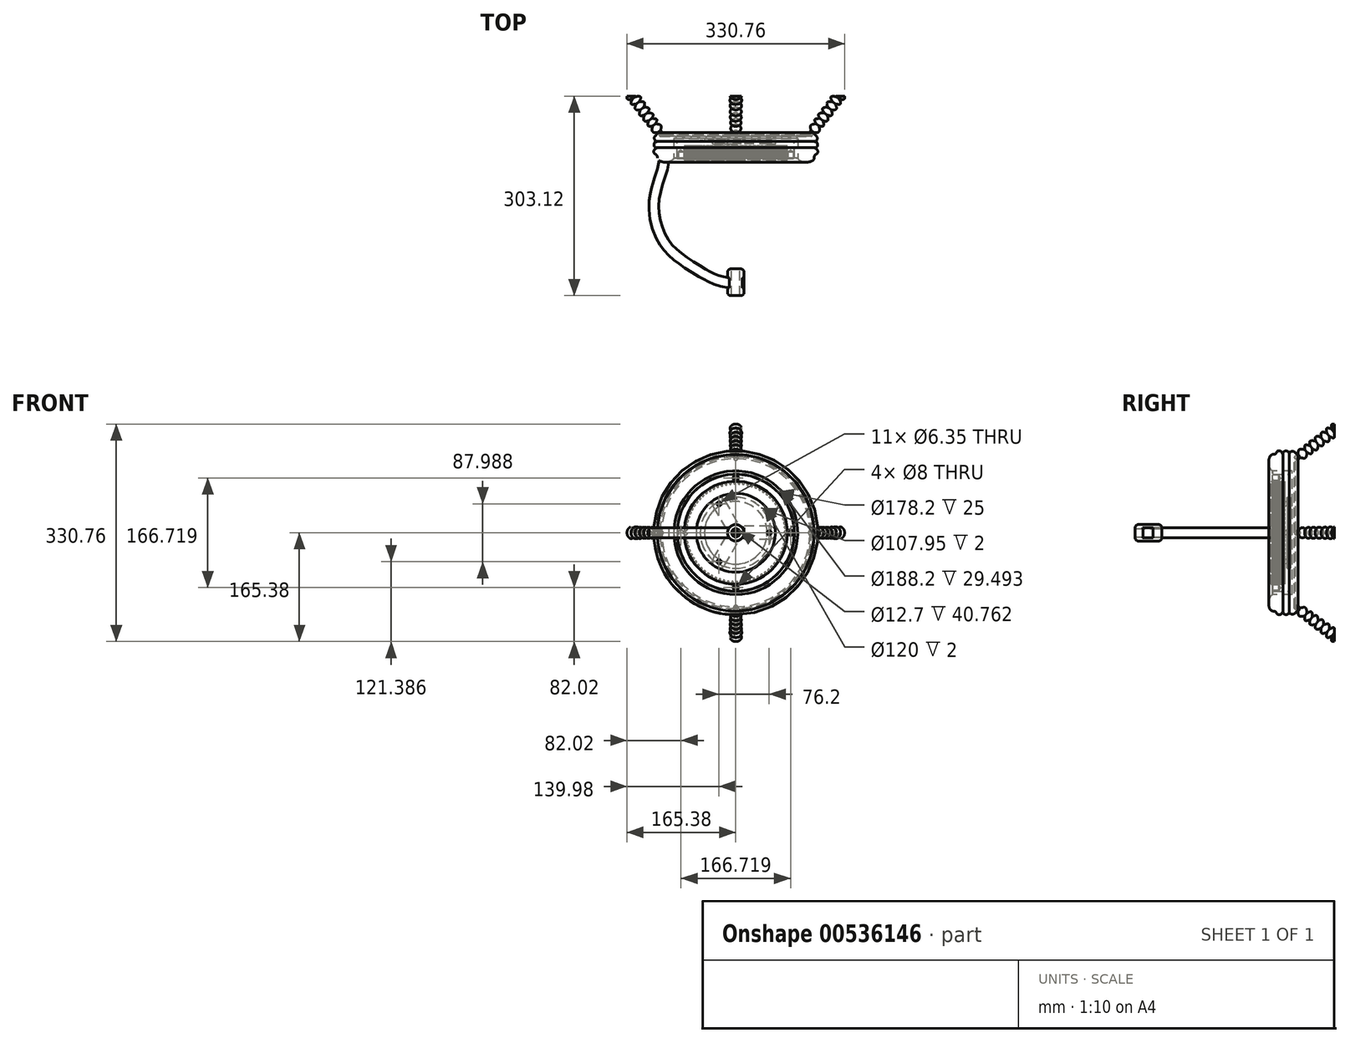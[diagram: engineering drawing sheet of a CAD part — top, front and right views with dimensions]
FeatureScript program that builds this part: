
annotation { "Feature Type Name" : "Feature", "Feature Type Description" : "" }
export const myFeature = defineFeature(function(context is Context, id is Id, definition is map)
    precondition{}
    {
        {
            var Q0;
            Q0=qCreatedBy(makeId("Front.planeOp"),FACE);
            var sketch = newSketch(context, id + "F0", { "sketchPlane" : qUnion([Q0])});
            skArc(sketch, "E0", {"start": v(-4.1, 78.2) * mm, "mid": v(-5.07, 78.15) * mm, "end": v(-6.03, 78.08) * mm});
            skArc(sketch, "E1.MirrorCS", {"start": v(-0.05, 76.06) * mm, "mid": v(-0.38, 75.29) * mm, "end": v(-0.74, 74.53) * mm});
            skLineSegment(sketch, "E2.MirrorCS", {"start": v(0, 76.35) * mm, "end": v(0, 77.53) * mm});
            skLineSegment(sketch, "E3.MirrorCS", {"start": v(-1.45, 74.1) * mm, "end": v(-1.7, 74.1) * mm});
            skLineSegment(sketch, "E4.MirrorCS", {"start": v(-1.97, 74.1) * mm, "end": v(-1.7, 74.1) * mm});
            skArc(sketch, "E5.MirrorCS", {"start": v(-3.28, 76.13) * mm, "mid": v(-2.99, 75.34) * mm, "end": v(-2.66, 74.57) * mm});
            skLineSegment(sketch, "E6.MirrorCS", {"start": v(-3.32, 76.42) * mm, "end": v(-3.28, 77.39) * mm});
            skPoint(sketch, "E7.end.orphan", {"position": v(-1.7, 78.3) * mm});
            skPoint(sketch, "E7.start.orphan", {"position": v(-0.96, 78.31) * mm});
            skPoint(sketch, "E8.MirrorCS.start.orphan", {"position": v(-2.45, 78.28) * mm});
            skPoint(sketch, "E9.orphan", {"position": v(-3.32, 76.13) * mm});
            skPoint(sketch, "E10.MirrorCS.end.orphan", {"position": v(-3.2, 73.49) * mm});
            skPoint(sketch, "E11.end.orphan", {"position": v(0, 73.56) * mm});
            skPoint(sketch, "E12.orphan", {"position": v(-3.2, 78.91) * mm});
            skPoint(sketch, "E13.orphan", {"position": v(0, 78.84) * mm});
            skPoint(sketch, "E14.start.orphan", {"position": v(0, 76.2) * mm});
            skPoint(sketch, "E15.visualSharp", {"position": v(-2.45, 74.12) * mm});
            skArc(sketch, "E15.filletArc", {"start": v(-2.48, 74.18) * mm, "mid": v(-2.44, 74.14) * mm, "end": v(-2.4, 74.12) * mm});
            skArc(sketch, "E16.filletArc", {"start": v(-0.05, 76.06) * mm, "mid": v(-0.01, 76.2) * mm, "end": v(0, 76.35) * mm});
            skPoint(sketch, "E17.visualSharp", {"position": v(-3.32, 76.27) * mm});
            skArc(sketch, "E17.filletArc", {"start": v(-3.32, 76.42) * mm, "mid": v(-3.3, 76.27) * mm, "end": v(-3.28, 76.13) * mm});
            skPoint(sketch, "E18.visualSharp", {"position": v(-0.96, 74.09) * mm});
            skArc(sketch, "E18.filletArc", {"start": v(-1.45, 74.1) * mm, "mid": v(-1.03, 74.21) * mm, "end": v(-0.74, 74.53) * mm});
            skArc(sketch, "E19.filletArc", {"start": v(-2.66, 74.57) * mm, "mid": v(-2.38, 74.24) * mm, "end": v(-1.97, 74.1) * mm});
            skPoint(sketch, "E20.visualSharp", {"position": v(-3.24, 78.25) * mm});
            skArc(sketch, "E20.filletArc", {"start": v(-3.28, 77.39) * mm, "mid": v(-3.5, 77.98) * mm, "end": v(-4.1, 78.2) * mm});
            skPoint(sketch, "E21.visualSharp", {"position": v(0, 78.32) * mm});
            skArc(sketch, "E21.filletArc", {"start": v(0.8, 78.31) * mm, "mid": v(0.23, 78.08) * mm, "end": v(0, 77.53) * mm});
            skCircle(sketch, "E22", {"center": v(0, 0) * mm, "radius": 88.9 * mm});
            skArc(sketch, "E23.1.0", {"start": v(-10, 76.8) * mm, "mid": v(-10.3, 77.38) * mm, "end": v(-10.9, 77.55) * mm});
            skLineSegment(sketch, "E23.1.1", {"start": v(-9.97, 75.84) * mm, "end": v(-10, 76.8) * mm});
            skArc(sketch, "E23.1.2", {"start": v(-9.97, 75.84) * mm, "mid": v(-9.94, 75.7) * mm, "end": v(-9.9, 75.55) * mm});
            skArc(sketch, "E23.1.3", {"start": v(-9.9, 75.55) * mm, "mid": v(-9.54, 74.8) * mm, "end": v(-9.15, 74.06) * mm});
            skArc(sketch, "E23.1.4", {"start": v(-9.15, 74.06) * mm, "mid": v(-8.84, 73.75) * mm, "end": v(-8.42, 73.65) * mm});
            skLineSegment(sketch, "E23.1.5", {"start": v(-8.42, 73.65) * mm, "end": v(-8.16, 73.67) * mm});
            skLineSegment(sketch, "E23.1.6", {"start": v(-7.9, 73.69) * mm, "end": v(-8.16, 73.67) * mm});
            skArc(sketch, "E23.1.7", {"start": v(-7.9, 73.69) * mm, "mid": v(-7.5, 73.84) * mm, "end": v(-7.23, 74.18) * mm});
            skArc(sketch, "E23.1.8", {"start": v(-6.68, 75.77) * mm, "mid": v(-6.94, 74.97) * mm, "end": v(-7.23, 74.18) * mm});
            skArc(sketch, "E23.1.9", {"start": v(-6.68, 75.77) * mm, "mid": v(-6.66, 75.9) * mm, "end": v(-6.65, 76.06) * mm});
            skLineSegment(sketch, "E23.1.10", {"start": v(-6.65, 76.06) * mm, "end": v(-6.76, 77.23) * mm});
            skArc(sketch, "E23.1.11", {"start": v(-6.03, 78.08) * mm, "mid": v(-6.57, 77.8) * mm, "end": v(-6.76, 77.23) * mm});
            skArc(sketch, "E23.2.0", {"start": v(-16.66, 75.64) * mm, "mid": v(-17, 76.19) * mm, "end": v(-17.62, 76.3) * mm});
            skLineSegment(sketch, "E23.2.1", {"start": v(-16.54, 74.68) * mm, "end": v(-16.66, 75.64) * mm});
            skArc(sketch, "E23.2.2", {"start": v(-16.54, 74.68) * mm, "mid": v(-16.5, 74.54) * mm, "end": v(-16.45, 74.4) * mm});
            skArc(sketch, "E23.2.3", {"start": v(-16.45, 74.4) * mm, "mid": v(-16.02, 73.68) * mm, "end": v(-15.57, 72.98) * mm});
            skArc(sketch, "E23.2.4", {"start": v(-15.57, 72.98) * mm, "mid": v(-15.24, 72.7) * mm, "end": v(-14.8, 72.64) * mm});
            skLineSegment(sketch, "E23.2.5", {"start": v(-14.8, 72.64) * mm, "end": v(-14.55, 72.68) * mm});
            skLineSegment(sketch, "E23.2.6", {"start": v(-14.3, 72.72) * mm, "end": v(-14.55, 72.68) * mm});
            skArc(sketch, "E23.2.7", {"start": v(-14.3, 72.72) * mm, "mid": v(-13.9, 72.9) * mm, "end": v(-13.67, 73.27) * mm});
            skArc(sketch, "E23.2.8", {"start": v(-13.26, 74.9) * mm, "mid": v(-13.45, 74.08) * mm, "end": v(-13.67, 73.27) * mm});
            skArc(sketch, "E23.2.9", {"start": v(-13.26, 74.9) * mm, "mid": v(-13.25, 75.04) * mm, "end": v(-13.26, 75.19) * mm});
            skLineSegment(sketch, "E23.2.10", {"start": v(-13.26, 75.19) * mm, "end": v(-13.46, 76.35) * mm});
            skArc(sketch, "E23.2.11", {"start": v(-12.82, 77.26) * mm, "mid": v(-13.33, 76.94) * mm, "end": v(-13.46, 76.35) * mm});
            skArc(sketch, "E23.3.0", {"start": v(-23.2, 73.9) * mm, "mid": v(-23.57, 74.42) * mm, "end": v(-24.2, 74.48) * mm});
            skLineSegment(sketch, "E23.3.1", {"start": v(-22.98, 72.96) * mm, "end": v(-23.2, 73.9) * mm});
            skArc(sketch, "E23.3.2", {"start": v(-22.98, 72.96) * mm, "mid": v(-22.94, 72.82) * mm, "end": v(-22.87, 72.69) * mm});
            skArc(sketch, "E23.3.3", {"start": v(-22.87, 72.69) * mm, "mid": v(-22.38, 72) * mm, "end": v(-21.87, 71.34) * mm});
            skArc(sketch, "E23.3.4", {"start": v(-21.87, 71.34) * mm, "mid": v(-21.52, 71.1) * mm, "end": v(-21.08, 71.07) * mm});
            skLineSegment(sketch, "E23.3.5", {"start": v(-21.08, 71.07) * mm, "end": v(-20.83, 71.13) * mm});
            skLineSegment(sketch, "E23.3.6", {"start": v(-20.58, 71.2) * mm, "end": v(-20.83, 71.13) * mm});
            skArc(sketch, "E23.3.7", {"start": v(-20.58, 71.2) * mm, "mid": v(-20.2, 71.42) * mm, "end": v(-20, 71.8) * mm});
            skArc(sketch, "E23.3.8", {"start": v(-19.74, 73.45) * mm, "mid": v(-19.85, 72.62) * mm, "end": v(-20, 71.8) * mm});
            skArc(sketch, "E23.3.9", {"start": v(-19.74, 73.45) * mm, "mid": v(-19.74, 73.6) * mm, "end": v(-19.76, 73.75) * mm});
            skLineSegment(sketch, "E23.3.10", {"start": v(-19.76, 73.75) * mm, "end": v(-20.07, 74.88) * mm});
            skArc(sketch, "E23.3.11", {"start": v(-19.5, 75.85) * mm, "mid": v(-19.98, 75.48) * mm, "end": v(-20.07, 74.88) * mm});
            skArc(sketch, "E23.4.0", {"start": v(-29.55, 71.6) * mm, "mid": v(-29.97, 72.08) * mm, "end": v(-30.6, 72.09) * mm});
            skLineSegment(sketch, "E23.4.1", {"start": v(-29.25, 70.68) * mm, "end": v(-29.55, 71.6) * mm});
            skArc(sketch, "E23.4.2", {"start": v(-29.25, 70.68) * mm, "mid": v(-29.2, 70.54) * mm, "end": v(-29.12, 70.42) * mm});
            skArc(sketch, "E23.4.3", {"start": v(-29.12, 70.42) * mm, "mid": v(-28.57, 69.78) * mm, "end": v(-28, 69.17) * mm});
            skArc(sketch, "E23.4.4", {"start": v(-28, 69.17) * mm, "mid": v(-27.63, 68.95) * mm, "end": v(-27.2, 68.96) * mm});
            skLineSegment(sketch, "E23.4.5", {"start": v(-27.2, 68.96) * mm, "end": v(-26.95, 69.05) * mm});
            skLineSegment(sketch, "E23.4.6", {"start": v(-26.7, 69.13) * mm, "end": v(-26.95, 69.05) * mm});
            skArc(sketch, "E23.4.7", {"start": v(-26.7, 69.13) * mm, "mid": v(-26.35, 69.38) * mm, "end": v(-26.18, 69.78) * mm});
            skArc(sketch, "E23.4.8", {"start": v(-26.07, 71.45) * mm, "mid": v(-26.1, 70.62) * mm, "end": v(-26.18, 69.78) * mm});
            skArc(sketch, "E23.4.9", {"start": v(-26.07, 71.45) * mm, "mid": v(-26.08, 71.6) * mm, "end": v(-26.11, 71.74) * mm});
            skLineSegment(sketch, "E23.4.10", {"start": v(-26.11, 71.74) * mm, "end": v(-26.52, 72.85) * mm});
            skArc(sketch, "E23.4.11", {"start": v(-26.04, 73.86) * mm, "mid": v(-26.49, 73.46) * mm, "end": v(-26.52, 72.85) * mm});
            skArc(sketch, "E23.5.0", {"start": v(-35.67, 68.75) * mm, "mid": v(-36.14, 69.2) * mm, "end": v(-36.77, 69.15) * mm});
            skLineSegment(sketch, "E23.5.1", {"start": v(-35.3, 67.86) * mm, "end": v(-35.67, 68.75) * mm});
            skArc(sketch, "E23.5.2", {"start": v(-35.3, 67.86) * mm, "mid": v(-35.23, 67.73) * mm, "end": v(-35.14, 67.61) * mm});
            skArc(sketch, "E23.5.3", {"start": v(-35.14, 67.61) * mm, "mid": v(-34.55, 67.02) * mm, "end": v(-33.93, 66.46) * mm});
            skArc(sketch, "E23.5.4", {"start": v(-33.93, 66.46) * mm, "mid": v(-33.53, 66.28) * mm, "end": v(-33.1, 66.33) * mm});
            skLineSegment(sketch, "E23.5.5", {"start": v(-33.1, 66.33) * mm, "end": v(-32.86, 66.43) * mm});
            skLineSegment(sketch, "E23.5.6", {"start": v(-32.63, 66.54) * mm, "end": v(-32.86, 66.43) * mm});
            skArc(sketch, "E23.5.7", {"start": v(-32.63, 66.54) * mm, "mid": v(-32.3, 66.82) * mm, "end": v(-32.16, 67.24) * mm});
            skArc(sketch, "E23.5.8", {"start": v(-32.2, 68.91) * mm, "mid": v(-32.16, 68.07) * mm, "end": v(-32.16, 67.24) * mm});
            skArc(sketch, "E23.5.9", {"start": v(-32.2, 68.91) * mm, "mid": v(-32.22, 69.06) * mm, "end": v(-32.27, 69.2) * mm});
            skLineSegment(sketch, "E23.5.10", {"start": v(-32.27, 69.2) * mm, "end": v(-32.76, 70.26) * mm});
            skArc(sketch, "E23.5.11", {"start": v(-32.38, 71.31) * mm, "mid": v(-32.79, 70.87) * mm, "end": v(-32.76, 70.26) * mm});
            skArc(sketch, "E23.6.0", {"start": v(-41.53, 65.38) * mm, "mid": v(-42.03, 65.78) * mm, "end": v(-42.66, 65.68) * mm});
            skLineSegment(sketch, "E23.6.1", {"start": v(-41.08, 64.52) * mm, "end": v(-41.53, 65.38) * mm});
            skArc(sketch, "E23.6.2", {"start": v(-41.08, 64.52) * mm, "mid": v(-41, 64.4) * mm, "end": v(-40.9, 64.3) * mm});
            skArc(sketch, "E23.6.3", {"start": v(-40.9, 64.3) * mm, "mid": v(-40.26, 63.76) * mm, "end": v(-39.6, 63.25) * mm});
            skArc(sketch, "E23.6.4", {"start": v(-39.6, 63.25) * mm, "mid": v(-39.18, 63.1) * mm, "end": v(-38.76, 63.2) * mm});
            skLineSegment(sketch, "E23.6.5", {"start": v(-38.76, 63.2) * mm, "end": v(-38.53, 63.32) * mm});
            skLineSegment(sketch, "E23.6.6", {"start": v(-38.3, 63.44) * mm, "end": v(-38.53, 63.32) * mm});
            skArc(sketch, "E23.6.7", {"start": v(-38.3, 63.44) * mm, "mid": v(-38, 63.75) * mm, "end": v(-37.9, 64.18) * mm});
            skArc(sketch, "E23.6.8", {"start": v(-38.08, 65.84) * mm, "mid": v(-37.97, 65.01) * mm, "end": v(-37.9, 64.18) * mm});
            skArc(sketch, "E23.6.9", {"start": v(-38.08, 65.84) * mm, "mid": v(-38.11, 65.99) * mm, "end": v(-38.17, 66.12) * mm});
            skLineSegment(sketch, "E23.6.10", {"start": v(-38.17, 66.12) * mm, "end": v(-38.76, 67.14) * mm});
            skArc(sketch, "E23.6.11", {"start": v(-38.47, 68.22) * mm, "mid": v(-38.84, 67.74) * mm, "end": v(-38.76, 67.14) * mm});
            skArc(sketch, "E23.7.0", {"start": v(-47.07, 61.51) * mm, "mid": v(-47.6, 61.87) * mm, "end": v(-48.22, 61.71) * mm});
            skLineSegment(sketch, "E23.7.1", {"start": v(-46.55, 60.7) * mm, "end": v(-47.07, 61.51) * mm});
            skArc(sketch, "E23.7.2", {"start": v(-46.55, 60.7) * mm, "mid": v(-46.46, 60.58) * mm, "end": v(-46.35, 60.48) * mm});
            skArc(sketch, "E23.7.3", {"start": v(-46.35, 60.48) * mm, "mid": v(-45.66, 60) * mm, "end": v(-44.95, 59.56) * mm});
            skArc(sketch, "E23.7.4", {"start": v(-44.95, 59.56) * mm, "mid": v(-44.53, 59.45) * mm, "end": v(-44.12, 59.58) * mm});
            skLineSegment(sketch, "E23.7.5", {"start": v(-44.12, 59.58) * mm, "end": v(-43.9, 59.72) * mm});
            skLineSegment(sketch, "E23.7.6", {"start": v(-43.69, 59.86) * mm, "end": v(-43.9, 59.72) * mm});
            skArc(sketch, "E23.7.7", {"start": v(-43.69, 59.86) * mm, "mid": v(-43.4, 60.2) * mm, "end": v(-43.35, 60.63) * mm});
            skArc(sketch, "E23.7.8", {"start": v(-43.67, 62.27) * mm, "mid": v(-43.5, 61.46) * mm, "end": v(-43.35, 60.63) * mm});
            skArc(sketch, "E23.7.9", {"start": v(-43.67, 62.27) * mm, "mid": v(-43.72, 62.41) * mm, "end": v(-43.8, 62.54) * mm});
            skLineSegment(sketch, "E23.7.10", {"start": v(-43.8, 62.54) * mm, "end": v(-44.47, 63.5) * mm});
            skArc(sketch, "E23.7.11", {"start": v(-44.27, 64.6) * mm, "mid": v(-44.6, 64.1) * mm, "end": v(-44.47, 63.5) * mm});
            skArc(sketch, "E23.8.0", {"start": v(-52.25, 57.18) * mm, "mid": v(-52.81, 57.48) * mm, "end": v(-53.41, 57.27) * mm});
            skLineSegment(sketch, "E23.8.1", {"start": v(-51.66, 56.4) * mm, "end": v(-52.25, 57.18) * mm});
            skArc(sketch, "E23.8.2", {"start": v(-51.66, 56.4) * mm, "mid": v(-51.56, 56.3) * mm, "end": v(-51.44, 56.21) * mm});
            skArc(sketch, "E23.8.3", {"start": v(-51.44, 56.21) * mm, "mid": v(-50.72, 55.8) * mm, "end": v(-49.97, 55.42) * mm});
            skArc(sketch, "E23.8.4", {"start": v(-49.97, 55.42) * mm, "mid": v(-49.54, 55.34) * mm, "end": v(-49.14, 55.5) * mm});
            skLineSegment(sketch, "E23.8.5", {"start": v(-49.14, 55.5) * mm, "end": v(-48.94, 55.66) * mm});
            skLineSegment(sketch, "E23.8.6", {"start": v(-48.74, 55.83) * mm, "end": v(-48.94, 55.66) * mm});
            skArc(sketch, "E23.8.7", {"start": v(-48.74, 55.83) * mm, "mid": v(-48.5, 56.19) * mm, "end": v(-48.47, 56.62) * mm});
            skArc(sketch, "E23.8.8", {"start": v(-48.93, 58.23) * mm, "mid": v(-48.68, 57.43) * mm, "end": v(-48.47, 56.62) * mm});
            skArc(sketch, "E23.8.9", {"start": v(-48.93, 58.23) * mm, "mid": v(-49, 58.36) * mm, "end": v(-49.08, 58.49) * mm});
            skLineSegment(sketch, "E23.8.10", {"start": v(-49.08, 58.49) * mm, "end": v(-49.83, 59.39) * mm});
            skArc(sketch, "E23.8.11", {"start": v(-49.73, 60.5) * mm, "mid": v(-50.01, 59.97) * mm, "end": v(-49.83, 59.39) * mm});
            skArc(sketch, "E23.9.0", {"start": v(-57.04, 52.4) * mm, "mid": v(-57.62, 52.66) * mm, "end": v(-58.2, 52.4) * mm});
            skLineSegment(sketch, "E23.9.1", {"start": v(-56.38, 51.7) * mm, "end": v(-57.04, 52.4) * mm});
            skArc(sketch, "E23.9.2", {"start": v(-56.38, 51.7) * mm, "mid": v(-56.27, 51.6) * mm, "end": v(-56.15, 51.52) * mm});
            skArc(sketch, "E23.9.3", {"start": v(-56.15, 51.52) * mm, "mid": v(-55.39, 51.17) * mm, "end": v(-54.61, 50.85) * mm});
            skArc(sketch, "E23.9.4", {"start": v(-54.61, 50.85) * mm, "mid": v(-54.18, 50.81) * mm, "end": v(-53.8, 51.01) * mm});
            skLineSegment(sketch, "E23.9.5", {"start": v(-53.8, 51.01) * mm, "end": v(-53.6, 51.19) * mm});
            skLineSegment(sketch, "E23.9.6", {"start": v(-53.42, 51.37) * mm, "end": v(-53.6, 51.19) * mm});
            skArc(sketch, "E23.9.7", {"start": v(-53.42, 51.37) * mm, "mid": v(-53.2, 51.75) * mm, "end": v(-53.22, 52.18) * mm});
            skArc(sketch, "E23.9.8", {"start": v(-53.82, 53.74) * mm, "mid": v(-53.5, 52.97) * mm, "end": v(-53.22, 52.18) * mm});
            skArc(sketch, "E23.9.9", {"start": v(-53.82, 53.74) * mm, "mid": v(-53.9, 53.87) * mm, "end": v(-53.99, 53.99) * mm});
            skLineSegment(sketch, "E23.9.10", {"start": v(-53.99, 53.99) * mm, "end": v(-54.82, 54.82) * mm});
            skArc(sketch, "E23.9.11", {"start": v(-54.81, 55.94) * mm, "mid": v(-55.05, 55.38) * mm, "end": v(-54.82, 54.82) * mm});
            skArc(sketch, "E23.10.0", {"start": v(-61.39, 47.24) * mm, "mid": v(-62, 47.44) * mm, "end": v(-62.55, 47.13) * mm});
            skLineSegment(sketch, "E23.10.1", {"start": v(-60.67, 46.58) * mm, "end": v(-61.39, 47.24) * mm});
            skArc(sketch, "E23.10.2", {"start": v(-60.67, 46.58) * mm, "mid": v(-60.56, 46.5) * mm, "end": v(-60.42, 46.43) * mm});
            skArc(sketch, "E23.10.3", {"start": v(-60.42, 46.43) * mm, "mid": v(-59.64, 46.14) * mm, "end": v(-58.84, 45.9) * mm});
            skArc(sketch, "E23.10.4", {"start": v(-58.84, 45.9) * mm, "mid": v(-58.4, 45.9) * mm, "end": v(-58.03, 46.13) * mm});
            skLineSegment(sketch, "E23.10.5", {"start": v(-58.03, 46.13) * mm, "end": v(-57.86, 46.32) * mm});
            skLineSegment(sketch, "E23.10.6", {"start": v(-57.7, 46.52) * mm, "end": v(-57.86, 46.32) * mm});
            skArc(sketch, "E23.10.7", {"start": v(-57.7, 46.52) * mm, "mid": v(-57.51, 46.91) * mm, "end": v(-57.57, 47.34) * mm});
            skArc(sketch, "E23.10.8", {"start": v(-58.3, 48.85) * mm, "mid": v(-57.92, 48.1) * mm, "end": v(-57.57, 47.34) * mm});
            skArc(sketch, "E23.10.9", {"start": v(-58.3, 48.85) * mm, "mid": v(-58.38, 48.97) * mm, "end": v(-58.49, 49.08) * mm});
            skLineSegment(sketch, "E23.10.10", {"start": v(-58.49, 49.08) * mm, "end": v(-59.39, 49.83) * mm});
            skArc(sketch, "E23.10.11", {"start": v(-59.48, 50.95) * mm, "mid": v(-59.67, 50.37) * mm, "end": v(-59.39, 49.83) * mm});
            skArc(sketch, "E23.11.0", {"start": v(-65.27, 41.7) * mm, "mid": v(-65.9, 41.86) * mm, "end": v(-66.42, 41.5) * mm});
            skLineSegment(sketch, "E23.11.1", {"start": v(-64.5, 41.12) * mm, "end": v(-65.27, 41.7) * mm});
            skArc(sketch, "E23.11.2", {"start": v(-64.5, 41.12) * mm, "mid": v(-64.38, 41.04) * mm, "end": v(-64.24, 40.98) * mm});
            skArc(sketch, "E23.11.3", {"start": v(-64.24, 40.98) * mm, "mid": v(-63.43, 40.77) * mm, "end": v(-62.61, 40.6) * mm});
            skArc(sketch, "E23.11.4", {"start": v(-62.61, 40.6) * mm, "mid": v(-62.18, 40.63) * mm, "end": v(-61.83, 40.9) * mm});
            skLineSegment(sketch, "E23.11.5", {"start": v(-61.83, 40.9) * mm, "end": v(-61.68, 41.1) * mm});
            skLineSegment(sketch, "E23.11.6", {"start": v(-61.53, 41.31) * mm, "end": v(-61.68, 41.1) * mm});
            skArc(sketch, "E23.11.7", {"start": v(-61.53, 41.31) * mm, "mid": v(-61.38, 41.72) * mm, "end": v(-61.47, 42.15) * mm});
            skArc(sketch, "E23.11.8", {"start": v(-62.34, 43.58) * mm, "mid": v(-61.89, 42.87) * mm, "end": v(-61.47, 42.15) * mm});
            skArc(sketch, "E23.11.9", {"start": v(-62.34, 43.58) * mm, "mid": v(-62.43, 43.7) * mm, "end": v(-62.54, 43.8) * mm});
            skLineSegment(sketch, "E23.11.10", {"start": v(-62.54, 43.8) * mm, "end": v(-63.5, 44.47) * mm});
            skArc(sketch, "E23.11.11", {"start": v(-63.7, 45.57) * mm, "mid": v(-63.83, 44.98) * mm, "end": v(-63.5, 44.47) * mm});
            skArc(sketch, "E23.12.0", {"start": v(-68.66, 35.86) * mm, "mid": v(-69.29, 35.95) * mm, "end": v(-69.78, 35.55) * mm});
            skLineSegment(sketch, "E23.12.1", {"start": v(-67.84, 35.34) * mm, "end": v(-68.66, 35.86) * mm});
            skArc(sketch, "E23.12.2", {"start": v(-67.84, 35.34) * mm, "mid": v(-67.7, 35.27) * mm, "end": v(-67.57, 35.23) * mm});
            skArc(sketch, "E23.12.3", {"start": v(-67.57, 35.23) * mm, "mid": v(-66.74, 35.09) * mm, "end": v(-65.91, 34.98) * mm});
            skArc(sketch, "E23.12.4", {"start": v(-65.91, 34.98) * mm, "mid": v(-65.48, 35.06) * mm, "end": v(-65.16, 35.35) * mm});
            skLineSegment(sketch, "E23.12.5", {"start": v(-65.16, 35.35) * mm, "end": v(-65.03, 35.57) * mm});
            skLineSegment(sketch, "E23.12.6", {"start": v(-64.9, 35.8) * mm, "end": v(-65.03, 35.57) * mm});
            skArc(sketch, "E23.12.7", {"start": v(-64.9, 35.8) * mm, "mid": v(-64.78, 36.21) * mm, "end": v(-64.91, 36.63) * mm});
            skArc(sketch, "E23.12.8", {"start": v(-65.9, 37.98) * mm, "mid": v(-65.4, 37.32) * mm, "end": v(-64.91, 36.63) * mm});
            skArc(sketch, "E23.12.9", {"start": v(-65.9, 37.98) * mm, "mid": v(-66, 38.09) * mm, "end": v(-66.12, 38.17) * mm});
            skLineSegment(sketch, "E23.12.10", {"start": v(-66.12, 38.17) * mm, "end": v(-67.14, 38.76) * mm});
            skArc(sketch, "E23.12.11", {"start": v(-67.42, 39.85) * mm, "mid": v(-67.5, 39.24) * mm, "end": v(-67.14, 38.76) * mm});
            skArc(sketch, "E23.13.0", {"start": v(-71.52, 29.74) * mm, "mid": v(-72.16, 29.78) * mm, "end": v(-72.62, 29.33) * mm});
            skLineSegment(sketch, "E23.13.1", {"start": v(-70.66, 29.3) * mm, "end": v(-71.52, 29.74) * mm});
            skArc(sketch, "E23.13.2", {"start": v(-70.66, 29.3) * mm, "mid": v(-70.53, 29.23) * mm, "end": v(-70.38, 29.2) * mm});
            skArc(sketch, "E23.13.3", {"start": v(-70.38, 29.2) * mm, "mid": v(-69.55, 29.14) * mm, "end": v(-68.71, 29.1) * mm});
            skArc(sketch, "E23.13.4", {"start": v(-68.71, 29.1) * mm, "mid": v(-68.3, 29.22) * mm, "end": v(-68, 29.54) * mm});
            skLineSegment(sketch, "E23.13.5", {"start": v(-68, 29.54) * mm, "end": v(-67.88, 29.77) * mm});
            skLineSegment(sketch, "E23.13.6", {"start": v(-67.77, 30) * mm, "end": v(-67.88, 29.77) * mm});
            skArc(sketch, "E23.13.7", {"start": v(-67.77, 30) * mm, "mid": v(-67.7, 30.43) * mm, "end": v(-67.86, 30.83) * mm});
            skArc(sketch, "E23.13.8", {"start": v(-68.96, 32.1) * mm, "mid": v(-68.4, 31.48) * mm, "end": v(-67.86, 30.83) * mm});
            skArc(sketch, "E23.13.9", {"start": v(-68.96, 32.1) * mm, "mid": v(-69.07, 32.2) * mm, "end": v(-69.2, 32.27) * mm});
            skLineSegment(sketch, "E23.13.10", {"start": v(-69.2, 32.27) * mm, "end": v(-70.26, 32.76) * mm});
            skArc(sketch, "E23.13.11", {"start": v(-70.64, 33.82) * mm, "mid": v(-70.67, 33.21) * mm, "end": v(-70.26, 32.76) * mm});
            skArc(sketch, "E23.14.0", {"start": v(-73.84, 23.4) * mm, "mid": v(-74.48, 23.38) * mm, "end": v(-74.9, 22.9) * mm});
            skLineSegment(sketch, "E23.14.1", {"start": v(-72.95, 23.02) * mm, "end": v(-73.84, 23.4) * mm});
            skArc(sketch, "E23.14.2", {"start": v(-72.95, 23.02) * mm, "mid": v(-72.8, 22.98) * mm, "end": v(-72.66, 22.96) * mm});
            skArc(sketch, "E23.14.3", {"start": v(-72.66, 22.96) * mm, "mid": v(-71.82, 22.96) * mm, "end": v(-70.99, 23) * mm});
            skArc(sketch, "E23.14.4", {"start": v(-70.99, 23) * mm, "mid": v(-70.58, 23.15) * mm, "end": v(-70.31, 23.5) * mm});
            skLineSegment(sketch, "E23.14.5", {"start": v(-70.31, 23.5) * mm, "end": v(-70.21, 23.74) * mm});
            skLineSegment(sketch, "E23.14.6", {"start": v(-70.12, 23.98) * mm, "end": v(-70.21, 23.74) * mm});
            skArc(sketch, "E23.14.7", {"start": v(-70.12, 23.98) * mm, "mid": v(-70.09, 24.41) * mm, "end": v(-70.29, 24.8) * mm});
            skArc(sketch, "E23.14.8", {"start": v(-71.5, 25.96) * mm, "mid": v(-70.88, 25.4) * mm, "end": v(-70.29, 24.8) * mm});
            skArc(sketch, "E23.14.9", {"start": v(-71.5, 25.96) * mm, "mid": v(-71.61, 26.05) * mm, "end": v(-71.74, 26.11) * mm});
            skLineSegment(sketch, "E23.14.10", {"start": v(-71.74, 26.11) * mm, "end": v(-72.85, 26.52) * mm});
            skArc(sketch, "E23.14.11", {"start": v(-73.32, 27.53) * mm, "mid": v(-73.3, 26.93) * mm, "end": v(-72.85, 26.52) * mm});
            skArc(sketch, "E23.15.0", {"start": v(-75.6, 16.87) * mm, "mid": v(-76.23, 16.8) * mm, "end": v(-76.6, 16.28) * mm});
            skLineSegment(sketch, "E23.15.1", {"start": v(-74.67, 16.57) * mm, "end": v(-75.6, 16.87) * mm});
            skArc(sketch, "E23.15.2", {"start": v(-74.67, 16.57) * mm, "mid": v(-74.53, 16.54) * mm, "end": v(-74.38, 16.54) * mm});
            skArc(sketch, "E23.15.3", {"start": v(-74.38, 16.54) * mm, "mid": v(-73.55, 16.62) * mm, "end": v(-72.72, 16.73) * mm});
            skArc(sketch, "E23.15.4", {"start": v(-72.72, 16.73) * mm, "mid": v(-72.33, 16.91) * mm, "end": v(-72.1, 17.28) * mm});
            skLineSegment(sketch, "E23.15.5", {"start": v(-72.1, 17.28) * mm, "end": v(-72.02, 17.53) * mm});
            skLineSegment(sketch, "E23.15.6", {"start": v(-71.95, 17.78) * mm, "end": v(-72.02, 17.53) * mm});
            skArc(sketch, "E23.15.7", {"start": v(-71.95, 17.78) * mm, "mid": v(-71.95, 18.21) * mm, "end": v(-72.18, 18.58) * mm});
            skArc(sketch, "E23.15.8", {"start": v(-73.48, 19.63) * mm, "mid": v(-72.82, 19.12) * mm, "end": v(-72.18, 18.58) * mm});
            skArc(sketch, "E23.15.9", {"start": v(-73.48, 19.63) * mm, "mid": v(-73.6, 19.7) * mm, "end": v(-73.75, 19.76) * mm});
            skLineSegment(sketch, "E23.15.10", {"start": v(-73.75, 19.76) * mm, "end": v(-74.88, 20.07) * mm});
            skArc(sketch, "E23.15.11", {"start": v(-75.44, 21.04) * mm, "mid": v(-75.36, 20.44) * mm, "end": v(-74.88, 20.07) * mm});
            skArc(sketch, "E23.16.0", {"start": v(-76.78, 10.21) * mm, "mid": v(-77.4, 10.09) * mm, "end": v(-77.73, 9.54) * mm});
            skLineSegment(sketch, "E23.16.1", {"start": v(-75.84, 10) * mm, "end": v(-76.78, 10.21) * mm});
            skArc(sketch, "E23.16.2", {"start": v(-75.84, 10) * mm, "mid": v(-75.69, 9.98) * mm, "end": v(-75.54, 10) * mm});
            skArc(sketch, "E23.16.3", {"start": v(-75.54, 10) * mm, "mid": v(-74.72, 10.14) * mm, "end": v(-73.9, 10.33) * mm});
            skArc(sketch, "E23.16.4", {"start": v(-73.9, 10.33) * mm, "mid": v(-73.53, 10.55) * mm, "end": v(-73.32, 10.93) * mm});
            skLineSegment(sketch, "E23.16.5", {"start": v(-73.32, 10.93) * mm, "end": v(-73.27, 11.18) * mm});
            skLineSegment(sketch, "E23.16.6", {"start": v(-73.22, 11.44) * mm, "end": v(-73.27, 11.18) * mm});
            skArc(sketch, "E23.16.7", {"start": v(-73.22, 11.44) * mm, "mid": v(-73.26, 11.87) * mm, "end": v(-73.53, 12.22) * mm});
            skArc(sketch, "E23.16.8", {"start": v(-74.91, 13.15) * mm, "mid": v(-74.2, 12.7) * mm, "end": v(-73.53, 12.22) * mm});
            skArc(sketch, "E23.16.9", {"start": v(-74.91, 13.15) * mm, "mid": v(-75.05, 13.22) * mm, "end": v(-75.19, 13.26) * mm});
            skLineSegment(sketch, "E23.16.10", {"start": v(-75.19, 13.26) * mm, "end": v(-76.35, 13.46) * mm});
            skArc(sketch, "E23.16.11", {"start": v(-76.98, 14.38) * mm, "mid": v(-76.86, 13.79) * mm, "end": v(-76.35, 13.46) * mm});
            skArc(sketch, "E23.17.0", {"start": v(-77.38, 3.48) * mm, "mid": v(-78, 3.3) * mm, "end": v(-78.27, 2.73) * mm});
            skLineSegment(sketch, "E23.17.1", {"start": v(-76.42, 3.36) * mm, "end": v(-77.38, 3.48) * mm});
            skArc(sketch, "E23.17.2", {"start": v(-76.42, 3.36) * mm, "mid": v(-76.27, 3.35) * mm, "end": v(-76.13, 3.37) * mm});
            skArc(sketch, "E23.17.3", {"start": v(-76.13, 3.37) * mm, "mid": v(-75.32, 3.6) * mm, "end": v(-74.52, 3.85) * mm});
            skArc(sketch, "E23.17.4", {"start": v(-74.52, 3.85) * mm, "mid": v(-74.16, 4.1) * mm, "end": v(-74, 4.5) * mm});
            skLineSegment(sketch, "E23.17.5", {"start": v(-74, 4.5) * mm, "end": v(-73.97, 4.76) * mm});
            skLineSegment(sketch, "E23.17.6", {"start": v(-73.94, 5.01) * mm, "end": v(-73.97, 4.76) * mm});
            skArc(sketch, "E23.17.7", {"start": v(-73.94, 5.01) * mm, "mid": v(-74.02, 5.44) * mm, "end": v(-74.31, 5.76) * mm});
            skArc(sketch, "E23.17.8", {"start": v(-75.77, 6.57) * mm, "mid": v(-75.03, 6.18) * mm, "end": v(-74.31, 5.76) * mm});
            skArc(sketch, "E23.17.9", {"start": v(-75.77, 6.57) * mm, "mid": v(-75.91, 6.63) * mm, "end": v(-76.06, 6.65) * mm});
            skLineSegment(sketch, "E23.17.10", {"start": v(-76.06, 6.65) * mm, "end": v(-77.23, 6.76) * mm});
            skArc(sketch, "E23.17.11", {"start": v(-77.95, 7.62) * mm, "mid": v(-77.77, 7.04) * mm, "end": v(-77.23, 6.76) * mm});
            skArc(sketch, "E23.18.0", {"start": v(-77.39, -3.28) * mm, "mid": v(-77.98, -3.5) * mm, "end": v(-78.2, -4.1) * mm});
            skLineSegment(sketch, "E23.18.1", {"start": v(-76.42, -3.32) * mm, "end": v(-77.39, -3.28) * mm});
            skArc(sketch, "E23.18.2", {"start": v(-76.42, -3.32) * mm, "mid": v(-76.27, -3.3) * mm, "end": v(-76.13, -3.28) * mm});
            skArc(sketch, "E23.18.3", {"start": v(-76.13, -3.28) * mm, "mid": v(-75.34, -2.99) * mm, "end": v(-74.57, -2.66) * mm});
            skArc(sketch, "E23.18.4", {"start": v(-74.57, -2.66) * mm, "mid": v(-74.24, -2.38) * mm, "end": v(-74.1, -1.97) * mm});
            skLineSegment(sketch, "E23.18.5", {"start": v(-74.1, -1.97) * mm, "end": v(-74.1, -1.7) * mm});
            skLineSegment(sketch, "E23.18.6", {"start": v(-74.1, -1.45) * mm, "end": v(-74.1, -1.7) * mm});
            skArc(sketch, "E23.18.7", {"start": v(-74.1, -1.45) * mm, "mid": v(-74.21, -1.03) * mm, "end": v(-74.53, -0.74) * mm});
            skArc(sketch, "E23.18.8", {"start": v(-76.06, -0.05) * mm, "mid": v(-75.29, -0.38) * mm, "end": v(-74.53, -0.74) * mm});
            skArc(sketch, "E23.18.9", {"start": v(-76.06, -0.05) * mm, "mid": v(-76.2, -0.01) * mm, "end": v(-76.35, 0) * mm});
            skLineSegment(sketch, "E23.18.10", {"start": v(-76.35, 0) * mm, "end": v(-77.53, 0) * mm});
            skArc(sketch, "E23.18.11", {"start": v(-78.31, 0.8) * mm, "mid": v(-78.08, 0.23) * mm, "end": v(-77.53, 0) * mm});
            skArc(sketch, "E23.19.0", {"start": v(-76.8, -10) * mm, "mid": v(-77.38, -10.3) * mm, "end": v(-77.55, -10.9) * mm});
            skLineSegment(sketch, "E23.19.1", {"start": v(-75.84, -9.97) * mm, "end": v(-76.8, -10) * mm});
            skArc(sketch, "E23.19.2", {"start": v(-75.84, -9.97) * mm, "mid": v(-75.7, -9.94) * mm, "end": v(-75.55, -9.9) * mm});
            skArc(sketch, "E23.19.3", {"start": v(-75.55, -9.9) * mm, "mid": v(-74.8, -9.54) * mm, "end": v(-74.06, -9.15) * mm});
            skArc(sketch, "E23.19.4", {"start": v(-74.06, -9.15) * mm, "mid": v(-73.75, -8.84) * mm, "end": v(-73.65, -8.42) * mm});
            skLineSegment(sketch, "E23.19.5", {"start": v(-73.65, -8.42) * mm, "end": v(-73.67, -8.16) * mm});
            skLineSegment(sketch, "E23.19.6", {"start": v(-73.69, -7.9) * mm, "end": v(-73.67, -8.16) * mm});
            skArc(sketch, "E23.19.7", {"start": v(-73.69, -7.9) * mm, "mid": v(-73.84, -7.5) * mm, "end": v(-74.18, -7.23) * mm});
            skArc(sketch, "E23.19.8", {"start": v(-75.77, -6.68) * mm, "mid": v(-74.97, -6.94) * mm, "end": v(-74.18, -7.23) * mm});
            skArc(sketch, "E23.19.9", {"start": v(-75.77, -6.68) * mm, "mid": v(-75.9, -6.66) * mm, "end": v(-76.06, -6.65) * mm});
            skLineSegment(sketch, "E23.19.10", {"start": v(-76.06, -6.65) * mm, "end": v(-77.23, -6.76) * mm});
            skArc(sketch, "E23.19.11", {"start": v(-78.08, -6.03) * mm, "mid": v(-77.8, -6.57) * mm, "end": v(-77.23, -6.76) * mm});
            skArc(sketch, "E23.20.0", {"start": v(-75.64, -16.66) * mm, "mid": v(-76.19, -17) * mm, "end": v(-76.3, -17.62) * mm});
            skLineSegment(sketch, "E23.20.1", {"start": v(-74.68, -16.54) * mm, "end": v(-75.64, -16.66) * mm});
            skArc(sketch, "E23.20.2", {"start": v(-74.68, -16.54) * mm, "mid": v(-74.54, -16.5) * mm, "end": v(-74.4, -16.45) * mm});
            skArc(sketch, "E23.20.3", {"start": v(-74.4, -16.45) * mm, "mid": v(-73.68, -16.02) * mm, "end": v(-72.98, -15.57) * mm});
            skArc(sketch, "E23.20.4", {"start": v(-72.98, -15.57) * mm, "mid": v(-72.7, -15.24) * mm, "end": v(-72.64, -14.8) * mm});
            skLineSegment(sketch, "E23.20.5", {"start": v(-72.64, -14.8) * mm, "end": v(-72.68, -14.55) * mm});
            skLineSegment(sketch, "E23.20.6", {"start": v(-72.72, -14.3) * mm, "end": v(-72.68, -14.55) * mm});
            skArc(sketch, "E23.20.7", {"start": v(-72.72, -14.3) * mm, "mid": v(-72.9, -13.9) * mm, "end": v(-73.27, -13.67) * mm});
            skArc(sketch, "E23.20.8", {"start": v(-74.9, -13.26) * mm, "mid": v(-74.08, -13.45) * mm, "end": v(-73.27, -13.67) * mm});
            skArc(sketch, "E23.20.9", {"start": v(-74.9, -13.26) * mm, "mid": v(-75.04, -13.25) * mm, "end": v(-75.19, -13.26) * mm});
            skLineSegment(sketch, "E23.20.10", {"start": v(-75.19, -13.26) * mm, "end": v(-76.35, -13.46) * mm});
            skArc(sketch, "E23.20.11", {"start": v(-77.26, -12.82) * mm, "mid": v(-76.94, -13.33) * mm, "end": v(-76.35, -13.46) * mm});
            skArc(sketch, "E23.21.0", {"start": v(-73.9, -23.2) * mm, "mid": v(-74.42, -23.57) * mm, "end": v(-74.48, -24.2) * mm});
            skLineSegment(sketch, "E23.21.1", {"start": v(-72.96, -22.98) * mm, "end": v(-73.9, -23.2) * mm});
            skArc(sketch, "E23.21.2", {"start": v(-72.96, -22.98) * mm, "mid": v(-72.82, -22.94) * mm, "end": v(-72.69, -22.87) * mm});
            skArc(sketch, "E23.21.3", {"start": v(-72.69, -22.87) * mm, "mid": v(-72, -22.38) * mm, "end": v(-71.34, -21.87) * mm});
            skArc(sketch, "E23.21.4", {"start": v(-71.34, -21.87) * mm, "mid": v(-71.1, -21.52) * mm, "end": v(-71.07, -21.08) * mm});
            skLineSegment(sketch, "E23.21.5", {"start": v(-71.07, -21.08) * mm, "end": v(-71.13, -20.83) * mm});
            skLineSegment(sketch, "E23.21.6", {"start": v(-71.2, -20.58) * mm, "end": v(-71.13, -20.83) * mm});
            skArc(sketch, "E23.21.7", {"start": v(-71.2, -20.58) * mm, "mid": v(-71.42, -20.2) * mm, "end": v(-71.8, -20) * mm});
            skArc(sketch, "E23.21.8", {"start": v(-73.45, -19.74) * mm, "mid": v(-72.62, -19.85) * mm, "end": v(-71.8, -20) * mm});
            skArc(sketch, "E23.21.9", {"start": v(-73.45, -19.74) * mm, "mid": v(-73.6, -19.74) * mm, "end": v(-73.75, -19.76) * mm});
            skLineSegment(sketch, "E23.21.10", {"start": v(-73.75, -19.76) * mm, "end": v(-74.88, -20.07) * mm});
            skArc(sketch, "E23.21.11", {"start": v(-75.85, -19.5) * mm, "mid": v(-75.48, -19.98) * mm, "end": v(-74.88, -20.07) * mm});
            skArc(sketch, "E23.22.0", {"start": v(-71.6, -29.55) * mm, "mid": v(-72.08, -29.97) * mm, "end": v(-72.09, -30.6) * mm});
            skLineSegment(sketch, "E23.22.1", {"start": v(-70.68, -29.25) * mm, "end": v(-71.6, -29.55) * mm});
            skArc(sketch, "E23.22.2", {"start": v(-70.68, -29.25) * mm, "mid": v(-70.54, -29.2) * mm, "end": v(-70.42, -29.12) * mm});
            skArc(sketch, "E23.22.3", {"start": v(-70.42, -29.12) * mm, "mid": v(-69.78, -28.57) * mm, "end": v(-69.17, -28) * mm});
            skArc(sketch, "E23.22.4", {"start": v(-69.17, -28) * mm, "mid": v(-68.95, -27.63) * mm, "end": v(-68.96, -27.2) * mm});
            skLineSegment(sketch, "E23.22.5", {"start": v(-68.96, -27.2) * mm, "end": v(-69.05, -26.95) * mm});
            skLineSegment(sketch, "E23.22.6", {"start": v(-69.13, -26.7) * mm, "end": v(-69.05, -26.95) * mm});
            skArc(sketch, "E23.22.7", {"start": v(-69.13, -26.7) * mm, "mid": v(-69.38, -26.35) * mm, "end": v(-69.78, -26.18) * mm});
            skArc(sketch, "E23.22.8", {"start": v(-71.45, -26.07) * mm, "mid": v(-70.62, -26.1) * mm, "end": v(-69.78, -26.18) * mm});
            skArc(sketch, "E23.22.9", {"start": v(-71.45, -26.07) * mm, "mid": v(-71.6, -26.08) * mm, "end": v(-71.74, -26.11) * mm});
            skLineSegment(sketch, "E23.22.10", {"start": v(-71.74, -26.11) * mm, "end": v(-72.85, -26.52) * mm});
            skArc(sketch, "E23.22.11", {"start": v(-73.86, -26.04) * mm, "mid": v(-73.46, -26.49) * mm, "end": v(-72.85, -26.52) * mm});
            skArc(sketch, "E23.23.0", {"start": v(-68.75, -35.67) * mm, "mid": v(-69.2, -36.14) * mm, "end": v(-69.15, -36.77) * mm});
            skLineSegment(sketch, "E23.23.1", {"start": v(-67.86, -35.3) * mm, "end": v(-68.75, -35.67) * mm});
            skArc(sketch, "E23.23.2", {"start": v(-67.86, -35.3) * mm, "mid": v(-67.73, -35.23) * mm, "end": v(-67.61, -35.14) * mm});
            skArc(sketch, "E23.23.3", {"start": v(-67.61, -35.14) * mm, "mid": v(-67.02, -34.55) * mm, "end": v(-66.46, -33.93) * mm});
            skArc(sketch, "E23.23.4", {"start": v(-66.46, -33.93) * mm, "mid": v(-66.28, -33.53) * mm, "end": v(-66.33, -33.1) * mm});
            skLineSegment(sketch, "E23.23.5", {"start": v(-66.33, -33.1) * mm, "end": v(-66.43, -32.86) * mm});
            skLineSegment(sketch, "E23.23.6", {"start": v(-66.54, -32.63) * mm, "end": v(-66.43, -32.86) * mm});
            skArc(sketch, "E23.23.7", {"start": v(-66.54, -32.63) * mm, "mid": v(-66.82, -32.3) * mm, "end": v(-67.24, -32.16) * mm});
            skArc(sketch, "E23.23.8", {"start": v(-68.91, -32.2) * mm, "mid": v(-68.07, -32.16) * mm, "end": v(-67.24, -32.16) * mm});
            skArc(sketch, "E23.23.9", {"start": v(-68.91, -32.2) * mm, "mid": v(-69.06, -32.22) * mm, "end": v(-69.2, -32.27) * mm});
            skLineSegment(sketch, "E23.23.10", {"start": v(-69.2, -32.27) * mm, "end": v(-70.26, -32.76) * mm});
            skArc(sketch, "E23.23.11", {"start": v(-71.31, -32.38) * mm, "mid": v(-70.87, -32.79) * mm, "end": v(-70.26, -32.76) * mm});
            skArc(sketch, "E23.24.0", {"start": v(-65.38, -41.53) * mm, "mid": v(-65.78, -42.03) * mm, "end": v(-65.68, -42.66) * mm});
            skLineSegment(sketch, "E23.24.1", {"start": v(-64.52, -41.08) * mm, "end": v(-65.38, -41.53) * mm});
            skArc(sketch, "E23.24.2", {"start": v(-64.52, -41.08) * mm, "mid": v(-64.4, -41) * mm, "end": v(-64.3, -40.9) * mm});
            skArc(sketch, "E23.24.3", {"start": v(-64.3, -40.9) * mm, "mid": v(-63.76, -40.26) * mm, "end": v(-63.25, -39.6) * mm});
            skArc(sketch, "E23.24.4", {"start": v(-63.25, -39.6) * mm, "mid": v(-63.1, -39.18) * mm, "end": v(-63.2, -38.76) * mm});
            skLineSegment(sketch, "E23.24.5", {"start": v(-63.2, -38.76) * mm, "end": v(-63.32, -38.53) * mm});
            skLineSegment(sketch, "E23.24.6", {"start": v(-63.44, -38.3) * mm, "end": v(-63.32, -38.53) * mm});
            skArc(sketch, "E23.24.7", {"start": v(-63.44, -38.3) * mm, "mid": v(-63.75, -38) * mm, "end": v(-64.18, -37.9) * mm});
            skArc(sketch, "E23.24.8", {"start": v(-65.84, -38.08) * mm, "mid": v(-65.01, -37.97) * mm, "end": v(-64.18, -37.9) * mm});
            skArc(sketch, "E23.24.9", {"start": v(-65.84, -38.08) * mm, "mid": v(-65.99, -38.11) * mm, "end": v(-66.12, -38.17) * mm});
            skLineSegment(sketch, "E23.24.10", {"start": v(-66.12, -38.17) * mm, "end": v(-67.14, -38.76) * mm});
            skArc(sketch, "E23.24.11", {"start": v(-68.22, -38.47) * mm, "mid": v(-67.74, -38.84) * mm, "end": v(-67.14, -38.76) * mm});
            skArc(sketch, "E23.25.0", {"start": v(-61.51, -47.07) * mm, "mid": v(-61.87, -47.6) * mm, "end": v(-61.71, -48.22) * mm});
            skLineSegment(sketch, "E23.25.1", {"start": v(-60.7, -46.55) * mm, "end": v(-61.51, -47.07) * mm});
            skArc(sketch, "E23.25.2", {"start": v(-60.7, -46.55) * mm, "mid": v(-60.58, -46.46) * mm, "end": v(-60.48, -46.35) * mm});
            skArc(sketch, "E23.25.3", {"start": v(-60.48, -46.35) * mm, "mid": v(-60, -45.66) * mm, "end": v(-59.56, -44.95) * mm});
            skArc(sketch, "E23.25.4", {"start": v(-59.56, -44.95) * mm, "mid": v(-59.45, -44.53) * mm, "end": v(-59.58, -44.12) * mm});
            skLineSegment(sketch, "E23.25.5", {"start": v(-59.58, -44.12) * mm, "end": v(-59.72, -43.9) * mm});
            skLineSegment(sketch, "E23.25.6", {"start": v(-59.86, -43.69) * mm, "end": v(-59.72, -43.9) * mm});
            skArc(sketch, "E23.25.7", {"start": v(-59.86, -43.69) * mm, "mid": v(-60.2, -43.4) * mm, "end": v(-60.63, -43.35) * mm});
            skArc(sketch, "E23.25.8", {"start": v(-62.27, -43.67) * mm, "mid": v(-61.46, -43.5) * mm, "end": v(-60.63, -43.35) * mm});
            skArc(sketch, "E23.25.9", {"start": v(-62.27, -43.67) * mm, "mid": v(-62.41, -43.72) * mm, "end": v(-62.54, -43.8) * mm});
            skLineSegment(sketch, "E23.25.10", {"start": v(-62.54, -43.8) * mm, "end": v(-63.5, -44.47) * mm});
            skArc(sketch, "E23.25.11", {"start": v(-64.6, -44.27) * mm, "mid": v(-64.1, -44.6) * mm, "end": v(-63.5, -44.47) * mm});
            skArc(sketch, "E23.26.0", {"start": v(-57.18, -52.25) * mm, "mid": v(-57.48, -52.81) * mm, "end": v(-57.27, -53.41) * mm});
            skLineSegment(sketch, "E23.26.1", {"start": v(-56.4, -51.66) * mm, "end": v(-57.18, -52.25) * mm});
            skArc(sketch, "E23.26.2", {"start": v(-56.4, -51.66) * mm, "mid": v(-56.3, -51.56) * mm, "end": v(-56.21, -51.44) * mm});
            skArc(sketch, "E23.26.3", {"start": v(-56.21, -51.44) * mm, "mid": v(-55.8, -50.72) * mm, "end": v(-55.42, -49.97) * mm});
            skArc(sketch, "E23.26.4", {"start": v(-55.42, -49.97) * mm, "mid": v(-55.34, -49.54) * mm, "end": v(-55.5, -49.14) * mm});
            skLineSegment(sketch, "E23.26.5", {"start": v(-55.5, -49.14) * mm, "end": v(-55.66, -48.94) * mm});
            skLineSegment(sketch, "E23.26.6", {"start": v(-55.83, -48.74) * mm, "end": v(-55.66, -48.94) * mm});
            skArc(sketch, "E23.26.7", {"start": v(-55.83, -48.74) * mm, "mid": v(-56.19, -48.5) * mm, "end": v(-56.62, -48.47) * mm});
            skArc(sketch, "E23.26.8", {"start": v(-58.23, -48.93) * mm, "mid": v(-57.43, -48.68) * mm, "end": v(-56.62, -48.47) * mm});
            skArc(sketch, "E23.26.9", {"start": v(-58.23, -48.93) * mm, "mid": v(-58.36, -49) * mm, "end": v(-58.49, -49.08) * mm});
            skLineSegment(sketch, "E23.26.10", {"start": v(-58.49, -49.08) * mm, "end": v(-59.39, -49.83) * mm});
            skArc(sketch, "E23.26.11", {"start": v(-60.5, -49.73) * mm, "mid": v(-59.97, -50.01) * mm, "end": v(-59.39, -49.83) * mm});
            skArc(sketch, "E23.27.0", {"start": v(-52.4, -57.04) * mm, "mid": v(-52.66, -57.62) * mm, "end": v(-52.4, -58.2) * mm});
            skLineSegment(sketch, "E23.27.1", {"start": v(-51.7, -56.38) * mm, "end": v(-52.4, -57.04) * mm});
            skArc(sketch, "E23.27.2", {"start": v(-51.7, -56.38) * mm, "mid": v(-51.6, -56.27) * mm, "end": v(-51.52, -56.15) * mm});
            skArc(sketch, "E23.27.3", {"start": v(-51.52, -56.15) * mm, "mid": v(-51.17, -55.39) * mm, "end": v(-50.85, -54.61) * mm});
            skArc(sketch, "E23.27.4", {"start": v(-50.85, -54.61) * mm, "mid": v(-50.81, -54.18) * mm, "end": v(-51.01, -53.8) * mm});
            skLineSegment(sketch, "E23.27.5", {"start": v(-51.01, -53.8) * mm, "end": v(-51.19, -53.6) * mm});
            skLineSegment(sketch, "E23.27.6", {"start": v(-51.37, -53.42) * mm, "end": v(-51.19, -53.6) * mm});
            skArc(sketch, "E23.27.7", {"start": v(-51.37, -53.42) * mm, "mid": v(-51.75, -53.2) * mm, "end": v(-52.18, -53.22) * mm});
            skArc(sketch, "E23.27.8", {"start": v(-53.74, -53.82) * mm, "mid": v(-52.97, -53.5) * mm, "end": v(-52.18, -53.22) * mm});
            skArc(sketch, "E23.27.9", {"start": v(-53.74, -53.82) * mm, "mid": v(-53.87, -53.9) * mm, "end": v(-53.99, -53.99) * mm});
            skLineSegment(sketch, "E23.27.10", {"start": v(-53.99, -53.99) * mm, "end": v(-54.82, -54.82) * mm});
            skArc(sketch, "E23.27.11", {"start": v(-55.94, -54.81) * mm, "mid": v(-55.38, -55.05) * mm, "end": v(-54.82, -54.82) * mm});
            skArc(sketch, "E23.28.0", {"start": v(-47.24, -61.39) * mm, "mid": v(-47.44, -62) * mm, "end": v(-47.13, -62.55) * mm});
            skLineSegment(sketch, "E23.28.1", {"start": v(-46.58, -60.67) * mm, "end": v(-47.24, -61.39) * mm});
            skArc(sketch, "E23.28.2", {"start": v(-46.58, -60.67) * mm, "mid": v(-46.5, -60.56) * mm, "end": v(-46.43, -60.42) * mm});
            skArc(sketch, "E23.28.3", {"start": v(-46.43, -60.42) * mm, "mid": v(-46.14, -59.64) * mm, "end": v(-45.9, -58.84) * mm});
            skArc(sketch, "E23.28.4", {"start": v(-45.9, -58.84) * mm, "mid": v(-45.9, -58.4) * mm, "end": v(-46.13, -58.03) * mm});
            skLineSegment(sketch, "E23.28.5", {"start": v(-46.13, -58.03) * mm, "end": v(-46.32, -57.86) * mm});
            skLineSegment(sketch, "E23.28.6", {"start": v(-46.52, -57.7) * mm, "end": v(-46.32, -57.86) * mm});
            skArc(sketch, "E23.28.7", {"start": v(-46.52, -57.7) * mm, "mid": v(-46.91, -57.51) * mm, "end": v(-47.34, -57.57) * mm});
            skArc(sketch, "E23.28.8", {"start": v(-48.85, -58.3) * mm, "mid": v(-48.1, -57.92) * mm, "end": v(-47.34, -57.57) * mm});
            skArc(sketch, "E23.28.9", {"start": v(-48.85, -58.3) * mm, "mid": v(-48.97, -58.38) * mm, "end": v(-49.08, -58.49) * mm});
            skLineSegment(sketch, "E23.28.10", {"start": v(-49.08, -58.49) * mm, "end": v(-49.83, -59.39) * mm});
            skArc(sketch, "E23.28.11", {"start": v(-50.95, -59.48) * mm, "mid": v(-50.37, -59.67) * mm, "end": v(-49.83, -59.39) * mm});
            skArc(sketch, "E23.29.0", {"start": v(-41.7, -65.27) * mm, "mid": v(-41.86, -65.9) * mm, "end": v(-41.5, -66.42) * mm});
            skLineSegment(sketch, "E23.29.1", {"start": v(-41.12, -64.5) * mm, "end": v(-41.7, -65.27) * mm});
            skArc(sketch, "E23.29.2", {"start": v(-41.12, -64.5) * mm, "mid": v(-41.04, -64.38) * mm, "end": v(-40.98, -64.24) * mm});
            skArc(sketch, "E23.29.3", {"start": v(-40.98, -64.24) * mm, "mid": v(-40.77, -63.43) * mm, "end": v(-40.6, -62.61) * mm});
            skArc(sketch, "E23.29.4", {"start": v(-40.6, -62.61) * mm, "mid": v(-40.63, -62.18) * mm, "end": v(-40.9, -61.83) * mm});
            skLineSegment(sketch, "E23.29.5", {"start": v(-40.9, -61.83) * mm, "end": v(-41.1, -61.68) * mm});
            skLineSegment(sketch, "E23.29.6", {"start": v(-41.31, -61.53) * mm, "end": v(-41.1, -61.68) * mm});
            skArc(sketch, "E23.29.7", {"start": v(-41.31, -61.53) * mm, "mid": v(-41.72, -61.38) * mm, "end": v(-42.15, -61.47) * mm});
            skArc(sketch, "E23.29.8", {"start": v(-43.58, -62.34) * mm, "mid": v(-42.87, -61.89) * mm, "end": v(-42.15, -61.47) * mm});
            skArc(sketch, "E23.29.9", {"start": v(-43.58, -62.34) * mm, "mid": v(-43.7, -62.43) * mm, "end": v(-43.8, -62.54) * mm});
            skLineSegment(sketch, "E23.29.10", {"start": v(-43.8, -62.54) * mm, "end": v(-44.47, -63.5) * mm});
            skArc(sketch, "E23.29.11", {"start": v(-45.57, -63.7) * mm, "mid": v(-44.98, -63.83) * mm, "end": v(-44.47, -63.5) * mm});
            skArc(sketch, "E23.30.0", {"start": v(-35.86, -68.66) * mm, "mid": v(-35.95, -69.29) * mm, "end": v(-35.55, -69.78) * mm});
            skLineSegment(sketch, "E23.30.1", {"start": v(-35.34, -67.84) * mm, "end": v(-35.86, -68.66) * mm});
            skArc(sketch, "E23.30.2", {"start": v(-35.34, -67.84) * mm, "mid": v(-35.27, -67.7) * mm, "end": v(-35.23, -67.57) * mm});
            skArc(sketch, "E23.30.3", {"start": v(-35.23, -67.57) * mm, "mid": v(-35.09, -66.74) * mm, "end": v(-34.98, -65.91) * mm});
            skArc(sketch, "E23.30.4", {"start": v(-34.98, -65.91) * mm, "mid": v(-35.06, -65.48) * mm, "end": v(-35.35, -65.16) * mm});
            skLineSegment(sketch, "E23.30.5", {"start": v(-35.35, -65.16) * mm, "end": v(-35.57, -65.03) * mm});
            skLineSegment(sketch, "E23.30.6", {"start": v(-35.8, -64.9) * mm, "end": v(-35.57, -65.03) * mm});
            skArc(sketch, "E23.30.7", {"start": v(-35.8, -64.9) * mm, "mid": v(-36.21, -64.78) * mm, "end": v(-36.63, -64.91) * mm});
            skArc(sketch, "E23.30.8", {"start": v(-37.98, -65.9) * mm, "mid": v(-37.32, -65.4) * mm, "end": v(-36.63, -64.91) * mm});
            skArc(sketch, "E23.30.9", {"start": v(-37.98, -65.9) * mm, "mid": v(-38.09, -66) * mm, "end": v(-38.17, -66.12) * mm});
            skLineSegment(sketch, "E23.30.10", {"start": v(-38.17, -66.12) * mm, "end": v(-38.76, -67.14) * mm});
            skArc(sketch, "E23.30.11", {"start": v(-39.85, -67.42) * mm, "mid": v(-39.24, -67.5) * mm, "end": v(-38.76, -67.14) * mm});
            skArc(sketch, "E23.31.0", {"start": v(-29.74, -71.52) * mm, "mid": v(-29.78, -72.16) * mm, "end": v(-29.33, -72.62) * mm});
            skLineSegment(sketch, "E23.31.1", {"start": v(-29.3, -70.66) * mm, "end": v(-29.74, -71.52) * mm});
            skArc(sketch, "E23.31.2", {"start": v(-29.3, -70.66) * mm, "mid": v(-29.23, -70.53) * mm, "end": v(-29.2, -70.38) * mm});
            skArc(sketch, "E23.31.3", {"start": v(-29.2, -70.38) * mm, "mid": v(-29.14, -69.55) * mm, "end": v(-29.1, -68.71) * mm});
            skArc(sketch, "E23.31.4", {"start": v(-29.1, -68.71) * mm, "mid": v(-29.22, -68.3) * mm, "end": v(-29.54, -68) * mm});
            skLineSegment(sketch, "E23.31.5", {"start": v(-29.54, -68) * mm, "end": v(-29.77, -67.88) * mm});
            skLineSegment(sketch, "E23.31.6", {"start": v(-30, -67.77) * mm, "end": v(-29.77, -67.88) * mm});
            skArc(sketch, "E23.31.7", {"start": v(-30, -67.77) * mm, "mid": v(-30.43, -67.7) * mm, "end": v(-30.83, -67.86) * mm});
            skArc(sketch, "E23.31.8", {"start": v(-32.1, -68.96) * mm, "mid": v(-31.48, -68.4) * mm, "end": v(-30.83, -67.86) * mm});
            skArc(sketch, "E23.31.9", {"start": v(-32.1, -68.96) * mm, "mid": v(-32.2, -69.07) * mm, "end": v(-32.27, -69.2) * mm});
            skLineSegment(sketch, "E23.31.10", {"start": v(-32.27, -69.2) * mm, "end": v(-32.76, -70.26) * mm});
            skArc(sketch, "E23.31.11", {"start": v(-33.82, -70.64) * mm, "mid": v(-33.21, -70.67) * mm, "end": v(-32.76, -70.26) * mm});
            skArc(sketch, "E23.32.0", {"start": v(-23.4, -73.84) * mm, "mid": v(-23.38, -74.48) * mm, "end": v(-22.9, -74.9) * mm});
            skLineSegment(sketch, "E23.32.1", {"start": v(-23.02, -72.95) * mm, "end": v(-23.4, -73.84) * mm});
            skArc(sketch, "E23.32.2", {"start": v(-23.02, -72.95) * mm, "mid": v(-22.98, -72.8) * mm, "end": v(-22.96, -72.66) * mm});
            skArc(sketch, "E23.32.3", {"start": v(-22.96, -72.66) * mm, "mid": v(-22.96, -71.82) * mm, "end": v(-23, -70.99) * mm});
            skArc(sketch, "E23.32.4", {"start": v(-23, -70.99) * mm, "mid": v(-23.15, -70.58) * mm, "end": v(-23.5, -70.31) * mm});
            skLineSegment(sketch, "E23.32.5", {"start": v(-23.5, -70.31) * mm, "end": v(-23.74, -70.21) * mm});
            skLineSegment(sketch, "E23.32.6", {"start": v(-23.98, -70.12) * mm, "end": v(-23.74, -70.21) * mm});
            skArc(sketch, "E23.32.7", {"start": v(-23.98, -70.12) * mm, "mid": v(-24.41, -70.09) * mm, "end": v(-24.8, -70.29) * mm});
            skArc(sketch, "E23.32.8", {"start": v(-25.96, -71.5) * mm, "mid": v(-25.4, -70.88) * mm, "end": v(-24.8, -70.29) * mm});
            skArc(sketch, "E23.32.9", {"start": v(-25.96, -71.5) * mm, "mid": v(-26.05, -71.61) * mm, "end": v(-26.11, -71.74) * mm});
            skLineSegment(sketch, "E23.32.10", {"start": v(-26.11, -71.74) * mm, "end": v(-26.52, -72.85) * mm});
            skArc(sketch, "E23.32.11", {"start": v(-27.53, -73.32) * mm, "mid": v(-26.93, -73.3) * mm, "end": v(-26.52, -72.85) * mm});
            skArc(sketch, "E23.33.0", {"start": v(-16.87, -75.6) * mm, "mid": v(-16.8, -76.23) * mm, "end": v(-16.28, -76.6) * mm});
            skLineSegment(sketch, "E23.33.1", {"start": v(-16.57, -74.67) * mm, "end": v(-16.87, -75.6) * mm});
            skArc(sketch, "E23.33.2", {"start": v(-16.57, -74.67) * mm, "mid": v(-16.54, -74.53) * mm, "end": v(-16.54, -74.38) * mm});
            skArc(sketch, "E23.33.3", {"start": v(-16.54, -74.38) * mm, "mid": v(-16.62, -73.55) * mm, "end": v(-16.73, -72.72) * mm});
            skArc(sketch, "E23.33.4", {"start": v(-16.73, -72.72) * mm, "mid": v(-16.91, -72.33) * mm, "end": v(-17.28, -72.1) * mm});
            skLineSegment(sketch, "E23.33.5", {"start": v(-17.28, -72.1) * mm, "end": v(-17.53, -72.02) * mm});
            skLineSegment(sketch, "E23.33.6", {"start": v(-17.78, -71.95) * mm, "end": v(-17.53, -72.02) * mm});
            skArc(sketch, "E23.33.7", {"start": v(-17.78, -71.95) * mm, "mid": v(-18.21, -71.95) * mm, "end": v(-18.58, -72.18) * mm});
            skArc(sketch, "E23.33.8", {"start": v(-19.63, -73.48) * mm, "mid": v(-19.12, -72.82) * mm, "end": v(-18.58, -72.18) * mm});
            skArc(sketch, "E23.33.9", {"start": v(-19.63, -73.48) * mm, "mid": v(-19.7, -73.6) * mm, "end": v(-19.76, -73.75) * mm});
            skLineSegment(sketch, "E23.33.10", {"start": v(-19.76, -73.75) * mm, "end": v(-20.07, -74.88) * mm});
            skArc(sketch, "E23.33.11", {"start": v(-21.04, -75.44) * mm, "mid": v(-20.44, -75.36) * mm, "end": v(-20.07, -74.88) * mm});
            skArc(sketch, "E23.34.0", {"start": v(-10.21, -76.78) * mm, "mid": v(-10.09, -77.4) * mm, "end": v(-9.54, -77.73) * mm});
            skLineSegment(sketch, "E23.34.1", {"start": v(-10, -75.84) * mm, "end": v(-10.21, -76.78) * mm});
            skArc(sketch, "E23.34.2", {"start": v(-10, -75.84) * mm, "mid": v(-9.98, -75.69) * mm, "end": v(-10, -75.54) * mm});
            skArc(sketch, "E23.34.3", {"start": v(-10, -75.54) * mm, "mid": v(-10.14, -74.72) * mm, "end": v(-10.33, -73.9) * mm});
            skArc(sketch, "E23.34.4", {"start": v(-10.33, -73.9) * mm, "mid": v(-10.55, -73.53) * mm, "end": v(-10.93, -73.32) * mm});
            skLineSegment(sketch, "E23.34.5", {"start": v(-10.93, -73.32) * mm, "end": v(-11.18, -73.27) * mm});
            skLineSegment(sketch, "E23.34.6", {"start": v(-11.44, -73.22) * mm, "end": v(-11.18, -73.27) * mm});
            skArc(sketch, "E23.34.7", {"start": v(-11.44, -73.22) * mm, "mid": v(-11.87, -73.26) * mm, "end": v(-12.22, -73.53) * mm});
            skArc(sketch, "E23.34.8", {"start": v(-13.15, -74.91) * mm, "mid": v(-12.7, -74.2) * mm, "end": v(-12.22, -73.53) * mm});
            skArc(sketch, "E23.34.9", {"start": v(-13.15, -74.91) * mm, "mid": v(-13.22, -75.05) * mm, "end": v(-13.26, -75.19) * mm});
            skLineSegment(sketch, "E23.34.10", {"start": v(-13.26, -75.19) * mm, "end": v(-13.46, -76.35) * mm});
            skArc(sketch, "E23.34.11", {"start": v(-14.38, -76.98) * mm, "mid": v(-13.79, -76.86) * mm, "end": v(-13.46, -76.35) * mm});
            skArc(sketch, "E23.35.0", {"start": v(-3.48, -77.38) * mm, "mid": v(-3.3, -78) * mm, "end": v(-2.73, -78.27) * mm});
            skLineSegment(sketch, "E23.35.1", {"start": v(-3.36, -76.42) * mm, "end": v(-3.48, -77.38) * mm});
            skArc(sketch, "E23.35.2", {"start": v(-3.36, -76.42) * mm, "mid": v(-3.35, -76.27) * mm, "end": v(-3.37, -76.13) * mm});
            skArc(sketch, "E23.35.3", {"start": v(-3.37, -76.13) * mm, "mid": v(-3.6, -75.32) * mm, "end": v(-3.85, -74.52) * mm});
            skArc(sketch, "E23.35.4", {"start": v(-3.85, -74.52) * mm, "mid": v(-4.1, -74.16) * mm, "end": v(-4.5, -74) * mm});
            skLineSegment(sketch, "E23.35.5", {"start": v(-4.5, -74) * mm, "end": v(-4.76, -73.97) * mm});
            skLineSegment(sketch, "E23.35.6", {"start": v(-5.01, -73.94) * mm, "end": v(-4.76, -73.97) * mm});
            skArc(sketch, "E23.35.7", {"start": v(-5.01, -73.94) * mm, "mid": v(-5.44, -74.02) * mm, "end": v(-5.76, -74.31) * mm});
            skArc(sketch, "E23.35.8", {"start": v(-6.57, -75.77) * mm, "mid": v(-6.18, -75.03) * mm, "end": v(-5.76, -74.31) * mm});
            skArc(sketch, "E23.35.9", {"start": v(-6.57, -75.77) * mm, "mid": v(-6.63, -75.91) * mm, "end": v(-6.65, -76.06) * mm});
            skLineSegment(sketch, "E23.35.10", {"start": v(-6.65, -76.06) * mm, "end": v(-6.76, -77.23) * mm});
            skArc(sketch, "E23.35.11", {"start": v(-7.62, -77.95) * mm, "mid": v(-7.04, -77.77) * mm, "end": v(-6.76, -77.23) * mm});
            skArc(sketch, "E23.36.0", {"start": v(3.28, -77.39) * mm, "mid": v(3.5, -77.98) * mm, "end": v(4.1, -78.2) * mm});
            skLineSegment(sketch, "E23.36.1", {"start": v(3.32, -76.42) * mm, "end": v(3.28, -77.39) * mm});
            skArc(sketch, "E23.36.2", {"start": v(3.32, -76.42) * mm, "mid": v(3.3, -76.27) * mm, "end": v(3.28, -76.13) * mm});
            skArc(sketch, "E23.36.3", {"start": v(3.28, -76.13) * mm, "mid": v(2.99, -75.34) * mm, "end": v(2.66, -74.57) * mm});
            skArc(sketch, "E23.36.4", {"start": v(2.66, -74.57) * mm, "mid": v(2.38, -74.24) * mm, "end": v(1.97, -74.1) * mm});
            skLineSegment(sketch, "E23.36.5", {"start": v(1.97, -74.1) * mm, "end": v(1.7, -74.1) * mm});
            skLineSegment(sketch, "E23.36.6", {"start": v(1.45, -74.1) * mm, "end": v(1.7, -74.1) * mm});
            skArc(sketch, "E23.36.7", {"start": v(1.45, -74.1) * mm, "mid": v(1.03, -74.21) * mm, "end": v(0.74, -74.53) * mm});
            skArc(sketch, "E23.36.8", {"start": v(0.05, -76.06) * mm, "mid": v(0.38, -75.29) * mm, "end": v(0.74, -74.53) * mm});
            skArc(sketch, "E23.36.9", {"start": v(0.05, -76.06) * mm, "mid": v(0.01, -76.2) * mm, "end": v(0, -76.35) * mm});
            skLineSegment(sketch, "E23.36.10", {"start": v(0, -76.35) * mm, "end": v(0, -77.53) * mm});
            skArc(sketch, "E23.36.11", {"start": v(-0.8, -78.31) * mm, "mid": v(-0.23, -78.08) * mm, "end": v(0, -77.53) * mm});
            skArc(sketch, "E23.37.0", {"start": v(10, -76.8) * mm, "mid": v(10.3, -77.38) * mm, "end": v(10.9, -77.55) * mm});
            skLineSegment(sketch, "E23.37.1", {"start": v(9.97, -75.84) * mm, "end": v(10, -76.8) * mm});
            skArc(sketch, "E23.37.2", {"start": v(9.97, -75.84) * mm, "mid": v(9.94, -75.7) * mm, "end": v(9.9, -75.55) * mm});
            skArc(sketch, "E23.37.3", {"start": v(9.9, -75.55) * mm, "mid": v(9.54, -74.8) * mm, "end": v(9.15, -74.06) * mm});
            skArc(sketch, "E23.37.4", {"start": v(9.15, -74.06) * mm, "mid": v(8.84, -73.75) * mm, "end": v(8.42, -73.65) * mm});
            skLineSegment(sketch, "E23.37.5", {"start": v(8.42, -73.65) * mm, "end": v(8.16, -73.67) * mm});
            skLineSegment(sketch, "E23.37.6", {"start": v(7.9, -73.69) * mm, "end": v(8.16, -73.67) * mm});
            skArc(sketch, "E23.37.7", {"start": v(7.9, -73.69) * mm, "mid": v(7.5, -73.84) * mm, "end": v(7.23, -74.18) * mm});
            skArc(sketch, "E23.37.8", {"start": v(6.68, -75.77) * mm, "mid": v(6.94, -74.97) * mm, "end": v(7.23, -74.18) * mm});
            skArc(sketch, "E23.37.9", {"start": v(6.68, -75.77) * mm, "mid": v(6.66, -75.9) * mm, "end": v(6.65, -76.06) * mm});
            skLineSegment(sketch, "E23.37.10", {"start": v(6.65, -76.06) * mm, "end": v(6.76, -77.23) * mm});
            skArc(sketch, "E23.37.11", {"start": v(6.03, -78.08) * mm, "mid": v(6.57, -77.8) * mm, "end": v(6.76, -77.23) * mm});
            skArc(sketch, "E23.38.0", {"start": v(16.66, -75.64) * mm, "mid": v(17, -76.19) * mm, "end": v(17.62, -76.3) * mm});
            skLineSegment(sketch, "E23.38.1", {"start": v(16.54, -74.68) * mm, "end": v(16.66, -75.64) * mm});
            skArc(sketch, "E23.38.2", {"start": v(16.54, -74.68) * mm, "mid": v(16.5, -74.54) * mm, "end": v(16.45, -74.4) * mm});
            skArc(sketch, "E23.38.3", {"start": v(16.45, -74.4) * mm, "mid": v(16.02, -73.68) * mm, "end": v(15.57, -72.98) * mm});
            skArc(sketch, "E23.38.4", {"start": v(15.57, -72.98) * mm, "mid": v(15.24, -72.7) * mm, "end": v(14.8, -72.64) * mm});
            skLineSegment(sketch, "E23.38.5", {"start": v(14.8, -72.64) * mm, "end": v(14.55, -72.68) * mm});
            skLineSegment(sketch, "E23.38.6", {"start": v(14.3, -72.72) * mm, "end": v(14.55, -72.68) * mm});
            skArc(sketch, "E23.38.7", {"start": v(14.3, -72.72) * mm, "mid": v(13.9, -72.9) * mm, "end": v(13.67, -73.27) * mm});
            skArc(sketch, "E23.38.8", {"start": v(13.26, -74.9) * mm, "mid": v(13.45, -74.08) * mm, "end": v(13.67, -73.27) * mm});
            skArc(sketch, "E23.38.9", {"start": v(13.26, -74.9) * mm, "mid": v(13.25, -75.04) * mm, "end": v(13.26, -75.19) * mm});
            skLineSegment(sketch, "E23.38.10", {"start": v(13.26, -75.19) * mm, "end": v(13.46, -76.35) * mm});
            skArc(sketch, "E23.38.11", {"start": v(12.82, -77.26) * mm, "mid": v(13.33, -76.94) * mm, "end": v(13.46, -76.35) * mm});
            skArc(sketch, "E23.39.0", {"start": v(23.2, -73.9) * mm, "mid": v(23.57, -74.42) * mm, "end": v(24.2, -74.48) * mm});
            skLineSegment(sketch, "E23.39.1", {"start": v(22.98, -72.96) * mm, "end": v(23.2, -73.9) * mm});
            skArc(sketch, "E23.39.2", {"start": v(22.98, -72.96) * mm, "mid": v(22.94, -72.82) * mm, "end": v(22.87, -72.69) * mm});
            skArc(sketch, "E23.39.3", {"start": v(22.87, -72.69) * mm, "mid": v(22.38, -72) * mm, "end": v(21.87, -71.34) * mm});
            skArc(sketch, "E23.39.4", {"start": v(21.87, -71.34) * mm, "mid": v(21.52, -71.1) * mm, "end": v(21.08, -71.07) * mm});
            skLineSegment(sketch, "E23.39.5", {"start": v(21.08, -71.07) * mm, "end": v(20.83, -71.13) * mm});
            skLineSegment(sketch, "E23.39.6", {"start": v(20.58, -71.2) * mm, "end": v(20.83, -71.13) * mm});
            skArc(sketch, "E23.39.7", {"start": v(20.58, -71.2) * mm, "mid": v(20.2, -71.42) * mm, "end": v(20, -71.8) * mm});
            skArc(sketch, "E23.39.8", {"start": v(19.74, -73.45) * mm, "mid": v(19.85, -72.62) * mm, "end": v(20, -71.8) * mm});
            skArc(sketch, "E23.39.9", {"start": v(19.74, -73.45) * mm, "mid": v(19.74, -73.6) * mm, "end": v(19.76, -73.75) * mm});
            skLineSegment(sketch, "E23.39.10", {"start": v(19.76, -73.75) * mm, "end": v(20.07, -74.88) * mm});
            skArc(sketch, "E23.39.11", {"start": v(19.5, -75.85) * mm, "mid": v(19.98, -75.48) * mm, "end": v(20.07, -74.88) * mm});
            skArc(sketch, "E23.40.0", {"start": v(29.55, -71.6) * mm, "mid": v(29.97, -72.08) * mm, "end": v(30.6, -72.09) * mm});
            skLineSegment(sketch, "E23.40.1", {"start": v(29.25, -70.68) * mm, "end": v(29.55, -71.6) * mm});
            skArc(sketch, "E23.40.2", {"start": v(29.25, -70.68) * mm, "mid": v(29.2, -70.54) * mm, "end": v(29.12, -70.42) * mm});
            skArc(sketch, "E23.40.3", {"start": v(29.12, -70.42) * mm, "mid": v(28.57, -69.78) * mm, "end": v(28, -69.17) * mm});
            skArc(sketch, "E23.40.4", {"start": v(28, -69.17) * mm, "mid": v(27.63, -68.95) * mm, "end": v(27.2, -68.96) * mm});
            skLineSegment(sketch, "E23.40.5", {"start": v(27.2, -68.96) * mm, "end": v(26.95, -69.05) * mm});
            skLineSegment(sketch, "E23.40.6", {"start": v(26.7, -69.13) * mm, "end": v(26.95, -69.05) * mm});
            skArc(sketch, "E23.40.7", {"start": v(26.7, -69.13) * mm, "mid": v(26.35, -69.38) * mm, "end": v(26.18, -69.78) * mm});
            skArc(sketch, "E23.40.8", {"start": v(26.07, -71.45) * mm, "mid": v(26.1, -70.62) * mm, "end": v(26.18, -69.78) * mm});
            skArc(sketch, "E23.40.9", {"start": v(26.07, -71.45) * mm, "mid": v(26.08, -71.6) * mm, "end": v(26.11, -71.74) * mm});
            skLineSegment(sketch, "E23.40.10", {"start": v(26.11, -71.74) * mm, "end": v(26.52, -72.85) * mm});
            skArc(sketch, "E23.40.11", {"start": v(26.04, -73.86) * mm, "mid": v(26.49, -73.46) * mm, "end": v(26.52, -72.85) * mm});
            skArc(sketch, "E23.41.0", {"start": v(35.67, -68.75) * mm, "mid": v(36.14, -69.2) * mm, "end": v(36.77, -69.15) * mm});
            skLineSegment(sketch, "E23.41.1", {"start": v(35.3, -67.86) * mm, "end": v(35.67, -68.75) * mm});
            skArc(sketch, "E23.41.2", {"start": v(35.3, -67.86) * mm, "mid": v(35.23, -67.73) * mm, "end": v(35.14, -67.61) * mm});
            skArc(sketch, "E23.41.3", {"start": v(35.14, -67.61) * mm, "mid": v(34.55, -67.02) * mm, "end": v(33.93, -66.46) * mm});
            skArc(sketch, "E23.41.4", {"start": v(33.93, -66.46) * mm, "mid": v(33.53, -66.28) * mm, "end": v(33.1, -66.33) * mm});
            skLineSegment(sketch, "E23.41.5", {"start": v(33.1, -66.33) * mm, "end": v(32.86, -66.43) * mm});
            skLineSegment(sketch, "E23.41.6", {"start": v(32.63, -66.54) * mm, "end": v(32.86, -66.43) * mm});
            skArc(sketch, "E23.41.7", {"start": v(32.63, -66.54) * mm, "mid": v(32.3, -66.82) * mm, "end": v(32.16, -67.24) * mm});
            skArc(sketch, "E23.41.8", {"start": v(32.2, -68.91) * mm, "mid": v(32.16, -68.07) * mm, "end": v(32.16, -67.24) * mm});
            skArc(sketch, "E23.41.9", {"start": v(32.2, -68.91) * mm, "mid": v(32.22, -69.06) * mm, "end": v(32.27, -69.2) * mm});
            skLineSegment(sketch, "E23.41.10", {"start": v(32.27, -69.2) * mm, "end": v(32.76, -70.26) * mm});
            skArc(sketch, "E23.41.11", {"start": v(32.38, -71.31) * mm, "mid": v(32.79, -70.87) * mm, "end": v(32.76, -70.26) * mm});
            skArc(sketch, "E23.42.0", {"start": v(41.53, -65.38) * mm, "mid": v(42.03, -65.78) * mm, "end": v(42.66, -65.68) * mm});
            skLineSegment(sketch, "E23.42.1", {"start": v(41.08, -64.52) * mm, "end": v(41.53, -65.38) * mm});
            skArc(sketch, "E23.42.2", {"start": v(41.08, -64.52) * mm, "mid": v(41, -64.4) * mm, "end": v(40.9, -64.3) * mm});
            skArc(sketch, "E23.42.3", {"start": v(40.9, -64.3) * mm, "mid": v(40.26, -63.76) * mm, "end": v(39.6, -63.25) * mm});
            skArc(sketch, "E23.42.4", {"start": v(39.6, -63.25) * mm, "mid": v(39.18, -63.1) * mm, "end": v(38.76, -63.2) * mm});
            skLineSegment(sketch, "E23.42.5", {"start": v(38.76, -63.2) * mm, "end": v(38.53, -63.32) * mm});
            skLineSegment(sketch, "E23.42.6", {"start": v(38.3, -63.44) * mm, "end": v(38.53, -63.32) * mm});
            skArc(sketch, "E23.42.7", {"start": v(38.3, -63.44) * mm, "mid": v(38, -63.75) * mm, "end": v(37.9, -64.18) * mm});
            skArc(sketch, "E23.42.8", {"start": v(38.08, -65.84) * mm, "mid": v(37.97, -65.01) * mm, "end": v(37.9, -64.18) * mm});
            skArc(sketch, "E23.42.9", {"start": v(38.08, -65.84) * mm, "mid": v(38.11, -65.99) * mm, "end": v(38.17, -66.12) * mm});
            skLineSegment(sketch, "E23.42.10", {"start": v(38.17, -66.12) * mm, "end": v(38.76, -67.14) * mm});
            skArc(sketch, "E23.42.11", {"start": v(38.47, -68.22) * mm, "mid": v(38.84, -67.74) * mm, "end": v(38.76, -67.14) * mm});
            skArc(sketch, "E23.43.0", {"start": v(47.07, -61.51) * mm, "mid": v(47.6, -61.87) * mm, "end": v(48.22, -61.71) * mm});
            skLineSegment(sketch, "E23.43.1", {"start": v(46.55, -60.7) * mm, "end": v(47.07, -61.51) * mm});
            skArc(sketch, "E23.43.2", {"start": v(46.55, -60.7) * mm, "mid": v(46.46, -60.58) * mm, "end": v(46.35, -60.48) * mm});
            skArc(sketch, "E23.43.3", {"start": v(46.35, -60.48) * mm, "mid": v(45.66, -60) * mm, "end": v(44.95, -59.56) * mm});
            skArc(sketch, "E23.43.4", {"start": v(44.95, -59.56) * mm, "mid": v(44.53, -59.45) * mm, "end": v(44.12, -59.58) * mm});
            skLineSegment(sketch, "E23.43.5", {"start": v(44.12, -59.58) * mm, "end": v(43.9, -59.72) * mm});
            skLineSegment(sketch, "E23.43.6", {"start": v(43.69, -59.86) * mm, "end": v(43.9, -59.72) * mm});
            skArc(sketch, "E23.43.7", {"start": v(43.69, -59.86) * mm, "mid": v(43.4, -60.2) * mm, "end": v(43.35, -60.63) * mm});
            skArc(sketch, "E23.43.8", {"start": v(43.67, -62.27) * mm, "mid": v(43.5, -61.46) * mm, "end": v(43.35, -60.63) * mm});
            skArc(sketch, "E23.43.9", {"start": v(43.67, -62.27) * mm, "mid": v(43.72, -62.41) * mm, "end": v(43.8, -62.54) * mm});
            skLineSegment(sketch, "E23.43.10", {"start": v(43.8, -62.54) * mm, "end": v(44.47, -63.5) * mm});
            skArc(sketch, "E23.43.11", {"start": v(44.27, -64.6) * mm, "mid": v(44.6, -64.1) * mm, "end": v(44.47, -63.5) * mm});
            skArc(sketch, "E23.44.0", {"start": v(52.25, -57.18) * mm, "mid": v(52.81, -57.48) * mm, "end": v(53.41, -57.27) * mm});
            skLineSegment(sketch, "E23.44.1", {"start": v(51.66, -56.4) * mm, "end": v(52.25, -57.18) * mm});
            skArc(sketch, "E23.44.2", {"start": v(51.66, -56.4) * mm, "mid": v(51.56, -56.3) * mm, "end": v(51.44, -56.21) * mm});
            skArc(sketch, "E23.44.3", {"start": v(51.44, -56.21) * mm, "mid": v(50.72, -55.8) * mm, "end": v(49.97, -55.42) * mm});
            skArc(sketch, "E23.44.4", {"start": v(49.97, -55.42) * mm, "mid": v(49.54, -55.34) * mm, "end": v(49.14, -55.5) * mm});
            skLineSegment(sketch, "E23.44.5", {"start": v(49.14, -55.5) * mm, "end": v(48.94, -55.66) * mm});
            skLineSegment(sketch, "E23.44.6", {"start": v(48.74, -55.83) * mm, "end": v(48.94, -55.66) * mm});
            skArc(sketch, "E23.44.7", {"start": v(48.74, -55.83) * mm, "mid": v(48.5, -56.19) * mm, "end": v(48.47, -56.62) * mm});
            skArc(sketch, "E23.44.8", {"start": v(48.93, -58.23) * mm, "mid": v(48.68, -57.43) * mm, "end": v(48.47, -56.62) * mm});
            skArc(sketch, "E23.44.9", {"start": v(48.93, -58.23) * mm, "mid": v(49, -58.36) * mm, "end": v(49.08, -58.49) * mm});
            skLineSegment(sketch, "E23.44.10", {"start": v(49.08, -58.49) * mm, "end": v(49.83, -59.39) * mm});
            skArc(sketch, "E23.44.11", {"start": v(49.73, -60.5) * mm, "mid": v(50.01, -59.97) * mm, "end": v(49.83, -59.39) * mm});
            skArc(sketch, "E23.45.0", {"start": v(57.04, -52.4) * mm, "mid": v(57.62, -52.66) * mm, "end": v(58.2, -52.4) * mm});
            skLineSegment(sketch, "E23.45.1", {"start": v(56.38, -51.7) * mm, "end": v(57.04, -52.4) * mm});
            skArc(sketch, "E23.45.2", {"start": v(56.38, -51.7) * mm, "mid": v(56.27, -51.6) * mm, "end": v(56.15, -51.52) * mm});
            skArc(sketch, "E23.45.3", {"start": v(56.15, -51.52) * mm, "mid": v(55.39, -51.17) * mm, "end": v(54.61, -50.85) * mm});
            skArc(sketch, "E23.45.4", {"start": v(54.61, -50.85) * mm, "mid": v(54.18, -50.81) * mm, "end": v(53.8, -51.01) * mm});
            skLineSegment(sketch, "E23.45.5", {"start": v(53.8, -51.01) * mm, "end": v(53.6, -51.19) * mm});
            skLineSegment(sketch, "E23.45.6", {"start": v(53.42, -51.37) * mm, "end": v(53.6, -51.19) * mm});
            skArc(sketch, "E23.45.7", {"start": v(53.42, -51.37) * mm, "mid": v(53.2, -51.75) * mm, "end": v(53.22, -52.18) * mm});
            skArc(sketch, "E23.45.8", {"start": v(53.82, -53.74) * mm, "mid": v(53.5, -52.97) * mm, "end": v(53.22, -52.18) * mm});
            skArc(sketch, "E23.45.9", {"start": v(53.82, -53.74) * mm, "mid": v(53.9, -53.87) * mm, "end": v(53.99, -53.99) * mm});
            skLineSegment(sketch, "E23.45.10", {"start": v(53.99, -53.99) * mm, "end": v(54.82, -54.82) * mm});
            skArc(sketch, "E23.45.11", {"start": v(54.81, -55.94) * mm, "mid": v(55.05, -55.38) * mm, "end": v(54.82, -54.82) * mm});
            skArc(sketch, "E23.46.0", {"start": v(61.39, -47.24) * mm, "mid": v(62, -47.44) * mm, "end": v(62.55, -47.13) * mm});
            skLineSegment(sketch, "E23.46.1", {"start": v(60.67, -46.58) * mm, "end": v(61.39, -47.24) * mm});
            skArc(sketch, "E23.46.2", {"start": v(60.67, -46.58) * mm, "mid": v(60.56, -46.5) * mm, "end": v(60.42, -46.43) * mm});
            skArc(sketch, "E23.46.3", {"start": v(60.42, -46.43) * mm, "mid": v(59.64, -46.14) * mm, "end": v(58.84, -45.9) * mm});
            skArc(sketch, "E23.46.4", {"start": v(58.84, -45.9) * mm, "mid": v(58.4, -45.9) * mm, "end": v(58.03, -46.13) * mm});
            skLineSegment(sketch, "E23.46.5", {"start": v(58.03, -46.13) * mm, "end": v(57.86, -46.32) * mm});
            skLineSegment(sketch, "E23.46.6", {"start": v(57.7, -46.52) * mm, "end": v(57.86, -46.32) * mm});
            skArc(sketch, "E23.46.7", {"start": v(57.7, -46.52) * mm, "mid": v(57.51, -46.91) * mm, "end": v(57.57, -47.34) * mm});
            skArc(sketch, "E23.46.8", {"start": v(58.3, -48.85) * mm, "mid": v(57.92, -48.1) * mm, "end": v(57.57, -47.34) * mm});
            skArc(sketch, "E23.46.9", {"start": v(58.3, -48.85) * mm, "mid": v(58.38, -48.97) * mm, "end": v(58.49, -49.08) * mm});
            skLineSegment(sketch, "E23.46.10", {"start": v(58.49, -49.08) * mm, "end": v(59.39, -49.83) * mm});
            skArc(sketch, "E23.46.11", {"start": v(59.48, -50.95) * mm, "mid": v(59.67, -50.37) * mm, "end": v(59.39, -49.83) * mm});
            skArc(sketch, "E23.47.0", {"start": v(65.27, -41.7) * mm, "mid": v(65.9, -41.86) * mm, "end": v(66.42, -41.5) * mm});
            skLineSegment(sketch, "E23.47.1", {"start": v(64.5, -41.12) * mm, "end": v(65.27, -41.7) * mm});
            skArc(sketch, "E23.47.2", {"start": v(64.5, -41.12) * mm, "mid": v(64.38, -41.04) * mm, "end": v(64.24, -40.98) * mm});
            skArc(sketch, "E23.47.3", {"start": v(64.24, -40.98) * mm, "mid": v(63.43, -40.77) * mm, "end": v(62.61, -40.6) * mm});
            skArc(sketch, "E23.47.4", {"start": v(62.61, -40.6) * mm, "mid": v(62.18, -40.63) * mm, "end": v(61.83, -40.9) * mm});
            skLineSegment(sketch, "E23.47.5", {"start": v(61.83, -40.9) * mm, "end": v(61.68, -41.1) * mm});
            skLineSegment(sketch, "E23.47.6", {"start": v(61.53, -41.31) * mm, "end": v(61.68, -41.1) * mm});
            skArc(sketch, "E23.47.7", {"start": v(61.53, -41.31) * mm, "mid": v(61.38, -41.72) * mm, "end": v(61.47, -42.15) * mm});
            skArc(sketch, "E23.47.8", {"start": v(62.34, -43.58) * mm, "mid": v(61.89, -42.87) * mm, "end": v(61.47, -42.15) * mm});
            skArc(sketch, "E23.47.9", {"start": v(62.34, -43.58) * mm, "mid": v(62.43, -43.7) * mm, "end": v(62.54, -43.8) * mm});
            skLineSegment(sketch, "E23.47.10", {"start": v(62.54, -43.8) * mm, "end": v(63.5, -44.47) * mm});
            skArc(sketch, "E23.47.11", {"start": v(63.7, -45.57) * mm, "mid": v(63.83, -44.98) * mm, "end": v(63.5, -44.47) * mm});
            skArc(sketch, "E23.48.0", {"start": v(68.66, -35.86) * mm, "mid": v(69.29, -35.95) * mm, "end": v(69.78, -35.55) * mm});
            skLineSegment(sketch, "E23.48.1", {"start": v(67.84, -35.34) * mm, "end": v(68.66, -35.86) * mm});
            skArc(sketch, "E23.48.2", {"start": v(67.84, -35.34) * mm, "mid": v(67.7, -35.27) * mm, "end": v(67.57, -35.23) * mm});
            skArc(sketch, "E23.48.3", {"start": v(67.57, -35.23) * mm, "mid": v(66.74, -35.09) * mm, "end": v(65.91, -34.98) * mm});
            skArc(sketch, "E23.48.4", {"start": v(65.91, -34.98) * mm, "mid": v(65.48, -35.06) * mm, "end": v(65.16, -35.35) * mm});
            skLineSegment(sketch, "E23.48.5", {"start": v(65.16, -35.35) * mm, "end": v(65.03, -35.57) * mm});
            skLineSegment(sketch, "E23.48.6", {"start": v(64.9, -35.8) * mm, "end": v(65.03, -35.57) * mm});
            skArc(sketch, "E23.48.7", {"start": v(64.9, -35.8) * mm, "mid": v(64.78, -36.21) * mm, "end": v(64.91, -36.63) * mm});
            skArc(sketch, "E23.48.8", {"start": v(65.9, -37.98) * mm, "mid": v(65.4, -37.32) * mm, "end": v(64.91, -36.63) * mm});
            skArc(sketch, "E23.48.9", {"start": v(65.9, -37.98) * mm, "mid": v(66, -38.09) * mm, "end": v(66.12, -38.17) * mm});
            skLineSegment(sketch, "E23.48.10", {"start": v(66.12, -38.17) * mm, "end": v(67.14, -38.76) * mm});
            skArc(sketch, "E23.48.11", {"start": v(67.42, -39.85) * mm, "mid": v(67.5, -39.24) * mm, "end": v(67.14, -38.76) * mm});
            skArc(sketch, "E23.49.0", {"start": v(71.52, -29.74) * mm, "mid": v(72.16, -29.78) * mm, "end": v(72.62, -29.33) * mm});
            skLineSegment(sketch, "E23.49.1", {"start": v(70.66, -29.3) * mm, "end": v(71.52, -29.74) * mm});
            skArc(sketch, "E23.49.2", {"start": v(70.66, -29.3) * mm, "mid": v(70.53, -29.23) * mm, "end": v(70.38, -29.2) * mm});
            skArc(sketch, "E23.49.3", {"start": v(70.38, -29.2) * mm, "mid": v(69.55, -29.14) * mm, "end": v(68.71, -29.1) * mm});
            skArc(sketch, "E23.49.4", {"start": v(68.71, -29.1) * mm, "mid": v(68.3, -29.22) * mm, "end": v(68, -29.54) * mm});
            skLineSegment(sketch, "E23.49.5", {"start": v(68, -29.54) * mm, "end": v(67.88, -29.77) * mm});
            skLineSegment(sketch, "E23.49.6", {"start": v(67.77, -30) * mm, "end": v(67.88, -29.77) * mm});
            skArc(sketch, "E23.49.7", {"start": v(67.77, -30) * mm, "mid": v(67.7, -30.43) * mm, "end": v(67.86, -30.83) * mm});
            skArc(sketch, "E23.49.8", {"start": v(68.96, -32.1) * mm, "mid": v(68.4, -31.48) * mm, "end": v(67.86, -30.83) * mm});
            skArc(sketch, "E23.49.9", {"start": v(68.96, -32.1) * mm, "mid": v(69.07, -32.2) * mm, "end": v(69.2, -32.27) * mm});
            skLineSegment(sketch, "E23.49.10", {"start": v(69.2, -32.27) * mm, "end": v(70.26, -32.76) * mm});
            skArc(sketch, "E23.49.11", {"start": v(70.64, -33.82) * mm, "mid": v(70.67, -33.21) * mm, "end": v(70.26, -32.76) * mm});
            skArc(sketch, "E23.50.0", {"start": v(73.84, -23.4) * mm, "mid": v(74.48, -23.38) * mm, "end": v(74.9, -22.9) * mm});
            skLineSegment(sketch, "E23.50.1", {"start": v(72.95, -23.02) * mm, "end": v(73.84, -23.4) * mm});
            skArc(sketch, "E23.50.2", {"start": v(72.95, -23.02) * mm, "mid": v(72.8, -22.98) * mm, "end": v(72.66, -22.96) * mm});
            skArc(sketch, "E23.50.3", {"start": v(72.66, -22.96) * mm, "mid": v(71.82, -22.96) * mm, "end": v(70.99, -23) * mm});
            skArc(sketch, "E23.50.4", {"start": v(70.99, -23) * mm, "mid": v(70.58, -23.15) * mm, "end": v(70.31, -23.5) * mm});
            skLineSegment(sketch, "E23.50.5", {"start": v(70.31, -23.5) * mm, "end": v(70.21, -23.74) * mm});
            skLineSegment(sketch, "E23.50.6", {"start": v(70.12, -23.98) * mm, "end": v(70.21, -23.74) * mm});
            skArc(sketch, "E23.50.7", {"start": v(70.12, -23.98) * mm, "mid": v(70.09, -24.41) * mm, "end": v(70.29, -24.8) * mm});
            skArc(sketch, "E23.50.8", {"start": v(71.5, -25.96) * mm, "mid": v(70.88, -25.4) * mm, "end": v(70.29, -24.8) * mm});
            skArc(sketch, "E23.50.9", {"start": v(71.5, -25.96) * mm, "mid": v(71.61, -26.05) * mm, "end": v(71.74, -26.11) * mm});
            skLineSegment(sketch, "E23.50.10", {"start": v(71.74, -26.11) * mm, "end": v(72.85, -26.52) * mm});
            skArc(sketch, "E23.50.11", {"start": v(73.32, -27.53) * mm, "mid": v(73.3, -26.93) * mm, "end": v(72.85, -26.52) * mm});
            skArc(sketch, "E23.51.0", {"start": v(75.6, -16.87) * mm, "mid": v(76.23, -16.8) * mm, "end": v(76.6, -16.28) * mm});
            skLineSegment(sketch, "E23.51.1", {"start": v(74.67, -16.57) * mm, "end": v(75.6, -16.87) * mm});
            skArc(sketch, "E23.51.2", {"start": v(74.67, -16.57) * mm, "mid": v(74.53, -16.54) * mm, "end": v(74.38, -16.54) * mm});
            skArc(sketch, "E23.51.3", {"start": v(74.38, -16.54) * mm, "mid": v(73.55, -16.62) * mm, "end": v(72.72, -16.73) * mm});
            skArc(sketch, "E23.51.4", {"start": v(72.72, -16.73) * mm, "mid": v(72.33, -16.91) * mm, "end": v(72.1, -17.28) * mm});
            skLineSegment(sketch, "E23.51.5", {"start": v(72.1, -17.28) * mm, "end": v(72.02, -17.53) * mm});
            skLineSegment(sketch, "E23.51.6", {"start": v(71.95, -17.78) * mm, "end": v(72.02, -17.53) * mm});
            skArc(sketch, "E23.51.7", {"start": v(71.95, -17.78) * mm, "mid": v(71.95, -18.21) * mm, "end": v(72.18, -18.58) * mm});
            skArc(sketch, "E23.51.8", {"start": v(73.48, -19.63) * mm, "mid": v(72.82, -19.12) * mm, "end": v(72.18, -18.58) * mm});
            skArc(sketch, "E23.51.9", {"start": v(73.48, -19.63) * mm, "mid": v(73.6, -19.7) * mm, "end": v(73.75, -19.76) * mm});
            skLineSegment(sketch, "E23.51.10", {"start": v(73.75, -19.76) * mm, "end": v(74.88, -20.07) * mm});
            skArc(sketch, "E23.51.11", {"start": v(75.44, -21.04) * mm, "mid": v(75.36, -20.44) * mm, "end": v(74.88, -20.07) * mm});
            skArc(sketch, "E23.52.0", {"start": v(76.78, -10.21) * mm, "mid": v(77.4, -10.09) * mm, "end": v(77.73, -9.54) * mm});
            skLineSegment(sketch, "E23.52.1", {"start": v(75.84, -10) * mm, "end": v(76.78, -10.21) * mm});
            skArc(sketch, "E23.52.2", {"start": v(75.84, -10) * mm, "mid": v(75.69, -9.98) * mm, "end": v(75.54, -10) * mm});
            skArc(sketch, "E23.52.3", {"start": v(75.54, -10) * mm, "mid": v(74.72, -10.14) * mm, "end": v(73.9, -10.33) * mm});
            skArc(sketch, "E23.52.4", {"start": v(73.9, -10.33) * mm, "mid": v(73.53, -10.55) * mm, "end": v(73.32, -10.93) * mm});
            skLineSegment(sketch, "E23.52.5", {"start": v(73.32, -10.93) * mm, "end": v(73.27, -11.18) * mm});
            skLineSegment(sketch, "E23.52.6", {"start": v(73.22, -11.44) * mm, "end": v(73.27, -11.18) * mm});
            skArc(sketch, "E23.52.7", {"start": v(73.22, -11.44) * mm, "mid": v(73.26, -11.87) * mm, "end": v(73.53, -12.22) * mm});
            skArc(sketch, "E23.52.8", {"start": v(74.91, -13.15) * mm, "mid": v(74.2, -12.7) * mm, "end": v(73.53, -12.22) * mm});
            skArc(sketch, "E23.52.9", {"start": v(74.91, -13.15) * mm, "mid": v(75.05, -13.22) * mm, "end": v(75.19, -13.26) * mm});
            skLineSegment(sketch, "E23.52.10", {"start": v(75.19, -13.26) * mm, "end": v(76.35, -13.46) * mm});
            skArc(sketch, "E23.52.11", {"start": v(76.98, -14.38) * mm, "mid": v(76.86, -13.79) * mm, "end": v(76.35, -13.46) * mm});
            skArc(sketch, "E23.53.0", {"start": v(77.38, -3.48) * mm, "mid": v(78, -3.3) * mm, "end": v(78.27, -2.73) * mm});
            skLineSegment(sketch, "E23.53.1", {"start": v(76.42, -3.36) * mm, "end": v(77.38, -3.48) * mm});
            skArc(sketch, "E23.53.2", {"start": v(76.42, -3.36) * mm, "mid": v(76.27, -3.35) * mm, "end": v(76.13, -3.37) * mm});
            skArc(sketch, "E23.53.3", {"start": v(76.13, -3.37) * mm, "mid": v(75.32, -3.6) * mm, "end": v(74.52, -3.85) * mm});
            skArc(sketch, "E23.53.4", {"start": v(74.52, -3.85) * mm, "mid": v(74.16, -4.1) * mm, "end": v(74, -4.5) * mm});
            skLineSegment(sketch, "E23.53.5", {"start": v(74, -4.5) * mm, "end": v(73.97, -4.76) * mm});
            skLineSegment(sketch, "E23.53.6", {"start": v(73.94, -5.01) * mm, "end": v(73.97, -4.76) * mm});
            skArc(sketch, "E23.53.7", {"start": v(73.94, -5.01) * mm, "mid": v(74.02, -5.44) * mm, "end": v(74.31, -5.76) * mm});
            skArc(sketch, "E23.53.8", {"start": v(75.77, -6.57) * mm, "mid": v(75.03, -6.18) * mm, "end": v(74.31, -5.76) * mm});
            skArc(sketch, "E23.53.9", {"start": v(75.77, -6.57) * mm, "mid": v(75.91, -6.63) * mm, "end": v(76.06, -6.65) * mm});
            skLineSegment(sketch, "E23.53.10", {"start": v(76.06, -6.65) * mm, "end": v(77.23, -6.76) * mm});
            skArc(sketch, "E23.53.11", {"start": v(77.95, -7.62) * mm, "mid": v(77.77, -7.04) * mm, "end": v(77.23, -6.76) * mm});
            skArc(sketch, "E23.54.0", {"start": v(77.39, 3.28) * mm, "mid": v(77.98, 3.5) * mm, "end": v(78.2, 4.1) * mm});
            skLineSegment(sketch, "E23.54.1", {"start": v(76.42, 3.32) * mm, "end": v(77.39, 3.28) * mm});
            skArc(sketch, "E23.54.2", {"start": v(76.42, 3.32) * mm, "mid": v(76.27, 3.3) * mm, "end": v(76.13, 3.28) * mm});
            skArc(sketch, "E23.54.3", {"start": v(76.13, 3.28) * mm, "mid": v(75.34, 2.99) * mm, "end": v(74.57, 2.66) * mm});
            skArc(sketch, "E23.54.4", {"start": v(74.57, 2.66) * mm, "mid": v(74.24, 2.38) * mm, "end": v(74.1, 1.97) * mm});
            skLineSegment(sketch, "E23.54.5", {"start": v(74.1, 1.97) * mm, "end": v(74.1, 1.7) * mm});
            skLineSegment(sketch, "E23.54.6", {"start": v(74.1, 1.45) * mm, "end": v(74.1, 1.7) * mm});
            skArc(sketch, "E23.54.7", {"start": v(74.1, 1.45) * mm, "mid": v(74.21, 1.03) * mm, "end": v(74.53, 0.74) * mm});
            skArc(sketch, "E23.54.8", {"start": v(76.06, 0.05) * mm, "mid": v(75.29, 0.38) * mm, "end": v(74.53, 0.74) * mm});
            skArc(sketch, "E23.54.9", {"start": v(76.06, 0.05) * mm, "mid": v(76.2, 0.01) * mm, "end": v(76.35, 0) * mm});
            skLineSegment(sketch, "E23.54.10", {"start": v(76.35, 0) * mm, "end": v(77.53, 0) * mm});
            skArc(sketch, "E23.54.11", {"start": v(78.31, -0.8) * mm, "mid": v(78.08, -0.23) * mm, "end": v(77.53, 0) * mm});
            skArc(sketch, "E23.55.0", {"start": v(76.8, 10) * mm, "mid": v(77.38, 10.3) * mm, "end": v(77.55, 10.9) * mm});
            skLineSegment(sketch, "E23.55.1", {"start": v(75.84, 9.97) * mm, "end": v(76.8, 10) * mm});
            skArc(sketch, "E23.55.2", {"start": v(75.84, 9.97) * mm, "mid": v(75.7, 9.94) * mm, "end": v(75.55, 9.9) * mm});
            skArc(sketch, "E23.55.3", {"start": v(75.55, 9.9) * mm, "mid": v(74.8, 9.54) * mm, "end": v(74.06, 9.15) * mm});
            skArc(sketch, "E23.55.4", {"start": v(74.06, 9.15) * mm, "mid": v(73.75, 8.84) * mm, "end": v(73.65, 8.42) * mm});
            skLineSegment(sketch, "E23.55.5", {"start": v(73.65, 8.42) * mm, "end": v(73.67, 8.16) * mm});
            skLineSegment(sketch, "E23.55.6", {"start": v(73.69, 7.9) * mm, "end": v(73.67, 8.16) * mm});
            skArc(sketch, "E23.55.7", {"start": v(73.69, 7.9) * mm, "mid": v(73.84, 7.5) * mm, "end": v(74.18, 7.23) * mm});
            skArc(sketch, "E23.55.8", {"start": v(75.77, 6.68) * mm, "mid": v(74.97, 6.94) * mm, "end": v(74.18, 7.23) * mm});
            skArc(sketch, "E23.55.9", {"start": v(75.77, 6.68) * mm, "mid": v(75.9, 6.66) * mm, "end": v(76.06, 6.65) * mm});
            skLineSegment(sketch, "E23.55.10", {"start": v(76.06, 6.65) * mm, "end": v(77.23, 6.76) * mm});
            skArc(sketch, "E23.55.11", {"start": v(78.08, 6.03) * mm, "mid": v(77.8, 6.57) * mm, "end": v(77.23, 6.76) * mm});
            skArc(sketch, "E23.56.0", {"start": v(75.64, 16.66) * mm, "mid": v(76.19, 17) * mm, "end": v(76.3, 17.62) * mm});
            skLineSegment(sketch, "E23.56.1", {"start": v(74.68, 16.54) * mm, "end": v(75.64, 16.66) * mm});
            skArc(sketch, "E23.56.2", {"start": v(74.68, 16.54) * mm, "mid": v(74.54, 16.5) * mm, "end": v(74.4, 16.45) * mm});
            skArc(sketch, "E23.56.3", {"start": v(74.4, 16.45) * mm, "mid": v(73.68, 16.02) * mm, "end": v(72.98, 15.57) * mm});
            skArc(sketch, "E23.56.4", {"start": v(72.98, 15.57) * mm, "mid": v(72.7, 15.24) * mm, "end": v(72.64, 14.8) * mm});
            skLineSegment(sketch, "E23.56.5", {"start": v(72.64, 14.8) * mm, "end": v(72.68, 14.55) * mm});
            skLineSegment(sketch, "E23.56.6", {"start": v(72.72, 14.3) * mm, "end": v(72.68, 14.55) * mm});
            skArc(sketch, "E23.56.7", {"start": v(72.72, 14.3) * mm, "mid": v(72.9, 13.9) * mm, "end": v(73.27, 13.67) * mm});
            skArc(sketch, "E23.56.8", {"start": v(74.9, 13.26) * mm, "mid": v(74.08, 13.45) * mm, "end": v(73.27, 13.67) * mm});
            skArc(sketch, "E23.56.9", {"start": v(74.9, 13.26) * mm, "mid": v(75.04, 13.25) * mm, "end": v(75.19, 13.26) * mm});
            skLineSegment(sketch, "E23.56.10", {"start": v(75.19, 13.26) * mm, "end": v(76.35, 13.46) * mm});
            skArc(sketch, "E23.56.11", {"start": v(77.26, 12.82) * mm, "mid": v(76.94, 13.33) * mm, "end": v(76.35, 13.46) * mm});
            skArc(sketch, "E23.57.0", {"start": v(73.9, 23.2) * mm, "mid": v(74.42, 23.57) * mm, "end": v(74.48, 24.2) * mm});
            skLineSegment(sketch, "E23.57.1", {"start": v(72.96, 22.98) * mm, "end": v(73.9, 23.2) * mm});
            skArc(sketch, "E23.57.2", {"start": v(72.96, 22.98) * mm, "mid": v(72.82, 22.94) * mm, "end": v(72.69, 22.87) * mm});
            skArc(sketch, "E23.57.3", {"start": v(72.69, 22.87) * mm, "mid": v(72, 22.38) * mm, "end": v(71.34, 21.87) * mm});
            skArc(sketch, "E23.57.4", {"start": v(71.34, 21.87) * mm, "mid": v(71.1, 21.52) * mm, "end": v(71.07, 21.08) * mm});
            skLineSegment(sketch, "E23.57.5", {"start": v(71.07, 21.08) * mm, "end": v(71.13, 20.83) * mm});
            skLineSegment(sketch, "E23.57.6", {"start": v(71.2, 20.58) * mm, "end": v(71.13, 20.83) * mm});
            skArc(sketch, "E23.57.7", {"start": v(71.2, 20.58) * mm, "mid": v(71.42, 20.2) * mm, "end": v(71.8, 20) * mm});
            skArc(sketch, "E23.57.8", {"start": v(73.45, 19.74) * mm, "mid": v(72.62, 19.85) * mm, "end": v(71.8, 20) * mm});
            skArc(sketch, "E23.57.9", {"start": v(73.45, 19.74) * mm, "mid": v(73.6, 19.74) * mm, "end": v(73.75, 19.76) * mm});
            skLineSegment(sketch, "E23.57.10", {"start": v(73.75, 19.76) * mm, "end": v(74.88, 20.07) * mm});
            skArc(sketch, "E23.57.11", {"start": v(75.85, 19.5) * mm, "mid": v(75.48, 19.98) * mm, "end": v(74.88, 20.07) * mm});
            skArc(sketch, "E23.58.0", {"start": v(71.6, 29.55) * mm, "mid": v(72.08, 29.97) * mm, "end": v(72.09, 30.6) * mm});
            skLineSegment(sketch, "E23.58.1", {"start": v(70.68, 29.25) * mm, "end": v(71.6, 29.55) * mm});
            skArc(sketch, "E23.58.2", {"start": v(70.68, 29.25) * mm, "mid": v(70.54, 29.2) * mm, "end": v(70.42, 29.12) * mm});
            skArc(sketch, "E23.58.3", {"start": v(70.42, 29.12) * mm, "mid": v(69.78, 28.57) * mm, "end": v(69.17, 28) * mm});
            skArc(sketch, "E23.58.4", {"start": v(69.17, 28) * mm, "mid": v(68.95, 27.63) * mm, "end": v(68.96, 27.2) * mm});
            skLineSegment(sketch, "E23.58.5", {"start": v(68.96, 27.2) * mm, "end": v(69.05, 26.95) * mm});
            skLineSegment(sketch, "E23.58.6", {"start": v(69.13, 26.7) * mm, "end": v(69.05, 26.95) * mm});
            skArc(sketch, "E23.58.7", {"start": v(69.13, 26.7) * mm, "mid": v(69.38, 26.35) * mm, "end": v(69.78, 26.18) * mm});
            skArc(sketch, "E23.58.8", {"start": v(71.45, 26.07) * mm, "mid": v(70.62, 26.1) * mm, "end": v(69.78, 26.18) * mm});
            skArc(sketch, "E23.58.9", {"start": v(71.45, 26.07) * mm, "mid": v(71.6, 26.08) * mm, "end": v(71.74, 26.11) * mm});
            skLineSegment(sketch, "E23.58.10", {"start": v(71.74, 26.11) * mm, "end": v(72.85, 26.52) * mm});
            skArc(sketch, "E23.58.11", {"start": v(73.86, 26.04) * mm, "mid": v(73.46, 26.49) * mm, "end": v(72.85, 26.52) * mm});
            skArc(sketch, "E23.59.0", {"start": v(68.75, 35.67) * mm, "mid": v(69.2, 36.14) * mm, "end": v(69.15, 36.77) * mm});
            skLineSegment(sketch, "E23.59.1", {"start": v(67.86, 35.3) * mm, "end": v(68.75, 35.67) * mm});
            skArc(sketch, "E23.59.2", {"start": v(67.86, 35.3) * mm, "mid": v(67.73, 35.23) * mm, "end": v(67.61, 35.14) * mm});
            skArc(sketch, "E23.59.3", {"start": v(67.61, 35.14) * mm, "mid": v(67.02, 34.55) * mm, "end": v(66.46, 33.93) * mm});
            skArc(sketch, "E23.59.4", {"start": v(66.46, 33.93) * mm, "mid": v(66.28, 33.53) * mm, "end": v(66.33, 33.1) * mm});
            skLineSegment(sketch, "E23.59.5", {"start": v(66.33, 33.1) * mm, "end": v(66.43, 32.86) * mm});
            skLineSegment(sketch, "E23.59.6", {"start": v(66.54, 32.63) * mm, "end": v(66.43, 32.86) * mm});
            skArc(sketch, "E23.59.7", {"start": v(66.54, 32.63) * mm, "mid": v(66.82, 32.3) * mm, "end": v(67.24, 32.16) * mm});
            skArc(sketch, "E23.59.8", {"start": v(68.91, 32.2) * mm, "mid": v(68.07, 32.16) * mm, "end": v(67.24, 32.16) * mm});
            skArc(sketch, "E23.59.9", {"start": v(68.91, 32.2) * mm, "mid": v(69.06, 32.22) * mm, "end": v(69.2, 32.27) * mm});
            skLineSegment(sketch, "E23.59.10", {"start": v(69.2, 32.27) * mm, "end": v(70.26, 32.76) * mm});
            skArc(sketch, "E23.59.11", {"start": v(71.31, 32.38) * mm, "mid": v(70.87, 32.79) * mm, "end": v(70.26, 32.76) * mm});
            skArc(sketch, "E23.60.0", {"start": v(65.38, 41.53) * mm, "mid": v(65.78, 42.03) * mm, "end": v(65.68, 42.66) * mm});
            skLineSegment(sketch, "E23.60.1", {"start": v(64.52, 41.08) * mm, "end": v(65.38, 41.53) * mm});
            skArc(sketch, "E23.60.2", {"start": v(64.52, 41.08) * mm, "mid": v(64.4, 41) * mm, "end": v(64.3, 40.9) * mm});
            skArc(sketch, "E23.60.3", {"start": v(64.3, 40.9) * mm, "mid": v(63.76, 40.26) * mm, "end": v(63.25, 39.6) * mm});
            skArc(sketch, "E23.60.4", {"start": v(63.25, 39.6) * mm, "mid": v(63.1, 39.18) * mm, "end": v(63.2, 38.76) * mm});
            skLineSegment(sketch, "E23.60.5", {"start": v(63.2, 38.76) * mm, "end": v(63.32, 38.53) * mm});
            skLineSegment(sketch, "E23.60.6", {"start": v(63.44, 38.3) * mm, "end": v(63.32, 38.53) * mm});
            skArc(sketch, "E23.60.7", {"start": v(63.44, 38.3) * mm, "mid": v(63.75, 38) * mm, "end": v(64.18, 37.9) * mm});
            skArc(sketch, "E23.60.8", {"start": v(65.84, 38.08) * mm, "mid": v(65.01, 37.97) * mm, "end": v(64.18, 37.9) * mm});
            skArc(sketch, "E23.60.9", {"start": v(65.84, 38.08) * mm, "mid": v(65.99, 38.11) * mm, "end": v(66.12, 38.17) * mm});
            skLineSegment(sketch, "E23.60.10", {"start": v(66.12, 38.17) * mm, "end": v(67.14, 38.76) * mm});
            skArc(sketch, "E23.60.11", {"start": v(68.22, 38.47) * mm, "mid": v(67.74, 38.84) * mm, "end": v(67.14, 38.76) * mm});
            skArc(sketch, "E23.61.0", {"start": v(61.51, 47.07) * mm, "mid": v(61.87, 47.6) * mm, "end": v(61.71, 48.22) * mm});
            skLineSegment(sketch, "E23.61.1", {"start": v(60.7, 46.55) * mm, "end": v(61.51, 47.07) * mm});
            skArc(sketch, "E23.61.2", {"start": v(60.7, 46.55) * mm, "mid": v(60.58, 46.46) * mm, "end": v(60.48, 46.35) * mm});
            skArc(sketch, "E23.61.3", {"start": v(60.48, 46.35) * mm, "mid": v(60, 45.66) * mm, "end": v(59.56, 44.95) * mm});
            skArc(sketch, "E23.61.4", {"start": v(59.56, 44.95) * mm, "mid": v(59.45, 44.53) * mm, "end": v(59.58, 44.12) * mm});
            skLineSegment(sketch, "E23.61.5", {"start": v(59.58, 44.12) * mm, "end": v(59.72, 43.9) * mm});
            skLineSegment(sketch, "E23.61.6", {"start": v(59.86, 43.69) * mm, "end": v(59.72, 43.9) * mm});
            skArc(sketch, "E23.61.7", {"start": v(59.86, 43.69) * mm, "mid": v(60.2, 43.4) * mm, "end": v(60.63, 43.35) * mm});
            skArc(sketch, "E23.61.8", {"start": v(62.27, 43.67) * mm, "mid": v(61.46, 43.5) * mm, "end": v(60.63, 43.35) * mm});
            skArc(sketch, "E23.61.9", {"start": v(62.27, 43.67) * mm, "mid": v(62.41, 43.72) * mm, "end": v(62.54, 43.8) * mm});
            skLineSegment(sketch, "E23.61.10", {"start": v(62.54, 43.8) * mm, "end": v(63.5, 44.47) * mm});
            skArc(sketch, "E23.61.11", {"start": v(64.6, 44.27) * mm, "mid": v(64.1, 44.6) * mm, "end": v(63.5, 44.47) * mm});
            skArc(sketch, "E23.62.0", {"start": v(57.18, 52.25) * mm, "mid": v(57.48, 52.81) * mm, "end": v(57.27, 53.41) * mm});
            skLineSegment(sketch, "E23.62.1", {"start": v(56.4, 51.66) * mm, "end": v(57.18, 52.25) * mm});
            skArc(sketch, "E23.62.2", {"start": v(56.4, 51.66) * mm, "mid": v(56.3, 51.56) * mm, "end": v(56.21, 51.44) * mm});
            skArc(sketch, "E23.62.3", {"start": v(56.21, 51.44) * mm, "mid": v(55.8, 50.72) * mm, "end": v(55.42, 49.97) * mm});
            skArc(sketch, "E23.62.4", {"start": v(55.42, 49.97) * mm, "mid": v(55.34, 49.54) * mm, "end": v(55.5, 49.14) * mm});
            skLineSegment(sketch, "E23.62.5", {"start": v(55.5, 49.14) * mm, "end": v(55.66, 48.94) * mm});
            skLineSegment(sketch, "E23.62.6", {"start": v(55.83, 48.74) * mm, "end": v(55.66, 48.94) * mm});
            skArc(sketch, "E23.62.7", {"start": v(55.83, 48.74) * mm, "mid": v(56.19, 48.5) * mm, "end": v(56.62, 48.47) * mm});
            skArc(sketch, "E23.62.8", {"start": v(58.23, 48.93) * mm, "mid": v(57.43, 48.68) * mm, "end": v(56.62, 48.47) * mm});
            skArc(sketch, "E23.62.9", {"start": v(58.23, 48.93) * mm, "mid": v(58.36, 49) * mm, "end": v(58.49, 49.08) * mm});
            skLineSegment(sketch, "E23.62.10", {"start": v(58.49, 49.08) * mm, "end": v(59.39, 49.83) * mm});
            skArc(sketch, "E23.62.11", {"start": v(60.5, 49.73) * mm, "mid": v(59.97, 50.01) * mm, "end": v(59.39, 49.83) * mm});
            skArc(sketch, "E23.63.0", {"start": v(52.4, 57.04) * mm, "mid": v(52.66, 57.62) * mm, "end": v(52.4, 58.2) * mm});
            skLineSegment(sketch, "E23.63.1", {"start": v(51.7, 56.38) * mm, "end": v(52.4, 57.04) * mm});
            skArc(sketch, "E23.63.2", {"start": v(51.7, 56.38) * mm, "mid": v(51.6, 56.27) * mm, "end": v(51.52, 56.15) * mm});
            skArc(sketch, "E23.63.3", {"start": v(51.52, 56.15) * mm, "mid": v(51.17, 55.39) * mm, "end": v(50.85, 54.61) * mm});
            skArc(sketch, "E23.63.4", {"start": v(50.85, 54.61) * mm, "mid": v(50.81, 54.18) * mm, "end": v(51.01, 53.8) * mm});
            skLineSegment(sketch, "E23.63.5", {"start": v(51.01, 53.8) * mm, "end": v(51.19, 53.6) * mm});
            skLineSegment(sketch, "E23.63.6", {"start": v(51.37, 53.42) * mm, "end": v(51.19, 53.6) * mm});
            skArc(sketch, "E23.63.7", {"start": v(51.37, 53.42) * mm, "mid": v(51.75, 53.2) * mm, "end": v(52.18, 53.22) * mm});
            skArc(sketch, "E23.63.8", {"start": v(53.74, 53.82) * mm, "mid": v(52.97, 53.5) * mm, "end": v(52.18, 53.22) * mm});
            skArc(sketch, "E23.63.9", {"start": v(53.74, 53.82) * mm, "mid": v(53.87, 53.9) * mm, "end": v(53.99, 53.99) * mm});
            skLineSegment(sketch, "E23.63.10", {"start": v(53.99, 53.99) * mm, "end": v(54.82, 54.82) * mm});
            skArc(sketch, "E23.63.11", {"start": v(55.94, 54.81) * mm, "mid": v(55.38, 55.05) * mm, "end": v(54.82, 54.82) * mm});
            skArc(sketch, "E23.64.0", {"start": v(47.24, 61.39) * mm, "mid": v(47.44, 62) * mm, "end": v(47.13, 62.55) * mm});
            skLineSegment(sketch, "E23.64.1", {"start": v(46.58, 60.67) * mm, "end": v(47.24, 61.39) * mm});
            skArc(sketch, "E23.64.2", {"start": v(46.58, 60.67) * mm, "mid": v(46.5, 60.56) * mm, "end": v(46.43, 60.42) * mm});
            skArc(sketch, "E23.64.3", {"start": v(46.43, 60.42) * mm, "mid": v(46.14, 59.64) * mm, "end": v(45.9, 58.84) * mm});
            skArc(sketch, "E23.64.4", {"start": v(45.9, 58.84) * mm, "mid": v(45.9, 58.4) * mm, "end": v(46.13, 58.03) * mm});
            skLineSegment(sketch, "E23.64.5", {"start": v(46.13, 58.03) * mm, "end": v(46.32, 57.86) * mm});
            skLineSegment(sketch, "E23.64.6", {"start": v(46.52, 57.7) * mm, "end": v(46.32, 57.86) * mm});
            skArc(sketch, "E23.64.7", {"start": v(46.52, 57.7) * mm, "mid": v(46.91, 57.51) * mm, "end": v(47.34, 57.57) * mm});
            skArc(sketch, "E23.64.8", {"start": v(48.85, 58.3) * mm, "mid": v(48.1, 57.92) * mm, "end": v(47.34, 57.57) * mm});
            skArc(sketch, "E23.64.9", {"start": v(48.85, 58.3) * mm, "mid": v(48.97, 58.38) * mm, "end": v(49.08, 58.49) * mm});
            skLineSegment(sketch, "E23.64.10", {"start": v(49.08, 58.49) * mm, "end": v(49.83, 59.39) * mm});
            skArc(sketch, "E23.64.11", {"start": v(50.95, 59.48) * mm, "mid": v(50.37, 59.67) * mm, "end": v(49.83, 59.39) * mm});
            skArc(sketch, "E23.65.0", {"start": v(41.7, 65.27) * mm, "mid": v(41.86, 65.9) * mm, "end": v(41.5, 66.42) * mm});
            skLineSegment(sketch, "E23.65.1", {"start": v(41.12, 64.5) * mm, "end": v(41.7, 65.27) * mm});
            skArc(sketch, "E23.65.2", {"start": v(41.12, 64.5) * mm, "mid": v(41.04, 64.38) * mm, "end": v(40.98, 64.24) * mm});
            skArc(sketch, "E23.65.3", {"start": v(40.98, 64.24) * mm, "mid": v(40.77, 63.43) * mm, "end": v(40.6, 62.61) * mm});
            skArc(sketch, "E23.65.4", {"start": v(40.6, 62.61) * mm, "mid": v(40.63, 62.18) * mm, "end": v(40.9, 61.83) * mm});
            skLineSegment(sketch, "E23.65.5", {"start": v(40.9, 61.83) * mm, "end": v(41.1, 61.68) * mm});
            skLineSegment(sketch, "E23.65.6", {"start": v(41.31, 61.53) * mm, "end": v(41.1, 61.68) * mm});
            skArc(sketch, "E23.65.7", {"start": v(41.31, 61.53) * mm, "mid": v(41.72, 61.38) * mm, "end": v(42.15, 61.47) * mm});
            skArc(sketch, "E23.65.8", {"start": v(43.58, 62.34) * mm, "mid": v(42.87, 61.89) * mm, "end": v(42.15, 61.47) * mm});
            skArc(sketch, "E23.65.9", {"start": v(43.58, 62.34) * mm, "mid": v(43.7, 62.43) * mm, "end": v(43.8, 62.54) * mm});
            skLineSegment(sketch, "E23.65.10", {"start": v(43.8, 62.54) * mm, "end": v(44.47, 63.5) * mm});
            skArc(sketch, "E23.65.11", {"start": v(45.57, 63.7) * mm, "mid": v(44.98, 63.83) * mm, "end": v(44.47, 63.5) * mm});
            skArc(sketch, "E23.66.0", {"start": v(35.86, 68.66) * mm, "mid": v(35.95, 69.29) * mm, "end": v(35.55, 69.78) * mm});
            skLineSegment(sketch, "E23.66.1", {"start": v(35.34, 67.84) * mm, "end": v(35.86, 68.66) * mm});
            skArc(sketch, "E23.66.2", {"start": v(35.34, 67.84) * mm, "mid": v(35.27, 67.7) * mm, "end": v(35.23, 67.57) * mm});
            skArc(sketch, "E23.66.3", {"start": v(35.23, 67.57) * mm, "mid": v(35.09, 66.74) * mm, "end": v(34.98, 65.91) * mm});
            skArc(sketch, "E23.66.4", {"start": v(34.98, 65.91) * mm, "mid": v(35.06, 65.48) * mm, "end": v(35.35, 65.16) * mm});
            skLineSegment(sketch, "E23.66.5", {"start": v(35.35, 65.16) * mm, "end": v(35.57, 65.03) * mm});
            skLineSegment(sketch, "E23.66.6", {"start": v(35.8, 64.9) * mm, "end": v(35.57, 65.03) * mm});
            skArc(sketch, "E23.66.7", {"start": v(35.8, 64.9) * mm, "mid": v(36.21, 64.78) * mm, "end": v(36.63, 64.91) * mm});
            skArc(sketch, "E23.66.8", {"start": v(37.98, 65.9) * mm, "mid": v(37.32, 65.4) * mm, "end": v(36.63, 64.91) * mm});
            skArc(sketch, "E23.66.9", {"start": v(37.98, 65.9) * mm, "mid": v(38.09, 66) * mm, "end": v(38.17, 66.12) * mm});
            skLineSegment(sketch, "E23.66.10", {"start": v(38.17, 66.12) * mm, "end": v(38.76, 67.14) * mm});
            skArc(sketch, "E23.66.11", {"start": v(39.85, 67.42) * mm, "mid": v(39.24, 67.5) * mm, "end": v(38.76, 67.14) * mm});
            skArc(sketch, "E23.67.0", {"start": v(29.74, 71.52) * mm, "mid": v(29.78, 72.16) * mm, "end": v(29.33, 72.62) * mm});
            skLineSegment(sketch, "E23.67.1", {"start": v(29.3, 70.66) * mm, "end": v(29.74, 71.52) * mm});
            skArc(sketch, "E23.67.2", {"start": v(29.3, 70.66) * mm, "mid": v(29.23, 70.53) * mm, "end": v(29.2, 70.38) * mm});
            skArc(sketch, "E23.67.3", {"start": v(29.2, 70.38) * mm, "mid": v(29.14, 69.55) * mm, "end": v(29.1, 68.71) * mm});
            skArc(sketch, "E23.67.4", {"start": v(29.1, 68.71) * mm, "mid": v(29.22, 68.3) * mm, "end": v(29.54, 68) * mm});
            skLineSegment(sketch, "E23.67.5", {"start": v(29.54, 68) * mm, "end": v(29.77, 67.88) * mm});
            skLineSegment(sketch, "E23.67.6", {"start": v(30, 67.77) * mm, "end": v(29.77, 67.88) * mm});
            skArc(sketch, "E23.67.7", {"start": v(30, 67.77) * mm, "mid": v(30.43, 67.7) * mm, "end": v(30.83, 67.86) * mm});
            skArc(sketch, "E23.67.8", {"start": v(32.1, 68.96) * mm, "mid": v(31.48, 68.4) * mm, "end": v(30.83, 67.86) * mm});
            skArc(sketch, "E23.67.9", {"start": v(32.1, 68.96) * mm, "mid": v(32.2, 69.07) * mm, "end": v(32.27, 69.2) * mm});
            skLineSegment(sketch, "E23.67.10", {"start": v(32.27, 69.2) * mm, "end": v(32.76, 70.26) * mm});
            skArc(sketch, "E23.67.11", {"start": v(33.82, 70.64) * mm, "mid": v(33.21, 70.67) * mm, "end": v(32.76, 70.26) * mm});
            skArc(sketch, "E23.68.0", {"start": v(23.4, 73.84) * mm, "mid": v(23.38, 74.48) * mm, "end": v(22.9, 74.9) * mm});
            skLineSegment(sketch, "E23.68.1", {"start": v(23.02, 72.95) * mm, "end": v(23.4, 73.84) * mm});
            skArc(sketch, "E23.68.2", {"start": v(23.02, 72.95) * mm, "mid": v(22.98, 72.8) * mm, "end": v(22.96, 72.66) * mm});
            skArc(sketch, "E23.68.3", {"start": v(22.96, 72.66) * mm, "mid": v(22.96, 71.82) * mm, "end": v(23, 70.99) * mm});
            skArc(sketch, "E23.68.4", {"start": v(23, 70.99) * mm, "mid": v(23.15, 70.58) * mm, "end": v(23.5, 70.31) * mm});
            skLineSegment(sketch, "E23.68.5", {"start": v(23.5, 70.31) * mm, "end": v(23.74, 70.21) * mm});
            skLineSegment(sketch, "E23.68.6", {"start": v(23.98, 70.12) * mm, "end": v(23.74, 70.21) * mm});
            skArc(sketch, "E23.68.7", {"start": v(23.98, 70.12) * mm, "mid": v(24.41, 70.09) * mm, "end": v(24.8, 70.29) * mm});
            skArc(sketch, "E23.68.8", {"start": v(25.96, 71.5) * mm, "mid": v(25.4, 70.88) * mm, "end": v(24.8, 70.29) * mm});
            skArc(sketch, "E23.68.9", {"start": v(25.96, 71.5) * mm, "mid": v(26.05, 71.61) * mm, "end": v(26.11, 71.74) * mm});
            skLineSegment(sketch, "E23.68.10", {"start": v(26.11, 71.74) * mm, "end": v(26.52, 72.85) * mm});
            skArc(sketch, "E23.68.11", {"start": v(27.53, 73.32) * mm, "mid": v(26.93, 73.3) * mm, "end": v(26.52, 72.85) * mm});
            skArc(sketch, "E23.69.0", {"start": v(16.87, 75.6) * mm, "mid": v(16.8, 76.23) * mm, "end": v(16.28, 76.6) * mm});
            skLineSegment(sketch, "E23.69.1", {"start": v(16.57, 74.67) * mm, "end": v(16.87, 75.6) * mm});
            skArc(sketch, "E23.69.2", {"start": v(16.57, 74.67) * mm, "mid": v(16.54, 74.53) * mm, "end": v(16.54, 74.38) * mm});
            skArc(sketch, "E23.69.3", {"start": v(16.54, 74.38) * mm, "mid": v(16.62, 73.55) * mm, "end": v(16.73, 72.72) * mm});
            skArc(sketch, "E23.69.4", {"start": v(16.73, 72.72) * mm, "mid": v(16.91, 72.33) * mm, "end": v(17.28, 72.1) * mm});
            skLineSegment(sketch, "E23.69.5", {"start": v(17.28, 72.1) * mm, "end": v(17.53, 72.02) * mm});
            skLineSegment(sketch, "E23.69.6", {"start": v(17.78, 71.95) * mm, "end": v(17.53, 72.02) * mm});
            skArc(sketch, "E23.69.7", {"start": v(17.78, 71.95) * mm, "mid": v(18.21, 71.95) * mm, "end": v(18.58, 72.18) * mm});
            skArc(sketch, "E23.69.8", {"start": v(19.63, 73.48) * mm, "mid": v(19.12, 72.82) * mm, "end": v(18.58, 72.18) * mm});
            skArc(sketch, "E23.69.9", {"start": v(19.63, 73.48) * mm, "mid": v(19.7, 73.6) * mm, "end": v(19.76, 73.75) * mm});
            skLineSegment(sketch, "E23.69.10", {"start": v(19.76, 73.75) * mm, "end": v(20.07, 74.88) * mm});
            skArc(sketch, "E23.69.11", {"start": v(21.04, 75.44) * mm, "mid": v(20.44, 75.36) * mm, "end": v(20.07, 74.88) * mm});
            skArc(sketch, "E23.70.0", {"start": v(10.21, 76.78) * mm, "mid": v(10.09, 77.4) * mm, "end": v(9.54, 77.73) * mm});
            skLineSegment(sketch, "E23.70.1", {"start": v(10, 75.84) * mm, "end": v(10.21, 76.78) * mm});
            skArc(sketch, "E23.70.2", {"start": v(10, 75.84) * mm, "mid": v(9.98, 75.69) * mm, "end": v(10, 75.54) * mm});
            skArc(sketch, "E23.70.3", {"start": v(10, 75.54) * mm, "mid": v(10.14, 74.72) * mm, "end": v(10.33, 73.9) * mm});
            skArc(sketch, "E23.70.4", {"start": v(10.33, 73.9) * mm, "mid": v(10.55, 73.53) * mm, "end": v(10.93, 73.32) * mm});
            skLineSegment(sketch, "E23.70.5", {"start": v(10.93, 73.32) * mm, "end": v(11.18, 73.27) * mm});
            skLineSegment(sketch, "E23.70.6", {"start": v(11.44, 73.22) * mm, "end": v(11.18, 73.27) * mm});
            skArc(sketch, "E23.70.7", {"start": v(11.44, 73.22) * mm, "mid": v(11.87, 73.26) * mm, "end": v(12.22, 73.53) * mm});
            skArc(sketch, "E23.70.8", {"start": v(13.15, 74.91) * mm, "mid": v(12.7, 74.2) * mm, "end": v(12.22, 73.53) * mm});
            skArc(sketch, "E23.70.9", {"start": v(13.15, 74.91) * mm, "mid": v(13.22, 75.05) * mm, "end": v(13.26, 75.19) * mm});
            skLineSegment(sketch, "E23.70.10", {"start": v(13.26, 75.19) * mm, "end": v(13.46, 76.35) * mm});
            skArc(sketch, "E23.70.11", {"start": v(14.38, 76.98) * mm, "mid": v(13.79, 76.86) * mm, "end": v(13.46, 76.35) * mm});
            skArc(sketch, "E23.71.0", {"start": v(3.48, 77.38) * mm, "mid": v(3.3, 78) * mm, "end": v(2.73, 78.27) * mm});
            skLineSegment(sketch, "E23.71.1", {"start": v(3.36, 76.42) * mm, "end": v(3.48, 77.38) * mm});
            skArc(sketch, "E23.71.2", {"start": v(3.36, 76.42) * mm, "mid": v(3.35, 76.27) * mm, "end": v(3.37, 76.13) * mm});
            skArc(sketch, "E23.71.3", {"start": v(3.37, 76.13) * mm, "mid": v(3.6, 75.32) * mm, "end": v(3.85, 74.52) * mm});
            skArc(sketch, "E23.71.4", {"start": v(3.85, 74.52) * mm, "mid": v(4.1, 74.16) * mm, "end": v(4.5, 74) * mm});
            skLineSegment(sketch, "E23.71.5", {"start": v(4.5, 74) * mm, "end": v(4.76, 73.97) * mm});
            skLineSegment(sketch, "E23.71.6", {"start": v(5.01, 73.94) * mm, "end": v(4.76, 73.97) * mm});
            skArc(sketch, "E23.71.7", {"start": v(5.01, 73.94) * mm, "mid": v(5.44, 74.02) * mm, "end": v(5.76, 74.31) * mm});
            skArc(sketch, "E23.71.8", {"start": v(6.57, 75.77) * mm, "mid": v(6.18, 75.03) * mm, "end": v(5.76, 74.31) * mm});
            skArc(sketch, "E23.71.9", {"start": v(6.57, 75.77) * mm, "mid": v(6.63, 75.91) * mm, "end": v(6.65, 76.06) * mm});
            skLineSegment(sketch, "E23.71.10", {"start": v(6.65, 76.06) * mm, "end": v(6.76, 77.23) * mm});
            skArc(sketch, "E23.71.11", {"start": v(7.62, 77.95) * mm, "mid": v(7.04, 77.77) * mm, "end": v(6.76, 77.23) * mm});
            skArc(sketch, "E24.trimOffspring", {"start": v(-10.9, 77.55) * mm, "mid": v(-11.86, 77.41) * mm, "end": v(-12.82, 77.26) * mm});
            skArc(sketch, "E25.trimOffspring", {"start": v(-17.62, 76.3) * mm, "mid": v(-18.56, 76.09) * mm, "end": v(-19.5, 75.85) * mm});
            skArc(sketch, "E26.trimOffspring", {"start": v(-24.2, 74.48) * mm, "mid": v(-25.12, 74.18) * mm, "end": v(-26.04, 73.86) * mm});
            skArc(sketch, "E27.trimOffspring", {"start": v(-30.6, 72.09) * mm, "mid": v(-31.5, 71.7) * mm, "end": v(-32.38, 71.31) * mm});
            skArc(sketch, "E28.trimOffspring", {"start": v(-36.77, 69.15) * mm, "mid": v(-37.62, 68.69) * mm, "end": v(-38.47, 68.22) * mm});
            skArc(sketch, "E29.trimOffspring", {"start": v(-42.66, 65.68) * mm, "mid": v(-43.47, 65.15) * mm, "end": v(-44.27, 64.6) * mm});
            skArc(sketch, "E30.trimOffspring", {"start": v(-48.22, 61.71) * mm, "mid": v(-48.98, 61.11) * mm, "end": v(-49.73, 60.5) * mm});
            skArc(sketch, "E31.trimOffspring", {"start": v(-53.41, 57.27) * mm, "mid": v(-54.12, 56.61) * mm, "end": v(-54.81, 55.94) * mm});
            skArc(sketch, "E32.trimOffspring", {"start": v(-58.2, 52.4) * mm, "mid": v(-58.85, 51.68) * mm, "end": v(-59.48, 50.95) * mm});
            skArc(sketch, "E33.trimOffspring", {"start": v(-62.55, 47.13) * mm, "mid": v(-63.13, 46.35) * mm, "end": v(-63.7, 45.57) * mm});
            skArc(sketch, "E34.trimOffspring", {"start": v(-66.42, 41.5) * mm, "mid": v(-66.93, 40.67) * mm, "end": v(-67.42, 39.85) * mm});
            skArc(sketch, "E35.trimOffspring", {"start": v(-69.78, 35.55) * mm, "mid": v(-70.22, 34.69) * mm, "end": v(-70.64, 33.82) * mm});
            skArc(sketch, "E36.trimOffspring", {"start": v(-72.62, 29.33) * mm, "mid": v(-72.97, 28.44) * mm, "end": v(-73.32, 27.53) * mm});
            skArc(sketch, "E37.trimOffspring", {"start": v(-74.9, 22.9) * mm, "mid": v(-75.17, 21.97) * mm, "end": v(-75.44, 21.04) * mm});
            skArc(sketch, "E38.trimOffspring", {"start": v(-76.6, 16.28) * mm, "mid": v(-76.8, 15.33) * mm, "end": v(-76.98, 14.38) * mm});
            skArc(sketch, "E39.trimOffspring", {"start": v(-77.73, 9.54) * mm, "mid": v(-77.85, 8.58) * mm, "end": v(-77.95, 7.62) * mm});
            skArc(sketch, "E40.trimOffspring", {"start": v(-78.27, 2.73) * mm, "mid": v(-78.3, 1.76) * mm, "end": v(-78.31, 0.8) * mm});
            skArc(sketch, "E41.trimOffspring", {"start": v(-78.2, -4.1) * mm, "mid": v(-78.15, -5.07) * mm, "end": v(-78.08, -6.03) * mm});
            skArc(sketch, "E42.trimOffspring", {"start": v(-77.55, -10.9) * mm, "mid": v(-77.41, -11.86) * mm, "end": v(-77.26, -12.82) * mm});
            skArc(sketch, "E43.trimOffspring", {"start": v(-76.3, -17.62) * mm, "mid": v(-76.09, -18.56) * mm, "end": v(-75.85, -19.5) * mm});
            skArc(sketch, "E44.trimOffspring", {"start": v(-74.48, -24.2) * mm, "mid": v(-74.18, -25.12) * mm, "end": v(-73.86, -26.04) * mm});
            skArc(sketch, "E45.trimOffspring", {"start": v(-69.15, -36.77) * mm, "mid": v(-68.69, -37.62) * mm, "end": v(-68.22, -38.47) * mm});
            skArc(sketch, "E46.trimOffspring", {"start": v(-65.68, -42.66) * mm, "mid": v(-65.15, -43.47) * mm, "end": v(-64.6, -44.27) * mm});
            skArc(sketch, "E47.trimOffspring", {"start": v(-61.71, -48.22) * mm, "mid": v(-61.11, -48.98) * mm, "end": v(-60.5, -49.73) * mm});
            skArc(sketch, "E48.trimOffspring", {"start": v(-57.27, -53.41) * mm, "mid": v(-56.61, -54.12) * mm, "end": v(-55.94, -54.81) * mm});
            skArc(sketch, "E49.trimOffspring", {"start": v(-52.4, -58.2) * mm, "mid": v(-51.68, -58.85) * mm, "end": v(-50.95, -59.48) * mm});
            skArc(sketch, "E50.trimOffspring", {"start": v(-47.13, -62.55) * mm, "mid": v(-46.35, -63.13) * mm, "end": v(-45.57, -63.7) * mm});
            skArc(sketch, "E51.trimOffspring", {"start": v(-41.5, -66.42) * mm, "mid": v(-40.67, -66.93) * mm, "end": v(-39.85, -67.42) * mm});
            skArc(sketch, "E52.trimOffspring", {"start": v(-35.55, -69.78) * mm, "mid": v(-34.69, -70.22) * mm, "end": v(-33.82, -70.64) * mm});
            skArc(sketch, "E53.trimOffspring", {"start": v(-29.33, -72.62) * mm, "mid": v(-28.44, -72.97) * mm, "end": v(-27.53, -73.32) * mm});
            skArc(sketch, "E54.trimOffspring", {"start": v(-22.9, -74.9) * mm, "mid": v(-21.97, -75.17) * mm, "end": v(-21.04, -75.44) * mm});
            skArc(sketch, "E55.trimOffspring", {"start": v(-16.28, -76.6) * mm, "mid": v(-15.33, -76.8) * mm, "end": v(-14.38, -76.98) * mm});
            skArc(sketch, "E56.trimOffspring", {"start": v(-9.54, -77.73) * mm, "mid": v(-8.58, -77.85) * mm, "end": v(-7.62, -77.95) * mm});
            skArc(sketch, "E57.trimOffspring", {"start": v(-2.73, -78.27) * mm, "mid": v(-1.76, -78.3) * mm, "end": v(-0.8, -78.31) * mm});
            skArc(sketch, "E58.trimOffspring", {"start": v(4.1, -78.2) * mm, "mid": v(5.07, -78.15) * mm, "end": v(6.03, -78.08) * mm});
            skArc(sketch, "E59.trimOffspring", {"start": v(10.9, -77.55) * mm, "mid": v(11.86, -77.41) * mm, "end": v(12.82, -77.26) * mm});
            skArc(sketch, "E60.trimOffspring", {"start": v(17.62, -76.3) * mm, "mid": v(18.56, -76.09) * mm, "end": v(19.5, -75.85) * mm});
            skArc(sketch, "E61.trimOffspring", {"start": v(24.2, -74.48) * mm, "mid": v(25.12, -74.18) * mm, "end": v(26.04, -73.86) * mm});
            skArc(sketch, "E62.trimOffspring", {"start": v(30.6, -72.09) * mm, "mid": v(31.5, -71.7) * mm, "end": v(32.38, -71.31) * mm});
            skArc(sketch, "E63.trimOffspring", {"start": v(36.77, -69.15) * mm, "mid": v(37.62, -68.69) * mm, "end": v(38.47, -68.22) * mm});
            skArc(sketch, "E64.trimOffspring", {"start": v(42.66, -65.68) * mm, "mid": v(43.47, -65.15) * mm, "end": v(44.27, -64.6) * mm});
            skArc(sketch, "E65.trimOffspring", {"start": v(48.22, -61.71) * mm, "mid": v(48.98, -61.11) * mm, "end": v(49.73, -60.5) * mm});
            skArc(sketch, "E66.trimOffspring", {"start": v(53.41, -57.27) * mm, "mid": v(54.12, -56.61) * mm, "end": v(54.81, -55.94) * mm});
            skArc(sketch, "E67.trimOffspring", {"start": v(58.2, -52.4) * mm, "mid": v(58.85, -51.68) * mm, "end": v(59.48, -50.95) * mm});
            skArc(sketch, "E68.trimOffspring", {"start": v(62.55, -47.13) * mm, "mid": v(63.13, -46.35) * mm, "end": v(63.7, -45.57) * mm});
            skArc(sketch, "E69.trimOffspring", {"start": v(66.42, -41.5) * mm, "mid": v(66.93, -40.67) * mm, "end": v(67.42, -39.85) * mm});
            skArc(sketch, "E70.trimOffspring", {"start": v(69.78, -35.55) * mm, "mid": v(70.22, -34.69) * mm, "end": v(70.64, -33.82) * mm});
            skArc(sketch, "E71.trimOffspring", {"start": v(72.62, -29.33) * mm, "mid": v(72.97, -28.44) * mm, "end": v(73.32, -27.53) * mm});
            skArc(sketch, "E72.trimOffspring", {"start": v(74.9, -22.9) * mm, "mid": v(75.17, -21.97) * mm, "end": v(75.44, -21.04) * mm});
            skArc(sketch, "E73.trimOffspring", {"start": v(76.6, -16.28) * mm, "mid": v(76.8, -15.33) * mm, "end": v(76.98, -14.38) * mm});
            skArc(sketch, "E74.trimOffspring", {"start": v(77.73, -9.54) * mm, "mid": v(77.85, -8.58) * mm, "end": v(77.95, -7.62) * mm});
            skArc(sketch, "E75.trimOffspring", {"start": v(78.27, -2.73) * mm, "mid": v(78.3, -1.76) * mm, "end": v(78.31, -0.8) * mm});
            skArc(sketch, "E76.trimOffspring", {"start": v(78.2, 4.1) * mm, "mid": v(78.15, 5.07) * mm, "end": v(78.08, 6.03) * mm});
            skArc(sketch, "E77.trimOffspring", {"start": v(77.55, 10.9) * mm, "mid": v(77.41, 11.86) * mm, "end": v(77.26, 12.82) * mm});
            skArc(sketch, "E78.trimOffspring", {"start": v(76.3, 17.62) * mm, "mid": v(76.09, 18.56) * mm, "end": v(75.85, 19.5) * mm});
            skArc(sketch, "E79.trimOffspring", {"start": v(74.48, 24.2) * mm, "mid": v(74.18, 25.12) * mm, "end": v(73.86, 26.04) * mm});
            skArc(sketch, "E80.trimOffspring", {"start": v(72.09, 30.6) * mm, "mid": v(71.7, 31.5) * mm, "end": v(71.31, 32.38) * mm});
            skArc(sketch, "E81.trimOffspring", {"start": v(69.15, 36.77) * mm, "mid": v(68.69, 37.62) * mm, "end": v(68.22, 38.47) * mm});
            skArc(sketch, "E82.trimOffspring", {"start": v(65.68, 42.66) * mm, "mid": v(65.15, 43.47) * mm, "end": v(64.6, 44.27) * mm});
            skArc(sketch, "E83.trimOffspring", {"start": v(61.71, 48.22) * mm, "mid": v(61.11, 48.98) * mm, "end": v(60.5, 49.73) * mm});
            skArc(sketch, "E84.trimOffspring", {"start": v(57.27, 53.41) * mm, "mid": v(56.61, 54.12) * mm, "end": v(55.94, 54.81) * mm});
            skArc(sketch, "E85.trimOffspring", {"start": v(52.4, 58.2) * mm, "mid": v(51.68, 58.85) * mm, "end": v(50.95, 59.48) * mm});
            skArc(sketch, "E86.trimOffspring", {"start": v(47.13, 62.55) * mm, "mid": v(46.35, 63.13) * mm, "end": v(45.57, 63.7) * mm});
            skArc(sketch, "E87.trimOffspring", {"start": v(41.5, 66.42) * mm, "mid": v(40.67, 66.93) * mm, "end": v(39.85, 67.42) * mm});
            skArc(sketch, "E88.trimOffspring", {"start": v(35.55, 69.78) * mm, "mid": v(34.69, 70.22) * mm, "end": v(33.82, 70.64) * mm});
            skArc(sketch, "E89.trimOffspring", {"start": v(29.33, 72.62) * mm, "mid": v(28.44, 72.97) * mm, "end": v(27.53, 73.32) * mm});
            skArc(sketch, "E90.trimOffspring", {"start": v(22.9, 74.9) * mm, "mid": v(21.97, 75.17) * mm, "end": v(21.04, 75.44) * mm});
            skArc(sketch, "E91.trimOffspring", {"start": v(16.28, 76.6) * mm, "mid": v(15.33, 76.8) * mm, "end": v(14.38, 76.98) * mm});
            skArc(sketch, "E92.trimOffspring", {"start": v(9.54, 77.73) * mm, "mid": v(8.58, 77.85) * mm, "end": v(7.62, 77.95) * mm});
            skArc(sketch, "E93.trimOffspring", {"start": v(2.73, 78.27) * mm, "mid": v(1.76, 78.3) * mm, "end": v(0.8, 78.31) * mm});
            skLineSegment(sketch, "E94", {"start": v(-72.09, -30.6) * mm, "end": v(-71.31, -32.38) * mm});
            skSolve(sketch);
        }
        {
            var Q0;
            Q0=makeQuery(id+"F0.imprint","IMPRINT",FACE,{"disambiguationData":[TD([[makeQuery(id+"F0.imprint","IMPRINT",EDGE,{"derivedFrom":sQuery(id+"F0.wireOp",EDGE,"E0")}),1.0]])]});
            extrude(context, id + "F1", {"entities" : qUnion([Q0]), "depth" : 6.35 * mm});
        }
        {
            var Q0;
            Q0=makeQuery(id+"F0.imprint","IMPRINT",FACE,{"disambiguationData":[TD([[makeQuery(id+"F0.imprint","IMPRINT",EDGE,{"derivedFrom":sQuery(id+"F0.wireOp",EDGE,"E0")}),-1.0]])]});
            extrude(context, id + "F2", {"entities" : qUnion([Q0]), "operationType" : NewBodyOperationType.ADD, "depth" : 25.4 * mm});
        }
        {
            var Q0;
            Q0=makeQuery(id+"F1.opExtrude","CAP_FACE",FACE,{"disambiguationData":[OSD([sQuery(id+"F0.wireOp",EDGE,"E0"),sQuery(id+"F0.wireOp",EDGE,"E1.MirrorCS"),sQuery(id+"F0.wireOp",EDGE,"E2.MirrorCS"),sQuery(id+"F0.wireOp",EDGE,"E3.MirrorCS"),sQuery(id+"F0.wireOp",EDGE,"E4.MirrorCS"),sQuery(id+"F0.wireOp",EDGE,"E5.MirrorCS"),sQuery(id+"F0.wireOp",EDGE,"E6.MirrorCS"),sQuery(id+"F0.wireOp",EDGE,"E16.filletArc"),sQuery(id+"F0.wireOp",EDGE,"E17.filletArc"),sQuery(id+"F0.wireOp",EDGE,"E18.filletArc"),sQuery(id+"F0.wireOp",EDGE,"E19.filletArc"),sQuery(id+"F0.wireOp",EDGE,"E20.filletArc"),sQuery(id+"F0.wireOp",EDGE,"E21.filletArc"),sQuery(id+"F0.wireOp",EDGE,"E23.1.0"),sQuery(id+"F0.wireOp",EDGE,"E23.1.1"),sQuery(id+"F0.wireOp",EDGE,"E23.1.2"),sQuery(id+"F0.wireOp",EDGE,"E23.1.3"),sQuery(id+"F0.wireOp",EDGE,"E23.1.4"),sQuery(id+"F0.wireOp",EDGE,"E23.1.5"),sQuery(id+"F0.wireOp",EDGE,"E23.1.6"),sQuery(id+"F0.wireOp",EDGE,"E23.1.7"),sQuery(id+"F0.wireOp",EDGE,"E23.1.8"),sQuery(id+"F0.wireOp",EDGE,"E23.1.9"),sQuery(id+"F0.wireOp",EDGE,"E23.1.10"),sQuery(id+"F0.wireOp",EDGE,"E23.1.11"),sQuery(id+"F0.wireOp",EDGE,"E23.2.0"),sQuery(id+"F0.wireOp",EDGE,"E23.2.1"),sQuery(id+"F0.wireOp",EDGE,"E23.2.2"),sQuery(id+"F0.wireOp",EDGE,"E23.2.3"),sQuery(id+"F0.wireOp",EDGE,"E23.2.4"),sQuery(id+"F0.wireOp",EDGE,"E23.2.5"),sQuery(id+"F0.wireOp",EDGE,"E23.2.6"),sQuery(id+"F0.wireOp",EDGE,"E23.2.7"),sQuery(id+"F0.wireOp",EDGE,"E23.2.8"),sQuery(id+"F0.wireOp",EDGE,"E23.2.9"),sQuery(id+"F0.wireOp",EDGE,"E23.2.10"),sQuery(id+"F0.wireOp",EDGE,"E23.2.11"),sQuery(id+"F0.wireOp",EDGE,"E23.3.0"),sQuery(id+"F0.wireOp",EDGE,"E23.3.1"),sQuery(id+"F0.wireOp",EDGE,"E23.3.2"),sQuery(id+"F0.wireOp",EDGE,"E23.3.3"),sQuery(id+"F0.wireOp",EDGE,"E23.3.4"),sQuery(id+"F0.wireOp",EDGE,"E23.3.5"),sQuery(id+"F0.wireOp",EDGE,"E23.3.6"),sQuery(id+"F0.wireOp",EDGE,"E23.3.7"),sQuery(id+"F0.wireOp",EDGE,"E23.3.8"),sQuery(id+"F0.wireOp",EDGE,"E23.3.9"),sQuery(id+"F0.wireOp",EDGE,"E23.3.10"),sQuery(id+"F0.wireOp",EDGE,"E23.3.11"),sQuery(id+"F0.wireOp",EDGE,"E23.4.0"),sQuery(id+"F0.wireOp",EDGE,"E23.4.1"),sQuery(id+"F0.wireOp",EDGE,"E23.4.2"),sQuery(id+"F0.wireOp",EDGE,"E23.4.3"),sQuery(id+"F0.wireOp",EDGE,"E23.4.4"),sQuery(id+"F0.wireOp",EDGE,"E23.4.5"),sQuery(id+"F0.wireOp",EDGE,"E23.4.6"),sQuery(id+"F0.wireOp",EDGE,"E23.4.7"),sQuery(id+"F0.wireOp",EDGE,"E23.4.8"),sQuery(id+"F0.wireOp",EDGE,"E23.4.9"),sQuery(id+"F0.wireOp",EDGE,"E23.4.10"),sQuery(id+"F0.wireOp",EDGE,"E23.4.11"),sQuery(id+"F0.wireOp",EDGE,"E23.5.0"),sQuery(id+"F0.wireOp",EDGE,"E23.5.1"),sQuery(id+"F0.wireOp",EDGE,"E23.5.2"),sQuery(id+"F0.wireOp",EDGE,"E23.5.3"),sQuery(id+"F0.wireOp",EDGE,"E23.5.4"),sQuery(id+"F0.wireOp",EDGE,"E23.5.5"),sQuery(id+"F0.wireOp",EDGE,"E23.5.6"),sQuery(id+"F0.wireOp",EDGE,"E23.5.7"),sQuery(id+"F0.wireOp",EDGE,"E23.5.8"),sQuery(id+"F0.wireOp",EDGE,"E23.5.9"),sQuery(id+"F0.wireOp",EDGE,"E23.5.10"),sQuery(id+"F0.wireOp",EDGE,"E23.5.11"),sQuery(id+"F0.wireOp",EDGE,"E23.6.0"),sQuery(id+"F0.wireOp",EDGE,"E23.6.1"),sQuery(id+"F0.wireOp",EDGE,"E23.6.2"),sQuery(id+"F0.wireOp",EDGE,"E23.6.3"),sQuery(id+"F0.wireOp",EDGE,"E23.6.4"),sQuery(id+"F0.wireOp",EDGE,"E23.6.5"),sQuery(id+"F0.wireOp",EDGE,"E23.6.6"),sQuery(id+"F0.wireOp",EDGE,"E23.6.7"),sQuery(id+"F0.wireOp",EDGE,"E23.6.8"),sQuery(id+"F0.wireOp",EDGE,"E23.6.9"),sQuery(id+"F0.wireOp",EDGE,"E23.6.10"),sQuery(id+"F0.wireOp",EDGE,"E23.6.11"),sQuery(id+"F0.wireOp",EDGE,"E23.7.0"),sQuery(id+"F0.wireOp",EDGE,"E23.7.1"),sQuery(id+"F0.wireOp",EDGE,"E23.7.2"),sQuery(id+"F0.wireOp",EDGE,"E23.7.3"),sQuery(id+"F0.wireOp",EDGE,"E23.7.4"),sQuery(id+"F0.wireOp",EDGE,"E23.7.5"),sQuery(id+"F0.wireOp",EDGE,"E23.7.6"),sQuery(id+"F0.wireOp",EDGE,"E23.7.7"),sQuery(id+"F0.wireOp",EDGE,"E23.7.8"),sQuery(id+"F0.wireOp",EDGE,"E23.7.9"),sQuery(id+"F0.wireOp",EDGE,"E23.7.10"),sQuery(id+"F0.wireOp",EDGE,"E23.7.11"),sQuery(id+"F0.wireOp",EDGE,"E23.8.0"),sQuery(id+"F0.wireOp",EDGE,"E23.8.1"),sQuery(id+"F0.wireOp",EDGE,"E23.8.2"),sQuery(id+"F0.wireOp",EDGE,"E23.8.3"),sQuery(id+"F0.wireOp",EDGE,"E23.8.4"),sQuery(id+"F0.wireOp",EDGE,"E23.8.5"),sQuery(id+"F0.wireOp",EDGE,"E23.8.6"),sQuery(id+"F0.wireOp",EDGE,"E23.8.7"),sQuery(id+"F0.wireOp",EDGE,"E23.8.8"),sQuery(id+"F0.wireOp",EDGE,"E23.8.9"),sQuery(id+"F0.wireOp",EDGE,"E23.8.10"),sQuery(id+"F0.wireOp",EDGE,"E23.8.11"),sQuery(id+"F0.wireOp",EDGE,"E23.9.0"),sQuery(id+"F0.wireOp",EDGE,"E23.9.1"),sQuery(id+"F0.wireOp",EDGE,"E23.9.2"),sQuery(id+"F0.wireOp",EDGE,"E23.9.3"),sQuery(id+"F0.wireOp",EDGE,"E23.9.4"),sQuery(id+"F0.wireOp",EDGE,"E23.9.5"),sQuery(id+"F0.wireOp",EDGE,"E23.9.6"),sQuery(id+"F0.wireOp",EDGE,"E23.9.7"),sQuery(id+"F0.wireOp",EDGE,"E23.9.8"),sQuery(id+"F0.wireOp",EDGE,"E23.9.9"),sQuery(id+"F0.wireOp",EDGE,"E23.9.10"),sQuery(id+"F0.wireOp",EDGE,"E23.9.11"),sQuery(id+"F0.wireOp",EDGE,"E23.10.0"),sQuery(id+"F0.wireOp",EDGE,"E23.10.1"),sQuery(id+"F0.wireOp",EDGE,"E23.10.2"),sQuery(id+"F0.wireOp",EDGE,"E23.10.3"),sQuery(id+"F0.wireOp",EDGE,"E23.10.4"),sQuery(id+"F0.wireOp",EDGE,"E23.10.5"),sQuery(id+"F0.wireOp",EDGE,"E23.10.6"),sQuery(id+"F0.wireOp",EDGE,"E23.10.7"),sQuery(id+"F0.wireOp",EDGE,"E23.10.8"),sQuery(id+"F0.wireOp",EDGE,"E23.10.9"),sQuery(id+"F0.wireOp",EDGE,"E23.10.10"),sQuery(id+"F0.wireOp",EDGE,"E23.10.11"),sQuery(id+"F0.wireOp",EDGE,"E23.11.0"),sQuery(id+"F0.wireOp",EDGE,"E23.11.1"),sQuery(id+"F0.wireOp",EDGE,"E23.11.2"),sQuery(id+"F0.wireOp",EDGE,"E23.11.3"),sQuery(id+"F0.wireOp",EDGE,"E23.11.4"),sQuery(id+"F0.wireOp",EDGE,"E23.11.5"),sQuery(id+"F0.wireOp",EDGE,"E23.11.6"),sQuery(id+"F0.wireOp",EDGE,"E23.11.7"),sQuery(id+"F0.wireOp",EDGE,"E23.11.8"),sQuery(id+"F0.wireOp",EDGE,"E23.11.9"),sQuery(id+"F0.wireOp",EDGE,"E23.11.10"),sQuery(id+"F0.wireOp",EDGE,"E23.11.11"),sQuery(id+"F0.wireOp",EDGE,"E23.12.0"),sQuery(id+"F0.wireOp",EDGE,"E23.12.1"),sQuery(id+"F0.wireOp",EDGE,"E23.12.2"),sQuery(id+"F0.wireOp",EDGE,"E23.12.3"),sQuery(id+"F0.wireOp",EDGE,"E23.12.4"),sQuery(id+"F0.wireOp",EDGE,"E23.12.5"),sQuery(id+"F0.wireOp",EDGE,"E23.12.6"),sQuery(id+"F0.wireOp",EDGE,"E23.12.7"),sQuery(id+"F0.wireOp",EDGE,"E23.12.8"),sQuery(id+"F0.wireOp",EDGE,"E23.12.9"),sQuery(id+"F0.wireOp",EDGE,"E23.12.10"),sQuery(id+"F0.wireOp",EDGE,"E23.12.11"),sQuery(id+"F0.wireOp",EDGE,"E23.13.0"),sQuery(id+"F0.wireOp",EDGE,"E23.13.1"),sQuery(id+"F0.wireOp",EDGE,"E23.13.2"),sQuery(id+"F0.wireOp",EDGE,"E23.13.3"),sQuery(id+"F0.wireOp",EDGE,"E23.13.4"),sQuery(id+"F0.wireOp",EDGE,"E23.13.5"),sQuery(id+"F0.wireOp",EDGE,"E23.13.6"),sQuery(id+"F0.wireOp",EDGE,"E23.13.7"),sQuery(id+"F0.wireOp",EDGE,"E23.13.8"),sQuery(id+"F0.wireOp",EDGE,"E23.13.9"),sQuery(id+"F0.wireOp",EDGE,"E23.13.10"),sQuery(id+"F0.wireOp",EDGE,"E23.13.11"),sQuery(id+"F0.wireOp",EDGE,"E23.14.0"),sQuery(id+"F0.wireOp",EDGE,"E23.14.1"),sQuery(id+"F0.wireOp",EDGE,"E23.14.2"),sQuery(id+"F0.wireOp",EDGE,"E23.14.3"),sQuery(id+"F0.wireOp",EDGE,"E23.14.4"),sQuery(id+"F0.wireOp",EDGE,"E23.14.5"),sQuery(id+"F0.wireOp",EDGE,"E23.14.6"),sQuery(id+"F0.wireOp",EDGE,"E23.14.7"),sQuery(id+"F0.wireOp",EDGE,"E23.14.8"),sQuery(id+"F0.wireOp",EDGE,"E23.14.9"),sQuery(id+"F0.wireOp",EDGE,"E23.14.10"),sQuery(id+"F0.wireOp",EDGE,"E23.14.11"),sQuery(id+"F0.wireOp",EDGE,"E23.15.0"),sQuery(id+"F0.wireOp",EDGE,"E23.15.1"),sQuery(id+"F0.wireOp",EDGE,"E23.15.2"),sQuery(id+"F0.wireOp",EDGE,"E23.15.3"),sQuery(id+"F0.wireOp",EDGE,"E23.15.4"),sQuery(id+"F0.wireOp",EDGE,"E23.15.5"),sQuery(id+"F0.wireOp",EDGE,"E23.15.6"),sQuery(id+"F0.wireOp",EDGE,"E23.15.7"),sQuery(id+"F0.wireOp",EDGE,"E23.15.8"),sQuery(id+"F0.wireOp",EDGE,"E23.15.9"),sQuery(id+"F0.wireOp",EDGE,"E23.15.10"),sQuery(id+"F0.wireOp",EDGE,"E23.15.11"),sQuery(id+"F0.wireOp",EDGE,"E23.16.0"),sQuery(id+"F0.wireOp",EDGE,"E23.16.1"),sQuery(id+"F0.wireOp",EDGE,"E23.16.2"),sQuery(id+"F0.wireOp",EDGE,"E23.16.3"),sQuery(id+"F0.wireOp",EDGE,"E23.16.4"),sQuery(id+"F0.wireOp",EDGE,"E23.16.5"),sQuery(id+"F0.wireOp",EDGE,"E23.16.6"),sQuery(id+"F0.wireOp",EDGE,"E23.16.7"),sQuery(id+"F0.wireOp",EDGE,"E23.16.8"),sQuery(id+"F0.wireOp",EDGE,"E23.16.9"),sQuery(id+"F0.wireOp",EDGE,"E23.16.10"),sQuery(id+"F0.wireOp",EDGE,"E23.16.11"),sQuery(id+"F0.wireOp",EDGE,"E23.17.0"),sQuery(id+"F0.wireOp",EDGE,"E23.17.1"),sQuery(id+"F0.wireOp",EDGE,"E23.17.2"),sQuery(id+"F0.wireOp",EDGE,"E23.17.3"),sQuery(id+"F0.wireOp",EDGE,"E23.17.4"),sQuery(id+"F0.wireOp",EDGE,"E23.17.5"),sQuery(id+"F0.wireOp",EDGE,"E23.17.6"),sQuery(id+"F0.wireOp",EDGE,"E23.17.7"),sQuery(id+"F0.wireOp",EDGE,"E23.17.8"),sQuery(id+"F0.wireOp",EDGE,"E23.17.9"),sQuery(id+"F0.wireOp",EDGE,"E23.17.10"),sQuery(id+"F0.wireOp",EDGE,"E23.17.11"),sQuery(id+"F0.wireOp",EDGE,"E23.18.0"),sQuery(id+"F0.wireOp",EDGE,"E23.18.1"),sQuery(id+"F0.wireOp",EDGE,"E23.18.2"),sQuery(id+"F0.wireOp",EDGE,"E23.18.3"),sQuery(id+"F0.wireOp",EDGE,"E23.18.4"),sQuery(id+"F0.wireOp",EDGE,"E23.18.5"),sQuery(id+"F0.wireOp",EDGE,"E23.18.6"),sQuery(id+"F0.wireOp",EDGE,"E23.18.7"),sQuery(id+"F0.wireOp",EDGE,"E23.18.8"),sQuery(id+"F0.wireOp",EDGE,"E23.18.9"),sQuery(id+"F0.wireOp",EDGE,"E23.18.10"),sQuery(id+"F0.wireOp",EDGE,"E23.18.11"),sQuery(id+"F0.wireOp",EDGE,"E23.19.0"),sQuery(id+"F0.wireOp",EDGE,"E23.19.1"),sQuery(id+"F0.wireOp",EDGE,"E23.19.2"),sQuery(id+"F0.wireOp",EDGE,"E23.19.3"),sQuery(id+"F0.wireOp",EDGE,"E23.19.4"),sQuery(id+"F0.wireOp",EDGE,"E23.19.5"),sQuery(id+"F0.wireOp",EDGE,"E23.19.6"),sQuery(id+"F0.wireOp",EDGE,"E23.19.7"),sQuery(id+"F0.wireOp",EDGE,"E23.19.8"),sQuery(id+"F0.wireOp",EDGE,"E23.19.9"),sQuery(id+"F0.wireOp",EDGE,"E23.19.10"),sQuery(id+"F0.wireOp",EDGE,"E23.19.11"),sQuery(id+"F0.wireOp",EDGE,"E23.20.0"),sQuery(id+"F0.wireOp",EDGE,"E23.20.1"),sQuery(id+"F0.wireOp",EDGE,"E23.20.2"),sQuery(id+"F0.wireOp",EDGE,"E23.20.3"),sQuery(id+"F0.wireOp",EDGE,"E23.20.4"),sQuery(id+"F0.wireOp",EDGE,"E23.20.5"),sQuery(id+"F0.wireOp",EDGE,"E23.20.6"),sQuery(id+"F0.wireOp",EDGE,"E23.20.7"),sQuery(id+"F0.wireOp",EDGE,"E23.20.8"),sQuery(id+"F0.wireOp",EDGE,"E23.20.9"),sQuery(id+"F0.wireOp",EDGE,"E23.20.10"),sQuery(id+"F0.wireOp",EDGE,"E23.20.11"),sQuery(id+"F0.wireOp",EDGE,"E23.21.0"),sQuery(id+"F0.wireOp",EDGE,"E23.21.1"),sQuery(id+"F0.wireOp",EDGE,"E23.21.2"),sQuery(id+"F0.wireOp",EDGE,"E23.21.3"),sQuery(id+"F0.wireOp",EDGE,"E23.21.4"),sQuery(id+"F0.wireOp",EDGE,"E23.21.5"),sQuery(id+"F0.wireOp",EDGE,"E23.21.6"),sQuery(id+"F0.wireOp",EDGE,"E23.21.7"),sQuery(id+"F0.wireOp",EDGE,"E23.21.8"),sQuery(id+"F0.wireOp",EDGE,"E23.21.9"),sQuery(id+"F0.wireOp",EDGE,"E23.21.10"),sQuery(id+"F0.wireOp",EDGE,"E23.21.11"),sQuery(id+"F0.wireOp",EDGE,"E23.22.0"),sQuery(id+"F0.wireOp",EDGE,"E23.22.1"),sQuery(id+"F0.wireOp",EDGE,"E23.22.2"),sQuery(id+"F0.wireOp",EDGE,"E23.22.3"),sQuery(id+"F0.wireOp",EDGE,"E23.22.4"),sQuery(id+"F0.wireOp",EDGE,"E23.22.5"),sQuery(id+"F0.wireOp",EDGE,"E23.22.6"),sQuery(id+"F0.wireOp",EDGE,"E23.22.7"),sQuery(id+"F0.wireOp",EDGE,"E23.22.8"),sQuery(id+"F0.wireOp",EDGE,"E23.22.9"),sQuery(id+"F0.wireOp",EDGE,"E23.22.10"),sQuery(id+"F0.wireOp",EDGE,"E23.22.11"),sQuery(id+"F0.wireOp",EDGE,"E23.23.0"),sQuery(id+"F0.wireOp",EDGE,"E23.23.1"),sQuery(id+"F0.wireOp",EDGE,"E23.23.2"),sQuery(id+"F0.wireOp",EDGE,"E23.23.3"),sQuery(id+"F0.wireOp",EDGE,"E23.23.4"),sQuery(id+"F0.wireOp",EDGE,"E23.23.5"),sQuery(id+"F0.wireOp",EDGE,"E23.23.6"),sQuery(id+"F0.wireOp",EDGE,"E23.23.7"),sQuery(id+"F0.wireOp",EDGE,"E23.23.8"),sQuery(id+"F0.wireOp",EDGE,"E23.23.9"),sQuery(id+"F0.wireOp",EDGE,"E23.23.10"),sQuery(id+"F0.wireOp",EDGE,"E23.23.11"),sQuery(id+"F0.wireOp",EDGE,"E23.24.0"),sQuery(id+"F0.wireOp",EDGE,"E23.24.1"),sQuery(id+"F0.wireOp",EDGE,"E23.24.2"),sQuery(id+"F0.wireOp",EDGE,"E23.24.3"),sQuery(id+"F0.wireOp",EDGE,"E23.24.4"),sQuery(id+"F0.wireOp",EDGE,"E23.24.5"),sQuery(id+"F0.wireOp",EDGE,"E23.24.6"),sQuery(id+"F0.wireOp",EDGE,"E23.24.7"),sQuery(id+"F0.wireOp",EDGE,"E23.24.8"),sQuery(id+"F0.wireOp",EDGE,"E23.24.9"),sQuery(id+"F0.wireOp",EDGE,"E23.24.10"),sQuery(id+"F0.wireOp",EDGE,"E23.24.11"),sQuery(id+"F0.wireOp",EDGE,"E23.25.0"),sQuery(id+"F0.wireOp",EDGE,"E23.25.1"),sQuery(id+"F0.wireOp",EDGE,"E23.25.2"),sQuery(id+"F0.wireOp",EDGE,"E23.25.3"),sQuery(id+"F0.wireOp",EDGE,"E23.25.4"),sQuery(id+"F0.wireOp",EDGE,"E23.25.5"),sQuery(id+"F0.wireOp",EDGE,"E23.25.6"),sQuery(id+"F0.wireOp",EDGE,"E23.25.7"),sQuery(id+"F0.wireOp",EDGE,"E23.25.8"),sQuery(id+"F0.wireOp",EDGE,"E23.25.9"),sQuery(id+"F0.wireOp",EDGE,"E23.25.10"),sQuery(id+"F0.wireOp",EDGE,"E23.25.11"),sQuery(id+"F0.wireOp",EDGE,"E23.26.0"),sQuery(id+"F0.wireOp",EDGE,"E23.26.1"),sQuery(id+"F0.wireOp",EDGE,"E23.26.2"),sQuery(id+"F0.wireOp",EDGE,"E23.26.3"),sQuery(id+"F0.wireOp",EDGE,"E23.26.4"),sQuery(id+"F0.wireOp",EDGE,"E23.26.5"),sQuery(id+"F0.wireOp",EDGE,"E23.26.6"),sQuery(id+"F0.wireOp",EDGE,"E23.26.7"),sQuery(id+"F0.wireOp",EDGE,"E23.26.8"),sQuery(id+"F0.wireOp",EDGE,"E23.26.9"),sQuery(id+"F0.wireOp",EDGE,"E23.26.10"),sQuery(id+"F0.wireOp",EDGE,"E23.26.11"),sQuery(id+"F0.wireOp",EDGE,"E23.27.0"),sQuery(id+"F0.wireOp",EDGE,"E23.27.1"),sQuery(id+"F0.wireOp",EDGE,"E23.27.2"),sQuery(id+"F0.wireOp",EDGE,"E23.27.3"),sQuery(id+"F0.wireOp",EDGE,"E23.27.4"),sQuery(id+"F0.wireOp",EDGE,"E23.27.5"),sQuery(id+"F0.wireOp",EDGE,"E23.27.6"),sQuery(id+"F0.wireOp",EDGE,"E23.27.7"),sQuery(id+"F0.wireOp",EDGE,"E23.27.8"),sQuery(id+"F0.wireOp",EDGE,"E23.27.9"),sQuery(id+"F0.wireOp",EDGE,"E23.27.10"),sQuery(id+"F0.wireOp",EDGE,"E23.27.11"),sQuery(id+"F0.wireOp",EDGE,"E23.28.0"),sQuery(id+"F0.wireOp",EDGE,"E23.28.1"),sQuery(id+"F0.wireOp",EDGE,"E23.28.2"),sQuery(id+"F0.wireOp",EDGE,"E23.28.3"),sQuery(id+"F0.wireOp",EDGE,"E23.28.4"),sQuery(id+"F0.wireOp",EDGE,"E23.28.5"),sQuery(id+"F0.wireOp",EDGE,"E23.28.6"),sQuery(id+"F0.wireOp",EDGE,"E23.28.7"),sQuery(id+"F0.wireOp",EDGE,"E23.28.8"),sQuery(id+"F0.wireOp",EDGE,"E23.28.9"),sQuery(id+"F0.wireOp",EDGE,"E23.28.10"),sQuery(id+"F0.wireOp",EDGE,"E23.28.11"),sQuery(id+"F0.wireOp",EDGE,"E23.29.0"),sQuery(id+"F0.wireOp",EDGE,"E23.29.1"),sQuery(id+"F0.wireOp",EDGE,"E23.29.2"),sQuery(id+"F0.wireOp",EDGE,"E23.29.3"),sQuery(id+"F0.wireOp",EDGE,"E23.29.4"),sQuery(id+"F0.wireOp",EDGE,"E23.29.5"),sQuery(id+"F0.wireOp",EDGE,"E23.29.6"),sQuery(id+"F0.wireOp",EDGE,"E23.29.7"),sQuery(id+"F0.wireOp",EDGE,"E23.29.8"),sQuery(id+"F0.wireOp",EDGE,"E23.29.9"),sQuery(id+"F0.wireOp",EDGE,"E23.29.10"),sQuery(id+"F0.wireOp",EDGE,"E23.29.11"),sQuery(id+"F0.wireOp",EDGE,"E23.30.0"),sQuery(id+"F0.wireOp",EDGE,"E23.30.1"),sQuery(id+"F0.wireOp",EDGE,"E23.30.2"),sQuery(id+"F0.wireOp",EDGE,"E23.30.3"),sQuery(id+"F0.wireOp",EDGE,"E23.30.4"),sQuery(id+"F0.wireOp",EDGE,"E23.30.5"),sQuery(id+"F0.wireOp",EDGE,"E23.30.6"),sQuery(id+"F0.wireOp",EDGE,"E23.30.7"),sQuery(id+"F0.wireOp",EDGE,"E23.30.8"),sQuery(id+"F0.wireOp",EDGE,"E23.30.9"),sQuery(id+"F0.wireOp",EDGE,"E23.30.10"),sQuery(id+"F0.wireOp",EDGE,"E23.30.11"),sQuery(id+"F0.wireOp",EDGE,"E23.31.0"),sQuery(id+"F0.wireOp",EDGE,"E23.31.1"),sQuery(id+"F0.wireOp",EDGE,"E23.31.2"),sQuery(id+"F0.wireOp",EDGE,"E23.31.3"),sQuery(id+"F0.wireOp",EDGE,"E23.31.4"),sQuery(id+"F0.wireOp",EDGE,"E23.31.5"),sQuery(id+"F0.wireOp",EDGE,"E23.31.6"),sQuery(id+"F0.wireOp",EDGE,"E23.31.7"),sQuery(id+"F0.wireOp",EDGE,"E23.31.8"),sQuery(id+"F0.wireOp",EDGE,"E23.31.9"),sQuery(id+"F0.wireOp",EDGE,"E23.31.10"),sQuery(id+"F0.wireOp",EDGE,"E23.31.11"),sQuery(id+"F0.wireOp",EDGE,"E23.32.0"),sQuery(id+"F0.wireOp",EDGE,"E23.32.1"),sQuery(id+"F0.wireOp",EDGE,"E23.32.2"),sQuery(id+"F0.wireOp",EDGE,"E23.32.3"),sQuery(id+"F0.wireOp",EDGE,"E23.32.4"),sQuery(id+"F0.wireOp",EDGE,"E23.32.5"),sQuery(id+"F0.wireOp",EDGE,"E23.32.6"),sQuery(id+"F0.wireOp",EDGE,"E23.32.7"),sQuery(id+"F0.wireOp",EDGE,"E23.32.8"),sQuery(id+"F0.wireOp",EDGE,"E23.32.9"),sQuery(id+"F0.wireOp",EDGE,"E23.32.10"),sQuery(id+"F0.wireOp",EDGE,"E23.32.11"),sQuery(id+"F0.wireOp",EDGE,"E23.33.0"),sQuery(id+"F0.wireOp",EDGE,"E23.33.1"),sQuery(id+"F0.wireOp",EDGE,"E23.33.2"),sQuery(id+"F0.wireOp",EDGE,"E23.33.3"),sQuery(id+"F0.wireOp",EDGE,"E23.33.4"),sQuery(id+"F0.wireOp",EDGE,"E23.33.5"),sQuery(id+"F0.wireOp",EDGE,"E23.33.6"),sQuery(id+"F0.wireOp",EDGE,"E23.33.7"),sQuery(id+"F0.wireOp",EDGE,"E23.33.8"),sQuery(id+"F0.wireOp",EDGE,"E23.33.9"),sQuery(id+"F0.wireOp",EDGE,"E23.33.10"),sQuery(id+"F0.wireOp",EDGE,"E23.33.11"),sQuery(id+"F0.wireOp",EDGE,"E23.34.0"),sQuery(id+"F0.wireOp",EDGE,"E23.34.1"),sQuery(id+"F0.wireOp",EDGE,"E23.34.2"),sQuery(id+"F0.wireOp",EDGE,"E23.34.3"),sQuery(id+"F0.wireOp",EDGE,"E23.34.4"),sQuery(id+"F0.wireOp",EDGE,"E23.34.5"),sQuery(id+"F0.wireOp",EDGE,"E23.34.6"),sQuery(id+"F0.wireOp",EDGE,"E23.34.7"),sQuery(id+"F0.wireOp",EDGE,"E23.34.8"),sQuery(id+"F0.wireOp",EDGE,"E23.34.9"),sQuery(id+"F0.wireOp",EDGE,"E23.34.10"),sQuery(id+"F0.wireOp",EDGE,"E23.34.11"),sQuery(id+"F0.wireOp",EDGE,"E23.35.0"),sQuery(id+"F0.wireOp",EDGE,"E23.35.1"),sQuery(id+"F0.wireOp",EDGE,"E23.35.2"),sQuery(id+"F0.wireOp",EDGE,"E23.35.3"),sQuery(id+"F0.wireOp",EDGE,"E23.35.4"),sQuery(id+"F0.wireOp",EDGE,"E23.35.5"),sQuery(id+"F0.wireOp",EDGE,"E23.35.6"),sQuery(id+"F0.wireOp",EDGE,"E23.35.7"),sQuery(id+"F0.wireOp",EDGE,"E23.35.8"),sQuery(id+"F0.wireOp",EDGE,"E23.35.9"),sQuery(id+"F0.wireOp",EDGE,"E23.35.10"),sQuery(id+"F0.wireOp",EDGE,"E23.35.11"),sQuery(id+"F0.wireOp",EDGE,"E23.36.0"),sQuery(id+"F0.wireOp",EDGE,"E23.36.1"),sQuery(id+"F0.wireOp",EDGE,"E23.36.2"),sQuery(id+"F0.wireOp",EDGE,"E23.36.3"),sQuery(id+"F0.wireOp",EDGE,"E23.36.4"),sQuery(id+"F0.wireOp",EDGE,"E23.36.5"),sQuery(id+"F0.wireOp",EDGE,"E23.36.6"),sQuery(id+"F0.wireOp",EDGE,"E23.36.7"),sQuery(id+"F0.wireOp",EDGE,"E23.36.8"),sQuery(id+"F0.wireOp",EDGE,"E23.36.9"),sQuery(id+"F0.wireOp",EDGE,"E23.36.10"),sQuery(id+"F0.wireOp",EDGE,"E23.36.11"),sQuery(id+"F0.wireOp",EDGE,"E23.37.0"),sQuery(id+"F0.wireOp",EDGE,"E23.37.1"),sQuery(id+"F0.wireOp",EDGE,"E23.37.2"),sQuery(id+"F0.wireOp",EDGE,"E23.37.3"),sQuery(id+"F0.wireOp",EDGE,"E23.37.4"),sQuery(id+"F0.wireOp",EDGE,"E23.37.5"),sQuery(id+"F0.wireOp",EDGE,"E23.37.6"),sQuery(id+"F0.wireOp",EDGE,"E23.37.7"),sQuery(id+"F0.wireOp",EDGE,"E23.37.8"),sQuery(id+"F0.wireOp",EDGE,"E23.37.9"),sQuery(id+"F0.wireOp",EDGE,"E23.37.10"),sQuery(id+"F0.wireOp",EDGE,"E23.37.11"),sQuery(id+"F0.wireOp",EDGE,"E23.38.0"),sQuery(id+"F0.wireOp",EDGE,"E23.38.1"),sQuery(id+"F0.wireOp",EDGE,"E23.38.2"),sQuery(id+"F0.wireOp",EDGE,"E23.38.3"),sQuery(id+"F0.wireOp",EDGE,"E23.38.4"),sQuery(id+"F0.wireOp",EDGE,"E23.38.5"),sQuery(id+"F0.wireOp",EDGE,"E23.38.6"),sQuery(id+"F0.wireOp",EDGE,"E23.38.7"),sQuery(id+"F0.wireOp",EDGE,"E23.38.8"),sQuery(id+"F0.wireOp",EDGE,"E23.38.9"),sQuery(id+"F0.wireOp",EDGE,"E23.38.10"),sQuery(id+"F0.wireOp",EDGE,"E23.38.11"),sQuery(id+"F0.wireOp",EDGE,"E23.39.0"),sQuery(id+"F0.wireOp",EDGE,"E23.39.1"),sQuery(id+"F0.wireOp",EDGE,"E23.39.2"),sQuery(id+"F0.wireOp",EDGE,"E23.39.3"),sQuery(id+"F0.wireOp",EDGE,"E23.39.4"),sQuery(id+"F0.wireOp",EDGE,"E23.39.5"),sQuery(id+"F0.wireOp",EDGE,"E23.39.6"),sQuery(id+"F0.wireOp",EDGE,"E23.39.7"),sQuery(id+"F0.wireOp",EDGE,"E23.39.8"),sQuery(id+"F0.wireOp",EDGE,"E23.39.9"),sQuery(id+"F0.wireOp",EDGE,"E23.39.10"),sQuery(id+"F0.wireOp",EDGE,"E23.39.11"),sQuery(id+"F0.wireOp",EDGE,"E23.40.0"),sQuery(id+"F0.wireOp",EDGE,"E23.40.1"),sQuery(id+"F0.wireOp",EDGE,"E23.40.2"),sQuery(id+"F0.wireOp",EDGE,"E23.40.3"),sQuery(id+"F0.wireOp",EDGE,"E23.40.4"),sQuery(id+"F0.wireOp",EDGE,"E23.40.5"),sQuery(id+"F0.wireOp",EDGE,"E23.40.6"),sQuery(id+"F0.wireOp",EDGE,"E23.40.7"),sQuery(id+"F0.wireOp",EDGE,"E23.40.8"),sQuery(id+"F0.wireOp",EDGE,"E23.40.9"),sQuery(id+"F0.wireOp",EDGE,"E23.40.10"),sQuery(id+"F0.wireOp",EDGE,"E23.40.11"),sQuery(id+"F0.wireOp",EDGE,"E23.41.0"),sQuery(id+"F0.wireOp",EDGE,"E23.41.1"),sQuery(id+"F0.wireOp",EDGE,"E23.41.2"),sQuery(id+"F0.wireOp",EDGE,"E23.41.3"),sQuery(id+"F0.wireOp",EDGE,"E23.41.4"),sQuery(id+"F0.wireOp",EDGE,"E23.41.5"),sQuery(id+"F0.wireOp",EDGE,"E23.41.6"),sQuery(id+"F0.wireOp",EDGE,"E23.41.7"),sQuery(id+"F0.wireOp",EDGE,"E23.41.8"),sQuery(id+"F0.wireOp",EDGE,"E23.41.9"),sQuery(id+"F0.wireOp",EDGE,"E23.41.10"),sQuery(id+"F0.wireOp",EDGE,"E23.41.11"),sQuery(id+"F0.wireOp",EDGE,"E23.42.0"),sQuery(id+"F0.wireOp",EDGE,"E23.42.1"),sQuery(id+"F0.wireOp",EDGE,"E23.42.2"),sQuery(id+"F0.wireOp",EDGE,"E23.42.3"),sQuery(id+"F0.wireOp",EDGE,"E23.42.4"),sQuery(id+"F0.wireOp",EDGE,"E23.42.5"),sQuery(id+"F0.wireOp",EDGE,"E23.42.6"),sQuery(id+"F0.wireOp",EDGE,"E23.42.7"),sQuery(id+"F0.wireOp",EDGE,"E23.42.8"),sQuery(id+"F0.wireOp",EDGE,"E23.42.9"),sQuery(id+"F0.wireOp",EDGE,"E23.42.10"),sQuery(id+"F0.wireOp",EDGE,"E23.42.11"),sQuery(id+"F0.wireOp",EDGE,"E23.43.0"),sQuery(id+"F0.wireOp",EDGE,"E23.43.1"),sQuery(id+"F0.wireOp",EDGE,"E23.43.2"),sQuery(id+"F0.wireOp",EDGE,"E23.43.3"),sQuery(id+"F0.wireOp",EDGE,"E23.43.4"),sQuery(id+"F0.wireOp",EDGE,"E23.43.5"),sQuery(id+"F0.wireOp",EDGE,"E23.43.6"),sQuery(id+"F0.wireOp",EDGE,"E23.43.7"),sQuery(id+"F0.wireOp",EDGE,"E23.43.8"),sQuery(id+"F0.wireOp",EDGE,"E23.43.9"),sQuery(id+"F0.wireOp",EDGE,"E23.43.10"),sQuery(id+"F0.wireOp",EDGE,"E23.43.11"),sQuery(id+"F0.wireOp",EDGE,"E23.44.0"),sQuery(id+"F0.wireOp",EDGE,"E23.44.1"),sQuery(id+"F0.wireOp",EDGE,"E23.44.2"),sQuery(id+"F0.wireOp",EDGE,"E23.44.3"),sQuery(id+"F0.wireOp",EDGE,"E23.44.4"),sQuery(id+"F0.wireOp",EDGE,"E23.44.5"),sQuery(id+"F0.wireOp",EDGE,"E23.44.6"),sQuery(id+"F0.wireOp",EDGE,"E23.44.7"),sQuery(id+"F0.wireOp",EDGE,"E23.44.8"),sQuery(id+"F0.wireOp",EDGE,"E23.44.9"),sQuery(id+"F0.wireOp",EDGE,"E23.44.10"),sQuery(id+"F0.wireOp",EDGE,"E23.44.11"),sQuery(id+"F0.wireOp",EDGE,"E23.45.0"),sQuery(id+"F0.wireOp",EDGE,"E23.45.1"),sQuery(id+"F0.wireOp",EDGE,"E23.45.2"),sQuery(id+"F0.wireOp",EDGE,"E23.45.3"),sQuery(id+"F0.wireOp",EDGE,"E23.45.4"),sQuery(id+"F0.wireOp",EDGE,"E23.45.5"),sQuery(id+"F0.wireOp",EDGE,"E23.45.6"),sQuery(id+"F0.wireOp",EDGE,"E23.45.7"),sQuery(id+"F0.wireOp",EDGE,"E23.45.8"),sQuery(id+"F0.wireOp",EDGE,"E23.45.9"),sQuery(id+"F0.wireOp",EDGE,"E23.45.10"),sQuery(id+"F0.wireOp",EDGE,"E23.45.11"),sQuery(id+"F0.wireOp",EDGE,"E23.46.0"),sQuery(id+"F0.wireOp",EDGE,"E23.46.1"),sQuery(id+"F0.wireOp",EDGE,"E23.46.2"),sQuery(id+"F0.wireOp",EDGE,"E23.46.3"),sQuery(id+"F0.wireOp",EDGE,"E23.46.4"),sQuery(id+"F0.wireOp",EDGE,"E23.46.5"),sQuery(id+"F0.wireOp",EDGE,"E23.46.6"),sQuery(id+"F0.wireOp",EDGE,"E23.46.7"),sQuery(id+"F0.wireOp",EDGE,"E23.46.8"),sQuery(id+"F0.wireOp",EDGE,"E23.46.9"),sQuery(id+"F0.wireOp",EDGE,"E23.46.10"),sQuery(id+"F0.wireOp",EDGE,"E23.46.11"),sQuery(id+"F0.wireOp",EDGE,"E23.47.0"),sQuery(id+"F0.wireOp",EDGE,"E23.47.1"),sQuery(id+"F0.wireOp",EDGE,"E23.47.2"),sQuery(id+"F0.wireOp",EDGE,"E23.47.3"),sQuery(id+"F0.wireOp",EDGE,"E23.47.4"),sQuery(id+"F0.wireOp",EDGE,"E23.47.5"),sQuery(id+"F0.wireOp",EDGE,"E23.47.6"),sQuery(id+"F0.wireOp",EDGE,"E23.47.7"),sQuery(id+"F0.wireOp",EDGE,"E23.47.8"),sQuery(id+"F0.wireOp",EDGE,"E23.47.9"),sQuery(id+"F0.wireOp",EDGE,"E23.47.10"),sQuery(id+"F0.wireOp",EDGE,"E23.47.11"),sQuery(id+"F0.wireOp",EDGE,"E23.48.0"),sQuery(id+"F0.wireOp",EDGE,"E23.48.1"),sQuery(id+"F0.wireOp",EDGE,"E23.48.2"),sQuery(id+"F0.wireOp",EDGE,"E23.48.3"),sQuery(id+"F0.wireOp",EDGE,"E23.48.4"),sQuery(id+"F0.wireOp",EDGE,"E23.48.5"),sQuery(id+"F0.wireOp",EDGE,"E23.48.6"),sQuery(id+"F0.wireOp",EDGE,"E23.48.7"),sQuery(id+"F0.wireOp",EDGE,"E23.48.8"),sQuery(id+"F0.wireOp",EDGE,"E23.48.9"),sQuery(id+"F0.wireOp",EDGE,"E23.48.10"),sQuery(id+"F0.wireOp",EDGE,"E23.48.11"),sQuery(id+"F0.wireOp",EDGE,"E23.49.0"),sQuery(id+"F0.wireOp",EDGE,"E23.49.1"),sQuery(id+"F0.wireOp",EDGE,"E23.49.2"),sQuery(id+"F0.wireOp",EDGE,"E23.49.3"),sQuery(id+"F0.wireOp",EDGE,"E23.49.4"),sQuery(id+"F0.wireOp",EDGE,"E23.49.5"),sQuery(id+"F0.wireOp",EDGE,"E23.49.6"),sQuery(id+"F0.wireOp",EDGE,"E23.49.7"),sQuery(id+"F0.wireOp",EDGE,"E23.49.8"),sQuery(id+"F0.wireOp",EDGE,"E23.49.9"),sQuery(id+"F0.wireOp",EDGE,"E23.49.10"),sQuery(id+"F0.wireOp",EDGE,"E23.49.11"),sQuery(id+"F0.wireOp",EDGE,"E23.50.0"),sQuery(id+"F0.wireOp",EDGE,"E23.50.1"),sQuery(id+"F0.wireOp",EDGE,"E23.50.2"),sQuery(id+"F0.wireOp",EDGE,"E23.50.3"),sQuery(id+"F0.wireOp",EDGE,"E23.50.4"),sQuery(id+"F0.wireOp",EDGE,"E23.50.5"),sQuery(id+"F0.wireOp",EDGE,"E23.50.6"),sQuery(id+"F0.wireOp",EDGE,"E23.50.7"),sQuery(id+"F0.wireOp",EDGE,"E23.50.8"),sQuery(id+"F0.wireOp",EDGE,"E23.50.9"),sQuery(id+"F0.wireOp",EDGE,"E23.50.10"),sQuery(id+"F0.wireOp",EDGE,"E23.50.11"),sQuery(id+"F0.wireOp",EDGE,"E23.51.0"),sQuery(id+"F0.wireOp",EDGE,"E23.51.1"),sQuery(id+"F0.wireOp",EDGE,"E23.51.2"),sQuery(id+"F0.wireOp",EDGE,"E23.51.3"),sQuery(id+"F0.wireOp",EDGE,"E23.51.4"),sQuery(id+"F0.wireOp",EDGE,"E23.51.5"),sQuery(id+"F0.wireOp",EDGE,"E23.51.6"),sQuery(id+"F0.wireOp",EDGE,"E23.51.7"),sQuery(id+"F0.wireOp",EDGE,"E23.51.8"),sQuery(id+"F0.wireOp",EDGE,"E23.51.9"),sQuery(id+"F0.wireOp",EDGE,"E23.51.10"),sQuery(id+"F0.wireOp",EDGE,"E23.51.11"),sQuery(id+"F0.wireOp",EDGE,"E23.52.0"),sQuery(id+"F0.wireOp",EDGE,"E23.52.1"),sQuery(id+"F0.wireOp",EDGE,"E23.52.2"),sQuery(id+"F0.wireOp",EDGE,"E23.52.3"),sQuery(id+"F0.wireOp",EDGE,"E23.52.4"),sQuery(id+"F0.wireOp",EDGE,"E23.52.5"),sQuery(id+"F0.wireOp",EDGE,"E23.52.6"),sQuery(id+"F0.wireOp",EDGE,"E23.52.7"),sQuery(id+"F0.wireOp",EDGE,"E23.52.8"),sQuery(id+"F0.wireOp",EDGE,"E23.52.9"),sQuery(id+"F0.wireOp",EDGE,"E23.52.10"),sQuery(id+"F0.wireOp",EDGE,"E23.52.11"),sQuery(id+"F0.wireOp",EDGE,"E23.53.0"),sQuery(id+"F0.wireOp",EDGE,"E23.53.1"),sQuery(id+"F0.wireOp",EDGE,"E23.53.2"),sQuery(id+"F0.wireOp",EDGE,"E23.53.3"),sQuery(id+"F0.wireOp",EDGE,"E23.53.4"),sQuery(id+"F0.wireOp",EDGE,"E23.53.5"),sQuery(id+"F0.wireOp",EDGE,"E23.53.6"),sQuery(id+"F0.wireOp",EDGE,"E23.53.7"),sQuery(id+"F0.wireOp",EDGE,"E23.53.8"),sQuery(id+"F0.wireOp",EDGE,"E23.53.9"),sQuery(id+"F0.wireOp",EDGE,"E23.53.10"),sQuery(id+"F0.wireOp",EDGE,"E23.53.11"),sQuery(id+"F0.wireOp",EDGE,"E23.54.0"),sQuery(id+"F0.wireOp",EDGE,"E23.54.1"),sQuery(id+"F0.wireOp",EDGE,"E23.54.2"),sQuery(id+"F0.wireOp",EDGE,"E23.54.3"),sQuery(id+"F0.wireOp",EDGE,"E23.54.4"),sQuery(id+"F0.wireOp",EDGE,"E23.54.5"),sQuery(id+"F0.wireOp",EDGE,"E23.54.6"),sQuery(id+"F0.wireOp",EDGE,"E23.54.7"),sQuery(id+"F0.wireOp",EDGE,"E23.54.8"),sQuery(id+"F0.wireOp",EDGE,"E23.54.9"),sQuery(id+"F0.wireOp",EDGE,"E23.54.10"),sQuery(id+"F0.wireOp",EDGE,"E23.54.11"),sQuery(id+"F0.wireOp",EDGE,"E23.55.0"),sQuery(id+"F0.wireOp",EDGE,"E23.55.1"),sQuery(id+"F0.wireOp",EDGE,"E23.55.2"),sQuery(id+"F0.wireOp",EDGE,"E23.55.3"),sQuery(id+"F0.wireOp",EDGE,"E23.55.4"),sQuery(id+"F0.wireOp",EDGE,"E23.55.5"),sQuery(id+"F0.wireOp",EDGE,"E23.55.6"),sQuery(id+"F0.wireOp",EDGE,"E23.55.7"),sQuery(id+"F0.wireOp",EDGE,"E23.55.8"),sQuery(id+"F0.wireOp",EDGE,"E23.55.9"),sQuery(id+"F0.wireOp",EDGE,"E23.55.10"),sQuery(id+"F0.wireOp",EDGE,"E23.55.11"),sQuery(id+"F0.wireOp",EDGE,"E23.56.0"),sQuery(id+"F0.wireOp",EDGE,"E23.56.1"),sQuery(id+"F0.wireOp",EDGE,"E23.56.2"),sQuery(id+"F0.wireOp",EDGE,"E23.56.3"),sQuery(id+"F0.wireOp",EDGE,"E23.56.4"),sQuery(id+"F0.wireOp",EDGE,"E23.56.5"),sQuery(id+"F0.wireOp",EDGE,"E23.56.6"),sQuery(id+"F0.wireOp",EDGE,"E23.56.7"),sQuery(id+"F0.wireOp",EDGE,"E23.56.8"),sQuery(id+"F0.wireOp",EDGE,"E23.56.9"),sQuery(id+"F0.wireOp",EDGE,"E23.56.10"),sQuery(id+"F0.wireOp",EDGE,"E23.56.11"),sQuery(id+"F0.wireOp",EDGE,"E23.57.0"),sQuery(id+"F0.wireOp",EDGE,"E23.57.1"),sQuery(id+"F0.wireOp",EDGE,"E23.57.2"),sQuery(id+"F0.wireOp",EDGE,"E23.57.3"),sQuery(id+"F0.wireOp",EDGE,"E23.57.4"),sQuery(id+"F0.wireOp",EDGE,"E23.57.5"),sQuery(id+"F0.wireOp",EDGE,"E23.57.6"),sQuery(id+"F0.wireOp",EDGE,"E23.57.7"),sQuery(id+"F0.wireOp",EDGE,"E23.57.8"),sQuery(id+"F0.wireOp",EDGE,"E23.57.9"),sQuery(id+"F0.wireOp",EDGE,"E23.57.10"),sQuery(id+"F0.wireOp",EDGE,"E23.57.11"),sQuery(id+"F0.wireOp",EDGE,"E23.58.0"),sQuery(id+"F0.wireOp",EDGE,"E23.58.1"),sQuery(id+"F0.wireOp",EDGE,"E23.58.2"),sQuery(id+"F0.wireOp",EDGE,"E23.58.3"),sQuery(id+"F0.wireOp",EDGE,"E23.58.4"),sQuery(id+"F0.wireOp",EDGE,"E23.58.5"),sQuery(id+"F0.wireOp",EDGE,"E23.58.6"),sQuery(id+"F0.wireOp",EDGE,"E23.58.7"),sQuery(id+"F0.wireOp",EDGE,"E23.58.8"),sQuery(id+"F0.wireOp",EDGE,"E23.58.9"),sQuery(id+"F0.wireOp",EDGE,"E23.58.10"),sQuery(id+"F0.wireOp",EDGE,"E23.58.11"),sQuery(id+"F0.wireOp",EDGE,"E23.59.0"),sQuery(id+"F0.wireOp",EDGE,"E23.59.1"),sQuery(id+"F0.wireOp",EDGE,"E23.59.2"),sQuery(id+"F0.wireOp",EDGE,"E23.59.3"),sQuery(id+"F0.wireOp",EDGE,"E23.59.4"),sQuery(id+"F0.wireOp",EDGE,"E23.59.5"),sQuery(id+"F0.wireOp",EDGE,"E23.59.6"),sQuery(id+"F0.wireOp",EDGE,"E23.59.7"),sQuery(id+"F0.wireOp",EDGE,"E23.59.8"),sQuery(id+"F0.wireOp",EDGE,"E23.59.9"),sQuery(id+"F0.wireOp",EDGE,"E23.59.10"),sQuery(id+"F0.wireOp",EDGE,"E23.59.11"),sQuery(id+"F0.wireOp",EDGE,"E23.60.0"),sQuery(id+"F0.wireOp",EDGE,"E23.60.1"),sQuery(id+"F0.wireOp",EDGE,"E23.60.2"),sQuery(id+"F0.wireOp",EDGE,"E23.60.3"),sQuery(id+"F0.wireOp",EDGE,"E23.60.4"),sQuery(id+"F0.wireOp",EDGE,"E23.60.5"),sQuery(id+"F0.wireOp",EDGE,"E23.60.6"),sQuery(id+"F0.wireOp",EDGE,"E23.60.7"),sQuery(id+"F0.wireOp",EDGE,"E23.60.8"),sQuery(id+"F0.wireOp",EDGE,"E23.60.9"),sQuery(id+"F0.wireOp",EDGE,"E23.60.10"),sQuery(id+"F0.wireOp",EDGE,"E23.60.11"),sQuery(id+"F0.wireOp",EDGE,"E23.61.0"),sQuery(id+"F0.wireOp",EDGE,"E23.61.1"),sQuery(id+"F0.wireOp",EDGE,"E23.61.2"),sQuery(id+"F0.wireOp",EDGE,"E23.61.3"),sQuery(id+"F0.wireOp",EDGE,"E23.61.4"),sQuery(id+"F0.wireOp",EDGE,"E23.61.5"),sQuery(id+"F0.wireOp",EDGE,"E23.61.6"),sQuery(id+"F0.wireOp",EDGE,"E23.61.7"),sQuery(id+"F0.wireOp",EDGE,"E23.61.8"),sQuery(id+"F0.wireOp",EDGE,"E23.61.9"),sQuery(id+"F0.wireOp",EDGE,"E23.61.10"),sQuery(id+"F0.wireOp",EDGE,"E23.61.11"),sQuery(id+"F0.wireOp",EDGE,"E23.62.0"),sQuery(id+"F0.wireOp",EDGE,"E23.62.1"),sQuery(id+"F0.wireOp",EDGE,"E23.62.2"),sQuery(id+"F0.wireOp",EDGE,"E23.62.3"),sQuery(id+"F0.wireOp",EDGE,"E23.62.4"),sQuery(id+"F0.wireOp",EDGE,"E23.62.5"),sQuery(id+"F0.wireOp",EDGE,"E23.62.6"),sQuery(id+"F0.wireOp",EDGE,"E23.62.7"),sQuery(id+"F0.wireOp",EDGE,"E23.62.8"),sQuery(id+"F0.wireOp",EDGE,"E23.62.9"),sQuery(id+"F0.wireOp",EDGE,"E23.62.10"),sQuery(id+"F0.wireOp",EDGE,"E23.62.11"),sQuery(id+"F0.wireOp",EDGE,"E23.63.0"),sQuery(id+"F0.wireOp",EDGE,"E23.63.1"),sQuery(id+"F0.wireOp",EDGE,"E23.63.2"),sQuery(id+"F0.wireOp",EDGE,"E23.63.3"),sQuery(id+"F0.wireOp",EDGE,"E23.63.4"),sQuery(id+"F0.wireOp",EDGE,"E23.63.5"),sQuery(id+"F0.wireOp",EDGE,"E23.63.6"),sQuery(id+"F0.wireOp",EDGE,"E23.63.7"),sQuery(id+"F0.wireOp",EDGE,"E23.63.8"),sQuery(id+"F0.wireOp",EDGE,"E23.63.9"),sQuery(id+"F0.wireOp",EDGE,"E23.63.10"),sQuery(id+"F0.wireOp",EDGE,"E23.63.11"),sQuery(id+"F0.wireOp",EDGE,"E23.64.0"),sQuery(id+"F0.wireOp",EDGE,"E23.64.1"),sQuery(id+"F0.wireOp",EDGE,"E23.64.2"),sQuery(id+"F0.wireOp",EDGE,"E23.64.3"),sQuery(id+"F0.wireOp",EDGE,"E23.64.4"),sQuery(id+"F0.wireOp",EDGE,"E23.64.5"),sQuery(id+"F0.wireOp",EDGE,"E23.64.6"),sQuery(id+"F0.wireOp",EDGE,"E23.64.7"),sQuery(id+"F0.wireOp",EDGE,"E23.64.8"),sQuery(id+"F0.wireOp",EDGE,"E23.64.9"),sQuery(id+"F0.wireOp",EDGE,"E23.64.10"),sQuery(id+"F0.wireOp",EDGE,"E23.64.11"),sQuery(id+"F0.wireOp",EDGE,"E23.65.0"),sQuery(id+"F0.wireOp",EDGE,"E23.65.1"),sQuery(id+"F0.wireOp",EDGE,"E23.65.2"),sQuery(id+"F0.wireOp",EDGE,"E23.65.3"),sQuery(id+"F0.wireOp",EDGE,"E23.65.4"),sQuery(id+"F0.wireOp",EDGE,"E23.65.5"),sQuery(id+"F0.wireOp",EDGE,"E23.65.6"),sQuery(id+"F0.wireOp",EDGE,"E23.65.7"),sQuery(id+"F0.wireOp",EDGE,"E23.65.8"),sQuery(id+"F0.wireOp",EDGE,"E23.65.9"),sQuery(id+"F0.wireOp",EDGE,"E23.65.10"),sQuery(id+"F0.wireOp",EDGE,"E23.65.11"),sQuery(id+"F0.wireOp",EDGE,"E23.66.0"),sQuery(id+"F0.wireOp",EDGE,"E23.66.1"),sQuery(id+"F0.wireOp",EDGE,"E23.66.2"),sQuery(id+"F0.wireOp",EDGE,"E23.66.3"),sQuery(id+"F0.wireOp",EDGE,"E23.66.4"),sQuery(id+"F0.wireOp",EDGE,"E23.66.5"),sQuery(id+"F0.wireOp",EDGE,"E23.66.6"),sQuery(id+"F0.wireOp",EDGE,"E23.66.7"),sQuery(id+"F0.wireOp",EDGE,"E23.66.8"),sQuery(id+"F0.wireOp",EDGE,"E23.66.9"),sQuery(id+"F0.wireOp",EDGE,"E23.66.10"),sQuery(id+"F0.wireOp",EDGE,"E23.66.11"),sQuery(id+"F0.wireOp",EDGE,"E23.67.0"),sQuery(id+"F0.wireOp",EDGE,"E23.67.1"),sQuery(id+"F0.wireOp",EDGE,"E23.67.2"),sQuery(id+"F0.wireOp",EDGE,"E23.67.3"),sQuery(id+"F0.wireOp",EDGE,"E23.67.4"),sQuery(id+"F0.wireOp",EDGE,"E23.67.5"),sQuery(id+"F0.wireOp",EDGE,"E23.67.6"),sQuery(id+"F0.wireOp",EDGE,"E23.67.7"),sQuery(id+"F0.wireOp",EDGE,"E23.67.8"),sQuery(id+"F0.wireOp",EDGE,"E23.67.9"),sQuery(id+"F0.wireOp",EDGE,"E23.67.10"),sQuery(id+"F0.wireOp",EDGE,"E23.67.11"),sQuery(id+"F0.wireOp",EDGE,"E23.68.0"),sQuery(id+"F0.wireOp",EDGE,"E23.68.1"),sQuery(id+"F0.wireOp",EDGE,"E23.68.2"),sQuery(id+"F0.wireOp",EDGE,"E23.68.3"),sQuery(id+"F0.wireOp",EDGE,"E23.68.4"),sQuery(id+"F0.wireOp",EDGE,"E23.68.5"),sQuery(id+"F0.wireOp",EDGE,"E23.68.6"),sQuery(id+"F0.wireOp",EDGE,"E23.68.7"),sQuery(id+"F0.wireOp",EDGE,"E23.68.8"),sQuery(id+"F0.wireOp",EDGE,"E23.68.9"),sQuery(id+"F0.wireOp",EDGE,"E23.68.10"),sQuery(id+"F0.wireOp",EDGE,"E23.68.11"),sQuery(id+"F0.wireOp",EDGE,"E23.69.0"),sQuery(id+"F0.wireOp",EDGE,"E23.69.1"),sQuery(id+"F0.wireOp",EDGE,"E23.69.2"),sQuery(id+"F0.wireOp",EDGE,"E23.69.3"),sQuery(id+"F0.wireOp",EDGE,"E23.69.4"),sQuery(id+"F0.wireOp",EDGE,"E23.69.5"),sQuery(id+"F0.wireOp",EDGE,"E23.69.6"),sQuery(id+"F0.wireOp",EDGE,"E23.69.7"),sQuery(id+"F0.wireOp",EDGE,"E23.69.8"),sQuery(id+"F0.wireOp",EDGE,"E23.69.9"),sQuery(id+"F0.wireOp",EDGE,"E23.69.10"),sQuery(id+"F0.wireOp",EDGE,"E23.69.11"),sQuery(id+"F0.wireOp",EDGE,"E23.70.0"),sQuery(id+"F0.wireOp",EDGE,"E23.70.1"),sQuery(id+"F0.wireOp",EDGE,"E23.70.2"),sQuery(id+"F0.wireOp",EDGE,"E23.70.3"),sQuery(id+"F0.wireOp",EDGE,"E23.70.4"),sQuery(id+"F0.wireOp",EDGE,"E23.70.5"),sQuery(id+"F0.wireOp",EDGE,"E23.70.6"),sQuery(id+"F0.wireOp",EDGE,"E23.70.7"),sQuery(id+"F0.wireOp",EDGE,"E23.70.8"),sQuery(id+"F0.wireOp",EDGE,"E23.70.9"),sQuery(id+"F0.wireOp",EDGE,"E23.70.10"),sQuery(id+"F0.wireOp",EDGE,"E23.70.11"),sQuery(id+"F0.wireOp",EDGE,"E23.71.0"),sQuery(id+"F0.wireOp",EDGE,"E23.71.1"),sQuery(id+"F0.wireOp",EDGE,"E23.71.2"),sQuery(id+"F0.wireOp",EDGE,"E23.71.3"),sQuery(id+"F0.wireOp",EDGE,"E23.71.4"),sQuery(id+"F0.wireOp",EDGE,"E23.71.5"),sQuery(id+"F0.wireOp",EDGE,"E23.71.6"),sQuery(id+"F0.wireOp",EDGE,"E23.71.7"),sQuery(id+"F0.wireOp",EDGE,"E23.71.8"),sQuery(id+"F0.wireOp",EDGE,"E23.71.9"),sQuery(id+"F0.wireOp",EDGE,"E23.71.10"),sQuery(id+"F0.wireOp",EDGE,"E23.71.11"),sQuery(id+"F0.wireOp",EDGE,"E24.trimOffspring"),sQuery(id+"F0.wireOp",EDGE,"E25.trimOffspring"),sQuery(id+"F0.wireOp",EDGE,"E26.trimOffspring"),sQuery(id+"F0.wireOp",EDGE,"E27.trimOffspring"),sQuery(id+"F0.wireOp",EDGE,"E28.trimOffspring"),sQuery(id+"F0.wireOp",EDGE,"E29.trimOffspring"),sQuery(id+"F0.wireOp",EDGE,"E30.trimOffspring"),sQuery(id+"F0.wireOp",EDGE,"E31.trimOffspring"),sQuery(id+"F0.wireOp",EDGE,"E32.trimOffspring"),sQuery(id+"F0.wireOp",EDGE,"E33.trimOffspring"),sQuery(id+"F0.wireOp",EDGE,"E34.trimOffspring"),sQuery(id+"F0.wireOp",EDGE,"E35.trimOffspring"),sQuery(id+"F0.wireOp",EDGE,"E36.trimOffspring"),sQuery(id+"F0.wireOp",EDGE,"E37.trimOffspring"),sQuery(id+"F0.wireOp",EDGE,"E38.trimOffspring"),sQuery(id+"F0.wireOp",EDGE,"E39.trimOffspring"),sQuery(id+"F0.wireOp",EDGE,"E40.trimOffspring"),sQuery(id+"F0.wireOp",EDGE,"E41.trimOffspring"),sQuery(id+"F0.wireOp",EDGE,"E42.trimOffspring"),sQuery(id+"F0.wireOp",EDGE,"E43.trimOffspring"),sQuery(id+"F0.wireOp",EDGE,"E44.trimOffspring"),sQuery(id+"F0.wireOp",EDGE,"E45.trimOffspring"),sQuery(id+"F0.wireOp",EDGE,"E46.trimOffspring"),sQuery(id+"F0.wireOp",EDGE,"E47.trimOffspring"),sQuery(id+"F0.wireOp",EDGE,"E48.trimOffspring"),sQuery(id+"F0.wireOp",EDGE,"E49.trimOffspring"),sQuery(id+"F0.wireOp",EDGE,"E50.trimOffspring"),sQuery(id+"F0.wireOp",EDGE,"E51.trimOffspring"),sQuery(id+"F0.wireOp",EDGE,"E52.trimOffspring"),sQuery(id+"F0.wireOp",EDGE,"E53.trimOffspring"),sQuery(id+"F0.wireOp",EDGE,"E54.trimOffspring"),sQuery(id+"F0.wireOp",EDGE,"E55.trimOffspring"),sQuery(id+"F0.wireOp",EDGE,"E56.trimOffspring"),sQuery(id+"F0.wireOp",EDGE,"E57.trimOffspring"),sQuery(id+"F0.wireOp",EDGE,"E58.trimOffspring"),sQuery(id+"F0.wireOp",EDGE,"E59.trimOffspring"),sQuery(id+"F0.wireOp",EDGE,"E60.trimOffspring"),sQuery(id+"F0.wireOp",EDGE,"E61.trimOffspring"),sQuery(id+"F0.wireOp",EDGE,"E62.trimOffspring"),sQuery(id+"F0.wireOp",EDGE,"E63.trimOffspring"),sQuery(id+"F0.wireOp",EDGE,"E64.trimOffspring"),sQuery(id+"F0.wireOp",EDGE,"E65.trimOffspring"),sQuery(id+"F0.wireOp",EDGE,"E66.trimOffspring"),sQuery(id+"F0.wireOp",EDGE,"E67.trimOffspring"),sQuery(id+"F0.wireOp",EDGE,"E68.trimOffspring"),sQuery(id+"F0.wireOp",EDGE,"E69.trimOffspring"),sQuery(id+"F0.wireOp",EDGE,"E70.trimOffspring"),sQuery(id+"F0.wireOp",EDGE,"E71.trimOffspring"),sQuery(id+"F0.wireOp",EDGE,"E72.trimOffspring"),sQuery(id+"F0.wireOp",EDGE,"E73.trimOffspring"),sQuery(id+"F0.wireOp",EDGE,"E74.trimOffspring"),sQuery(id+"F0.wireOp",EDGE,"E75.trimOffspring"),sQuery(id+"F0.wireOp",EDGE,"E76.trimOffspring"),sQuery(id+"F0.wireOp",EDGE,"E77.trimOffspring"),sQuery(id+"F0.wireOp",EDGE,"E78.trimOffspring"),sQuery(id+"F0.wireOp",EDGE,"E79.trimOffspring"),sQuery(id+"F0.wireOp",EDGE,"E80.trimOffspring"),sQuery(id+"F0.wireOp",EDGE,"E81.trimOffspring"),sQuery(id+"F0.wireOp",EDGE,"E82.trimOffspring"),sQuery(id+"F0.wireOp",EDGE,"E83.trimOffspring"),sQuery(id+"F0.wireOp",EDGE,"E84.trimOffspring"),sQuery(id+"F0.wireOp",EDGE,"E85.trimOffspring"),sQuery(id+"F0.wireOp",EDGE,"E86.trimOffspring"),sQuery(id+"F0.wireOp",EDGE,"E87.trimOffspring"),sQuery(id+"F0.wireOp",EDGE,"E88.trimOffspring"),sQuery(id+"F0.wireOp",EDGE,"E89.trimOffspring"),sQuery(id+"F0.wireOp",EDGE,"E90.trimOffspring"),sQuery(id+"F0.wireOp",EDGE,"E91.trimOffspring"),sQuery(id+"F0.wireOp",EDGE,"E92.trimOffspring"),sQuery(id+"F0.wireOp",EDGE,"E93.trimOffspring"),sQuery(id+"F0.wireOp",EDGE,"E94")])],"isStart":false});
            var sketch = newSketch(context, id + "F3", { "sketchPlane" : qUnion([Q0])});
            skCircle(sketch, "E95", {"center": v(50.8, 0) * mm, "radius": 3.18 * mm});
            skCircle(sketch, "E96.1.0", {"center": v(-25.4, 44) * mm, "radius": 3.18 * mm});
            skCircle(sketch, "E96.2.0", {"center": v(-25.4, -44) * mm, "radius": 3.18 * mm});
            skPoint(sketch, "E96.center", {"position": v(0, 0) * mm});
            skSolve(sketch);
        }
        {
            var Q0;
            Q0=qSketchRegion(id+"F3",true);
            extrude(context, id + "F4", {"entities" : qUnion([Q0]), "operationType" : NewBodyOperationType.ADD, "depth" : 12.7 * mm});
        }
        {
            var Q0;
            Q0=makeQuery(id+"F1.opExtrude","CAP_FACE",FACE,{"disambiguationData":[OSD([sQuery(id+"F0.wireOp",EDGE,"E0"),sQuery(id+"F0.wireOp",EDGE,"E1.MirrorCS"),sQuery(id+"F0.wireOp",EDGE,"E2.MirrorCS"),sQuery(id+"F0.wireOp",EDGE,"E3.MirrorCS"),sQuery(id+"F0.wireOp",EDGE,"E4.MirrorCS"),sQuery(id+"F0.wireOp",EDGE,"E5.MirrorCS"),sQuery(id+"F0.wireOp",EDGE,"E6.MirrorCS"),sQuery(id+"F0.wireOp",EDGE,"E16.filletArc"),sQuery(id+"F0.wireOp",EDGE,"E17.filletArc"),sQuery(id+"F0.wireOp",EDGE,"E18.filletArc"),sQuery(id+"F0.wireOp",EDGE,"E19.filletArc"),sQuery(id+"F0.wireOp",EDGE,"E20.filletArc"),sQuery(id+"F0.wireOp",EDGE,"E21.filletArc"),sQuery(id+"F0.wireOp",EDGE,"E23.1.0"),sQuery(id+"F0.wireOp",EDGE,"E23.1.1"),sQuery(id+"F0.wireOp",EDGE,"E23.1.2"),sQuery(id+"F0.wireOp",EDGE,"E23.1.3"),sQuery(id+"F0.wireOp",EDGE,"E23.1.4"),sQuery(id+"F0.wireOp",EDGE,"E23.1.5"),sQuery(id+"F0.wireOp",EDGE,"E23.1.6"),sQuery(id+"F0.wireOp",EDGE,"E23.1.7"),sQuery(id+"F0.wireOp",EDGE,"E23.1.8"),sQuery(id+"F0.wireOp",EDGE,"E23.1.9"),sQuery(id+"F0.wireOp",EDGE,"E23.1.10"),sQuery(id+"F0.wireOp",EDGE,"E23.1.11"),sQuery(id+"F0.wireOp",EDGE,"E23.2.0"),sQuery(id+"F0.wireOp",EDGE,"E23.2.1"),sQuery(id+"F0.wireOp",EDGE,"E23.2.2"),sQuery(id+"F0.wireOp",EDGE,"E23.2.3"),sQuery(id+"F0.wireOp",EDGE,"E23.2.4"),sQuery(id+"F0.wireOp",EDGE,"E23.2.5"),sQuery(id+"F0.wireOp",EDGE,"E23.2.6"),sQuery(id+"F0.wireOp",EDGE,"E23.2.7"),sQuery(id+"F0.wireOp",EDGE,"E23.2.8"),sQuery(id+"F0.wireOp",EDGE,"E23.2.9"),sQuery(id+"F0.wireOp",EDGE,"E23.2.10"),sQuery(id+"F0.wireOp",EDGE,"E23.2.11"),sQuery(id+"F0.wireOp",EDGE,"E23.3.0"),sQuery(id+"F0.wireOp",EDGE,"E23.3.1"),sQuery(id+"F0.wireOp",EDGE,"E23.3.2"),sQuery(id+"F0.wireOp",EDGE,"E23.3.3"),sQuery(id+"F0.wireOp",EDGE,"E23.3.4"),sQuery(id+"F0.wireOp",EDGE,"E23.3.5"),sQuery(id+"F0.wireOp",EDGE,"E23.3.6"),sQuery(id+"F0.wireOp",EDGE,"E23.3.7"),sQuery(id+"F0.wireOp",EDGE,"E23.3.8"),sQuery(id+"F0.wireOp",EDGE,"E23.3.9"),sQuery(id+"F0.wireOp",EDGE,"E23.3.10"),sQuery(id+"F0.wireOp",EDGE,"E23.3.11"),sQuery(id+"F0.wireOp",EDGE,"E23.4.0"),sQuery(id+"F0.wireOp",EDGE,"E23.4.1"),sQuery(id+"F0.wireOp",EDGE,"E23.4.2"),sQuery(id+"F0.wireOp",EDGE,"E23.4.3"),sQuery(id+"F0.wireOp",EDGE,"E23.4.4"),sQuery(id+"F0.wireOp",EDGE,"E23.4.5"),sQuery(id+"F0.wireOp",EDGE,"E23.4.6"),sQuery(id+"F0.wireOp",EDGE,"E23.4.7"),sQuery(id+"F0.wireOp",EDGE,"E23.4.8"),sQuery(id+"F0.wireOp",EDGE,"E23.4.9"),sQuery(id+"F0.wireOp",EDGE,"E23.4.10"),sQuery(id+"F0.wireOp",EDGE,"E23.4.11"),sQuery(id+"F0.wireOp",EDGE,"E23.5.0"),sQuery(id+"F0.wireOp",EDGE,"E23.5.1"),sQuery(id+"F0.wireOp",EDGE,"E23.5.2"),sQuery(id+"F0.wireOp",EDGE,"E23.5.3"),sQuery(id+"F0.wireOp",EDGE,"E23.5.4"),sQuery(id+"F0.wireOp",EDGE,"E23.5.5"),sQuery(id+"F0.wireOp",EDGE,"E23.5.6"),sQuery(id+"F0.wireOp",EDGE,"E23.5.7"),sQuery(id+"F0.wireOp",EDGE,"E23.5.8"),sQuery(id+"F0.wireOp",EDGE,"E23.5.9"),sQuery(id+"F0.wireOp",EDGE,"E23.5.10"),sQuery(id+"F0.wireOp",EDGE,"E23.5.11"),sQuery(id+"F0.wireOp",EDGE,"E23.6.0"),sQuery(id+"F0.wireOp",EDGE,"E23.6.1"),sQuery(id+"F0.wireOp",EDGE,"E23.6.2"),sQuery(id+"F0.wireOp",EDGE,"E23.6.3"),sQuery(id+"F0.wireOp",EDGE,"E23.6.4"),sQuery(id+"F0.wireOp",EDGE,"E23.6.5"),sQuery(id+"F0.wireOp",EDGE,"E23.6.6"),sQuery(id+"F0.wireOp",EDGE,"E23.6.7"),sQuery(id+"F0.wireOp",EDGE,"E23.6.8"),sQuery(id+"F0.wireOp",EDGE,"E23.6.9"),sQuery(id+"F0.wireOp",EDGE,"E23.6.10"),sQuery(id+"F0.wireOp",EDGE,"E23.6.11"),sQuery(id+"F0.wireOp",EDGE,"E23.7.0"),sQuery(id+"F0.wireOp",EDGE,"E23.7.1"),sQuery(id+"F0.wireOp",EDGE,"E23.7.2"),sQuery(id+"F0.wireOp",EDGE,"E23.7.3"),sQuery(id+"F0.wireOp",EDGE,"E23.7.4"),sQuery(id+"F0.wireOp",EDGE,"E23.7.5"),sQuery(id+"F0.wireOp",EDGE,"E23.7.6"),sQuery(id+"F0.wireOp",EDGE,"E23.7.7"),sQuery(id+"F0.wireOp",EDGE,"E23.7.8"),sQuery(id+"F0.wireOp",EDGE,"E23.7.9"),sQuery(id+"F0.wireOp",EDGE,"E23.7.10"),sQuery(id+"F0.wireOp",EDGE,"E23.7.11"),sQuery(id+"F0.wireOp",EDGE,"E23.8.0"),sQuery(id+"F0.wireOp",EDGE,"E23.8.1"),sQuery(id+"F0.wireOp",EDGE,"E23.8.2"),sQuery(id+"F0.wireOp",EDGE,"E23.8.3"),sQuery(id+"F0.wireOp",EDGE,"E23.8.4"),sQuery(id+"F0.wireOp",EDGE,"E23.8.5"),sQuery(id+"F0.wireOp",EDGE,"E23.8.6"),sQuery(id+"F0.wireOp",EDGE,"E23.8.7"),sQuery(id+"F0.wireOp",EDGE,"E23.8.8"),sQuery(id+"F0.wireOp",EDGE,"E23.8.9"),sQuery(id+"F0.wireOp",EDGE,"E23.8.10"),sQuery(id+"F0.wireOp",EDGE,"E23.8.11"),sQuery(id+"F0.wireOp",EDGE,"E23.9.0"),sQuery(id+"F0.wireOp",EDGE,"E23.9.1"),sQuery(id+"F0.wireOp",EDGE,"E23.9.2"),sQuery(id+"F0.wireOp",EDGE,"E23.9.3"),sQuery(id+"F0.wireOp",EDGE,"E23.9.4"),sQuery(id+"F0.wireOp",EDGE,"E23.9.5"),sQuery(id+"F0.wireOp",EDGE,"E23.9.6"),sQuery(id+"F0.wireOp",EDGE,"E23.9.7"),sQuery(id+"F0.wireOp",EDGE,"E23.9.8"),sQuery(id+"F0.wireOp",EDGE,"E23.9.9"),sQuery(id+"F0.wireOp",EDGE,"E23.9.10"),sQuery(id+"F0.wireOp",EDGE,"E23.9.11"),sQuery(id+"F0.wireOp",EDGE,"E23.10.0"),sQuery(id+"F0.wireOp",EDGE,"E23.10.1"),sQuery(id+"F0.wireOp",EDGE,"E23.10.2"),sQuery(id+"F0.wireOp",EDGE,"E23.10.3"),sQuery(id+"F0.wireOp",EDGE,"E23.10.4"),sQuery(id+"F0.wireOp",EDGE,"E23.10.5"),sQuery(id+"F0.wireOp",EDGE,"E23.10.6"),sQuery(id+"F0.wireOp",EDGE,"E23.10.7"),sQuery(id+"F0.wireOp",EDGE,"E23.10.8"),sQuery(id+"F0.wireOp",EDGE,"E23.10.9"),sQuery(id+"F0.wireOp",EDGE,"E23.10.10"),sQuery(id+"F0.wireOp",EDGE,"E23.10.11"),sQuery(id+"F0.wireOp",EDGE,"E23.11.0"),sQuery(id+"F0.wireOp",EDGE,"E23.11.1"),sQuery(id+"F0.wireOp",EDGE,"E23.11.2"),sQuery(id+"F0.wireOp",EDGE,"E23.11.3"),sQuery(id+"F0.wireOp",EDGE,"E23.11.4"),sQuery(id+"F0.wireOp",EDGE,"E23.11.5"),sQuery(id+"F0.wireOp",EDGE,"E23.11.6"),sQuery(id+"F0.wireOp",EDGE,"E23.11.7"),sQuery(id+"F0.wireOp",EDGE,"E23.11.8"),sQuery(id+"F0.wireOp",EDGE,"E23.11.9"),sQuery(id+"F0.wireOp",EDGE,"E23.11.10"),sQuery(id+"F0.wireOp",EDGE,"E23.11.11"),sQuery(id+"F0.wireOp",EDGE,"E23.12.0"),sQuery(id+"F0.wireOp",EDGE,"E23.12.1"),sQuery(id+"F0.wireOp",EDGE,"E23.12.2"),sQuery(id+"F0.wireOp",EDGE,"E23.12.3"),sQuery(id+"F0.wireOp",EDGE,"E23.12.4"),sQuery(id+"F0.wireOp",EDGE,"E23.12.5"),sQuery(id+"F0.wireOp",EDGE,"E23.12.6"),sQuery(id+"F0.wireOp",EDGE,"E23.12.7"),sQuery(id+"F0.wireOp",EDGE,"E23.12.8"),sQuery(id+"F0.wireOp",EDGE,"E23.12.9"),sQuery(id+"F0.wireOp",EDGE,"E23.12.10"),sQuery(id+"F0.wireOp",EDGE,"E23.12.11"),sQuery(id+"F0.wireOp",EDGE,"E23.13.0"),sQuery(id+"F0.wireOp",EDGE,"E23.13.1"),sQuery(id+"F0.wireOp",EDGE,"E23.13.2"),sQuery(id+"F0.wireOp",EDGE,"E23.13.3"),sQuery(id+"F0.wireOp",EDGE,"E23.13.4"),sQuery(id+"F0.wireOp",EDGE,"E23.13.5"),sQuery(id+"F0.wireOp",EDGE,"E23.13.6"),sQuery(id+"F0.wireOp",EDGE,"E23.13.7"),sQuery(id+"F0.wireOp",EDGE,"E23.13.8"),sQuery(id+"F0.wireOp",EDGE,"E23.13.9"),sQuery(id+"F0.wireOp",EDGE,"E23.13.10"),sQuery(id+"F0.wireOp",EDGE,"E23.13.11"),sQuery(id+"F0.wireOp",EDGE,"E23.14.0"),sQuery(id+"F0.wireOp",EDGE,"E23.14.1"),sQuery(id+"F0.wireOp",EDGE,"E23.14.2"),sQuery(id+"F0.wireOp",EDGE,"E23.14.3"),sQuery(id+"F0.wireOp",EDGE,"E23.14.4"),sQuery(id+"F0.wireOp",EDGE,"E23.14.5"),sQuery(id+"F0.wireOp",EDGE,"E23.14.6"),sQuery(id+"F0.wireOp",EDGE,"E23.14.7"),sQuery(id+"F0.wireOp",EDGE,"E23.14.8"),sQuery(id+"F0.wireOp",EDGE,"E23.14.9"),sQuery(id+"F0.wireOp",EDGE,"E23.14.10"),sQuery(id+"F0.wireOp",EDGE,"E23.14.11"),sQuery(id+"F0.wireOp",EDGE,"E23.15.0"),sQuery(id+"F0.wireOp",EDGE,"E23.15.1"),sQuery(id+"F0.wireOp",EDGE,"E23.15.2"),sQuery(id+"F0.wireOp",EDGE,"E23.15.3"),sQuery(id+"F0.wireOp",EDGE,"E23.15.4"),sQuery(id+"F0.wireOp",EDGE,"E23.15.5"),sQuery(id+"F0.wireOp",EDGE,"E23.15.6"),sQuery(id+"F0.wireOp",EDGE,"E23.15.7"),sQuery(id+"F0.wireOp",EDGE,"E23.15.8"),sQuery(id+"F0.wireOp",EDGE,"E23.15.9"),sQuery(id+"F0.wireOp",EDGE,"E23.15.10"),sQuery(id+"F0.wireOp",EDGE,"E23.15.11"),sQuery(id+"F0.wireOp",EDGE,"E23.16.0"),sQuery(id+"F0.wireOp",EDGE,"E23.16.1"),sQuery(id+"F0.wireOp",EDGE,"E23.16.2"),sQuery(id+"F0.wireOp",EDGE,"E23.16.3"),sQuery(id+"F0.wireOp",EDGE,"E23.16.4"),sQuery(id+"F0.wireOp",EDGE,"E23.16.5"),sQuery(id+"F0.wireOp",EDGE,"E23.16.6"),sQuery(id+"F0.wireOp",EDGE,"E23.16.7"),sQuery(id+"F0.wireOp",EDGE,"E23.16.8"),sQuery(id+"F0.wireOp",EDGE,"E23.16.9"),sQuery(id+"F0.wireOp",EDGE,"E23.16.10"),sQuery(id+"F0.wireOp",EDGE,"E23.16.11"),sQuery(id+"F0.wireOp",EDGE,"E23.17.0"),sQuery(id+"F0.wireOp",EDGE,"E23.17.1"),sQuery(id+"F0.wireOp",EDGE,"E23.17.2"),sQuery(id+"F0.wireOp",EDGE,"E23.17.3"),sQuery(id+"F0.wireOp",EDGE,"E23.17.4"),sQuery(id+"F0.wireOp",EDGE,"E23.17.5"),sQuery(id+"F0.wireOp",EDGE,"E23.17.6"),sQuery(id+"F0.wireOp",EDGE,"E23.17.7"),sQuery(id+"F0.wireOp",EDGE,"E23.17.8"),sQuery(id+"F0.wireOp",EDGE,"E23.17.9"),sQuery(id+"F0.wireOp",EDGE,"E23.17.10"),sQuery(id+"F0.wireOp",EDGE,"E23.17.11"),sQuery(id+"F0.wireOp",EDGE,"E23.18.0"),sQuery(id+"F0.wireOp",EDGE,"E23.18.1"),sQuery(id+"F0.wireOp",EDGE,"E23.18.2"),sQuery(id+"F0.wireOp",EDGE,"E23.18.3"),sQuery(id+"F0.wireOp",EDGE,"E23.18.4"),sQuery(id+"F0.wireOp",EDGE,"E23.18.5"),sQuery(id+"F0.wireOp",EDGE,"E23.18.6"),sQuery(id+"F0.wireOp",EDGE,"E23.18.7"),sQuery(id+"F0.wireOp",EDGE,"E23.18.8"),sQuery(id+"F0.wireOp",EDGE,"E23.18.9"),sQuery(id+"F0.wireOp",EDGE,"E23.18.10"),sQuery(id+"F0.wireOp",EDGE,"E23.18.11"),sQuery(id+"F0.wireOp",EDGE,"E23.19.0"),sQuery(id+"F0.wireOp",EDGE,"E23.19.1"),sQuery(id+"F0.wireOp",EDGE,"E23.19.2"),sQuery(id+"F0.wireOp",EDGE,"E23.19.3"),sQuery(id+"F0.wireOp",EDGE,"E23.19.4"),sQuery(id+"F0.wireOp",EDGE,"E23.19.5"),sQuery(id+"F0.wireOp",EDGE,"E23.19.6"),sQuery(id+"F0.wireOp",EDGE,"E23.19.7"),sQuery(id+"F0.wireOp",EDGE,"E23.19.8"),sQuery(id+"F0.wireOp",EDGE,"E23.19.9"),sQuery(id+"F0.wireOp",EDGE,"E23.19.10"),sQuery(id+"F0.wireOp",EDGE,"E23.19.11"),sQuery(id+"F0.wireOp",EDGE,"E23.20.0"),sQuery(id+"F0.wireOp",EDGE,"E23.20.1"),sQuery(id+"F0.wireOp",EDGE,"E23.20.2"),sQuery(id+"F0.wireOp",EDGE,"E23.20.3"),sQuery(id+"F0.wireOp",EDGE,"E23.20.4"),sQuery(id+"F0.wireOp",EDGE,"E23.20.5"),sQuery(id+"F0.wireOp",EDGE,"E23.20.6"),sQuery(id+"F0.wireOp",EDGE,"E23.20.7"),sQuery(id+"F0.wireOp",EDGE,"E23.20.8"),sQuery(id+"F0.wireOp",EDGE,"E23.20.9"),sQuery(id+"F0.wireOp",EDGE,"E23.20.10"),sQuery(id+"F0.wireOp",EDGE,"E23.20.11"),sQuery(id+"F0.wireOp",EDGE,"E23.21.0"),sQuery(id+"F0.wireOp",EDGE,"E23.21.1"),sQuery(id+"F0.wireOp",EDGE,"E23.21.2"),sQuery(id+"F0.wireOp",EDGE,"E23.21.3"),sQuery(id+"F0.wireOp",EDGE,"E23.21.4"),sQuery(id+"F0.wireOp",EDGE,"E23.21.5"),sQuery(id+"F0.wireOp",EDGE,"E23.21.6"),sQuery(id+"F0.wireOp",EDGE,"E23.21.7"),sQuery(id+"F0.wireOp",EDGE,"E23.21.8"),sQuery(id+"F0.wireOp",EDGE,"E23.21.9"),sQuery(id+"F0.wireOp",EDGE,"E23.21.10"),sQuery(id+"F0.wireOp",EDGE,"E23.21.11"),sQuery(id+"F0.wireOp",EDGE,"E23.22.0"),sQuery(id+"F0.wireOp",EDGE,"E23.22.1"),sQuery(id+"F0.wireOp",EDGE,"E23.22.2"),sQuery(id+"F0.wireOp",EDGE,"E23.22.3"),sQuery(id+"F0.wireOp",EDGE,"E23.22.4"),sQuery(id+"F0.wireOp",EDGE,"E23.22.5"),sQuery(id+"F0.wireOp",EDGE,"E23.22.6"),sQuery(id+"F0.wireOp",EDGE,"E23.22.7"),sQuery(id+"F0.wireOp",EDGE,"E23.22.8"),sQuery(id+"F0.wireOp",EDGE,"E23.22.9"),sQuery(id+"F0.wireOp",EDGE,"E23.22.10"),sQuery(id+"F0.wireOp",EDGE,"E23.22.11"),sQuery(id+"F0.wireOp",EDGE,"E23.23.0"),sQuery(id+"F0.wireOp",EDGE,"E23.23.1"),sQuery(id+"F0.wireOp",EDGE,"E23.23.2"),sQuery(id+"F0.wireOp",EDGE,"E23.23.3"),sQuery(id+"F0.wireOp",EDGE,"E23.23.4"),sQuery(id+"F0.wireOp",EDGE,"E23.23.5"),sQuery(id+"F0.wireOp",EDGE,"E23.23.6"),sQuery(id+"F0.wireOp",EDGE,"E23.23.7"),sQuery(id+"F0.wireOp",EDGE,"E23.23.8"),sQuery(id+"F0.wireOp",EDGE,"E23.23.9"),sQuery(id+"F0.wireOp",EDGE,"E23.23.10"),sQuery(id+"F0.wireOp",EDGE,"E23.23.11"),sQuery(id+"F0.wireOp",EDGE,"E23.24.0"),sQuery(id+"F0.wireOp",EDGE,"E23.24.1"),sQuery(id+"F0.wireOp",EDGE,"E23.24.2"),sQuery(id+"F0.wireOp",EDGE,"E23.24.3"),sQuery(id+"F0.wireOp",EDGE,"E23.24.4"),sQuery(id+"F0.wireOp",EDGE,"E23.24.5"),sQuery(id+"F0.wireOp",EDGE,"E23.24.6"),sQuery(id+"F0.wireOp",EDGE,"E23.24.7"),sQuery(id+"F0.wireOp",EDGE,"E23.24.8"),sQuery(id+"F0.wireOp",EDGE,"E23.24.9"),sQuery(id+"F0.wireOp",EDGE,"E23.24.10"),sQuery(id+"F0.wireOp",EDGE,"E23.24.11"),sQuery(id+"F0.wireOp",EDGE,"E23.25.0"),sQuery(id+"F0.wireOp",EDGE,"E23.25.1"),sQuery(id+"F0.wireOp",EDGE,"E23.25.2"),sQuery(id+"F0.wireOp",EDGE,"E23.25.3"),sQuery(id+"F0.wireOp",EDGE,"E23.25.4"),sQuery(id+"F0.wireOp",EDGE,"E23.25.5"),sQuery(id+"F0.wireOp",EDGE,"E23.25.6"),sQuery(id+"F0.wireOp",EDGE,"E23.25.7"),sQuery(id+"F0.wireOp",EDGE,"E23.25.8"),sQuery(id+"F0.wireOp",EDGE,"E23.25.9"),sQuery(id+"F0.wireOp",EDGE,"E23.25.10"),sQuery(id+"F0.wireOp",EDGE,"E23.25.11"),sQuery(id+"F0.wireOp",EDGE,"E23.26.0"),sQuery(id+"F0.wireOp",EDGE,"E23.26.1"),sQuery(id+"F0.wireOp",EDGE,"E23.26.2"),sQuery(id+"F0.wireOp",EDGE,"E23.26.3"),sQuery(id+"F0.wireOp",EDGE,"E23.26.4"),sQuery(id+"F0.wireOp",EDGE,"E23.26.5"),sQuery(id+"F0.wireOp",EDGE,"E23.26.6"),sQuery(id+"F0.wireOp",EDGE,"E23.26.7"),sQuery(id+"F0.wireOp",EDGE,"E23.26.8"),sQuery(id+"F0.wireOp",EDGE,"E23.26.9"),sQuery(id+"F0.wireOp",EDGE,"E23.26.10"),sQuery(id+"F0.wireOp",EDGE,"E23.26.11"),sQuery(id+"F0.wireOp",EDGE,"E23.27.0"),sQuery(id+"F0.wireOp",EDGE,"E23.27.1"),sQuery(id+"F0.wireOp",EDGE,"E23.27.2"),sQuery(id+"F0.wireOp",EDGE,"E23.27.3"),sQuery(id+"F0.wireOp",EDGE,"E23.27.4"),sQuery(id+"F0.wireOp",EDGE,"E23.27.5"),sQuery(id+"F0.wireOp",EDGE,"E23.27.6"),sQuery(id+"F0.wireOp",EDGE,"E23.27.7"),sQuery(id+"F0.wireOp",EDGE,"E23.27.8"),sQuery(id+"F0.wireOp",EDGE,"E23.27.9"),sQuery(id+"F0.wireOp",EDGE,"E23.27.10"),sQuery(id+"F0.wireOp",EDGE,"E23.27.11"),sQuery(id+"F0.wireOp",EDGE,"E23.28.0"),sQuery(id+"F0.wireOp",EDGE,"E23.28.1"),sQuery(id+"F0.wireOp",EDGE,"E23.28.2"),sQuery(id+"F0.wireOp",EDGE,"E23.28.3"),sQuery(id+"F0.wireOp",EDGE,"E23.28.4"),sQuery(id+"F0.wireOp",EDGE,"E23.28.5"),sQuery(id+"F0.wireOp",EDGE,"E23.28.6"),sQuery(id+"F0.wireOp",EDGE,"E23.28.7"),sQuery(id+"F0.wireOp",EDGE,"E23.28.8"),sQuery(id+"F0.wireOp",EDGE,"E23.28.9"),sQuery(id+"F0.wireOp",EDGE,"E23.28.10"),sQuery(id+"F0.wireOp",EDGE,"E23.28.11"),sQuery(id+"F0.wireOp",EDGE,"E23.29.0"),sQuery(id+"F0.wireOp",EDGE,"E23.29.1"),sQuery(id+"F0.wireOp",EDGE,"E23.29.2"),sQuery(id+"F0.wireOp",EDGE,"E23.29.3"),sQuery(id+"F0.wireOp",EDGE,"E23.29.4"),sQuery(id+"F0.wireOp",EDGE,"E23.29.5"),sQuery(id+"F0.wireOp",EDGE,"E23.29.6"),sQuery(id+"F0.wireOp",EDGE,"E23.29.7"),sQuery(id+"F0.wireOp",EDGE,"E23.29.8"),sQuery(id+"F0.wireOp",EDGE,"E23.29.9"),sQuery(id+"F0.wireOp",EDGE,"E23.29.10"),sQuery(id+"F0.wireOp",EDGE,"E23.29.11"),sQuery(id+"F0.wireOp",EDGE,"E23.30.0"),sQuery(id+"F0.wireOp",EDGE,"E23.30.1"),sQuery(id+"F0.wireOp",EDGE,"E23.30.2"),sQuery(id+"F0.wireOp",EDGE,"E23.30.3"),sQuery(id+"F0.wireOp",EDGE,"E23.30.4"),sQuery(id+"F0.wireOp",EDGE,"E23.30.5"),sQuery(id+"F0.wireOp",EDGE,"E23.30.6"),sQuery(id+"F0.wireOp",EDGE,"E23.30.7"),sQuery(id+"F0.wireOp",EDGE,"E23.30.8"),sQuery(id+"F0.wireOp",EDGE,"E23.30.9"),sQuery(id+"F0.wireOp",EDGE,"E23.30.10"),sQuery(id+"F0.wireOp",EDGE,"E23.30.11"),sQuery(id+"F0.wireOp",EDGE,"E23.31.0"),sQuery(id+"F0.wireOp",EDGE,"E23.31.1"),sQuery(id+"F0.wireOp",EDGE,"E23.31.2"),sQuery(id+"F0.wireOp",EDGE,"E23.31.3"),sQuery(id+"F0.wireOp",EDGE,"E23.31.4"),sQuery(id+"F0.wireOp",EDGE,"E23.31.5"),sQuery(id+"F0.wireOp",EDGE,"E23.31.6"),sQuery(id+"F0.wireOp",EDGE,"E23.31.7"),sQuery(id+"F0.wireOp",EDGE,"E23.31.8"),sQuery(id+"F0.wireOp",EDGE,"E23.31.9"),sQuery(id+"F0.wireOp",EDGE,"E23.31.10"),sQuery(id+"F0.wireOp",EDGE,"E23.31.11"),sQuery(id+"F0.wireOp",EDGE,"E23.32.0"),sQuery(id+"F0.wireOp",EDGE,"E23.32.1"),sQuery(id+"F0.wireOp",EDGE,"E23.32.2"),sQuery(id+"F0.wireOp",EDGE,"E23.32.3"),sQuery(id+"F0.wireOp",EDGE,"E23.32.4"),sQuery(id+"F0.wireOp",EDGE,"E23.32.5"),sQuery(id+"F0.wireOp",EDGE,"E23.32.6"),sQuery(id+"F0.wireOp",EDGE,"E23.32.7"),sQuery(id+"F0.wireOp",EDGE,"E23.32.8"),sQuery(id+"F0.wireOp",EDGE,"E23.32.9"),sQuery(id+"F0.wireOp",EDGE,"E23.32.10"),sQuery(id+"F0.wireOp",EDGE,"E23.32.11"),sQuery(id+"F0.wireOp",EDGE,"E23.33.0"),sQuery(id+"F0.wireOp",EDGE,"E23.33.1"),sQuery(id+"F0.wireOp",EDGE,"E23.33.2"),sQuery(id+"F0.wireOp",EDGE,"E23.33.3"),sQuery(id+"F0.wireOp",EDGE,"E23.33.4"),sQuery(id+"F0.wireOp",EDGE,"E23.33.5"),sQuery(id+"F0.wireOp",EDGE,"E23.33.6"),sQuery(id+"F0.wireOp",EDGE,"E23.33.7"),sQuery(id+"F0.wireOp",EDGE,"E23.33.8"),sQuery(id+"F0.wireOp",EDGE,"E23.33.9"),sQuery(id+"F0.wireOp",EDGE,"E23.33.10"),sQuery(id+"F0.wireOp",EDGE,"E23.33.11"),sQuery(id+"F0.wireOp",EDGE,"E23.34.0"),sQuery(id+"F0.wireOp",EDGE,"E23.34.1"),sQuery(id+"F0.wireOp",EDGE,"E23.34.2"),sQuery(id+"F0.wireOp",EDGE,"E23.34.3"),sQuery(id+"F0.wireOp",EDGE,"E23.34.4"),sQuery(id+"F0.wireOp",EDGE,"E23.34.5"),sQuery(id+"F0.wireOp",EDGE,"E23.34.6"),sQuery(id+"F0.wireOp",EDGE,"E23.34.7"),sQuery(id+"F0.wireOp",EDGE,"E23.34.8"),sQuery(id+"F0.wireOp",EDGE,"E23.34.9"),sQuery(id+"F0.wireOp",EDGE,"E23.34.10"),sQuery(id+"F0.wireOp",EDGE,"E23.34.11"),sQuery(id+"F0.wireOp",EDGE,"E23.35.0"),sQuery(id+"F0.wireOp",EDGE,"E23.35.1"),sQuery(id+"F0.wireOp",EDGE,"E23.35.2"),sQuery(id+"F0.wireOp",EDGE,"E23.35.3"),sQuery(id+"F0.wireOp",EDGE,"E23.35.4"),sQuery(id+"F0.wireOp",EDGE,"E23.35.5"),sQuery(id+"F0.wireOp",EDGE,"E23.35.6"),sQuery(id+"F0.wireOp",EDGE,"E23.35.7"),sQuery(id+"F0.wireOp",EDGE,"E23.35.8"),sQuery(id+"F0.wireOp",EDGE,"E23.35.9"),sQuery(id+"F0.wireOp",EDGE,"E23.35.10"),sQuery(id+"F0.wireOp",EDGE,"E23.35.11"),sQuery(id+"F0.wireOp",EDGE,"E23.36.0"),sQuery(id+"F0.wireOp",EDGE,"E23.36.1"),sQuery(id+"F0.wireOp",EDGE,"E23.36.2"),sQuery(id+"F0.wireOp",EDGE,"E23.36.3"),sQuery(id+"F0.wireOp",EDGE,"E23.36.4"),sQuery(id+"F0.wireOp",EDGE,"E23.36.5"),sQuery(id+"F0.wireOp",EDGE,"E23.36.6"),sQuery(id+"F0.wireOp",EDGE,"E23.36.7"),sQuery(id+"F0.wireOp",EDGE,"E23.36.8"),sQuery(id+"F0.wireOp",EDGE,"E23.36.9"),sQuery(id+"F0.wireOp",EDGE,"E23.36.10"),sQuery(id+"F0.wireOp",EDGE,"E23.36.11"),sQuery(id+"F0.wireOp",EDGE,"E23.37.0"),sQuery(id+"F0.wireOp",EDGE,"E23.37.1"),sQuery(id+"F0.wireOp",EDGE,"E23.37.2"),sQuery(id+"F0.wireOp",EDGE,"E23.37.3"),sQuery(id+"F0.wireOp",EDGE,"E23.37.4"),sQuery(id+"F0.wireOp",EDGE,"E23.37.5"),sQuery(id+"F0.wireOp",EDGE,"E23.37.6"),sQuery(id+"F0.wireOp",EDGE,"E23.37.7"),sQuery(id+"F0.wireOp",EDGE,"E23.37.8"),sQuery(id+"F0.wireOp",EDGE,"E23.37.9"),sQuery(id+"F0.wireOp",EDGE,"E23.37.10"),sQuery(id+"F0.wireOp",EDGE,"E23.37.11"),sQuery(id+"F0.wireOp",EDGE,"E23.38.0"),sQuery(id+"F0.wireOp",EDGE,"E23.38.1"),sQuery(id+"F0.wireOp",EDGE,"E23.38.2"),sQuery(id+"F0.wireOp",EDGE,"E23.38.3"),sQuery(id+"F0.wireOp",EDGE,"E23.38.4"),sQuery(id+"F0.wireOp",EDGE,"E23.38.5"),sQuery(id+"F0.wireOp",EDGE,"E23.38.6"),sQuery(id+"F0.wireOp",EDGE,"E23.38.7"),sQuery(id+"F0.wireOp",EDGE,"E23.38.8"),sQuery(id+"F0.wireOp",EDGE,"E23.38.9"),sQuery(id+"F0.wireOp",EDGE,"E23.38.10"),sQuery(id+"F0.wireOp",EDGE,"E23.38.11"),sQuery(id+"F0.wireOp",EDGE,"E23.39.0"),sQuery(id+"F0.wireOp",EDGE,"E23.39.1"),sQuery(id+"F0.wireOp",EDGE,"E23.39.2"),sQuery(id+"F0.wireOp",EDGE,"E23.39.3"),sQuery(id+"F0.wireOp",EDGE,"E23.39.4"),sQuery(id+"F0.wireOp",EDGE,"E23.39.5"),sQuery(id+"F0.wireOp",EDGE,"E23.39.6"),sQuery(id+"F0.wireOp",EDGE,"E23.39.7"),sQuery(id+"F0.wireOp",EDGE,"E23.39.8"),sQuery(id+"F0.wireOp",EDGE,"E23.39.9"),sQuery(id+"F0.wireOp",EDGE,"E23.39.10"),sQuery(id+"F0.wireOp",EDGE,"E23.39.11"),sQuery(id+"F0.wireOp",EDGE,"E23.40.0"),sQuery(id+"F0.wireOp",EDGE,"E23.40.1"),sQuery(id+"F0.wireOp",EDGE,"E23.40.2"),sQuery(id+"F0.wireOp",EDGE,"E23.40.3"),sQuery(id+"F0.wireOp",EDGE,"E23.40.4"),sQuery(id+"F0.wireOp",EDGE,"E23.40.5"),sQuery(id+"F0.wireOp",EDGE,"E23.40.6"),sQuery(id+"F0.wireOp",EDGE,"E23.40.7"),sQuery(id+"F0.wireOp",EDGE,"E23.40.8"),sQuery(id+"F0.wireOp",EDGE,"E23.40.9"),sQuery(id+"F0.wireOp",EDGE,"E23.40.10"),sQuery(id+"F0.wireOp",EDGE,"E23.40.11"),sQuery(id+"F0.wireOp",EDGE,"E23.41.0"),sQuery(id+"F0.wireOp",EDGE,"E23.41.1"),sQuery(id+"F0.wireOp",EDGE,"E23.41.2"),sQuery(id+"F0.wireOp",EDGE,"E23.41.3"),sQuery(id+"F0.wireOp",EDGE,"E23.41.4"),sQuery(id+"F0.wireOp",EDGE,"E23.41.5"),sQuery(id+"F0.wireOp",EDGE,"E23.41.6"),sQuery(id+"F0.wireOp",EDGE,"E23.41.7"),sQuery(id+"F0.wireOp",EDGE,"E23.41.8"),sQuery(id+"F0.wireOp",EDGE,"E23.41.9"),sQuery(id+"F0.wireOp",EDGE,"E23.41.10"),sQuery(id+"F0.wireOp",EDGE,"E23.41.11"),sQuery(id+"F0.wireOp",EDGE,"E23.42.0"),sQuery(id+"F0.wireOp",EDGE,"E23.42.1"),sQuery(id+"F0.wireOp",EDGE,"E23.42.2"),sQuery(id+"F0.wireOp",EDGE,"E23.42.3"),sQuery(id+"F0.wireOp",EDGE,"E23.42.4"),sQuery(id+"F0.wireOp",EDGE,"E23.42.5"),sQuery(id+"F0.wireOp",EDGE,"E23.42.6"),sQuery(id+"F0.wireOp",EDGE,"E23.42.7"),sQuery(id+"F0.wireOp",EDGE,"E23.42.8"),sQuery(id+"F0.wireOp",EDGE,"E23.42.9"),sQuery(id+"F0.wireOp",EDGE,"E23.42.10"),sQuery(id+"F0.wireOp",EDGE,"E23.42.11"),sQuery(id+"F0.wireOp",EDGE,"E23.43.0"),sQuery(id+"F0.wireOp",EDGE,"E23.43.1"),sQuery(id+"F0.wireOp",EDGE,"E23.43.2"),sQuery(id+"F0.wireOp",EDGE,"E23.43.3"),sQuery(id+"F0.wireOp",EDGE,"E23.43.4"),sQuery(id+"F0.wireOp",EDGE,"E23.43.5"),sQuery(id+"F0.wireOp",EDGE,"E23.43.6"),sQuery(id+"F0.wireOp",EDGE,"E23.43.7"),sQuery(id+"F0.wireOp",EDGE,"E23.43.8"),sQuery(id+"F0.wireOp",EDGE,"E23.43.9"),sQuery(id+"F0.wireOp",EDGE,"E23.43.10"),sQuery(id+"F0.wireOp",EDGE,"E23.43.11"),sQuery(id+"F0.wireOp",EDGE,"E23.44.0"),sQuery(id+"F0.wireOp",EDGE,"E23.44.1"),sQuery(id+"F0.wireOp",EDGE,"E23.44.2"),sQuery(id+"F0.wireOp",EDGE,"E23.44.3"),sQuery(id+"F0.wireOp",EDGE,"E23.44.4"),sQuery(id+"F0.wireOp",EDGE,"E23.44.5"),sQuery(id+"F0.wireOp",EDGE,"E23.44.6"),sQuery(id+"F0.wireOp",EDGE,"E23.44.7"),sQuery(id+"F0.wireOp",EDGE,"E23.44.8"),sQuery(id+"F0.wireOp",EDGE,"E23.44.9"),sQuery(id+"F0.wireOp",EDGE,"E23.44.10"),sQuery(id+"F0.wireOp",EDGE,"E23.44.11"),sQuery(id+"F0.wireOp",EDGE,"E23.45.0"),sQuery(id+"F0.wireOp",EDGE,"E23.45.1"),sQuery(id+"F0.wireOp",EDGE,"E23.45.2"),sQuery(id+"F0.wireOp",EDGE,"E23.45.3"),sQuery(id+"F0.wireOp",EDGE,"E23.45.4"),sQuery(id+"F0.wireOp",EDGE,"E23.45.5"),sQuery(id+"F0.wireOp",EDGE,"E23.45.6"),sQuery(id+"F0.wireOp",EDGE,"E23.45.7"),sQuery(id+"F0.wireOp",EDGE,"E23.45.8"),sQuery(id+"F0.wireOp",EDGE,"E23.45.9"),sQuery(id+"F0.wireOp",EDGE,"E23.45.10"),sQuery(id+"F0.wireOp",EDGE,"E23.45.11"),sQuery(id+"F0.wireOp",EDGE,"E23.46.0"),sQuery(id+"F0.wireOp",EDGE,"E23.46.1"),sQuery(id+"F0.wireOp",EDGE,"E23.46.2"),sQuery(id+"F0.wireOp",EDGE,"E23.46.3"),sQuery(id+"F0.wireOp",EDGE,"E23.46.4"),sQuery(id+"F0.wireOp",EDGE,"E23.46.5"),sQuery(id+"F0.wireOp",EDGE,"E23.46.6"),sQuery(id+"F0.wireOp",EDGE,"E23.46.7"),sQuery(id+"F0.wireOp",EDGE,"E23.46.8"),sQuery(id+"F0.wireOp",EDGE,"E23.46.9"),sQuery(id+"F0.wireOp",EDGE,"E23.46.10"),sQuery(id+"F0.wireOp",EDGE,"E23.46.11"),sQuery(id+"F0.wireOp",EDGE,"E23.47.0"),sQuery(id+"F0.wireOp",EDGE,"E23.47.1"),sQuery(id+"F0.wireOp",EDGE,"E23.47.2"),sQuery(id+"F0.wireOp",EDGE,"E23.47.3"),sQuery(id+"F0.wireOp",EDGE,"E23.47.4"),sQuery(id+"F0.wireOp",EDGE,"E23.47.5"),sQuery(id+"F0.wireOp",EDGE,"E23.47.6"),sQuery(id+"F0.wireOp",EDGE,"E23.47.7"),sQuery(id+"F0.wireOp",EDGE,"E23.47.8"),sQuery(id+"F0.wireOp",EDGE,"E23.47.9"),sQuery(id+"F0.wireOp",EDGE,"E23.47.10"),sQuery(id+"F0.wireOp",EDGE,"E23.47.11"),sQuery(id+"F0.wireOp",EDGE,"E23.48.0"),sQuery(id+"F0.wireOp",EDGE,"E23.48.1"),sQuery(id+"F0.wireOp",EDGE,"E23.48.2"),sQuery(id+"F0.wireOp",EDGE,"E23.48.3"),sQuery(id+"F0.wireOp",EDGE,"E23.48.4"),sQuery(id+"F0.wireOp",EDGE,"E23.48.5"),sQuery(id+"F0.wireOp",EDGE,"E23.48.6"),sQuery(id+"F0.wireOp",EDGE,"E23.48.7"),sQuery(id+"F0.wireOp",EDGE,"E23.48.8"),sQuery(id+"F0.wireOp",EDGE,"E23.48.9"),sQuery(id+"F0.wireOp",EDGE,"E23.48.10"),sQuery(id+"F0.wireOp",EDGE,"E23.48.11"),sQuery(id+"F0.wireOp",EDGE,"E23.49.0"),sQuery(id+"F0.wireOp",EDGE,"E23.49.1"),sQuery(id+"F0.wireOp",EDGE,"E23.49.2"),sQuery(id+"F0.wireOp",EDGE,"E23.49.3"),sQuery(id+"F0.wireOp",EDGE,"E23.49.4"),sQuery(id+"F0.wireOp",EDGE,"E23.49.5"),sQuery(id+"F0.wireOp",EDGE,"E23.49.6"),sQuery(id+"F0.wireOp",EDGE,"E23.49.7"),sQuery(id+"F0.wireOp",EDGE,"E23.49.8"),sQuery(id+"F0.wireOp",EDGE,"E23.49.9"),sQuery(id+"F0.wireOp",EDGE,"E23.49.10"),sQuery(id+"F0.wireOp",EDGE,"E23.49.11"),sQuery(id+"F0.wireOp",EDGE,"E23.50.0"),sQuery(id+"F0.wireOp",EDGE,"E23.50.1"),sQuery(id+"F0.wireOp",EDGE,"E23.50.2"),sQuery(id+"F0.wireOp",EDGE,"E23.50.3"),sQuery(id+"F0.wireOp",EDGE,"E23.50.4"),sQuery(id+"F0.wireOp",EDGE,"E23.50.5"),sQuery(id+"F0.wireOp",EDGE,"E23.50.6"),sQuery(id+"F0.wireOp",EDGE,"E23.50.7"),sQuery(id+"F0.wireOp",EDGE,"E23.50.8"),sQuery(id+"F0.wireOp",EDGE,"E23.50.9"),sQuery(id+"F0.wireOp",EDGE,"E23.50.10"),sQuery(id+"F0.wireOp",EDGE,"E23.50.11"),sQuery(id+"F0.wireOp",EDGE,"E23.51.0"),sQuery(id+"F0.wireOp",EDGE,"E23.51.1"),sQuery(id+"F0.wireOp",EDGE,"E23.51.2"),sQuery(id+"F0.wireOp",EDGE,"E23.51.3"),sQuery(id+"F0.wireOp",EDGE,"E23.51.4"),sQuery(id+"F0.wireOp",EDGE,"E23.51.5"),sQuery(id+"F0.wireOp",EDGE,"E23.51.6"),sQuery(id+"F0.wireOp",EDGE,"E23.51.7"),sQuery(id+"F0.wireOp",EDGE,"E23.51.8"),sQuery(id+"F0.wireOp",EDGE,"E23.51.9"),sQuery(id+"F0.wireOp",EDGE,"E23.51.10"),sQuery(id+"F0.wireOp",EDGE,"E23.51.11"),sQuery(id+"F0.wireOp",EDGE,"E23.52.0"),sQuery(id+"F0.wireOp",EDGE,"E23.52.1"),sQuery(id+"F0.wireOp",EDGE,"E23.52.2"),sQuery(id+"F0.wireOp",EDGE,"E23.52.3"),sQuery(id+"F0.wireOp",EDGE,"E23.52.4"),sQuery(id+"F0.wireOp",EDGE,"E23.52.5"),sQuery(id+"F0.wireOp",EDGE,"E23.52.6"),sQuery(id+"F0.wireOp",EDGE,"E23.52.7"),sQuery(id+"F0.wireOp",EDGE,"E23.52.8"),sQuery(id+"F0.wireOp",EDGE,"E23.52.9"),sQuery(id+"F0.wireOp",EDGE,"E23.52.10"),sQuery(id+"F0.wireOp",EDGE,"E23.52.11"),sQuery(id+"F0.wireOp",EDGE,"E23.53.0"),sQuery(id+"F0.wireOp",EDGE,"E23.53.1"),sQuery(id+"F0.wireOp",EDGE,"E23.53.2"),sQuery(id+"F0.wireOp",EDGE,"E23.53.3"),sQuery(id+"F0.wireOp",EDGE,"E23.53.4"),sQuery(id+"F0.wireOp",EDGE,"E23.53.5"),sQuery(id+"F0.wireOp",EDGE,"E23.53.6"),sQuery(id+"F0.wireOp",EDGE,"E23.53.7"),sQuery(id+"F0.wireOp",EDGE,"E23.53.8"),sQuery(id+"F0.wireOp",EDGE,"E23.53.9"),sQuery(id+"F0.wireOp",EDGE,"E23.53.10"),sQuery(id+"F0.wireOp",EDGE,"E23.53.11"),sQuery(id+"F0.wireOp",EDGE,"E23.54.0"),sQuery(id+"F0.wireOp",EDGE,"E23.54.1"),sQuery(id+"F0.wireOp",EDGE,"E23.54.2"),sQuery(id+"F0.wireOp",EDGE,"E23.54.3"),sQuery(id+"F0.wireOp",EDGE,"E23.54.4"),sQuery(id+"F0.wireOp",EDGE,"E23.54.5"),sQuery(id+"F0.wireOp",EDGE,"E23.54.6"),sQuery(id+"F0.wireOp",EDGE,"E23.54.7"),sQuery(id+"F0.wireOp",EDGE,"E23.54.8"),sQuery(id+"F0.wireOp",EDGE,"E23.54.9"),sQuery(id+"F0.wireOp",EDGE,"E23.54.10"),sQuery(id+"F0.wireOp",EDGE,"E23.54.11"),sQuery(id+"F0.wireOp",EDGE,"E23.55.0"),sQuery(id+"F0.wireOp",EDGE,"E23.55.1"),sQuery(id+"F0.wireOp",EDGE,"E23.55.2"),sQuery(id+"F0.wireOp",EDGE,"E23.55.3"),sQuery(id+"F0.wireOp",EDGE,"E23.55.4"),sQuery(id+"F0.wireOp",EDGE,"E23.55.5"),sQuery(id+"F0.wireOp",EDGE,"E23.55.6"),sQuery(id+"F0.wireOp",EDGE,"E23.55.7"),sQuery(id+"F0.wireOp",EDGE,"E23.55.8"),sQuery(id+"F0.wireOp",EDGE,"E23.55.9"),sQuery(id+"F0.wireOp",EDGE,"E23.55.10"),sQuery(id+"F0.wireOp",EDGE,"E23.55.11"),sQuery(id+"F0.wireOp",EDGE,"E23.56.0"),sQuery(id+"F0.wireOp",EDGE,"E23.56.1"),sQuery(id+"F0.wireOp",EDGE,"E23.56.2"),sQuery(id+"F0.wireOp",EDGE,"E23.56.3"),sQuery(id+"F0.wireOp",EDGE,"E23.56.4"),sQuery(id+"F0.wireOp",EDGE,"E23.56.5"),sQuery(id+"F0.wireOp",EDGE,"E23.56.6"),sQuery(id+"F0.wireOp",EDGE,"E23.56.7"),sQuery(id+"F0.wireOp",EDGE,"E23.56.8"),sQuery(id+"F0.wireOp",EDGE,"E23.56.9"),sQuery(id+"F0.wireOp",EDGE,"E23.56.10"),sQuery(id+"F0.wireOp",EDGE,"E23.56.11"),sQuery(id+"F0.wireOp",EDGE,"E23.57.0"),sQuery(id+"F0.wireOp",EDGE,"E23.57.1"),sQuery(id+"F0.wireOp",EDGE,"E23.57.2"),sQuery(id+"F0.wireOp",EDGE,"E23.57.3"),sQuery(id+"F0.wireOp",EDGE,"E23.57.4"),sQuery(id+"F0.wireOp",EDGE,"E23.57.5"),sQuery(id+"F0.wireOp",EDGE,"E23.57.6"),sQuery(id+"F0.wireOp",EDGE,"E23.57.7"),sQuery(id+"F0.wireOp",EDGE,"E23.57.8"),sQuery(id+"F0.wireOp",EDGE,"E23.57.9"),sQuery(id+"F0.wireOp",EDGE,"E23.57.10"),sQuery(id+"F0.wireOp",EDGE,"E23.57.11"),sQuery(id+"F0.wireOp",EDGE,"E23.58.0"),sQuery(id+"F0.wireOp",EDGE,"E23.58.1"),sQuery(id+"F0.wireOp",EDGE,"E23.58.2"),sQuery(id+"F0.wireOp",EDGE,"E23.58.3"),sQuery(id+"F0.wireOp",EDGE,"E23.58.4"),sQuery(id+"F0.wireOp",EDGE,"E23.58.5"),sQuery(id+"F0.wireOp",EDGE,"E23.58.6"),sQuery(id+"F0.wireOp",EDGE,"E23.58.7"),sQuery(id+"F0.wireOp",EDGE,"E23.58.8"),sQuery(id+"F0.wireOp",EDGE,"E23.58.9"),sQuery(id+"F0.wireOp",EDGE,"E23.58.10"),sQuery(id+"F0.wireOp",EDGE,"E23.58.11"),sQuery(id+"F0.wireOp",EDGE,"E23.59.0"),sQuery(id+"F0.wireOp",EDGE,"E23.59.1"),sQuery(id+"F0.wireOp",EDGE,"E23.59.2"),sQuery(id+"F0.wireOp",EDGE,"E23.59.3"),sQuery(id+"F0.wireOp",EDGE,"E23.59.4"),sQuery(id+"F0.wireOp",EDGE,"E23.59.5"),sQuery(id+"F0.wireOp",EDGE,"E23.59.6"),sQuery(id+"F0.wireOp",EDGE,"E23.59.7"),sQuery(id+"F0.wireOp",EDGE,"E23.59.8"),sQuery(id+"F0.wireOp",EDGE,"E23.59.9"),sQuery(id+"F0.wireOp",EDGE,"E23.59.10"),sQuery(id+"F0.wireOp",EDGE,"E23.59.11"),sQuery(id+"F0.wireOp",EDGE,"E23.60.0"),sQuery(id+"F0.wireOp",EDGE,"E23.60.1"),sQuery(id+"F0.wireOp",EDGE,"E23.60.2"),sQuery(id+"F0.wireOp",EDGE,"E23.60.3"),sQuery(id+"F0.wireOp",EDGE,"E23.60.4"),sQuery(id+"F0.wireOp",EDGE,"E23.60.5"),sQuery(id+"F0.wireOp",EDGE,"E23.60.6"),sQuery(id+"F0.wireOp",EDGE,"E23.60.7"),sQuery(id+"F0.wireOp",EDGE,"E23.60.8"),sQuery(id+"F0.wireOp",EDGE,"E23.60.9"),sQuery(id+"F0.wireOp",EDGE,"E23.60.10"),sQuery(id+"F0.wireOp",EDGE,"E23.60.11"),sQuery(id+"F0.wireOp",EDGE,"E23.61.0"),sQuery(id+"F0.wireOp",EDGE,"E23.61.1"),sQuery(id+"F0.wireOp",EDGE,"E23.61.2"),sQuery(id+"F0.wireOp",EDGE,"E23.61.3"),sQuery(id+"F0.wireOp",EDGE,"E23.61.4"),sQuery(id+"F0.wireOp",EDGE,"E23.61.5"),sQuery(id+"F0.wireOp",EDGE,"E23.61.6"),sQuery(id+"F0.wireOp",EDGE,"E23.61.7"),sQuery(id+"F0.wireOp",EDGE,"E23.61.8"),sQuery(id+"F0.wireOp",EDGE,"E23.61.9"),sQuery(id+"F0.wireOp",EDGE,"E23.61.10"),sQuery(id+"F0.wireOp",EDGE,"E23.61.11"),sQuery(id+"F0.wireOp",EDGE,"E23.62.0"),sQuery(id+"F0.wireOp",EDGE,"E23.62.1"),sQuery(id+"F0.wireOp",EDGE,"E23.62.2"),sQuery(id+"F0.wireOp",EDGE,"E23.62.3"),sQuery(id+"F0.wireOp",EDGE,"E23.62.4"),sQuery(id+"F0.wireOp",EDGE,"E23.62.5"),sQuery(id+"F0.wireOp",EDGE,"E23.62.6"),sQuery(id+"F0.wireOp",EDGE,"E23.62.7"),sQuery(id+"F0.wireOp",EDGE,"E23.62.8"),sQuery(id+"F0.wireOp",EDGE,"E23.62.9"),sQuery(id+"F0.wireOp",EDGE,"E23.62.10"),sQuery(id+"F0.wireOp",EDGE,"E23.62.11"),sQuery(id+"F0.wireOp",EDGE,"E23.63.0"),sQuery(id+"F0.wireOp",EDGE,"E23.63.1"),sQuery(id+"F0.wireOp",EDGE,"E23.63.2"),sQuery(id+"F0.wireOp",EDGE,"E23.63.3"),sQuery(id+"F0.wireOp",EDGE,"E23.63.4"),sQuery(id+"F0.wireOp",EDGE,"E23.63.5"),sQuery(id+"F0.wireOp",EDGE,"E23.63.6"),sQuery(id+"F0.wireOp",EDGE,"E23.63.7"),sQuery(id+"F0.wireOp",EDGE,"E23.63.8"),sQuery(id+"F0.wireOp",EDGE,"E23.63.9"),sQuery(id+"F0.wireOp",EDGE,"E23.63.10"),sQuery(id+"F0.wireOp",EDGE,"E23.63.11"),sQuery(id+"F0.wireOp",EDGE,"E23.64.0"),sQuery(id+"F0.wireOp",EDGE,"E23.64.1"),sQuery(id+"F0.wireOp",EDGE,"E23.64.2"),sQuery(id+"F0.wireOp",EDGE,"E23.64.3"),sQuery(id+"F0.wireOp",EDGE,"E23.64.4"),sQuery(id+"F0.wireOp",EDGE,"E23.64.5"),sQuery(id+"F0.wireOp",EDGE,"E23.64.6"),sQuery(id+"F0.wireOp",EDGE,"E23.64.7"),sQuery(id+"F0.wireOp",EDGE,"E23.64.8"),sQuery(id+"F0.wireOp",EDGE,"E23.64.9"),sQuery(id+"F0.wireOp",EDGE,"E23.64.10"),sQuery(id+"F0.wireOp",EDGE,"E23.64.11"),sQuery(id+"F0.wireOp",EDGE,"E23.65.0"),sQuery(id+"F0.wireOp",EDGE,"E23.65.1"),sQuery(id+"F0.wireOp",EDGE,"E23.65.2"),sQuery(id+"F0.wireOp",EDGE,"E23.65.3"),sQuery(id+"F0.wireOp",EDGE,"E23.65.4"),sQuery(id+"F0.wireOp",EDGE,"E23.65.5"),sQuery(id+"F0.wireOp",EDGE,"E23.65.6"),sQuery(id+"F0.wireOp",EDGE,"E23.65.7"),sQuery(id+"F0.wireOp",EDGE,"E23.65.8"),sQuery(id+"F0.wireOp",EDGE,"E23.65.9"),sQuery(id+"F0.wireOp",EDGE,"E23.65.10"),sQuery(id+"F0.wireOp",EDGE,"E23.65.11"),sQuery(id+"F0.wireOp",EDGE,"E23.66.0"),sQuery(id+"F0.wireOp",EDGE,"E23.66.1"),sQuery(id+"F0.wireOp",EDGE,"E23.66.2"),sQuery(id+"F0.wireOp",EDGE,"E23.66.3"),sQuery(id+"F0.wireOp",EDGE,"E23.66.4"),sQuery(id+"F0.wireOp",EDGE,"E23.66.5"),sQuery(id+"F0.wireOp",EDGE,"E23.66.6"),sQuery(id+"F0.wireOp",EDGE,"E23.66.7"),sQuery(id+"F0.wireOp",EDGE,"E23.66.8"),sQuery(id+"F0.wireOp",EDGE,"E23.66.9"),sQuery(id+"F0.wireOp",EDGE,"E23.66.10"),sQuery(id+"F0.wireOp",EDGE,"E23.66.11"),sQuery(id+"F0.wireOp",EDGE,"E23.67.0"),sQuery(id+"F0.wireOp",EDGE,"E23.67.1"),sQuery(id+"F0.wireOp",EDGE,"E23.67.2"),sQuery(id+"F0.wireOp",EDGE,"E23.67.3"),sQuery(id+"F0.wireOp",EDGE,"E23.67.4"),sQuery(id+"F0.wireOp",EDGE,"E23.67.5"),sQuery(id+"F0.wireOp",EDGE,"E23.67.6"),sQuery(id+"F0.wireOp",EDGE,"E23.67.7"),sQuery(id+"F0.wireOp",EDGE,"E23.67.8"),sQuery(id+"F0.wireOp",EDGE,"E23.67.9"),sQuery(id+"F0.wireOp",EDGE,"E23.67.10"),sQuery(id+"F0.wireOp",EDGE,"E23.67.11"),sQuery(id+"F0.wireOp",EDGE,"E23.68.0"),sQuery(id+"F0.wireOp",EDGE,"E23.68.1"),sQuery(id+"F0.wireOp",EDGE,"E23.68.2"),sQuery(id+"F0.wireOp",EDGE,"E23.68.3"),sQuery(id+"F0.wireOp",EDGE,"E23.68.4"),sQuery(id+"F0.wireOp",EDGE,"E23.68.5"),sQuery(id+"F0.wireOp",EDGE,"E23.68.6"),sQuery(id+"F0.wireOp",EDGE,"E23.68.7"),sQuery(id+"F0.wireOp",EDGE,"E23.68.8"),sQuery(id+"F0.wireOp",EDGE,"E23.68.9"),sQuery(id+"F0.wireOp",EDGE,"E23.68.10"),sQuery(id+"F0.wireOp",EDGE,"E23.68.11"),sQuery(id+"F0.wireOp",EDGE,"E23.69.0"),sQuery(id+"F0.wireOp",EDGE,"E23.69.1"),sQuery(id+"F0.wireOp",EDGE,"E23.69.2"),sQuery(id+"F0.wireOp",EDGE,"E23.69.3"),sQuery(id+"F0.wireOp",EDGE,"E23.69.4"),sQuery(id+"F0.wireOp",EDGE,"E23.69.5"),sQuery(id+"F0.wireOp",EDGE,"E23.69.6"),sQuery(id+"F0.wireOp",EDGE,"E23.69.7"),sQuery(id+"F0.wireOp",EDGE,"E23.69.8"),sQuery(id+"F0.wireOp",EDGE,"E23.69.9"),sQuery(id+"F0.wireOp",EDGE,"E23.69.10"),sQuery(id+"F0.wireOp",EDGE,"E23.69.11"),sQuery(id+"F0.wireOp",EDGE,"E23.70.0"),sQuery(id+"F0.wireOp",EDGE,"E23.70.1"),sQuery(id+"F0.wireOp",EDGE,"E23.70.2"),sQuery(id+"F0.wireOp",EDGE,"E23.70.3"),sQuery(id+"F0.wireOp",EDGE,"E23.70.4"),sQuery(id+"F0.wireOp",EDGE,"E23.70.5"),sQuery(id+"F0.wireOp",EDGE,"E23.70.6"),sQuery(id+"F0.wireOp",EDGE,"E23.70.7"),sQuery(id+"F0.wireOp",EDGE,"E23.70.8"),sQuery(id+"F0.wireOp",EDGE,"E23.70.9"),sQuery(id+"F0.wireOp",EDGE,"E23.70.10"),sQuery(id+"F0.wireOp",EDGE,"E23.70.11"),sQuery(id+"F0.wireOp",EDGE,"E23.71.0"),sQuery(id+"F0.wireOp",EDGE,"E23.71.1"),sQuery(id+"F0.wireOp",EDGE,"E23.71.2"),sQuery(id+"F0.wireOp",EDGE,"E23.71.3"),sQuery(id+"F0.wireOp",EDGE,"E23.71.4"),sQuery(id+"F0.wireOp",EDGE,"E23.71.5"),sQuery(id+"F0.wireOp",EDGE,"E23.71.6"),sQuery(id+"F0.wireOp",EDGE,"E23.71.7"),sQuery(id+"F0.wireOp",EDGE,"E23.71.8"),sQuery(id+"F0.wireOp",EDGE,"E23.71.9"),sQuery(id+"F0.wireOp",EDGE,"E23.71.10"),sQuery(id+"F0.wireOp",EDGE,"E23.71.11"),sQuery(id+"F0.wireOp",EDGE,"E24.trimOffspring"),sQuery(id+"F0.wireOp",EDGE,"E25.trimOffspring"),sQuery(id+"F0.wireOp",EDGE,"E26.trimOffspring"),sQuery(id+"F0.wireOp",EDGE,"E27.trimOffspring"),sQuery(id+"F0.wireOp",EDGE,"E28.trimOffspring"),sQuery(id+"F0.wireOp",EDGE,"E29.trimOffspring"),sQuery(id+"F0.wireOp",EDGE,"E30.trimOffspring"),sQuery(id+"F0.wireOp",EDGE,"E31.trimOffspring"),sQuery(id+"F0.wireOp",EDGE,"E32.trimOffspring"),sQuery(id+"F0.wireOp",EDGE,"E33.trimOffspring"),sQuery(id+"F0.wireOp",EDGE,"E34.trimOffspring"),sQuery(id+"F0.wireOp",EDGE,"E35.trimOffspring"),sQuery(id+"F0.wireOp",EDGE,"E36.trimOffspring"),sQuery(id+"F0.wireOp",EDGE,"E37.trimOffspring"),sQuery(id+"F0.wireOp",EDGE,"E38.trimOffspring"),sQuery(id+"F0.wireOp",EDGE,"E39.trimOffspring"),sQuery(id+"F0.wireOp",EDGE,"E40.trimOffspring"),sQuery(id+"F0.wireOp",EDGE,"E41.trimOffspring"),sQuery(id+"F0.wireOp",EDGE,"E42.trimOffspring"),sQuery(id+"F0.wireOp",EDGE,"E43.trimOffspring"),sQuery(id+"F0.wireOp",EDGE,"E44.trimOffspring"),sQuery(id+"F0.wireOp",EDGE,"E45.trimOffspring"),sQuery(id+"F0.wireOp",EDGE,"E46.trimOffspring"),sQuery(id+"F0.wireOp",EDGE,"E47.trimOffspring"),sQuery(id+"F0.wireOp",EDGE,"E48.trimOffspring"),sQuery(id+"F0.wireOp",EDGE,"E49.trimOffspring"),sQuery(id+"F0.wireOp",EDGE,"E50.trimOffspring"),sQuery(id+"F0.wireOp",EDGE,"E51.trimOffspring"),sQuery(id+"F0.wireOp",EDGE,"E52.trimOffspring"),sQuery(id+"F0.wireOp",EDGE,"E53.trimOffspring"),sQuery(id+"F0.wireOp",EDGE,"E54.trimOffspring"),sQuery(id+"F0.wireOp",EDGE,"E55.trimOffspring"),sQuery(id+"F0.wireOp",EDGE,"E56.trimOffspring"),sQuery(id+"F0.wireOp",EDGE,"E57.trimOffspring"),sQuery(id+"F0.wireOp",EDGE,"E58.trimOffspring"),sQuery(id+"F0.wireOp",EDGE,"E59.trimOffspring"),sQuery(id+"F0.wireOp",EDGE,"E60.trimOffspring"),sQuery(id+"F0.wireOp",EDGE,"E61.trimOffspring"),sQuery(id+"F0.wireOp",EDGE,"E62.trimOffspring"),sQuery(id+"F0.wireOp",EDGE,"E63.trimOffspring"),sQuery(id+"F0.wireOp",EDGE,"E64.trimOffspring"),sQuery(id+"F0.wireOp",EDGE,"E65.trimOffspring"),sQuery(id+"F0.wireOp",EDGE,"E66.trimOffspring"),sQuery(id+"F0.wireOp",EDGE,"E67.trimOffspring"),sQuery(id+"F0.wireOp",EDGE,"E68.trimOffspring"),sQuery(id+"F0.wireOp",EDGE,"E69.trimOffspring"),sQuery(id+"F0.wireOp",EDGE,"E70.trimOffspring"),sQuery(id+"F0.wireOp",EDGE,"E71.trimOffspring"),sQuery(id+"F0.wireOp",EDGE,"E72.trimOffspring"),sQuery(id+"F0.wireOp",EDGE,"E73.trimOffspring"),sQuery(id+"F0.wireOp",EDGE,"E74.trimOffspring"),sQuery(id+"F0.wireOp",EDGE,"E75.trimOffspring"),sQuery(id+"F0.wireOp",EDGE,"E76.trimOffspring"),sQuery(id+"F0.wireOp",EDGE,"E77.trimOffspring"),sQuery(id+"F0.wireOp",EDGE,"E78.trimOffspring"),sQuery(id+"F0.wireOp",EDGE,"E79.trimOffspring"),sQuery(id+"F0.wireOp",EDGE,"E80.trimOffspring"),sQuery(id+"F0.wireOp",EDGE,"E81.trimOffspring"),sQuery(id+"F0.wireOp",EDGE,"E82.trimOffspring"),sQuery(id+"F0.wireOp",EDGE,"E83.trimOffspring"),sQuery(id+"F0.wireOp",EDGE,"E84.trimOffspring"),sQuery(id+"F0.wireOp",EDGE,"E85.trimOffspring"),sQuery(id+"F0.wireOp",EDGE,"E86.trimOffspring"),sQuery(id+"F0.wireOp",EDGE,"E87.trimOffspring"),sQuery(id+"F0.wireOp",EDGE,"E88.trimOffspring"),sQuery(id+"F0.wireOp",EDGE,"E89.trimOffspring"),sQuery(id+"F0.wireOp",EDGE,"E90.trimOffspring"),sQuery(id+"F0.wireOp",EDGE,"E91.trimOffspring"),sQuery(id+"F0.wireOp",EDGE,"E92.trimOffspring"),sQuery(id+"F0.wireOp",EDGE,"E93.trimOffspring"),sQuery(id+"F0.wireOp",EDGE,"E94")])],"isStart":false});
            var sketch = newSketch(context, id + "F5", { "sketchPlane" : qUnion([Q0])});
            skCircle(sketch, "E97", {"center": v(0, 0) * mm, "radius": 3.18 * mm});
            skSolve(sketch);
        }
        {
            var Q0;
            Q0=qSketchRegion(id+"F5",true);
            extrude(context, id + "F6", {"entities" : qUnion([Q0]), "operationType" : NewBodyOperationType.ADD, "depth" : 5.08 * mm});
        }
        {
            var Q0;
            Q0=qCreatedBy(makeId("Front.planeOp"),FACE);
            var sketch = newSketch(context, id + "F7", { "sketchPlane" : qUnion([Q0])});
            skPoint(sketch, "E98.0", {"position": v(-25.4, 44) * mm});
            skPoint(sketch, "E99.0", {"position": v(50.8, 0) * mm});
            skPoint(sketch, "E100.0", {"position": v(-25.4, -44) * mm});
            skPoint(sketch, "E101.0", {"position": v(0, 0) * mm});
            skCircle(sketch, "E102.0", {"center": v(-25.4, 44) * mm, "radius": 3.18 * mm});
            skCircle(sketch, "E103.0", {"center": v(50.8, 0) * mm, "radius": 3.18 * mm});
            skCircle(sketch, "E104.0", {"center": v(-25.4, -44) * mm, "radius": 3.18 * mm});
            skCircle(sketch, "E105.0", {"center": v(0, 0) * mm, "radius": 89.1 * mm});
            skCircle(sketch, "E106.0", {"center": v(0, 0) * mm, "radius": 94.1 * mm});
            skCircle(sketch, "E107", {"center": v(0, 0) * mm, "radius": 53.98 * mm});
            skCircle(sketch, "E108", {"center": v(0, 0) * mm, "radius": 47.62 * mm});
            skCircle(sketch, "E109.0", {"center": v(0, 0) * mm, "radius": 3.18 * mm});
            skSolve(sketch);
        }
        {
            var Q0;
            Q0=qSketchRegion(id+"F7",true);
            var Q1;
            Q1=makeQuery(id+"F7.imprint","IMPRINT",FACE,{"disambiguationData":[TD([[makeQuery(id+"F7.imprint","IMPRINT",EDGE,{"derivedFrom":sQuery(id+"F7.wireOp",EDGE,"E105.0")}),1.0]])]});
            var Q2;
            {var subQ0=sQuery(id+"F7.wireOp",EDGE,"E108");var subQ1=makeQuery(id+"F7.imprint","INTERSECT",VERTEX,{"derivedFrom":[sQuery(id+"F7.wireOp",EDGE,"E102.0"),subQ0]});Q2=makeQuery(id+"F7.imprint","IMPRINT",FACE,{"disambiguationData":[TD([[makeQuery(id+"F7.imprint","IMPRINT",EDGE,{"disambiguationData":[TD([[subQ1,1.0]])],"derivedFrom":subQ0}),1.0]])]});}
            var Q3;
            {var subQ0=sQuery(id+"F7.wireOp",EDGE,"E107");var subQ1=sQuery(id+"F7.wireOp",EDGE,"E102.0");var subQ2=makeQuery(id+"F7.imprint","INTERSECT",VERTEX,{"derivedFrom":[subQ1,subQ0]});Q3=makeQuery(id+"F7.imprint","IMPRINT",FACE,{"disambiguationData":[TD([[makeQuery(id+"F7.imprint","IMPRINT",EDGE,{"disambiguationData":[TD([[subQ2,-1.0]])],"derivedFrom":subQ1}),-1.0]])]});}
            var Q4;
            {var subQ0=sQuery(id+"F7.wireOp",EDGE,"E107");var subQ1=sQuery(id+"F7.wireOp",EDGE,"E102.0");var subQ2=makeQuery(id+"F7.imprint","INTERSECT",VERTEX,{"derivedFrom":[subQ1,subQ0]});Q4=makeQuery(id+"F7.imprint","IMPRINT",FACE,{"disambiguationData":[TD([[makeQuery(id+"F7.imprint","IMPRINT",EDGE,{"disambiguationData":[TD([[subQ2,1.0]])],"derivedFrom":subQ1}),-1.0]])]});}
            var Q5;
            {var subQ0=sQuery(id+"F7.wireOp",EDGE,"E102.0");var subQ1=makeQuery(id+"F7.imprint","INTERSECT",VERTEX,{"derivedFrom":[subQ0,sQuery(id+"F7.wireOp",EDGE,"E107")]});Q5=makeQuery(id+"F7.imprint","IMPRINT",FACE,{"disambiguationData":[TD([[makeQuery(id+"F7.imprint","IMPRINT",EDGE,{"disambiguationData":[TD([[subQ1,1.0]])],"derivedFrom":subQ0}),1.0]])]});}
            var Q6;
            {var subQ0=sQuery(id+"F7.wireOp",EDGE,"E103.0");var subQ1=makeQuery(id+"F7.imprint","INTERSECT",VERTEX,{"derivedFrom":[subQ0,sQuery(id+"F7.wireOp",EDGE,"E107")]});Q6=makeQuery(id+"F7.imprint","IMPRINT",FACE,{"disambiguationData":[TD([[makeQuery(id+"F7.imprint","IMPRINT",EDGE,{"disambiguationData":[TD([[subQ1,-1.0]])],"derivedFrom":subQ0}),1.0]])]});}
            var Q7;
            {var subQ0=sQuery(id+"F7.wireOp",EDGE,"E107");var subQ1=sQuery(id+"F7.wireOp",EDGE,"E103.0");var subQ2=makeQuery(id+"F7.imprint","INTERSECT",VERTEX,{"derivedFrom":[subQ1,subQ0]});Q7=makeQuery(id+"F7.imprint","IMPRINT",FACE,{"disambiguationData":[TD([[makeQuery(id+"F7.imprint","IMPRINT",EDGE,{"disambiguationData":[TD([[subQ2,1.0]])],"derivedFrom":subQ1}),-1.0]])]});}
            var Q8;
            {var subQ0=sQuery(id+"F7.wireOp",EDGE,"E104.0");var subQ1=makeQuery(id+"F7.imprint","INTERSECT",VERTEX,{"derivedFrom":[subQ0,sQuery(id+"F7.wireOp",EDGE,"E107")]});Q8=makeQuery(id+"F7.imprint","IMPRINT",FACE,{"disambiguationData":[TD([[makeQuery(id+"F7.imprint","IMPRINT",EDGE,{"disambiguationData":[TD([[subQ1,1.0]])],"derivedFrom":subQ0}),1.0]])]});}
            extrude(context, id + "F8", {"entities" : qUnion([Q0, Q1, Q2, Q3, Q4, Q5, Q6, Q7, Q8]), "oppositeDirection" : true, "depth" : 5 * mm});
        }
        {
            var Q0;
            Q0=makeQuery(id+"F7.imprint","IMPRINT",FACE,{"disambiguationData":[TD([[makeQuery(id+"F7.imprint","IMPRINT",EDGE,{"derivedFrom":sQuery(id+"F7.wireOp",EDGE,"E105.0")}),-1.0]])]});
            var Q1;
            Q1=sQuery(id+"F7.wireOp",EDGE,"E106.0");
            extrude(context, id + "F9", {"entities" : qUnion([Q0]), "operationType" : NewBodyOperationType.ADD, "surfaceEntities" : qUnion([Q1]), "depth" : 25 * mm});
        }
        {
            var Q0;
            {var subQ0=sQuery(id+"F7.wireOp",EDGE,"E107");var subQ1=sQuery(id+"F7.wireOp",EDGE,"E102.0");var subQ2=makeQuery(id+"F7.imprint","INTERSECT",VERTEX,{"derivedFrom":[subQ1,subQ0]});Q0=makeQuery(id+"F7.imprint","IMPRINT",FACE,{"disambiguationData":[TD([[makeQuery(id+"F7.imprint","IMPRINT",EDGE,{"disambiguationData":[TD([[subQ2,-1.0]])],"derivedFrom":subQ1}),-1.0]])]});}
            var Q1;
            {var subQ0=sQuery(id+"F7.wireOp",EDGE,"E107");var subQ1=sQuery(id+"F7.wireOp",EDGE,"E103.0");var subQ2=makeQuery(id+"F7.imprint","INTERSECT",VERTEX,{"derivedFrom":[subQ1,subQ0]});Q1=makeQuery(id+"F7.imprint","IMPRINT",FACE,{"disambiguationData":[TD([[makeQuery(id+"F7.imprint","IMPRINT",EDGE,{"disambiguationData":[TD([[subQ2,1.0]])],"derivedFrom":subQ1}),-1.0]])]});}
            var Q2;
            {var subQ0=sQuery(id+"F7.wireOp",EDGE,"E104.0");var subQ1=makeQuery(id+"F7.imprint","INTERSECT",VERTEX,{"derivedFrom":[subQ0,sQuery(id+"F7.wireOp",EDGE,"E107")]});Q2=makeQuery(id+"F7.imprint","IMPRINT",FACE,{"disambiguationData":[TD([[makeQuery(id+"F7.imprint","IMPRINT",EDGE,{"disambiguationData":[TD([[subQ1,1.0]])],"derivedFrom":subQ0}),1.0]])]});}
            var Q3;
            {var subQ0=sQuery(id+"F7.wireOp",EDGE,"E102.0");var subQ1=makeQuery(id+"F7.imprint","INTERSECT",VERTEX,{"derivedFrom":[subQ0,sQuery(id+"F7.wireOp",EDGE,"E107")]});Q3=makeQuery(id+"F7.imprint","IMPRINT",FACE,{"disambiguationData":[TD([[makeQuery(id+"F7.imprint","IMPRINT",EDGE,{"disambiguationData":[TD([[subQ1,1.0]])],"derivedFrom":subQ0}),1.0]])]});}
            var Q4;
            {var subQ0=sQuery(id+"F7.wireOp",EDGE,"E107");var subQ1=sQuery(id+"F7.wireOp",EDGE,"E102.0");var subQ2=makeQuery(id+"F7.imprint","INTERSECT",VERTEX,{"derivedFrom":[subQ1,subQ0]});Q4=makeQuery(id+"F7.imprint","IMPRINT",FACE,{"disambiguationData":[TD([[makeQuery(id+"F7.imprint","IMPRINT",EDGE,{"disambiguationData":[TD([[subQ2,1.0]])],"derivedFrom":subQ1}),-1.0]])]});}
            var Q5;
            {var subQ0=sQuery(id+"F7.wireOp",EDGE,"E103.0");var subQ1=makeQuery(id+"F7.imprint","INTERSECT",VERTEX,{"derivedFrom":[subQ0,sQuery(id+"F7.wireOp",EDGE,"E107")]});Q5=makeQuery(id+"F7.imprint","IMPRINT",FACE,{"disambiguationData":[TD([[makeQuery(id+"F7.imprint","IMPRINT",EDGE,{"disambiguationData":[TD([[subQ1,-1.0]])],"derivedFrom":subQ0}),1.0]])]});}
            var Q6;
            Q6=makeQuery(id+"F6.opExtrude","CAP_FACE",FACE,{"disambiguationData":[OSD([sQuery(id+"F5.wireOp",EDGE,"E97")])],"isStart":false});
            extrude(context, id + "F10", {"entities" : qUnion([Q0, Q1, Q2, Q3, Q4, Q5, Q6]), "operationType" : NewBodyOperationType.REMOVE, "oppositeDirection" : true, "depth" : 2 * mm});
        }
        {
            var Q0;
            Q0=makeQuery(id+"F1.opExtrude","CAP_FACE",FACE,{"disambiguationData":[OSD([sQuery(id+"F0.wireOp",EDGE,"E0"),sQuery(id+"F0.wireOp",EDGE,"E1.MirrorCS"),sQuery(id+"F0.wireOp",EDGE,"E2.MirrorCS"),sQuery(id+"F0.wireOp",EDGE,"E3.MirrorCS"),sQuery(id+"F0.wireOp",EDGE,"E4.MirrorCS"),sQuery(id+"F0.wireOp",EDGE,"E5.MirrorCS"),sQuery(id+"F0.wireOp",EDGE,"E6.MirrorCS"),sQuery(id+"F0.wireOp",EDGE,"E16.filletArc"),sQuery(id+"F0.wireOp",EDGE,"E17.filletArc"),sQuery(id+"F0.wireOp",EDGE,"E18.filletArc"),sQuery(id+"F0.wireOp",EDGE,"E19.filletArc"),sQuery(id+"F0.wireOp",EDGE,"E20.filletArc"),sQuery(id+"F0.wireOp",EDGE,"E21.filletArc"),sQuery(id+"F0.wireOp",EDGE,"E23.1.0"),sQuery(id+"F0.wireOp",EDGE,"E23.1.1"),sQuery(id+"F0.wireOp",EDGE,"E23.1.2"),sQuery(id+"F0.wireOp",EDGE,"E23.1.3"),sQuery(id+"F0.wireOp",EDGE,"E23.1.4"),sQuery(id+"F0.wireOp",EDGE,"E23.1.5"),sQuery(id+"F0.wireOp",EDGE,"E23.1.6"),sQuery(id+"F0.wireOp",EDGE,"E23.1.7"),sQuery(id+"F0.wireOp",EDGE,"E23.1.8"),sQuery(id+"F0.wireOp",EDGE,"E23.1.9"),sQuery(id+"F0.wireOp",EDGE,"E23.1.10"),sQuery(id+"F0.wireOp",EDGE,"E23.1.11"),sQuery(id+"F0.wireOp",EDGE,"E23.2.0"),sQuery(id+"F0.wireOp",EDGE,"E23.2.1"),sQuery(id+"F0.wireOp",EDGE,"E23.2.2"),sQuery(id+"F0.wireOp",EDGE,"E23.2.3"),sQuery(id+"F0.wireOp",EDGE,"E23.2.4"),sQuery(id+"F0.wireOp",EDGE,"E23.2.5"),sQuery(id+"F0.wireOp",EDGE,"E23.2.6"),sQuery(id+"F0.wireOp",EDGE,"E23.2.7"),sQuery(id+"F0.wireOp",EDGE,"E23.2.8"),sQuery(id+"F0.wireOp",EDGE,"E23.2.9"),sQuery(id+"F0.wireOp",EDGE,"E23.2.10"),sQuery(id+"F0.wireOp",EDGE,"E23.2.11"),sQuery(id+"F0.wireOp",EDGE,"E23.3.0"),sQuery(id+"F0.wireOp",EDGE,"E23.3.1"),sQuery(id+"F0.wireOp",EDGE,"E23.3.2"),sQuery(id+"F0.wireOp",EDGE,"E23.3.3"),sQuery(id+"F0.wireOp",EDGE,"E23.3.4"),sQuery(id+"F0.wireOp",EDGE,"E23.3.5"),sQuery(id+"F0.wireOp",EDGE,"E23.3.6"),sQuery(id+"F0.wireOp",EDGE,"E23.3.7"),sQuery(id+"F0.wireOp",EDGE,"E23.3.8"),sQuery(id+"F0.wireOp",EDGE,"E23.3.9"),sQuery(id+"F0.wireOp",EDGE,"E23.3.10"),sQuery(id+"F0.wireOp",EDGE,"E23.3.11"),sQuery(id+"F0.wireOp",EDGE,"E23.4.0"),sQuery(id+"F0.wireOp",EDGE,"E23.4.1"),sQuery(id+"F0.wireOp",EDGE,"E23.4.2"),sQuery(id+"F0.wireOp",EDGE,"E23.4.3"),sQuery(id+"F0.wireOp",EDGE,"E23.4.4"),sQuery(id+"F0.wireOp",EDGE,"E23.4.5"),sQuery(id+"F0.wireOp",EDGE,"E23.4.6"),sQuery(id+"F0.wireOp",EDGE,"E23.4.7"),sQuery(id+"F0.wireOp",EDGE,"E23.4.8"),sQuery(id+"F0.wireOp",EDGE,"E23.4.9"),sQuery(id+"F0.wireOp",EDGE,"E23.4.10"),sQuery(id+"F0.wireOp",EDGE,"E23.4.11"),sQuery(id+"F0.wireOp",EDGE,"E23.5.0"),sQuery(id+"F0.wireOp",EDGE,"E23.5.1"),sQuery(id+"F0.wireOp",EDGE,"E23.5.2"),sQuery(id+"F0.wireOp",EDGE,"E23.5.3"),sQuery(id+"F0.wireOp",EDGE,"E23.5.4"),sQuery(id+"F0.wireOp",EDGE,"E23.5.5"),sQuery(id+"F0.wireOp",EDGE,"E23.5.6"),sQuery(id+"F0.wireOp",EDGE,"E23.5.7"),sQuery(id+"F0.wireOp",EDGE,"E23.5.8"),sQuery(id+"F0.wireOp",EDGE,"E23.5.9"),sQuery(id+"F0.wireOp",EDGE,"E23.5.10"),sQuery(id+"F0.wireOp",EDGE,"E23.5.11"),sQuery(id+"F0.wireOp",EDGE,"E23.6.0"),sQuery(id+"F0.wireOp",EDGE,"E23.6.1"),sQuery(id+"F0.wireOp",EDGE,"E23.6.2"),sQuery(id+"F0.wireOp",EDGE,"E23.6.3"),sQuery(id+"F0.wireOp",EDGE,"E23.6.4"),sQuery(id+"F0.wireOp",EDGE,"E23.6.5"),sQuery(id+"F0.wireOp",EDGE,"E23.6.6"),sQuery(id+"F0.wireOp",EDGE,"E23.6.7"),sQuery(id+"F0.wireOp",EDGE,"E23.6.8"),sQuery(id+"F0.wireOp",EDGE,"E23.6.9"),sQuery(id+"F0.wireOp",EDGE,"E23.6.10"),sQuery(id+"F0.wireOp",EDGE,"E23.6.11"),sQuery(id+"F0.wireOp",EDGE,"E23.7.0"),sQuery(id+"F0.wireOp",EDGE,"E23.7.1"),sQuery(id+"F0.wireOp",EDGE,"E23.7.2"),sQuery(id+"F0.wireOp",EDGE,"E23.7.3"),sQuery(id+"F0.wireOp",EDGE,"E23.7.4"),sQuery(id+"F0.wireOp",EDGE,"E23.7.5"),sQuery(id+"F0.wireOp",EDGE,"E23.7.6"),sQuery(id+"F0.wireOp",EDGE,"E23.7.7"),sQuery(id+"F0.wireOp",EDGE,"E23.7.8"),sQuery(id+"F0.wireOp",EDGE,"E23.7.9"),sQuery(id+"F0.wireOp",EDGE,"E23.7.10"),sQuery(id+"F0.wireOp",EDGE,"E23.7.11"),sQuery(id+"F0.wireOp",EDGE,"E23.8.0"),sQuery(id+"F0.wireOp",EDGE,"E23.8.1"),sQuery(id+"F0.wireOp",EDGE,"E23.8.2"),sQuery(id+"F0.wireOp",EDGE,"E23.8.3"),sQuery(id+"F0.wireOp",EDGE,"E23.8.4"),sQuery(id+"F0.wireOp",EDGE,"E23.8.5"),sQuery(id+"F0.wireOp",EDGE,"E23.8.6"),sQuery(id+"F0.wireOp",EDGE,"E23.8.7"),sQuery(id+"F0.wireOp",EDGE,"E23.8.8"),sQuery(id+"F0.wireOp",EDGE,"E23.8.9"),sQuery(id+"F0.wireOp",EDGE,"E23.8.10"),sQuery(id+"F0.wireOp",EDGE,"E23.8.11"),sQuery(id+"F0.wireOp",EDGE,"E23.9.0"),sQuery(id+"F0.wireOp",EDGE,"E23.9.1"),sQuery(id+"F0.wireOp",EDGE,"E23.9.2"),sQuery(id+"F0.wireOp",EDGE,"E23.9.3"),sQuery(id+"F0.wireOp",EDGE,"E23.9.4"),sQuery(id+"F0.wireOp",EDGE,"E23.9.5"),sQuery(id+"F0.wireOp",EDGE,"E23.9.6"),sQuery(id+"F0.wireOp",EDGE,"E23.9.7"),sQuery(id+"F0.wireOp",EDGE,"E23.9.8"),sQuery(id+"F0.wireOp",EDGE,"E23.9.9"),sQuery(id+"F0.wireOp",EDGE,"E23.9.10"),sQuery(id+"F0.wireOp",EDGE,"E23.9.11"),sQuery(id+"F0.wireOp",EDGE,"E23.10.0"),sQuery(id+"F0.wireOp",EDGE,"E23.10.1"),sQuery(id+"F0.wireOp",EDGE,"E23.10.2"),sQuery(id+"F0.wireOp",EDGE,"E23.10.3"),sQuery(id+"F0.wireOp",EDGE,"E23.10.4"),sQuery(id+"F0.wireOp",EDGE,"E23.10.5"),sQuery(id+"F0.wireOp",EDGE,"E23.10.6"),sQuery(id+"F0.wireOp",EDGE,"E23.10.7"),sQuery(id+"F0.wireOp",EDGE,"E23.10.8"),sQuery(id+"F0.wireOp",EDGE,"E23.10.9"),sQuery(id+"F0.wireOp",EDGE,"E23.10.10"),sQuery(id+"F0.wireOp",EDGE,"E23.10.11"),sQuery(id+"F0.wireOp",EDGE,"E23.11.0"),sQuery(id+"F0.wireOp",EDGE,"E23.11.1"),sQuery(id+"F0.wireOp",EDGE,"E23.11.2"),sQuery(id+"F0.wireOp",EDGE,"E23.11.3"),sQuery(id+"F0.wireOp",EDGE,"E23.11.4"),sQuery(id+"F0.wireOp",EDGE,"E23.11.5"),sQuery(id+"F0.wireOp",EDGE,"E23.11.6"),sQuery(id+"F0.wireOp",EDGE,"E23.11.7"),sQuery(id+"F0.wireOp",EDGE,"E23.11.8"),sQuery(id+"F0.wireOp",EDGE,"E23.11.9"),sQuery(id+"F0.wireOp",EDGE,"E23.11.10"),sQuery(id+"F0.wireOp",EDGE,"E23.11.11"),sQuery(id+"F0.wireOp",EDGE,"E23.12.0"),sQuery(id+"F0.wireOp",EDGE,"E23.12.1"),sQuery(id+"F0.wireOp",EDGE,"E23.12.2"),sQuery(id+"F0.wireOp",EDGE,"E23.12.3"),sQuery(id+"F0.wireOp",EDGE,"E23.12.4"),sQuery(id+"F0.wireOp",EDGE,"E23.12.5"),sQuery(id+"F0.wireOp",EDGE,"E23.12.6"),sQuery(id+"F0.wireOp",EDGE,"E23.12.7"),sQuery(id+"F0.wireOp",EDGE,"E23.12.8"),sQuery(id+"F0.wireOp",EDGE,"E23.12.9"),sQuery(id+"F0.wireOp",EDGE,"E23.12.10"),sQuery(id+"F0.wireOp",EDGE,"E23.12.11"),sQuery(id+"F0.wireOp",EDGE,"E23.13.0"),sQuery(id+"F0.wireOp",EDGE,"E23.13.1"),sQuery(id+"F0.wireOp",EDGE,"E23.13.2"),sQuery(id+"F0.wireOp",EDGE,"E23.13.3"),sQuery(id+"F0.wireOp",EDGE,"E23.13.4"),sQuery(id+"F0.wireOp",EDGE,"E23.13.5"),sQuery(id+"F0.wireOp",EDGE,"E23.13.6"),sQuery(id+"F0.wireOp",EDGE,"E23.13.7"),sQuery(id+"F0.wireOp",EDGE,"E23.13.8"),sQuery(id+"F0.wireOp",EDGE,"E23.13.9"),sQuery(id+"F0.wireOp",EDGE,"E23.13.10"),sQuery(id+"F0.wireOp",EDGE,"E23.13.11"),sQuery(id+"F0.wireOp",EDGE,"E23.14.0"),sQuery(id+"F0.wireOp",EDGE,"E23.14.1"),sQuery(id+"F0.wireOp",EDGE,"E23.14.2"),sQuery(id+"F0.wireOp",EDGE,"E23.14.3"),sQuery(id+"F0.wireOp",EDGE,"E23.14.4"),sQuery(id+"F0.wireOp",EDGE,"E23.14.5"),sQuery(id+"F0.wireOp",EDGE,"E23.14.6"),sQuery(id+"F0.wireOp",EDGE,"E23.14.7"),sQuery(id+"F0.wireOp",EDGE,"E23.14.8"),sQuery(id+"F0.wireOp",EDGE,"E23.14.9"),sQuery(id+"F0.wireOp",EDGE,"E23.14.10"),sQuery(id+"F0.wireOp",EDGE,"E23.14.11"),sQuery(id+"F0.wireOp",EDGE,"E23.15.0"),sQuery(id+"F0.wireOp",EDGE,"E23.15.1"),sQuery(id+"F0.wireOp",EDGE,"E23.15.2"),sQuery(id+"F0.wireOp",EDGE,"E23.15.3"),sQuery(id+"F0.wireOp",EDGE,"E23.15.4"),sQuery(id+"F0.wireOp",EDGE,"E23.15.5"),sQuery(id+"F0.wireOp",EDGE,"E23.15.6"),sQuery(id+"F0.wireOp",EDGE,"E23.15.7"),sQuery(id+"F0.wireOp",EDGE,"E23.15.8"),sQuery(id+"F0.wireOp",EDGE,"E23.15.9"),sQuery(id+"F0.wireOp",EDGE,"E23.15.10"),sQuery(id+"F0.wireOp",EDGE,"E23.15.11"),sQuery(id+"F0.wireOp",EDGE,"E23.16.0"),sQuery(id+"F0.wireOp",EDGE,"E23.16.1"),sQuery(id+"F0.wireOp",EDGE,"E23.16.2"),sQuery(id+"F0.wireOp",EDGE,"E23.16.3"),sQuery(id+"F0.wireOp",EDGE,"E23.16.4"),sQuery(id+"F0.wireOp",EDGE,"E23.16.5"),sQuery(id+"F0.wireOp",EDGE,"E23.16.6"),sQuery(id+"F0.wireOp",EDGE,"E23.16.7"),sQuery(id+"F0.wireOp",EDGE,"E23.16.8"),sQuery(id+"F0.wireOp",EDGE,"E23.16.9"),sQuery(id+"F0.wireOp",EDGE,"E23.16.10"),sQuery(id+"F0.wireOp",EDGE,"E23.16.11"),sQuery(id+"F0.wireOp",EDGE,"E23.17.0"),sQuery(id+"F0.wireOp",EDGE,"E23.17.1"),sQuery(id+"F0.wireOp",EDGE,"E23.17.2"),sQuery(id+"F0.wireOp",EDGE,"E23.17.3"),sQuery(id+"F0.wireOp",EDGE,"E23.17.4"),sQuery(id+"F0.wireOp",EDGE,"E23.17.5"),sQuery(id+"F0.wireOp",EDGE,"E23.17.6"),sQuery(id+"F0.wireOp",EDGE,"E23.17.7"),sQuery(id+"F0.wireOp",EDGE,"E23.17.8"),sQuery(id+"F0.wireOp",EDGE,"E23.17.9"),sQuery(id+"F0.wireOp",EDGE,"E23.17.10"),sQuery(id+"F0.wireOp",EDGE,"E23.17.11"),sQuery(id+"F0.wireOp",EDGE,"E23.18.0"),sQuery(id+"F0.wireOp",EDGE,"E23.18.1"),sQuery(id+"F0.wireOp",EDGE,"E23.18.2"),sQuery(id+"F0.wireOp",EDGE,"E23.18.3"),sQuery(id+"F0.wireOp",EDGE,"E23.18.4"),sQuery(id+"F0.wireOp",EDGE,"E23.18.5"),sQuery(id+"F0.wireOp",EDGE,"E23.18.6"),sQuery(id+"F0.wireOp",EDGE,"E23.18.7"),sQuery(id+"F0.wireOp",EDGE,"E23.18.8"),sQuery(id+"F0.wireOp",EDGE,"E23.18.9"),sQuery(id+"F0.wireOp",EDGE,"E23.18.10"),sQuery(id+"F0.wireOp",EDGE,"E23.18.11"),sQuery(id+"F0.wireOp",EDGE,"E23.19.0"),sQuery(id+"F0.wireOp",EDGE,"E23.19.1"),sQuery(id+"F0.wireOp",EDGE,"E23.19.2"),sQuery(id+"F0.wireOp",EDGE,"E23.19.3"),sQuery(id+"F0.wireOp",EDGE,"E23.19.4"),sQuery(id+"F0.wireOp",EDGE,"E23.19.5"),sQuery(id+"F0.wireOp",EDGE,"E23.19.6"),sQuery(id+"F0.wireOp",EDGE,"E23.19.7"),sQuery(id+"F0.wireOp",EDGE,"E23.19.8"),sQuery(id+"F0.wireOp",EDGE,"E23.19.9"),sQuery(id+"F0.wireOp",EDGE,"E23.19.10"),sQuery(id+"F0.wireOp",EDGE,"E23.19.11"),sQuery(id+"F0.wireOp",EDGE,"E23.20.0"),sQuery(id+"F0.wireOp",EDGE,"E23.20.1"),sQuery(id+"F0.wireOp",EDGE,"E23.20.2"),sQuery(id+"F0.wireOp",EDGE,"E23.20.3"),sQuery(id+"F0.wireOp",EDGE,"E23.20.4"),sQuery(id+"F0.wireOp",EDGE,"E23.20.5"),sQuery(id+"F0.wireOp",EDGE,"E23.20.6"),sQuery(id+"F0.wireOp",EDGE,"E23.20.7"),sQuery(id+"F0.wireOp",EDGE,"E23.20.8"),sQuery(id+"F0.wireOp",EDGE,"E23.20.9"),sQuery(id+"F0.wireOp",EDGE,"E23.20.10"),sQuery(id+"F0.wireOp",EDGE,"E23.20.11"),sQuery(id+"F0.wireOp",EDGE,"E23.21.0"),sQuery(id+"F0.wireOp",EDGE,"E23.21.1"),sQuery(id+"F0.wireOp",EDGE,"E23.21.2"),sQuery(id+"F0.wireOp",EDGE,"E23.21.3"),sQuery(id+"F0.wireOp",EDGE,"E23.21.4"),sQuery(id+"F0.wireOp",EDGE,"E23.21.5"),sQuery(id+"F0.wireOp",EDGE,"E23.21.6"),sQuery(id+"F0.wireOp",EDGE,"E23.21.7"),sQuery(id+"F0.wireOp",EDGE,"E23.21.8"),sQuery(id+"F0.wireOp",EDGE,"E23.21.9"),sQuery(id+"F0.wireOp",EDGE,"E23.21.10"),sQuery(id+"F0.wireOp",EDGE,"E23.21.11"),sQuery(id+"F0.wireOp",EDGE,"E23.22.0"),sQuery(id+"F0.wireOp",EDGE,"E23.22.1"),sQuery(id+"F0.wireOp",EDGE,"E23.22.2"),sQuery(id+"F0.wireOp",EDGE,"E23.22.3"),sQuery(id+"F0.wireOp",EDGE,"E23.22.4"),sQuery(id+"F0.wireOp",EDGE,"E23.22.5"),sQuery(id+"F0.wireOp",EDGE,"E23.22.6"),sQuery(id+"F0.wireOp",EDGE,"E23.22.7"),sQuery(id+"F0.wireOp",EDGE,"E23.22.8"),sQuery(id+"F0.wireOp",EDGE,"E23.22.9"),sQuery(id+"F0.wireOp",EDGE,"E23.22.10"),sQuery(id+"F0.wireOp",EDGE,"E23.22.11"),sQuery(id+"F0.wireOp",EDGE,"E23.23.0"),sQuery(id+"F0.wireOp",EDGE,"E23.23.1"),sQuery(id+"F0.wireOp",EDGE,"E23.23.2"),sQuery(id+"F0.wireOp",EDGE,"E23.23.3"),sQuery(id+"F0.wireOp",EDGE,"E23.23.4"),sQuery(id+"F0.wireOp",EDGE,"E23.23.5"),sQuery(id+"F0.wireOp",EDGE,"E23.23.6"),sQuery(id+"F0.wireOp",EDGE,"E23.23.7"),sQuery(id+"F0.wireOp",EDGE,"E23.23.8"),sQuery(id+"F0.wireOp",EDGE,"E23.23.9"),sQuery(id+"F0.wireOp",EDGE,"E23.23.10"),sQuery(id+"F0.wireOp",EDGE,"E23.23.11"),sQuery(id+"F0.wireOp",EDGE,"E23.24.0"),sQuery(id+"F0.wireOp",EDGE,"E23.24.1"),sQuery(id+"F0.wireOp",EDGE,"E23.24.2"),sQuery(id+"F0.wireOp",EDGE,"E23.24.3"),sQuery(id+"F0.wireOp",EDGE,"E23.24.4"),sQuery(id+"F0.wireOp",EDGE,"E23.24.5"),sQuery(id+"F0.wireOp",EDGE,"E23.24.6"),sQuery(id+"F0.wireOp",EDGE,"E23.24.7"),sQuery(id+"F0.wireOp",EDGE,"E23.24.8"),sQuery(id+"F0.wireOp",EDGE,"E23.24.9"),sQuery(id+"F0.wireOp",EDGE,"E23.24.10"),sQuery(id+"F0.wireOp",EDGE,"E23.24.11"),sQuery(id+"F0.wireOp",EDGE,"E23.25.0"),sQuery(id+"F0.wireOp",EDGE,"E23.25.1"),sQuery(id+"F0.wireOp",EDGE,"E23.25.2"),sQuery(id+"F0.wireOp",EDGE,"E23.25.3"),sQuery(id+"F0.wireOp",EDGE,"E23.25.4"),sQuery(id+"F0.wireOp",EDGE,"E23.25.5"),sQuery(id+"F0.wireOp",EDGE,"E23.25.6"),sQuery(id+"F0.wireOp",EDGE,"E23.25.7"),sQuery(id+"F0.wireOp",EDGE,"E23.25.8"),sQuery(id+"F0.wireOp",EDGE,"E23.25.9"),sQuery(id+"F0.wireOp",EDGE,"E23.25.10"),sQuery(id+"F0.wireOp",EDGE,"E23.25.11"),sQuery(id+"F0.wireOp",EDGE,"E23.26.0"),sQuery(id+"F0.wireOp",EDGE,"E23.26.1"),sQuery(id+"F0.wireOp",EDGE,"E23.26.2"),sQuery(id+"F0.wireOp",EDGE,"E23.26.3"),sQuery(id+"F0.wireOp",EDGE,"E23.26.4"),sQuery(id+"F0.wireOp",EDGE,"E23.26.5"),sQuery(id+"F0.wireOp",EDGE,"E23.26.6"),sQuery(id+"F0.wireOp",EDGE,"E23.26.7"),sQuery(id+"F0.wireOp",EDGE,"E23.26.8"),sQuery(id+"F0.wireOp",EDGE,"E23.26.9"),sQuery(id+"F0.wireOp",EDGE,"E23.26.10"),sQuery(id+"F0.wireOp",EDGE,"E23.26.11"),sQuery(id+"F0.wireOp",EDGE,"E23.27.0"),sQuery(id+"F0.wireOp",EDGE,"E23.27.1"),sQuery(id+"F0.wireOp",EDGE,"E23.27.2"),sQuery(id+"F0.wireOp",EDGE,"E23.27.3"),sQuery(id+"F0.wireOp",EDGE,"E23.27.4"),sQuery(id+"F0.wireOp",EDGE,"E23.27.5"),sQuery(id+"F0.wireOp",EDGE,"E23.27.6"),sQuery(id+"F0.wireOp",EDGE,"E23.27.7"),sQuery(id+"F0.wireOp",EDGE,"E23.27.8"),sQuery(id+"F0.wireOp",EDGE,"E23.27.9"),sQuery(id+"F0.wireOp",EDGE,"E23.27.10"),sQuery(id+"F0.wireOp",EDGE,"E23.27.11"),sQuery(id+"F0.wireOp",EDGE,"E23.28.0"),sQuery(id+"F0.wireOp",EDGE,"E23.28.1"),sQuery(id+"F0.wireOp",EDGE,"E23.28.2"),sQuery(id+"F0.wireOp",EDGE,"E23.28.3"),sQuery(id+"F0.wireOp",EDGE,"E23.28.4"),sQuery(id+"F0.wireOp",EDGE,"E23.28.5"),sQuery(id+"F0.wireOp",EDGE,"E23.28.6"),sQuery(id+"F0.wireOp",EDGE,"E23.28.7"),sQuery(id+"F0.wireOp",EDGE,"E23.28.8"),sQuery(id+"F0.wireOp",EDGE,"E23.28.9"),sQuery(id+"F0.wireOp",EDGE,"E23.28.10"),sQuery(id+"F0.wireOp",EDGE,"E23.28.11"),sQuery(id+"F0.wireOp",EDGE,"E23.29.0"),sQuery(id+"F0.wireOp",EDGE,"E23.29.1"),sQuery(id+"F0.wireOp",EDGE,"E23.29.2"),sQuery(id+"F0.wireOp",EDGE,"E23.29.3"),sQuery(id+"F0.wireOp",EDGE,"E23.29.4"),sQuery(id+"F0.wireOp",EDGE,"E23.29.5"),sQuery(id+"F0.wireOp",EDGE,"E23.29.6"),sQuery(id+"F0.wireOp",EDGE,"E23.29.7"),sQuery(id+"F0.wireOp",EDGE,"E23.29.8"),sQuery(id+"F0.wireOp",EDGE,"E23.29.9"),sQuery(id+"F0.wireOp",EDGE,"E23.29.10"),sQuery(id+"F0.wireOp",EDGE,"E23.29.11"),sQuery(id+"F0.wireOp",EDGE,"E23.30.0"),sQuery(id+"F0.wireOp",EDGE,"E23.30.1"),sQuery(id+"F0.wireOp",EDGE,"E23.30.2"),sQuery(id+"F0.wireOp",EDGE,"E23.30.3"),sQuery(id+"F0.wireOp",EDGE,"E23.30.4"),sQuery(id+"F0.wireOp",EDGE,"E23.30.5"),sQuery(id+"F0.wireOp",EDGE,"E23.30.6"),sQuery(id+"F0.wireOp",EDGE,"E23.30.7"),sQuery(id+"F0.wireOp",EDGE,"E23.30.8"),sQuery(id+"F0.wireOp",EDGE,"E23.30.9"),sQuery(id+"F0.wireOp",EDGE,"E23.30.10"),sQuery(id+"F0.wireOp",EDGE,"E23.30.11"),sQuery(id+"F0.wireOp",EDGE,"E23.31.0"),sQuery(id+"F0.wireOp",EDGE,"E23.31.1"),sQuery(id+"F0.wireOp",EDGE,"E23.31.2"),sQuery(id+"F0.wireOp",EDGE,"E23.31.3"),sQuery(id+"F0.wireOp",EDGE,"E23.31.4"),sQuery(id+"F0.wireOp",EDGE,"E23.31.5"),sQuery(id+"F0.wireOp",EDGE,"E23.31.6"),sQuery(id+"F0.wireOp",EDGE,"E23.31.7"),sQuery(id+"F0.wireOp",EDGE,"E23.31.8"),sQuery(id+"F0.wireOp",EDGE,"E23.31.9"),sQuery(id+"F0.wireOp",EDGE,"E23.31.10"),sQuery(id+"F0.wireOp",EDGE,"E23.31.11"),sQuery(id+"F0.wireOp",EDGE,"E23.32.0"),sQuery(id+"F0.wireOp",EDGE,"E23.32.1"),sQuery(id+"F0.wireOp",EDGE,"E23.32.2"),sQuery(id+"F0.wireOp",EDGE,"E23.32.3"),sQuery(id+"F0.wireOp",EDGE,"E23.32.4"),sQuery(id+"F0.wireOp",EDGE,"E23.32.5"),sQuery(id+"F0.wireOp",EDGE,"E23.32.6"),sQuery(id+"F0.wireOp",EDGE,"E23.32.7"),sQuery(id+"F0.wireOp",EDGE,"E23.32.8"),sQuery(id+"F0.wireOp",EDGE,"E23.32.9"),sQuery(id+"F0.wireOp",EDGE,"E23.32.10"),sQuery(id+"F0.wireOp",EDGE,"E23.32.11"),sQuery(id+"F0.wireOp",EDGE,"E23.33.0"),sQuery(id+"F0.wireOp",EDGE,"E23.33.1"),sQuery(id+"F0.wireOp",EDGE,"E23.33.2"),sQuery(id+"F0.wireOp",EDGE,"E23.33.3"),sQuery(id+"F0.wireOp",EDGE,"E23.33.4"),sQuery(id+"F0.wireOp",EDGE,"E23.33.5"),sQuery(id+"F0.wireOp",EDGE,"E23.33.6"),sQuery(id+"F0.wireOp",EDGE,"E23.33.7"),sQuery(id+"F0.wireOp",EDGE,"E23.33.8"),sQuery(id+"F0.wireOp",EDGE,"E23.33.9"),sQuery(id+"F0.wireOp",EDGE,"E23.33.10"),sQuery(id+"F0.wireOp",EDGE,"E23.33.11"),sQuery(id+"F0.wireOp",EDGE,"E23.34.0"),sQuery(id+"F0.wireOp",EDGE,"E23.34.1"),sQuery(id+"F0.wireOp",EDGE,"E23.34.2"),sQuery(id+"F0.wireOp",EDGE,"E23.34.3"),sQuery(id+"F0.wireOp",EDGE,"E23.34.4"),sQuery(id+"F0.wireOp",EDGE,"E23.34.5"),sQuery(id+"F0.wireOp",EDGE,"E23.34.6"),sQuery(id+"F0.wireOp",EDGE,"E23.34.7"),sQuery(id+"F0.wireOp",EDGE,"E23.34.8"),sQuery(id+"F0.wireOp",EDGE,"E23.34.9"),sQuery(id+"F0.wireOp",EDGE,"E23.34.10"),sQuery(id+"F0.wireOp",EDGE,"E23.34.11"),sQuery(id+"F0.wireOp",EDGE,"E23.35.0"),sQuery(id+"F0.wireOp",EDGE,"E23.35.1"),sQuery(id+"F0.wireOp",EDGE,"E23.35.2"),sQuery(id+"F0.wireOp",EDGE,"E23.35.3"),sQuery(id+"F0.wireOp",EDGE,"E23.35.4"),sQuery(id+"F0.wireOp",EDGE,"E23.35.5"),sQuery(id+"F0.wireOp",EDGE,"E23.35.6"),sQuery(id+"F0.wireOp",EDGE,"E23.35.7"),sQuery(id+"F0.wireOp",EDGE,"E23.35.8"),sQuery(id+"F0.wireOp",EDGE,"E23.35.9"),sQuery(id+"F0.wireOp",EDGE,"E23.35.10"),sQuery(id+"F0.wireOp",EDGE,"E23.35.11"),sQuery(id+"F0.wireOp",EDGE,"E23.36.0"),sQuery(id+"F0.wireOp",EDGE,"E23.36.1"),sQuery(id+"F0.wireOp",EDGE,"E23.36.2"),sQuery(id+"F0.wireOp",EDGE,"E23.36.3"),sQuery(id+"F0.wireOp",EDGE,"E23.36.4"),sQuery(id+"F0.wireOp",EDGE,"E23.36.5"),sQuery(id+"F0.wireOp",EDGE,"E23.36.6"),sQuery(id+"F0.wireOp",EDGE,"E23.36.7"),sQuery(id+"F0.wireOp",EDGE,"E23.36.8"),sQuery(id+"F0.wireOp",EDGE,"E23.36.9"),sQuery(id+"F0.wireOp",EDGE,"E23.36.10"),sQuery(id+"F0.wireOp",EDGE,"E23.36.11"),sQuery(id+"F0.wireOp",EDGE,"E23.37.0"),sQuery(id+"F0.wireOp",EDGE,"E23.37.1"),sQuery(id+"F0.wireOp",EDGE,"E23.37.2"),sQuery(id+"F0.wireOp",EDGE,"E23.37.3"),sQuery(id+"F0.wireOp",EDGE,"E23.37.4"),sQuery(id+"F0.wireOp",EDGE,"E23.37.5"),sQuery(id+"F0.wireOp",EDGE,"E23.37.6"),sQuery(id+"F0.wireOp",EDGE,"E23.37.7"),sQuery(id+"F0.wireOp",EDGE,"E23.37.8"),sQuery(id+"F0.wireOp",EDGE,"E23.37.9"),sQuery(id+"F0.wireOp",EDGE,"E23.37.10"),sQuery(id+"F0.wireOp",EDGE,"E23.37.11"),sQuery(id+"F0.wireOp",EDGE,"E23.38.0"),sQuery(id+"F0.wireOp",EDGE,"E23.38.1"),sQuery(id+"F0.wireOp",EDGE,"E23.38.2"),sQuery(id+"F0.wireOp",EDGE,"E23.38.3"),sQuery(id+"F0.wireOp",EDGE,"E23.38.4"),sQuery(id+"F0.wireOp",EDGE,"E23.38.5"),sQuery(id+"F0.wireOp",EDGE,"E23.38.6"),sQuery(id+"F0.wireOp",EDGE,"E23.38.7"),sQuery(id+"F0.wireOp",EDGE,"E23.38.8"),sQuery(id+"F0.wireOp",EDGE,"E23.38.9"),sQuery(id+"F0.wireOp",EDGE,"E23.38.10"),sQuery(id+"F0.wireOp",EDGE,"E23.38.11"),sQuery(id+"F0.wireOp",EDGE,"E23.39.0"),sQuery(id+"F0.wireOp",EDGE,"E23.39.1"),sQuery(id+"F0.wireOp",EDGE,"E23.39.2"),sQuery(id+"F0.wireOp",EDGE,"E23.39.3"),sQuery(id+"F0.wireOp",EDGE,"E23.39.4"),sQuery(id+"F0.wireOp",EDGE,"E23.39.5"),sQuery(id+"F0.wireOp",EDGE,"E23.39.6"),sQuery(id+"F0.wireOp",EDGE,"E23.39.7"),sQuery(id+"F0.wireOp",EDGE,"E23.39.8"),sQuery(id+"F0.wireOp",EDGE,"E23.39.9"),sQuery(id+"F0.wireOp",EDGE,"E23.39.10"),sQuery(id+"F0.wireOp",EDGE,"E23.39.11"),sQuery(id+"F0.wireOp",EDGE,"E23.40.0"),sQuery(id+"F0.wireOp",EDGE,"E23.40.1"),sQuery(id+"F0.wireOp",EDGE,"E23.40.2"),sQuery(id+"F0.wireOp",EDGE,"E23.40.3"),sQuery(id+"F0.wireOp",EDGE,"E23.40.4"),sQuery(id+"F0.wireOp",EDGE,"E23.40.5"),sQuery(id+"F0.wireOp",EDGE,"E23.40.6"),sQuery(id+"F0.wireOp",EDGE,"E23.40.7"),sQuery(id+"F0.wireOp",EDGE,"E23.40.8"),sQuery(id+"F0.wireOp",EDGE,"E23.40.9"),sQuery(id+"F0.wireOp",EDGE,"E23.40.10"),sQuery(id+"F0.wireOp",EDGE,"E23.40.11"),sQuery(id+"F0.wireOp",EDGE,"E23.41.0"),sQuery(id+"F0.wireOp",EDGE,"E23.41.1"),sQuery(id+"F0.wireOp",EDGE,"E23.41.2"),sQuery(id+"F0.wireOp",EDGE,"E23.41.3"),sQuery(id+"F0.wireOp",EDGE,"E23.41.4"),sQuery(id+"F0.wireOp",EDGE,"E23.41.5"),sQuery(id+"F0.wireOp",EDGE,"E23.41.6"),sQuery(id+"F0.wireOp",EDGE,"E23.41.7"),sQuery(id+"F0.wireOp",EDGE,"E23.41.8"),sQuery(id+"F0.wireOp",EDGE,"E23.41.9"),sQuery(id+"F0.wireOp",EDGE,"E23.41.10"),sQuery(id+"F0.wireOp",EDGE,"E23.41.11"),sQuery(id+"F0.wireOp",EDGE,"E23.42.0"),sQuery(id+"F0.wireOp",EDGE,"E23.42.1"),sQuery(id+"F0.wireOp",EDGE,"E23.42.2"),sQuery(id+"F0.wireOp",EDGE,"E23.42.3"),sQuery(id+"F0.wireOp",EDGE,"E23.42.4"),sQuery(id+"F0.wireOp",EDGE,"E23.42.5"),sQuery(id+"F0.wireOp",EDGE,"E23.42.6"),sQuery(id+"F0.wireOp",EDGE,"E23.42.7"),sQuery(id+"F0.wireOp",EDGE,"E23.42.8"),sQuery(id+"F0.wireOp",EDGE,"E23.42.9"),sQuery(id+"F0.wireOp",EDGE,"E23.42.10"),sQuery(id+"F0.wireOp",EDGE,"E23.42.11"),sQuery(id+"F0.wireOp",EDGE,"E23.43.0"),sQuery(id+"F0.wireOp",EDGE,"E23.43.1"),sQuery(id+"F0.wireOp",EDGE,"E23.43.2"),sQuery(id+"F0.wireOp",EDGE,"E23.43.3"),sQuery(id+"F0.wireOp",EDGE,"E23.43.4"),sQuery(id+"F0.wireOp",EDGE,"E23.43.5"),sQuery(id+"F0.wireOp",EDGE,"E23.43.6"),sQuery(id+"F0.wireOp",EDGE,"E23.43.7"),sQuery(id+"F0.wireOp",EDGE,"E23.43.8"),sQuery(id+"F0.wireOp",EDGE,"E23.43.9"),sQuery(id+"F0.wireOp",EDGE,"E23.43.10"),sQuery(id+"F0.wireOp",EDGE,"E23.43.11"),sQuery(id+"F0.wireOp",EDGE,"E23.44.0"),sQuery(id+"F0.wireOp",EDGE,"E23.44.1"),sQuery(id+"F0.wireOp",EDGE,"E23.44.2"),sQuery(id+"F0.wireOp",EDGE,"E23.44.3"),sQuery(id+"F0.wireOp",EDGE,"E23.44.4"),sQuery(id+"F0.wireOp",EDGE,"E23.44.5"),sQuery(id+"F0.wireOp",EDGE,"E23.44.6"),sQuery(id+"F0.wireOp",EDGE,"E23.44.7"),sQuery(id+"F0.wireOp",EDGE,"E23.44.8"),sQuery(id+"F0.wireOp",EDGE,"E23.44.9"),sQuery(id+"F0.wireOp",EDGE,"E23.44.10"),sQuery(id+"F0.wireOp",EDGE,"E23.44.11"),sQuery(id+"F0.wireOp",EDGE,"E23.45.0"),sQuery(id+"F0.wireOp",EDGE,"E23.45.1"),sQuery(id+"F0.wireOp",EDGE,"E23.45.2"),sQuery(id+"F0.wireOp",EDGE,"E23.45.3"),sQuery(id+"F0.wireOp",EDGE,"E23.45.4"),sQuery(id+"F0.wireOp",EDGE,"E23.45.5"),sQuery(id+"F0.wireOp",EDGE,"E23.45.6"),sQuery(id+"F0.wireOp",EDGE,"E23.45.7"),sQuery(id+"F0.wireOp",EDGE,"E23.45.8"),sQuery(id+"F0.wireOp",EDGE,"E23.45.9"),sQuery(id+"F0.wireOp",EDGE,"E23.45.10"),sQuery(id+"F0.wireOp",EDGE,"E23.45.11"),sQuery(id+"F0.wireOp",EDGE,"E23.46.0"),sQuery(id+"F0.wireOp",EDGE,"E23.46.1"),sQuery(id+"F0.wireOp",EDGE,"E23.46.2"),sQuery(id+"F0.wireOp",EDGE,"E23.46.3"),sQuery(id+"F0.wireOp",EDGE,"E23.46.4"),sQuery(id+"F0.wireOp",EDGE,"E23.46.5"),sQuery(id+"F0.wireOp",EDGE,"E23.46.6"),sQuery(id+"F0.wireOp",EDGE,"E23.46.7"),sQuery(id+"F0.wireOp",EDGE,"E23.46.8"),sQuery(id+"F0.wireOp",EDGE,"E23.46.9"),sQuery(id+"F0.wireOp",EDGE,"E23.46.10"),sQuery(id+"F0.wireOp",EDGE,"E23.46.11"),sQuery(id+"F0.wireOp",EDGE,"E23.47.0"),sQuery(id+"F0.wireOp",EDGE,"E23.47.1"),sQuery(id+"F0.wireOp",EDGE,"E23.47.2"),sQuery(id+"F0.wireOp",EDGE,"E23.47.3"),sQuery(id+"F0.wireOp",EDGE,"E23.47.4"),sQuery(id+"F0.wireOp",EDGE,"E23.47.5"),sQuery(id+"F0.wireOp",EDGE,"E23.47.6"),sQuery(id+"F0.wireOp",EDGE,"E23.47.7"),sQuery(id+"F0.wireOp",EDGE,"E23.47.8"),sQuery(id+"F0.wireOp",EDGE,"E23.47.9"),sQuery(id+"F0.wireOp",EDGE,"E23.47.10"),sQuery(id+"F0.wireOp",EDGE,"E23.47.11"),sQuery(id+"F0.wireOp",EDGE,"E23.48.0"),sQuery(id+"F0.wireOp",EDGE,"E23.48.1"),sQuery(id+"F0.wireOp",EDGE,"E23.48.2"),sQuery(id+"F0.wireOp",EDGE,"E23.48.3"),sQuery(id+"F0.wireOp",EDGE,"E23.48.4"),sQuery(id+"F0.wireOp",EDGE,"E23.48.5"),sQuery(id+"F0.wireOp",EDGE,"E23.48.6"),sQuery(id+"F0.wireOp",EDGE,"E23.48.7"),sQuery(id+"F0.wireOp",EDGE,"E23.48.8"),sQuery(id+"F0.wireOp",EDGE,"E23.48.9"),sQuery(id+"F0.wireOp",EDGE,"E23.48.10"),sQuery(id+"F0.wireOp",EDGE,"E23.48.11"),sQuery(id+"F0.wireOp",EDGE,"E23.49.0"),sQuery(id+"F0.wireOp",EDGE,"E23.49.1"),sQuery(id+"F0.wireOp",EDGE,"E23.49.2"),sQuery(id+"F0.wireOp",EDGE,"E23.49.3"),sQuery(id+"F0.wireOp",EDGE,"E23.49.4"),sQuery(id+"F0.wireOp",EDGE,"E23.49.5"),sQuery(id+"F0.wireOp",EDGE,"E23.49.6"),sQuery(id+"F0.wireOp",EDGE,"E23.49.7"),sQuery(id+"F0.wireOp",EDGE,"E23.49.8"),sQuery(id+"F0.wireOp",EDGE,"E23.49.9"),sQuery(id+"F0.wireOp",EDGE,"E23.49.10"),sQuery(id+"F0.wireOp",EDGE,"E23.49.11"),sQuery(id+"F0.wireOp",EDGE,"E23.50.0"),sQuery(id+"F0.wireOp",EDGE,"E23.50.1"),sQuery(id+"F0.wireOp",EDGE,"E23.50.2"),sQuery(id+"F0.wireOp",EDGE,"E23.50.3"),sQuery(id+"F0.wireOp",EDGE,"E23.50.4"),sQuery(id+"F0.wireOp",EDGE,"E23.50.5"),sQuery(id+"F0.wireOp",EDGE,"E23.50.6"),sQuery(id+"F0.wireOp",EDGE,"E23.50.7"),sQuery(id+"F0.wireOp",EDGE,"E23.50.8"),sQuery(id+"F0.wireOp",EDGE,"E23.50.9"),sQuery(id+"F0.wireOp",EDGE,"E23.50.10"),sQuery(id+"F0.wireOp",EDGE,"E23.50.11"),sQuery(id+"F0.wireOp",EDGE,"E23.51.0"),sQuery(id+"F0.wireOp",EDGE,"E23.51.1"),sQuery(id+"F0.wireOp",EDGE,"E23.51.2"),sQuery(id+"F0.wireOp",EDGE,"E23.51.3"),sQuery(id+"F0.wireOp",EDGE,"E23.51.4"),sQuery(id+"F0.wireOp",EDGE,"E23.51.5"),sQuery(id+"F0.wireOp",EDGE,"E23.51.6"),sQuery(id+"F0.wireOp",EDGE,"E23.51.7"),sQuery(id+"F0.wireOp",EDGE,"E23.51.8"),sQuery(id+"F0.wireOp",EDGE,"E23.51.9"),sQuery(id+"F0.wireOp",EDGE,"E23.51.10"),sQuery(id+"F0.wireOp",EDGE,"E23.51.11"),sQuery(id+"F0.wireOp",EDGE,"E23.52.0"),sQuery(id+"F0.wireOp",EDGE,"E23.52.1"),sQuery(id+"F0.wireOp",EDGE,"E23.52.2"),sQuery(id+"F0.wireOp",EDGE,"E23.52.3"),sQuery(id+"F0.wireOp",EDGE,"E23.52.4"),sQuery(id+"F0.wireOp",EDGE,"E23.52.5"),sQuery(id+"F0.wireOp",EDGE,"E23.52.6"),sQuery(id+"F0.wireOp",EDGE,"E23.52.7"),sQuery(id+"F0.wireOp",EDGE,"E23.52.8"),sQuery(id+"F0.wireOp",EDGE,"E23.52.9"),sQuery(id+"F0.wireOp",EDGE,"E23.52.10"),sQuery(id+"F0.wireOp",EDGE,"E23.52.11"),sQuery(id+"F0.wireOp",EDGE,"E23.53.0"),sQuery(id+"F0.wireOp",EDGE,"E23.53.1"),sQuery(id+"F0.wireOp",EDGE,"E23.53.2"),sQuery(id+"F0.wireOp",EDGE,"E23.53.3"),sQuery(id+"F0.wireOp",EDGE,"E23.53.4"),sQuery(id+"F0.wireOp",EDGE,"E23.53.5"),sQuery(id+"F0.wireOp",EDGE,"E23.53.6"),sQuery(id+"F0.wireOp",EDGE,"E23.53.7"),sQuery(id+"F0.wireOp",EDGE,"E23.53.8"),sQuery(id+"F0.wireOp",EDGE,"E23.53.9"),sQuery(id+"F0.wireOp",EDGE,"E23.53.10"),sQuery(id+"F0.wireOp",EDGE,"E23.53.11"),sQuery(id+"F0.wireOp",EDGE,"E23.54.0"),sQuery(id+"F0.wireOp",EDGE,"E23.54.1"),sQuery(id+"F0.wireOp",EDGE,"E23.54.2"),sQuery(id+"F0.wireOp",EDGE,"E23.54.3"),sQuery(id+"F0.wireOp",EDGE,"E23.54.4"),sQuery(id+"F0.wireOp",EDGE,"E23.54.5"),sQuery(id+"F0.wireOp",EDGE,"E23.54.6"),sQuery(id+"F0.wireOp",EDGE,"E23.54.7"),sQuery(id+"F0.wireOp",EDGE,"E23.54.8"),sQuery(id+"F0.wireOp",EDGE,"E23.54.9"),sQuery(id+"F0.wireOp",EDGE,"E23.54.10"),sQuery(id+"F0.wireOp",EDGE,"E23.54.11"),sQuery(id+"F0.wireOp",EDGE,"E23.55.0"),sQuery(id+"F0.wireOp",EDGE,"E23.55.1"),sQuery(id+"F0.wireOp",EDGE,"E23.55.2"),sQuery(id+"F0.wireOp",EDGE,"E23.55.3"),sQuery(id+"F0.wireOp",EDGE,"E23.55.4"),sQuery(id+"F0.wireOp",EDGE,"E23.55.5"),sQuery(id+"F0.wireOp",EDGE,"E23.55.6"),sQuery(id+"F0.wireOp",EDGE,"E23.55.7"),sQuery(id+"F0.wireOp",EDGE,"E23.55.8"),sQuery(id+"F0.wireOp",EDGE,"E23.55.9"),sQuery(id+"F0.wireOp",EDGE,"E23.55.10"),sQuery(id+"F0.wireOp",EDGE,"E23.55.11"),sQuery(id+"F0.wireOp",EDGE,"E23.56.0"),sQuery(id+"F0.wireOp",EDGE,"E23.56.1"),sQuery(id+"F0.wireOp",EDGE,"E23.56.2"),sQuery(id+"F0.wireOp",EDGE,"E23.56.3"),sQuery(id+"F0.wireOp",EDGE,"E23.56.4"),sQuery(id+"F0.wireOp",EDGE,"E23.56.5"),sQuery(id+"F0.wireOp",EDGE,"E23.56.6"),sQuery(id+"F0.wireOp",EDGE,"E23.56.7"),sQuery(id+"F0.wireOp",EDGE,"E23.56.8"),sQuery(id+"F0.wireOp",EDGE,"E23.56.9"),sQuery(id+"F0.wireOp",EDGE,"E23.56.10"),sQuery(id+"F0.wireOp",EDGE,"E23.56.11"),sQuery(id+"F0.wireOp",EDGE,"E23.57.0"),sQuery(id+"F0.wireOp",EDGE,"E23.57.1"),sQuery(id+"F0.wireOp",EDGE,"E23.57.2"),sQuery(id+"F0.wireOp",EDGE,"E23.57.3"),sQuery(id+"F0.wireOp",EDGE,"E23.57.4"),sQuery(id+"F0.wireOp",EDGE,"E23.57.5"),sQuery(id+"F0.wireOp",EDGE,"E23.57.6"),sQuery(id+"F0.wireOp",EDGE,"E23.57.7"),sQuery(id+"F0.wireOp",EDGE,"E23.57.8"),sQuery(id+"F0.wireOp",EDGE,"E23.57.9"),sQuery(id+"F0.wireOp",EDGE,"E23.57.10"),sQuery(id+"F0.wireOp",EDGE,"E23.57.11"),sQuery(id+"F0.wireOp",EDGE,"E23.58.0"),sQuery(id+"F0.wireOp",EDGE,"E23.58.1"),sQuery(id+"F0.wireOp",EDGE,"E23.58.2"),sQuery(id+"F0.wireOp",EDGE,"E23.58.3"),sQuery(id+"F0.wireOp",EDGE,"E23.58.4"),sQuery(id+"F0.wireOp",EDGE,"E23.58.5"),sQuery(id+"F0.wireOp",EDGE,"E23.58.6"),sQuery(id+"F0.wireOp",EDGE,"E23.58.7"),sQuery(id+"F0.wireOp",EDGE,"E23.58.8"),sQuery(id+"F0.wireOp",EDGE,"E23.58.9"),sQuery(id+"F0.wireOp",EDGE,"E23.58.10"),sQuery(id+"F0.wireOp",EDGE,"E23.58.11"),sQuery(id+"F0.wireOp",EDGE,"E23.59.0"),sQuery(id+"F0.wireOp",EDGE,"E23.59.1"),sQuery(id+"F0.wireOp",EDGE,"E23.59.2"),sQuery(id+"F0.wireOp",EDGE,"E23.59.3"),sQuery(id+"F0.wireOp",EDGE,"E23.59.4"),sQuery(id+"F0.wireOp",EDGE,"E23.59.5"),sQuery(id+"F0.wireOp",EDGE,"E23.59.6"),sQuery(id+"F0.wireOp",EDGE,"E23.59.7"),sQuery(id+"F0.wireOp",EDGE,"E23.59.8"),sQuery(id+"F0.wireOp",EDGE,"E23.59.9"),sQuery(id+"F0.wireOp",EDGE,"E23.59.10"),sQuery(id+"F0.wireOp",EDGE,"E23.59.11"),sQuery(id+"F0.wireOp",EDGE,"E23.60.0"),sQuery(id+"F0.wireOp",EDGE,"E23.60.1"),sQuery(id+"F0.wireOp",EDGE,"E23.60.2"),sQuery(id+"F0.wireOp",EDGE,"E23.60.3"),sQuery(id+"F0.wireOp",EDGE,"E23.60.4"),sQuery(id+"F0.wireOp",EDGE,"E23.60.5"),sQuery(id+"F0.wireOp",EDGE,"E23.60.6"),sQuery(id+"F0.wireOp",EDGE,"E23.60.7"),sQuery(id+"F0.wireOp",EDGE,"E23.60.8"),sQuery(id+"F0.wireOp",EDGE,"E23.60.9"),sQuery(id+"F0.wireOp",EDGE,"E23.60.10"),sQuery(id+"F0.wireOp",EDGE,"E23.60.11"),sQuery(id+"F0.wireOp",EDGE,"E23.61.0"),sQuery(id+"F0.wireOp",EDGE,"E23.61.1"),sQuery(id+"F0.wireOp",EDGE,"E23.61.2"),sQuery(id+"F0.wireOp",EDGE,"E23.61.3"),sQuery(id+"F0.wireOp",EDGE,"E23.61.4"),sQuery(id+"F0.wireOp",EDGE,"E23.61.5"),sQuery(id+"F0.wireOp",EDGE,"E23.61.6"),sQuery(id+"F0.wireOp",EDGE,"E23.61.7"),sQuery(id+"F0.wireOp",EDGE,"E23.61.8"),sQuery(id+"F0.wireOp",EDGE,"E23.61.9"),sQuery(id+"F0.wireOp",EDGE,"E23.61.10"),sQuery(id+"F0.wireOp",EDGE,"E23.61.11"),sQuery(id+"F0.wireOp",EDGE,"E23.62.0"),sQuery(id+"F0.wireOp",EDGE,"E23.62.1"),sQuery(id+"F0.wireOp",EDGE,"E23.62.2"),sQuery(id+"F0.wireOp",EDGE,"E23.62.3"),sQuery(id+"F0.wireOp",EDGE,"E23.62.4"),sQuery(id+"F0.wireOp",EDGE,"E23.62.5"),sQuery(id+"F0.wireOp",EDGE,"E23.62.6"),sQuery(id+"F0.wireOp",EDGE,"E23.62.7"),sQuery(id+"F0.wireOp",EDGE,"E23.62.8"),sQuery(id+"F0.wireOp",EDGE,"E23.62.9"),sQuery(id+"F0.wireOp",EDGE,"E23.62.10"),sQuery(id+"F0.wireOp",EDGE,"E23.62.11"),sQuery(id+"F0.wireOp",EDGE,"E23.63.0"),sQuery(id+"F0.wireOp",EDGE,"E23.63.1"),sQuery(id+"F0.wireOp",EDGE,"E23.63.2"),sQuery(id+"F0.wireOp",EDGE,"E23.63.3"),sQuery(id+"F0.wireOp",EDGE,"E23.63.4"),sQuery(id+"F0.wireOp",EDGE,"E23.63.5"),sQuery(id+"F0.wireOp",EDGE,"E23.63.6"),sQuery(id+"F0.wireOp",EDGE,"E23.63.7"),sQuery(id+"F0.wireOp",EDGE,"E23.63.8"),sQuery(id+"F0.wireOp",EDGE,"E23.63.9"),sQuery(id+"F0.wireOp",EDGE,"E23.63.10"),sQuery(id+"F0.wireOp",EDGE,"E23.63.11"),sQuery(id+"F0.wireOp",EDGE,"E23.64.0"),sQuery(id+"F0.wireOp",EDGE,"E23.64.1"),sQuery(id+"F0.wireOp",EDGE,"E23.64.2"),sQuery(id+"F0.wireOp",EDGE,"E23.64.3"),sQuery(id+"F0.wireOp",EDGE,"E23.64.4"),sQuery(id+"F0.wireOp",EDGE,"E23.64.5"),sQuery(id+"F0.wireOp",EDGE,"E23.64.6"),sQuery(id+"F0.wireOp",EDGE,"E23.64.7"),sQuery(id+"F0.wireOp",EDGE,"E23.64.8"),sQuery(id+"F0.wireOp",EDGE,"E23.64.9"),sQuery(id+"F0.wireOp",EDGE,"E23.64.10"),sQuery(id+"F0.wireOp",EDGE,"E23.64.11"),sQuery(id+"F0.wireOp",EDGE,"E23.65.0"),sQuery(id+"F0.wireOp",EDGE,"E23.65.1"),sQuery(id+"F0.wireOp",EDGE,"E23.65.2"),sQuery(id+"F0.wireOp",EDGE,"E23.65.3"),sQuery(id+"F0.wireOp",EDGE,"E23.65.4"),sQuery(id+"F0.wireOp",EDGE,"E23.65.5"),sQuery(id+"F0.wireOp",EDGE,"E23.65.6"),sQuery(id+"F0.wireOp",EDGE,"E23.65.7"),sQuery(id+"F0.wireOp",EDGE,"E23.65.8"),sQuery(id+"F0.wireOp",EDGE,"E23.65.9"),sQuery(id+"F0.wireOp",EDGE,"E23.65.10"),sQuery(id+"F0.wireOp",EDGE,"E23.65.11"),sQuery(id+"F0.wireOp",EDGE,"E23.66.0"),sQuery(id+"F0.wireOp",EDGE,"E23.66.1"),sQuery(id+"F0.wireOp",EDGE,"E23.66.2"),sQuery(id+"F0.wireOp",EDGE,"E23.66.3"),sQuery(id+"F0.wireOp",EDGE,"E23.66.4"),sQuery(id+"F0.wireOp",EDGE,"E23.66.5"),sQuery(id+"F0.wireOp",EDGE,"E23.66.6"),sQuery(id+"F0.wireOp",EDGE,"E23.66.7"),sQuery(id+"F0.wireOp",EDGE,"E23.66.8"),sQuery(id+"F0.wireOp",EDGE,"E23.66.9"),sQuery(id+"F0.wireOp",EDGE,"E23.66.10"),sQuery(id+"F0.wireOp",EDGE,"E23.66.11"),sQuery(id+"F0.wireOp",EDGE,"E23.67.0"),sQuery(id+"F0.wireOp",EDGE,"E23.67.1"),sQuery(id+"F0.wireOp",EDGE,"E23.67.2"),sQuery(id+"F0.wireOp",EDGE,"E23.67.3"),sQuery(id+"F0.wireOp",EDGE,"E23.67.4"),sQuery(id+"F0.wireOp",EDGE,"E23.67.5"),sQuery(id+"F0.wireOp",EDGE,"E23.67.6"),sQuery(id+"F0.wireOp",EDGE,"E23.67.7"),sQuery(id+"F0.wireOp",EDGE,"E23.67.8"),sQuery(id+"F0.wireOp",EDGE,"E23.67.9"),sQuery(id+"F0.wireOp",EDGE,"E23.67.10"),sQuery(id+"F0.wireOp",EDGE,"E23.67.11"),sQuery(id+"F0.wireOp",EDGE,"E23.68.0"),sQuery(id+"F0.wireOp",EDGE,"E23.68.1"),sQuery(id+"F0.wireOp",EDGE,"E23.68.2"),sQuery(id+"F0.wireOp",EDGE,"E23.68.3"),sQuery(id+"F0.wireOp",EDGE,"E23.68.4"),sQuery(id+"F0.wireOp",EDGE,"E23.68.5"),sQuery(id+"F0.wireOp",EDGE,"E23.68.6"),sQuery(id+"F0.wireOp",EDGE,"E23.68.7"),sQuery(id+"F0.wireOp",EDGE,"E23.68.8"),sQuery(id+"F0.wireOp",EDGE,"E23.68.9"),sQuery(id+"F0.wireOp",EDGE,"E23.68.10"),sQuery(id+"F0.wireOp",EDGE,"E23.68.11"),sQuery(id+"F0.wireOp",EDGE,"E23.69.0"),sQuery(id+"F0.wireOp",EDGE,"E23.69.1"),sQuery(id+"F0.wireOp",EDGE,"E23.69.2"),sQuery(id+"F0.wireOp",EDGE,"E23.69.3"),sQuery(id+"F0.wireOp",EDGE,"E23.69.4"),sQuery(id+"F0.wireOp",EDGE,"E23.69.5"),sQuery(id+"F0.wireOp",EDGE,"E23.69.6"),sQuery(id+"F0.wireOp",EDGE,"E23.69.7"),sQuery(id+"F0.wireOp",EDGE,"E23.69.8"),sQuery(id+"F0.wireOp",EDGE,"E23.69.9"),sQuery(id+"F0.wireOp",EDGE,"E23.69.10"),sQuery(id+"F0.wireOp",EDGE,"E23.69.11"),sQuery(id+"F0.wireOp",EDGE,"E23.70.0"),sQuery(id+"F0.wireOp",EDGE,"E23.70.1"),sQuery(id+"F0.wireOp",EDGE,"E23.70.2"),sQuery(id+"F0.wireOp",EDGE,"E23.70.3"),sQuery(id+"F0.wireOp",EDGE,"E23.70.4"),sQuery(id+"F0.wireOp",EDGE,"E23.70.5"),sQuery(id+"F0.wireOp",EDGE,"E23.70.6"),sQuery(id+"F0.wireOp",EDGE,"E23.70.7"),sQuery(id+"F0.wireOp",EDGE,"E23.70.8"),sQuery(id+"F0.wireOp",EDGE,"E23.70.9"),sQuery(id+"F0.wireOp",EDGE,"E23.70.10"),sQuery(id+"F0.wireOp",EDGE,"E23.70.11"),sQuery(id+"F0.wireOp",EDGE,"E23.71.0"),sQuery(id+"F0.wireOp",EDGE,"E23.71.1"),sQuery(id+"F0.wireOp",EDGE,"E23.71.2"),sQuery(id+"F0.wireOp",EDGE,"E23.71.3"),sQuery(id+"F0.wireOp",EDGE,"E23.71.4"),sQuery(id+"F0.wireOp",EDGE,"E23.71.5"),sQuery(id+"F0.wireOp",EDGE,"E23.71.6"),sQuery(id+"F0.wireOp",EDGE,"E23.71.7"),sQuery(id+"F0.wireOp",EDGE,"E23.71.8"),sQuery(id+"F0.wireOp",EDGE,"E23.71.9"),sQuery(id+"F0.wireOp",EDGE,"E23.71.10"),sQuery(id+"F0.wireOp",EDGE,"E23.71.11"),sQuery(id+"F0.wireOp",EDGE,"E24.trimOffspring"),sQuery(id+"F0.wireOp",EDGE,"E25.trimOffspring"),sQuery(id+"F0.wireOp",EDGE,"E26.trimOffspring"),sQuery(id+"F0.wireOp",EDGE,"E27.trimOffspring"),sQuery(id+"F0.wireOp",EDGE,"E28.trimOffspring"),sQuery(id+"F0.wireOp",EDGE,"E29.trimOffspring"),sQuery(id+"F0.wireOp",EDGE,"E30.trimOffspring"),sQuery(id+"F0.wireOp",EDGE,"E31.trimOffspring"),sQuery(id+"F0.wireOp",EDGE,"E32.trimOffspring"),sQuery(id+"F0.wireOp",EDGE,"E33.trimOffspring"),sQuery(id+"F0.wireOp",EDGE,"E34.trimOffspring"),sQuery(id+"F0.wireOp",EDGE,"E35.trimOffspring"),sQuery(id+"F0.wireOp",EDGE,"E36.trimOffspring"),sQuery(id+"F0.wireOp",EDGE,"E37.trimOffspring"),sQuery(id+"F0.wireOp",EDGE,"E38.trimOffspring"),sQuery(id+"F0.wireOp",EDGE,"E39.trimOffspring"),sQuery(id+"F0.wireOp",EDGE,"E40.trimOffspring"),sQuery(id+"F0.wireOp",EDGE,"E41.trimOffspring"),sQuery(id+"F0.wireOp",EDGE,"E42.trimOffspring"),sQuery(id+"F0.wireOp",EDGE,"E43.trimOffspring"),sQuery(id+"F0.wireOp",EDGE,"E44.trimOffspring"),sQuery(id+"F0.wireOp",EDGE,"E45.trimOffspring"),sQuery(id+"F0.wireOp",EDGE,"E46.trimOffspring"),sQuery(id+"F0.wireOp",EDGE,"E47.trimOffspring"),sQuery(id+"F0.wireOp",EDGE,"E48.trimOffspring"),sQuery(id+"F0.wireOp",EDGE,"E49.trimOffspring"),sQuery(id+"F0.wireOp",EDGE,"E50.trimOffspring"),sQuery(id+"F0.wireOp",EDGE,"E51.trimOffspring"),sQuery(id+"F0.wireOp",EDGE,"E52.trimOffspring"),sQuery(id+"F0.wireOp",EDGE,"E53.trimOffspring"),sQuery(id+"F0.wireOp",EDGE,"E54.trimOffspring"),sQuery(id+"F0.wireOp",EDGE,"E55.trimOffspring"),sQuery(id+"F0.wireOp",EDGE,"E56.trimOffspring"),sQuery(id+"F0.wireOp",EDGE,"E57.trimOffspring"),sQuery(id+"F0.wireOp",EDGE,"E58.trimOffspring"),sQuery(id+"F0.wireOp",EDGE,"E59.trimOffspring"),sQuery(id+"F0.wireOp",EDGE,"E60.trimOffspring"),sQuery(id+"F0.wireOp",EDGE,"E61.trimOffspring"),sQuery(id+"F0.wireOp",EDGE,"E62.trimOffspring"),sQuery(id+"F0.wireOp",EDGE,"E63.trimOffspring"),sQuery(id+"F0.wireOp",EDGE,"E64.trimOffspring"),sQuery(id+"F0.wireOp",EDGE,"E65.trimOffspring"),sQuery(id+"F0.wireOp",EDGE,"E66.trimOffspring"),sQuery(id+"F0.wireOp",EDGE,"E67.trimOffspring"),sQuery(id+"F0.wireOp",EDGE,"E68.trimOffspring"),sQuery(id+"F0.wireOp",EDGE,"E69.trimOffspring"),sQuery(id+"F0.wireOp",EDGE,"E70.trimOffspring"),sQuery(id+"F0.wireOp",EDGE,"E71.trimOffspring"),sQuery(id+"F0.wireOp",EDGE,"E72.trimOffspring"),sQuery(id+"F0.wireOp",EDGE,"E73.trimOffspring"),sQuery(id+"F0.wireOp",EDGE,"E74.trimOffspring"),sQuery(id+"F0.wireOp",EDGE,"E75.trimOffspring"),sQuery(id+"F0.wireOp",EDGE,"E76.trimOffspring"),sQuery(id+"F0.wireOp",EDGE,"E77.trimOffspring"),sQuery(id+"F0.wireOp",EDGE,"E78.trimOffspring"),sQuery(id+"F0.wireOp",EDGE,"E79.trimOffspring"),sQuery(id+"F0.wireOp",EDGE,"E80.trimOffspring"),sQuery(id+"F0.wireOp",EDGE,"E81.trimOffspring"),sQuery(id+"F0.wireOp",EDGE,"E82.trimOffspring"),sQuery(id+"F0.wireOp",EDGE,"E83.trimOffspring"),sQuery(id+"F0.wireOp",EDGE,"E84.trimOffspring"),sQuery(id+"F0.wireOp",EDGE,"E85.trimOffspring"),sQuery(id+"F0.wireOp",EDGE,"E86.trimOffspring"),sQuery(id+"F0.wireOp",EDGE,"E87.trimOffspring"),sQuery(id+"F0.wireOp",EDGE,"E88.trimOffspring"),sQuery(id+"F0.wireOp",EDGE,"E89.trimOffspring"),sQuery(id+"F0.wireOp",EDGE,"E90.trimOffspring"),sQuery(id+"F0.wireOp",EDGE,"E91.trimOffspring"),sQuery(id+"F0.wireOp",EDGE,"E92.trimOffspring"),sQuery(id+"F0.wireOp",EDGE,"E93.trimOffspring"),sQuery(id+"F0.wireOp",EDGE,"E94")])],"isStart":false});
            var sketch = newSketch(context, id + "F11", { "sketchPlane" : qUnion([Q0])});
            skSolve(sketch);
        }
        {
            var Q0;
            Q0=qSketchRegion(id+"F11",true);
            var Q1;
            Q1=makeQuery(id+"F4.opExtrude","CAP_FACE",FACE,{"disambiguationData":[OSD([sQuery(id+"F3.wireOp",EDGE,"E96.1.0")])],"isStart":false});
            var Q2;
            Q2=makeQuery(id+"F6.opExtrude","CAP_FACE",FACE,{"disambiguationData":[OSD([sQuery(id+"F5.wireOp",EDGE,"E97")])],"isStart":false});
            var Q3;
            Q3=makeQuery(id+"F11.imprint","IMPRINT",FACE,{"disambiguationData":[TD([[makeQuery(id+"F11.imprint","IMPRINT",EDGE,{"derivedFrom":makeQuery(id+"F1.opExtrude","CAP_EDGE",EDGE,{"disambiguationData":[OSD([sQuery(id+"F0.wireOp",EDGE,"E0")])],"isStart":false})}),1.0]])]});
            var Q4;
            Q4=makeQuery(id+"F4.opExtrude","CAP_FACE",FACE,{"disambiguationData":[OSD([sQuery(id+"F3.wireOp",EDGE,"E96.2.0")])],"isStart":false});
            var Q5;
            Q5=makeQuery(id+"F4.opExtrude","CAP_FACE",FACE,{"disambiguationData":[OSD([sQuery(id+"F3.wireOp",EDGE,"E95")])],"isStart":false});
            extrude(context, id + "F12", {"entities" : qUnion([Q0, Q1, Q2, Q3, Q4, Q5]), "operationType" : NewBodyOperationType.REMOVE, "oppositeDirection" : true, "depth" : 40 * mm});
        }
        {
            var Q0;
            Q0=makeQuery(id+"F7.imprint","IMPRINT",FACE,{"disambiguationData":[TD([[makeQuery(id+"F7.imprint","IMPRINT",EDGE,{"derivedFrom":sQuery(id+"F7.wireOp",EDGE,"E105.0")}),1.0]])]});
            var sketch = newSketch(context, id + "F13", { "sketchPlane" : qUnion([Q0])});
            skCircle(sketch, "E110.0", {"center": v(-25.4, 44) * mm, "radius": 3.18 * mm});
            skCircle(sketch, "E111.0", {"center": v(-25.4, -44) * mm, "radius": 3.18 * mm});
            skCircle(sketch, "E112.0", {"center": v(50.8, 0) * mm, "radius": 3.18 * mm});
            skCircle(sketch, "E113.0", {"center": v(0, 0) * mm, "radius": 3.18 * mm});
            skArc(sketch, "E114", {"start": v(-16.74, 49) * mm, "mid": v(-30.4, 52.65) * mm, "end": v(-34.06, 39) * mm});
            skLineSegment(sketch, "E115", {"start": v(-34.06, 39) * mm, "end": v(-13, 2.5) * mm});
            skLineSegment(sketch, "E116", {"start": v(-16.74, 49) * mm, "end": v(4.33, 12.5) * mm});
            skLineSegment(sketch, "E117.1.0", {"start": v(-16.74, -49) * mm, "end": v(4.33, -12.5) * mm});
            skLineSegment(sketch, "E117.1.1", {"start": v(-34.06, -39) * mm, "end": v(-13, -2.5) * mm});
            skArc(sketch, "E117.1.2", {"start": v(-34.06, -39) * mm, "mid": v(-30.4, -52.65) * mm, "end": v(-16.74, -49) * mm});
            skLineSegment(sketch, "E117.2.0", {"start": v(50.8, 10) * mm, "end": v(8.66, 10) * mm});
            skLineSegment(sketch, "E117.2.1", {"start": v(50.8, -10) * mm, "end": v(8.66, -10) * mm});
            skArc(sketch, "E117.2.2", {"start": v(50.8, -10) * mm, "mid": v(60.8, 0) * mm, "end": v(50.8, 10) * mm});
            skPoint(sketch, "E118.orphan", {"position": v(-8.66, 5) * mm});
            skPoint(sketch, "E119.orphan", {"position": v(-8.66, -5) * mm});
            skPoint(sketch, "E120.orphan", {"position": v(8.66, -5) * mm});
            skPoint(sketch, "E121.orphan", {"position": v(0, 10) * mm});
            skPoint(sketch, "E122.orphan", {"position": v(0, -10) * mm});
            skPoint(sketch, "E123.orphan", {"position": v(8.66, 5) * mm});
            skPoint(sketch, "E124.visualSharp", {"position": v(5.77, 10) * mm});
            skArc(sketch, "E124.filletArc", {"start": v(4.33, 12.5) * mm, "mid": v(6.16, 10.67) * mm, "end": v(8.66, 10) * mm});
            skPoint(sketch, "E125.visualSharp", {"position": v(-11.55, 0) * mm});
            skArc(sketch, "E125.filletArc", {"start": v(-13, -2.5) * mm, "mid": v(-12.32, 0) * mm, "end": v(-13, 2.5) * mm});
            skPoint(sketch, "E126.visualSharp", {"position": v(5.77, -10) * mm});
            skArc(sketch, "E126.filletArc", {"start": v(8.66, -10) * mm, "mid": v(6.16, -10.67) * mm, "end": v(4.33, -12.5) * mm});
            skSolve(sketch);
        }
        {
            var Q0;
            Q0=qSketchRegion(id+"F13",true);
            extrude(context, id + "F14", {"entities" : qUnion([Q0]), "depth" : 3 * mm});
        }
        {
            var Q0;
            Q0=makeQuery(id+"F2.opExtrude","CAP_FACE",FACE,{"disambiguationData":[OSD([sQuery(id+"F0.wireOp",EDGE,"E0"),sQuery(id+"F0.wireOp",EDGE,"E1.MirrorCS"),sQuery(id+"F0.wireOp",EDGE,"E2.MirrorCS"),sQuery(id+"F0.wireOp",EDGE,"E3.MirrorCS"),sQuery(id+"F0.wireOp",EDGE,"E4.MirrorCS"),sQuery(id+"F0.wireOp",EDGE,"E5.MirrorCS"),sQuery(id+"F0.wireOp",EDGE,"E6.MirrorCS"),sQuery(id+"F0.wireOp",EDGE,"E16.filletArc"),sQuery(id+"F0.wireOp",EDGE,"E17.filletArc"),sQuery(id+"F0.wireOp",EDGE,"E18.filletArc"),sQuery(id+"F0.wireOp",EDGE,"E19.filletArc"),sQuery(id+"F0.wireOp",EDGE,"E20.filletArc"),sQuery(id+"F0.wireOp",EDGE,"E21.filletArc"),sQuery(id+"F0.wireOp",EDGE,"E22"),sQuery(id+"F0.wireOp",EDGE,"E23.1.0"),sQuery(id+"F0.wireOp",EDGE,"E23.1.1"),sQuery(id+"F0.wireOp",EDGE,"E23.1.2"),sQuery(id+"F0.wireOp",EDGE,"E23.1.3"),sQuery(id+"F0.wireOp",EDGE,"E23.1.4"),sQuery(id+"F0.wireOp",EDGE,"E23.1.5"),sQuery(id+"F0.wireOp",EDGE,"E23.1.6"),sQuery(id+"F0.wireOp",EDGE,"E23.1.7"),sQuery(id+"F0.wireOp",EDGE,"E23.1.8"),sQuery(id+"F0.wireOp",EDGE,"E23.1.9"),sQuery(id+"F0.wireOp",EDGE,"E23.1.10"),sQuery(id+"F0.wireOp",EDGE,"E23.1.11"),sQuery(id+"F0.wireOp",EDGE,"E23.2.0"),sQuery(id+"F0.wireOp",EDGE,"E23.2.1"),sQuery(id+"F0.wireOp",EDGE,"E23.2.2"),sQuery(id+"F0.wireOp",EDGE,"E23.2.3"),sQuery(id+"F0.wireOp",EDGE,"E23.2.4"),sQuery(id+"F0.wireOp",EDGE,"E23.2.5"),sQuery(id+"F0.wireOp",EDGE,"E23.2.6"),sQuery(id+"F0.wireOp",EDGE,"E23.2.7"),sQuery(id+"F0.wireOp",EDGE,"E23.2.8"),sQuery(id+"F0.wireOp",EDGE,"E23.2.9"),sQuery(id+"F0.wireOp",EDGE,"E23.2.10"),sQuery(id+"F0.wireOp",EDGE,"E23.2.11"),sQuery(id+"F0.wireOp",EDGE,"E23.3.0"),sQuery(id+"F0.wireOp",EDGE,"E23.3.1"),sQuery(id+"F0.wireOp",EDGE,"E23.3.2"),sQuery(id+"F0.wireOp",EDGE,"E23.3.3"),sQuery(id+"F0.wireOp",EDGE,"E23.3.4"),sQuery(id+"F0.wireOp",EDGE,"E23.3.5"),sQuery(id+"F0.wireOp",EDGE,"E23.3.6"),sQuery(id+"F0.wireOp",EDGE,"E23.3.7"),sQuery(id+"F0.wireOp",EDGE,"E23.3.8"),sQuery(id+"F0.wireOp",EDGE,"E23.3.9"),sQuery(id+"F0.wireOp",EDGE,"E23.3.10"),sQuery(id+"F0.wireOp",EDGE,"E23.3.11"),sQuery(id+"F0.wireOp",EDGE,"E23.4.0"),sQuery(id+"F0.wireOp",EDGE,"E23.4.1"),sQuery(id+"F0.wireOp",EDGE,"E23.4.2"),sQuery(id+"F0.wireOp",EDGE,"E23.4.3"),sQuery(id+"F0.wireOp",EDGE,"E23.4.4"),sQuery(id+"F0.wireOp",EDGE,"E23.4.5"),sQuery(id+"F0.wireOp",EDGE,"E23.4.6"),sQuery(id+"F0.wireOp",EDGE,"E23.4.7"),sQuery(id+"F0.wireOp",EDGE,"E23.4.8"),sQuery(id+"F0.wireOp",EDGE,"E23.4.9"),sQuery(id+"F0.wireOp",EDGE,"E23.4.10"),sQuery(id+"F0.wireOp",EDGE,"E23.4.11"),sQuery(id+"F0.wireOp",EDGE,"E23.5.0"),sQuery(id+"F0.wireOp",EDGE,"E23.5.1"),sQuery(id+"F0.wireOp",EDGE,"E23.5.2"),sQuery(id+"F0.wireOp",EDGE,"E23.5.3"),sQuery(id+"F0.wireOp",EDGE,"E23.5.4"),sQuery(id+"F0.wireOp",EDGE,"E23.5.5"),sQuery(id+"F0.wireOp",EDGE,"E23.5.6"),sQuery(id+"F0.wireOp",EDGE,"E23.5.7"),sQuery(id+"F0.wireOp",EDGE,"E23.5.8"),sQuery(id+"F0.wireOp",EDGE,"E23.5.9"),sQuery(id+"F0.wireOp",EDGE,"E23.5.10"),sQuery(id+"F0.wireOp",EDGE,"E23.5.11"),sQuery(id+"F0.wireOp",EDGE,"E23.6.0"),sQuery(id+"F0.wireOp",EDGE,"E23.6.1"),sQuery(id+"F0.wireOp",EDGE,"E23.6.2"),sQuery(id+"F0.wireOp",EDGE,"E23.6.3"),sQuery(id+"F0.wireOp",EDGE,"E23.6.4"),sQuery(id+"F0.wireOp",EDGE,"E23.6.5"),sQuery(id+"F0.wireOp",EDGE,"E23.6.6"),sQuery(id+"F0.wireOp",EDGE,"E23.6.7"),sQuery(id+"F0.wireOp",EDGE,"E23.6.8"),sQuery(id+"F0.wireOp",EDGE,"E23.6.9"),sQuery(id+"F0.wireOp",EDGE,"E23.6.10"),sQuery(id+"F0.wireOp",EDGE,"E23.6.11"),sQuery(id+"F0.wireOp",EDGE,"E23.7.0"),sQuery(id+"F0.wireOp",EDGE,"E23.7.1"),sQuery(id+"F0.wireOp",EDGE,"E23.7.2"),sQuery(id+"F0.wireOp",EDGE,"E23.7.3"),sQuery(id+"F0.wireOp",EDGE,"E23.7.4"),sQuery(id+"F0.wireOp",EDGE,"E23.7.5"),sQuery(id+"F0.wireOp",EDGE,"E23.7.6"),sQuery(id+"F0.wireOp",EDGE,"E23.7.7"),sQuery(id+"F0.wireOp",EDGE,"E23.7.8"),sQuery(id+"F0.wireOp",EDGE,"E23.7.9"),sQuery(id+"F0.wireOp",EDGE,"E23.7.10"),sQuery(id+"F0.wireOp",EDGE,"E23.7.11"),sQuery(id+"F0.wireOp",EDGE,"E23.8.0"),sQuery(id+"F0.wireOp",EDGE,"E23.8.1"),sQuery(id+"F0.wireOp",EDGE,"E23.8.2"),sQuery(id+"F0.wireOp",EDGE,"E23.8.3"),sQuery(id+"F0.wireOp",EDGE,"E23.8.4"),sQuery(id+"F0.wireOp",EDGE,"E23.8.5"),sQuery(id+"F0.wireOp",EDGE,"E23.8.6"),sQuery(id+"F0.wireOp",EDGE,"E23.8.7"),sQuery(id+"F0.wireOp",EDGE,"E23.8.8"),sQuery(id+"F0.wireOp",EDGE,"E23.8.9"),sQuery(id+"F0.wireOp",EDGE,"E23.8.10"),sQuery(id+"F0.wireOp",EDGE,"E23.8.11"),sQuery(id+"F0.wireOp",EDGE,"E23.9.0"),sQuery(id+"F0.wireOp",EDGE,"E23.9.1"),sQuery(id+"F0.wireOp",EDGE,"E23.9.2"),sQuery(id+"F0.wireOp",EDGE,"E23.9.3"),sQuery(id+"F0.wireOp",EDGE,"E23.9.4"),sQuery(id+"F0.wireOp",EDGE,"E23.9.5"),sQuery(id+"F0.wireOp",EDGE,"E23.9.6"),sQuery(id+"F0.wireOp",EDGE,"E23.9.7"),sQuery(id+"F0.wireOp",EDGE,"E23.9.8"),sQuery(id+"F0.wireOp",EDGE,"E23.9.9"),sQuery(id+"F0.wireOp",EDGE,"E23.9.10"),sQuery(id+"F0.wireOp",EDGE,"E23.9.11"),sQuery(id+"F0.wireOp",EDGE,"E23.10.0"),sQuery(id+"F0.wireOp",EDGE,"E23.10.1"),sQuery(id+"F0.wireOp",EDGE,"E23.10.2"),sQuery(id+"F0.wireOp",EDGE,"E23.10.3"),sQuery(id+"F0.wireOp",EDGE,"E23.10.4"),sQuery(id+"F0.wireOp",EDGE,"E23.10.5"),sQuery(id+"F0.wireOp",EDGE,"E23.10.6"),sQuery(id+"F0.wireOp",EDGE,"E23.10.7"),sQuery(id+"F0.wireOp",EDGE,"E23.10.8"),sQuery(id+"F0.wireOp",EDGE,"E23.10.9"),sQuery(id+"F0.wireOp",EDGE,"E23.10.10"),sQuery(id+"F0.wireOp",EDGE,"E23.10.11"),sQuery(id+"F0.wireOp",EDGE,"E23.11.0"),sQuery(id+"F0.wireOp",EDGE,"E23.11.1"),sQuery(id+"F0.wireOp",EDGE,"E23.11.2"),sQuery(id+"F0.wireOp",EDGE,"E23.11.3"),sQuery(id+"F0.wireOp",EDGE,"E23.11.4"),sQuery(id+"F0.wireOp",EDGE,"E23.11.5"),sQuery(id+"F0.wireOp",EDGE,"E23.11.6"),sQuery(id+"F0.wireOp",EDGE,"E23.11.7"),sQuery(id+"F0.wireOp",EDGE,"E23.11.8"),sQuery(id+"F0.wireOp",EDGE,"E23.11.9"),sQuery(id+"F0.wireOp",EDGE,"E23.11.10"),sQuery(id+"F0.wireOp",EDGE,"E23.11.11"),sQuery(id+"F0.wireOp",EDGE,"E23.12.0"),sQuery(id+"F0.wireOp",EDGE,"E23.12.1"),sQuery(id+"F0.wireOp",EDGE,"E23.12.2"),sQuery(id+"F0.wireOp",EDGE,"E23.12.3"),sQuery(id+"F0.wireOp",EDGE,"E23.12.4"),sQuery(id+"F0.wireOp",EDGE,"E23.12.5"),sQuery(id+"F0.wireOp",EDGE,"E23.12.6"),sQuery(id+"F0.wireOp",EDGE,"E23.12.7"),sQuery(id+"F0.wireOp",EDGE,"E23.12.8"),sQuery(id+"F0.wireOp",EDGE,"E23.12.9"),sQuery(id+"F0.wireOp",EDGE,"E23.12.10"),sQuery(id+"F0.wireOp",EDGE,"E23.12.11"),sQuery(id+"F0.wireOp",EDGE,"E23.13.0"),sQuery(id+"F0.wireOp",EDGE,"E23.13.1"),sQuery(id+"F0.wireOp",EDGE,"E23.13.2"),sQuery(id+"F0.wireOp",EDGE,"E23.13.3"),sQuery(id+"F0.wireOp",EDGE,"E23.13.4"),sQuery(id+"F0.wireOp",EDGE,"E23.13.5"),sQuery(id+"F0.wireOp",EDGE,"E23.13.6"),sQuery(id+"F0.wireOp",EDGE,"E23.13.7"),sQuery(id+"F0.wireOp",EDGE,"E23.13.8"),sQuery(id+"F0.wireOp",EDGE,"E23.13.9"),sQuery(id+"F0.wireOp",EDGE,"E23.13.10"),sQuery(id+"F0.wireOp",EDGE,"E23.13.11"),sQuery(id+"F0.wireOp",EDGE,"E23.14.0"),sQuery(id+"F0.wireOp",EDGE,"E23.14.1"),sQuery(id+"F0.wireOp",EDGE,"E23.14.2"),sQuery(id+"F0.wireOp",EDGE,"E23.14.3"),sQuery(id+"F0.wireOp",EDGE,"E23.14.4"),sQuery(id+"F0.wireOp",EDGE,"E23.14.5"),sQuery(id+"F0.wireOp",EDGE,"E23.14.6"),sQuery(id+"F0.wireOp",EDGE,"E23.14.7"),sQuery(id+"F0.wireOp",EDGE,"E23.14.8"),sQuery(id+"F0.wireOp",EDGE,"E23.14.9"),sQuery(id+"F0.wireOp",EDGE,"E23.14.10"),sQuery(id+"F0.wireOp",EDGE,"E23.14.11"),sQuery(id+"F0.wireOp",EDGE,"E23.15.0"),sQuery(id+"F0.wireOp",EDGE,"E23.15.1"),sQuery(id+"F0.wireOp",EDGE,"E23.15.2"),sQuery(id+"F0.wireOp",EDGE,"E23.15.3"),sQuery(id+"F0.wireOp",EDGE,"E23.15.4"),sQuery(id+"F0.wireOp",EDGE,"E23.15.5"),sQuery(id+"F0.wireOp",EDGE,"E23.15.6"),sQuery(id+"F0.wireOp",EDGE,"E23.15.7"),sQuery(id+"F0.wireOp",EDGE,"E23.15.8"),sQuery(id+"F0.wireOp",EDGE,"E23.15.9"),sQuery(id+"F0.wireOp",EDGE,"E23.15.10"),sQuery(id+"F0.wireOp",EDGE,"E23.15.11"),sQuery(id+"F0.wireOp",EDGE,"E23.16.0"),sQuery(id+"F0.wireOp",EDGE,"E23.16.1"),sQuery(id+"F0.wireOp",EDGE,"E23.16.2"),sQuery(id+"F0.wireOp",EDGE,"E23.16.3"),sQuery(id+"F0.wireOp",EDGE,"E23.16.4"),sQuery(id+"F0.wireOp",EDGE,"E23.16.5"),sQuery(id+"F0.wireOp",EDGE,"E23.16.6"),sQuery(id+"F0.wireOp",EDGE,"E23.16.7"),sQuery(id+"F0.wireOp",EDGE,"E23.16.8"),sQuery(id+"F0.wireOp",EDGE,"E23.16.9"),sQuery(id+"F0.wireOp",EDGE,"E23.16.10"),sQuery(id+"F0.wireOp",EDGE,"E23.16.11"),sQuery(id+"F0.wireOp",EDGE,"E23.17.0"),sQuery(id+"F0.wireOp",EDGE,"E23.17.1"),sQuery(id+"F0.wireOp",EDGE,"E23.17.2"),sQuery(id+"F0.wireOp",EDGE,"E23.17.3"),sQuery(id+"F0.wireOp",EDGE,"E23.17.4"),sQuery(id+"F0.wireOp",EDGE,"E23.17.5"),sQuery(id+"F0.wireOp",EDGE,"E23.17.6"),sQuery(id+"F0.wireOp",EDGE,"E23.17.7"),sQuery(id+"F0.wireOp",EDGE,"E23.17.8"),sQuery(id+"F0.wireOp",EDGE,"E23.17.9"),sQuery(id+"F0.wireOp",EDGE,"E23.17.10"),sQuery(id+"F0.wireOp",EDGE,"E23.17.11"),sQuery(id+"F0.wireOp",EDGE,"E23.18.0"),sQuery(id+"F0.wireOp",EDGE,"E23.18.1"),sQuery(id+"F0.wireOp",EDGE,"E23.18.2"),sQuery(id+"F0.wireOp",EDGE,"E23.18.3"),sQuery(id+"F0.wireOp",EDGE,"E23.18.4"),sQuery(id+"F0.wireOp",EDGE,"E23.18.5"),sQuery(id+"F0.wireOp",EDGE,"E23.18.6"),sQuery(id+"F0.wireOp",EDGE,"E23.18.7"),sQuery(id+"F0.wireOp",EDGE,"E23.18.8"),sQuery(id+"F0.wireOp",EDGE,"E23.18.9"),sQuery(id+"F0.wireOp",EDGE,"E23.18.10"),sQuery(id+"F0.wireOp",EDGE,"E23.18.11"),sQuery(id+"F0.wireOp",EDGE,"E23.19.0"),sQuery(id+"F0.wireOp",EDGE,"E23.19.1"),sQuery(id+"F0.wireOp",EDGE,"E23.19.2"),sQuery(id+"F0.wireOp",EDGE,"E23.19.3"),sQuery(id+"F0.wireOp",EDGE,"E23.19.4"),sQuery(id+"F0.wireOp",EDGE,"E23.19.5"),sQuery(id+"F0.wireOp",EDGE,"E23.19.6"),sQuery(id+"F0.wireOp",EDGE,"E23.19.7"),sQuery(id+"F0.wireOp",EDGE,"E23.19.8"),sQuery(id+"F0.wireOp",EDGE,"E23.19.9"),sQuery(id+"F0.wireOp",EDGE,"E23.19.10"),sQuery(id+"F0.wireOp",EDGE,"E23.19.11"),sQuery(id+"F0.wireOp",EDGE,"E23.20.0"),sQuery(id+"F0.wireOp",EDGE,"E23.20.1"),sQuery(id+"F0.wireOp",EDGE,"E23.20.2"),sQuery(id+"F0.wireOp",EDGE,"E23.20.3"),sQuery(id+"F0.wireOp",EDGE,"E23.20.4"),sQuery(id+"F0.wireOp",EDGE,"E23.20.5"),sQuery(id+"F0.wireOp",EDGE,"E23.20.6"),sQuery(id+"F0.wireOp",EDGE,"E23.20.7"),sQuery(id+"F0.wireOp",EDGE,"E23.20.8"),sQuery(id+"F0.wireOp",EDGE,"E23.20.9"),sQuery(id+"F0.wireOp",EDGE,"E23.20.10"),sQuery(id+"F0.wireOp",EDGE,"E23.20.11"),sQuery(id+"F0.wireOp",EDGE,"E23.21.0"),sQuery(id+"F0.wireOp",EDGE,"E23.21.1"),sQuery(id+"F0.wireOp",EDGE,"E23.21.2"),sQuery(id+"F0.wireOp",EDGE,"E23.21.3"),sQuery(id+"F0.wireOp",EDGE,"E23.21.4"),sQuery(id+"F0.wireOp",EDGE,"E23.21.5"),sQuery(id+"F0.wireOp",EDGE,"E23.21.6"),sQuery(id+"F0.wireOp",EDGE,"E23.21.7"),sQuery(id+"F0.wireOp",EDGE,"E23.21.8"),sQuery(id+"F0.wireOp",EDGE,"E23.21.9"),sQuery(id+"F0.wireOp",EDGE,"E23.21.10"),sQuery(id+"F0.wireOp",EDGE,"E23.21.11"),sQuery(id+"F0.wireOp",EDGE,"E23.22.0"),sQuery(id+"F0.wireOp",EDGE,"E23.22.1"),sQuery(id+"F0.wireOp",EDGE,"E23.22.2"),sQuery(id+"F0.wireOp",EDGE,"E23.22.3"),sQuery(id+"F0.wireOp",EDGE,"E23.22.4"),sQuery(id+"F0.wireOp",EDGE,"E23.22.5"),sQuery(id+"F0.wireOp",EDGE,"E23.22.6"),sQuery(id+"F0.wireOp",EDGE,"E23.22.7"),sQuery(id+"F0.wireOp",EDGE,"E23.22.8"),sQuery(id+"F0.wireOp",EDGE,"E23.22.9"),sQuery(id+"F0.wireOp",EDGE,"E23.22.10"),sQuery(id+"F0.wireOp",EDGE,"E23.22.11"),sQuery(id+"F0.wireOp",EDGE,"E23.23.0"),sQuery(id+"F0.wireOp",EDGE,"E23.23.1"),sQuery(id+"F0.wireOp",EDGE,"E23.23.2"),sQuery(id+"F0.wireOp",EDGE,"E23.23.3"),sQuery(id+"F0.wireOp",EDGE,"E23.23.4"),sQuery(id+"F0.wireOp",EDGE,"E23.23.5"),sQuery(id+"F0.wireOp",EDGE,"E23.23.6"),sQuery(id+"F0.wireOp",EDGE,"E23.23.7"),sQuery(id+"F0.wireOp",EDGE,"E23.23.8"),sQuery(id+"F0.wireOp",EDGE,"E23.23.9"),sQuery(id+"F0.wireOp",EDGE,"E23.23.10"),sQuery(id+"F0.wireOp",EDGE,"E23.23.11"),sQuery(id+"F0.wireOp",EDGE,"E23.24.0"),sQuery(id+"F0.wireOp",EDGE,"E23.24.1"),sQuery(id+"F0.wireOp",EDGE,"E23.24.2"),sQuery(id+"F0.wireOp",EDGE,"E23.24.3"),sQuery(id+"F0.wireOp",EDGE,"E23.24.4"),sQuery(id+"F0.wireOp",EDGE,"E23.24.5"),sQuery(id+"F0.wireOp",EDGE,"E23.24.6"),sQuery(id+"F0.wireOp",EDGE,"E23.24.7"),sQuery(id+"F0.wireOp",EDGE,"E23.24.8"),sQuery(id+"F0.wireOp",EDGE,"E23.24.9"),sQuery(id+"F0.wireOp",EDGE,"E23.24.10"),sQuery(id+"F0.wireOp",EDGE,"E23.24.11"),sQuery(id+"F0.wireOp",EDGE,"E23.25.0"),sQuery(id+"F0.wireOp",EDGE,"E23.25.1"),sQuery(id+"F0.wireOp",EDGE,"E23.25.2"),sQuery(id+"F0.wireOp",EDGE,"E23.25.3"),sQuery(id+"F0.wireOp",EDGE,"E23.25.4"),sQuery(id+"F0.wireOp",EDGE,"E23.25.5"),sQuery(id+"F0.wireOp",EDGE,"E23.25.6"),sQuery(id+"F0.wireOp",EDGE,"E23.25.7"),sQuery(id+"F0.wireOp",EDGE,"E23.25.8"),sQuery(id+"F0.wireOp",EDGE,"E23.25.9"),sQuery(id+"F0.wireOp",EDGE,"E23.25.10"),sQuery(id+"F0.wireOp",EDGE,"E23.25.11"),sQuery(id+"F0.wireOp",EDGE,"E23.26.0"),sQuery(id+"F0.wireOp",EDGE,"E23.26.1"),sQuery(id+"F0.wireOp",EDGE,"E23.26.2"),sQuery(id+"F0.wireOp",EDGE,"E23.26.3"),sQuery(id+"F0.wireOp",EDGE,"E23.26.4"),sQuery(id+"F0.wireOp",EDGE,"E23.26.5"),sQuery(id+"F0.wireOp",EDGE,"E23.26.6"),sQuery(id+"F0.wireOp",EDGE,"E23.26.7"),sQuery(id+"F0.wireOp",EDGE,"E23.26.8"),sQuery(id+"F0.wireOp",EDGE,"E23.26.9"),sQuery(id+"F0.wireOp",EDGE,"E23.26.10"),sQuery(id+"F0.wireOp",EDGE,"E23.26.11"),sQuery(id+"F0.wireOp",EDGE,"E23.27.0"),sQuery(id+"F0.wireOp",EDGE,"E23.27.1"),sQuery(id+"F0.wireOp",EDGE,"E23.27.2"),sQuery(id+"F0.wireOp",EDGE,"E23.27.3"),sQuery(id+"F0.wireOp",EDGE,"E23.27.4"),sQuery(id+"F0.wireOp",EDGE,"E23.27.5"),sQuery(id+"F0.wireOp",EDGE,"E23.27.6"),sQuery(id+"F0.wireOp",EDGE,"E23.27.7"),sQuery(id+"F0.wireOp",EDGE,"E23.27.8"),sQuery(id+"F0.wireOp",EDGE,"E23.27.9"),sQuery(id+"F0.wireOp",EDGE,"E23.27.10"),sQuery(id+"F0.wireOp",EDGE,"E23.27.11"),sQuery(id+"F0.wireOp",EDGE,"E23.28.0"),sQuery(id+"F0.wireOp",EDGE,"E23.28.1"),sQuery(id+"F0.wireOp",EDGE,"E23.28.2"),sQuery(id+"F0.wireOp",EDGE,"E23.28.3"),sQuery(id+"F0.wireOp",EDGE,"E23.28.4"),sQuery(id+"F0.wireOp",EDGE,"E23.28.5"),sQuery(id+"F0.wireOp",EDGE,"E23.28.6"),sQuery(id+"F0.wireOp",EDGE,"E23.28.7"),sQuery(id+"F0.wireOp",EDGE,"E23.28.8"),sQuery(id+"F0.wireOp",EDGE,"E23.28.9"),sQuery(id+"F0.wireOp",EDGE,"E23.28.10"),sQuery(id+"F0.wireOp",EDGE,"E23.28.11"),sQuery(id+"F0.wireOp",EDGE,"E23.29.0"),sQuery(id+"F0.wireOp",EDGE,"E23.29.1"),sQuery(id+"F0.wireOp",EDGE,"E23.29.2"),sQuery(id+"F0.wireOp",EDGE,"E23.29.3"),sQuery(id+"F0.wireOp",EDGE,"E23.29.4"),sQuery(id+"F0.wireOp",EDGE,"E23.29.5"),sQuery(id+"F0.wireOp",EDGE,"E23.29.6"),sQuery(id+"F0.wireOp",EDGE,"E23.29.7"),sQuery(id+"F0.wireOp",EDGE,"E23.29.8"),sQuery(id+"F0.wireOp",EDGE,"E23.29.9"),sQuery(id+"F0.wireOp",EDGE,"E23.29.10"),sQuery(id+"F0.wireOp",EDGE,"E23.29.11"),sQuery(id+"F0.wireOp",EDGE,"E23.30.0"),sQuery(id+"F0.wireOp",EDGE,"E23.30.1"),sQuery(id+"F0.wireOp",EDGE,"E23.30.2"),sQuery(id+"F0.wireOp",EDGE,"E23.30.3"),sQuery(id+"F0.wireOp",EDGE,"E23.30.4"),sQuery(id+"F0.wireOp",EDGE,"E23.30.5"),sQuery(id+"F0.wireOp",EDGE,"E23.30.6"),sQuery(id+"F0.wireOp",EDGE,"E23.30.7"),sQuery(id+"F0.wireOp",EDGE,"E23.30.8"),sQuery(id+"F0.wireOp",EDGE,"E23.30.9"),sQuery(id+"F0.wireOp",EDGE,"E23.30.10"),sQuery(id+"F0.wireOp",EDGE,"E23.30.11"),sQuery(id+"F0.wireOp",EDGE,"E23.31.0"),sQuery(id+"F0.wireOp",EDGE,"E23.31.1"),sQuery(id+"F0.wireOp",EDGE,"E23.31.2"),sQuery(id+"F0.wireOp",EDGE,"E23.31.3"),sQuery(id+"F0.wireOp",EDGE,"E23.31.4"),sQuery(id+"F0.wireOp",EDGE,"E23.31.5"),sQuery(id+"F0.wireOp",EDGE,"E23.31.6"),sQuery(id+"F0.wireOp",EDGE,"E23.31.7"),sQuery(id+"F0.wireOp",EDGE,"E23.31.8"),sQuery(id+"F0.wireOp",EDGE,"E23.31.9"),sQuery(id+"F0.wireOp",EDGE,"E23.31.10"),sQuery(id+"F0.wireOp",EDGE,"E23.31.11"),sQuery(id+"F0.wireOp",EDGE,"E23.32.0"),sQuery(id+"F0.wireOp",EDGE,"E23.32.1"),sQuery(id+"F0.wireOp",EDGE,"E23.32.2"),sQuery(id+"F0.wireOp",EDGE,"E23.32.3"),sQuery(id+"F0.wireOp",EDGE,"E23.32.4"),sQuery(id+"F0.wireOp",EDGE,"E23.32.5"),sQuery(id+"F0.wireOp",EDGE,"E23.32.6"),sQuery(id+"F0.wireOp",EDGE,"E23.32.7"),sQuery(id+"F0.wireOp",EDGE,"E23.32.8"),sQuery(id+"F0.wireOp",EDGE,"E23.32.9"),sQuery(id+"F0.wireOp",EDGE,"E23.32.10"),sQuery(id+"F0.wireOp",EDGE,"E23.32.11"),sQuery(id+"F0.wireOp",EDGE,"E23.33.0"),sQuery(id+"F0.wireOp",EDGE,"E23.33.1"),sQuery(id+"F0.wireOp",EDGE,"E23.33.2"),sQuery(id+"F0.wireOp",EDGE,"E23.33.3"),sQuery(id+"F0.wireOp",EDGE,"E23.33.4"),sQuery(id+"F0.wireOp",EDGE,"E23.33.5"),sQuery(id+"F0.wireOp",EDGE,"E23.33.6"),sQuery(id+"F0.wireOp",EDGE,"E23.33.7"),sQuery(id+"F0.wireOp",EDGE,"E23.33.8"),sQuery(id+"F0.wireOp",EDGE,"E23.33.9"),sQuery(id+"F0.wireOp",EDGE,"E23.33.10"),sQuery(id+"F0.wireOp",EDGE,"E23.33.11"),sQuery(id+"F0.wireOp",EDGE,"E23.34.0"),sQuery(id+"F0.wireOp",EDGE,"E23.34.1"),sQuery(id+"F0.wireOp",EDGE,"E23.34.2"),sQuery(id+"F0.wireOp",EDGE,"E23.34.3"),sQuery(id+"F0.wireOp",EDGE,"E23.34.4"),sQuery(id+"F0.wireOp",EDGE,"E23.34.5"),sQuery(id+"F0.wireOp",EDGE,"E23.34.6"),sQuery(id+"F0.wireOp",EDGE,"E23.34.7"),sQuery(id+"F0.wireOp",EDGE,"E23.34.8"),sQuery(id+"F0.wireOp",EDGE,"E23.34.9"),sQuery(id+"F0.wireOp",EDGE,"E23.34.10"),sQuery(id+"F0.wireOp",EDGE,"E23.34.11"),sQuery(id+"F0.wireOp",EDGE,"E23.35.0"),sQuery(id+"F0.wireOp",EDGE,"E23.35.1"),sQuery(id+"F0.wireOp",EDGE,"E23.35.2"),sQuery(id+"F0.wireOp",EDGE,"E23.35.3"),sQuery(id+"F0.wireOp",EDGE,"E23.35.4"),sQuery(id+"F0.wireOp",EDGE,"E23.35.5"),sQuery(id+"F0.wireOp",EDGE,"E23.35.6"),sQuery(id+"F0.wireOp",EDGE,"E23.35.7"),sQuery(id+"F0.wireOp",EDGE,"E23.35.8"),sQuery(id+"F0.wireOp",EDGE,"E23.35.9"),sQuery(id+"F0.wireOp",EDGE,"E23.35.10"),sQuery(id+"F0.wireOp",EDGE,"E23.35.11"),sQuery(id+"F0.wireOp",EDGE,"E23.36.0"),sQuery(id+"F0.wireOp",EDGE,"E23.36.1"),sQuery(id+"F0.wireOp",EDGE,"E23.36.2"),sQuery(id+"F0.wireOp",EDGE,"E23.36.3"),sQuery(id+"F0.wireOp",EDGE,"E23.36.4"),sQuery(id+"F0.wireOp",EDGE,"E23.36.5"),sQuery(id+"F0.wireOp",EDGE,"E23.36.6"),sQuery(id+"F0.wireOp",EDGE,"E23.36.7"),sQuery(id+"F0.wireOp",EDGE,"E23.36.8"),sQuery(id+"F0.wireOp",EDGE,"E23.36.9"),sQuery(id+"F0.wireOp",EDGE,"E23.36.10"),sQuery(id+"F0.wireOp",EDGE,"E23.36.11"),sQuery(id+"F0.wireOp",EDGE,"E23.37.0"),sQuery(id+"F0.wireOp",EDGE,"E23.37.1"),sQuery(id+"F0.wireOp",EDGE,"E23.37.2"),sQuery(id+"F0.wireOp",EDGE,"E23.37.3"),sQuery(id+"F0.wireOp",EDGE,"E23.37.4"),sQuery(id+"F0.wireOp",EDGE,"E23.37.5"),sQuery(id+"F0.wireOp",EDGE,"E23.37.6"),sQuery(id+"F0.wireOp",EDGE,"E23.37.7"),sQuery(id+"F0.wireOp",EDGE,"E23.37.8"),sQuery(id+"F0.wireOp",EDGE,"E23.37.9"),sQuery(id+"F0.wireOp",EDGE,"E23.37.10"),sQuery(id+"F0.wireOp",EDGE,"E23.37.11"),sQuery(id+"F0.wireOp",EDGE,"E23.38.0"),sQuery(id+"F0.wireOp",EDGE,"E23.38.1"),sQuery(id+"F0.wireOp",EDGE,"E23.38.2"),sQuery(id+"F0.wireOp",EDGE,"E23.38.3"),sQuery(id+"F0.wireOp",EDGE,"E23.38.4"),sQuery(id+"F0.wireOp",EDGE,"E23.38.5"),sQuery(id+"F0.wireOp",EDGE,"E23.38.6"),sQuery(id+"F0.wireOp",EDGE,"E23.38.7"),sQuery(id+"F0.wireOp",EDGE,"E23.38.8"),sQuery(id+"F0.wireOp",EDGE,"E23.38.9"),sQuery(id+"F0.wireOp",EDGE,"E23.38.10"),sQuery(id+"F0.wireOp",EDGE,"E23.38.11"),sQuery(id+"F0.wireOp",EDGE,"E23.39.0"),sQuery(id+"F0.wireOp",EDGE,"E23.39.1"),sQuery(id+"F0.wireOp",EDGE,"E23.39.2"),sQuery(id+"F0.wireOp",EDGE,"E23.39.3"),sQuery(id+"F0.wireOp",EDGE,"E23.39.4"),sQuery(id+"F0.wireOp",EDGE,"E23.39.5"),sQuery(id+"F0.wireOp",EDGE,"E23.39.6"),sQuery(id+"F0.wireOp",EDGE,"E23.39.7"),sQuery(id+"F0.wireOp",EDGE,"E23.39.8"),sQuery(id+"F0.wireOp",EDGE,"E23.39.9"),sQuery(id+"F0.wireOp",EDGE,"E23.39.10"),sQuery(id+"F0.wireOp",EDGE,"E23.39.11"),sQuery(id+"F0.wireOp",EDGE,"E23.40.0"),sQuery(id+"F0.wireOp",EDGE,"E23.40.1"),sQuery(id+"F0.wireOp",EDGE,"E23.40.2"),sQuery(id+"F0.wireOp",EDGE,"E23.40.3"),sQuery(id+"F0.wireOp",EDGE,"E23.40.4"),sQuery(id+"F0.wireOp",EDGE,"E23.40.5"),sQuery(id+"F0.wireOp",EDGE,"E23.40.6"),sQuery(id+"F0.wireOp",EDGE,"E23.40.7"),sQuery(id+"F0.wireOp",EDGE,"E23.40.8"),sQuery(id+"F0.wireOp",EDGE,"E23.40.9"),sQuery(id+"F0.wireOp",EDGE,"E23.40.10"),sQuery(id+"F0.wireOp",EDGE,"E23.40.11"),sQuery(id+"F0.wireOp",EDGE,"E23.41.0"),sQuery(id+"F0.wireOp",EDGE,"E23.41.1"),sQuery(id+"F0.wireOp",EDGE,"E23.41.2"),sQuery(id+"F0.wireOp",EDGE,"E23.41.3"),sQuery(id+"F0.wireOp",EDGE,"E23.41.4"),sQuery(id+"F0.wireOp",EDGE,"E23.41.5"),sQuery(id+"F0.wireOp",EDGE,"E23.41.6"),sQuery(id+"F0.wireOp",EDGE,"E23.41.7"),sQuery(id+"F0.wireOp",EDGE,"E23.41.8"),sQuery(id+"F0.wireOp",EDGE,"E23.41.9"),sQuery(id+"F0.wireOp",EDGE,"E23.41.10"),sQuery(id+"F0.wireOp",EDGE,"E23.41.11"),sQuery(id+"F0.wireOp",EDGE,"E23.42.0"),sQuery(id+"F0.wireOp",EDGE,"E23.42.1"),sQuery(id+"F0.wireOp",EDGE,"E23.42.2"),sQuery(id+"F0.wireOp",EDGE,"E23.42.3"),sQuery(id+"F0.wireOp",EDGE,"E23.42.4"),sQuery(id+"F0.wireOp",EDGE,"E23.42.5"),sQuery(id+"F0.wireOp",EDGE,"E23.42.6"),sQuery(id+"F0.wireOp",EDGE,"E23.42.7"),sQuery(id+"F0.wireOp",EDGE,"E23.42.8"),sQuery(id+"F0.wireOp",EDGE,"E23.42.9"),sQuery(id+"F0.wireOp",EDGE,"E23.42.10"),sQuery(id+"F0.wireOp",EDGE,"E23.42.11"),sQuery(id+"F0.wireOp",EDGE,"E23.43.0"),sQuery(id+"F0.wireOp",EDGE,"E23.43.1"),sQuery(id+"F0.wireOp",EDGE,"E23.43.2"),sQuery(id+"F0.wireOp",EDGE,"E23.43.3"),sQuery(id+"F0.wireOp",EDGE,"E23.43.4"),sQuery(id+"F0.wireOp",EDGE,"E23.43.5"),sQuery(id+"F0.wireOp",EDGE,"E23.43.6"),sQuery(id+"F0.wireOp",EDGE,"E23.43.7"),sQuery(id+"F0.wireOp",EDGE,"E23.43.8"),sQuery(id+"F0.wireOp",EDGE,"E23.43.9"),sQuery(id+"F0.wireOp",EDGE,"E23.43.10"),sQuery(id+"F0.wireOp",EDGE,"E23.43.11"),sQuery(id+"F0.wireOp",EDGE,"E23.44.0"),sQuery(id+"F0.wireOp",EDGE,"E23.44.1"),sQuery(id+"F0.wireOp",EDGE,"E23.44.2"),sQuery(id+"F0.wireOp",EDGE,"E23.44.3"),sQuery(id+"F0.wireOp",EDGE,"E23.44.4"),sQuery(id+"F0.wireOp",EDGE,"E23.44.5"),sQuery(id+"F0.wireOp",EDGE,"E23.44.6"),sQuery(id+"F0.wireOp",EDGE,"E23.44.7"),sQuery(id+"F0.wireOp",EDGE,"E23.44.8"),sQuery(id+"F0.wireOp",EDGE,"E23.44.9"),sQuery(id+"F0.wireOp",EDGE,"E23.44.10"),sQuery(id+"F0.wireOp",EDGE,"E23.44.11"),sQuery(id+"F0.wireOp",EDGE,"E23.45.0"),sQuery(id+"F0.wireOp",EDGE,"E23.45.1"),sQuery(id+"F0.wireOp",EDGE,"E23.45.2"),sQuery(id+"F0.wireOp",EDGE,"E23.45.3"),sQuery(id+"F0.wireOp",EDGE,"E23.45.4"),sQuery(id+"F0.wireOp",EDGE,"E23.45.5"),sQuery(id+"F0.wireOp",EDGE,"E23.45.6"),sQuery(id+"F0.wireOp",EDGE,"E23.45.7"),sQuery(id+"F0.wireOp",EDGE,"E23.45.8"),sQuery(id+"F0.wireOp",EDGE,"E23.45.9"),sQuery(id+"F0.wireOp",EDGE,"E23.45.10"),sQuery(id+"F0.wireOp",EDGE,"E23.45.11"),sQuery(id+"F0.wireOp",EDGE,"E23.46.0"),sQuery(id+"F0.wireOp",EDGE,"E23.46.1"),sQuery(id+"F0.wireOp",EDGE,"E23.46.2"),sQuery(id+"F0.wireOp",EDGE,"E23.46.3"),sQuery(id+"F0.wireOp",EDGE,"E23.46.4"),sQuery(id+"F0.wireOp",EDGE,"E23.46.5"),sQuery(id+"F0.wireOp",EDGE,"E23.46.6"),sQuery(id+"F0.wireOp",EDGE,"E23.46.7"),sQuery(id+"F0.wireOp",EDGE,"E23.46.8"),sQuery(id+"F0.wireOp",EDGE,"E23.46.9"),sQuery(id+"F0.wireOp",EDGE,"E23.46.10"),sQuery(id+"F0.wireOp",EDGE,"E23.46.11"),sQuery(id+"F0.wireOp",EDGE,"E23.47.0"),sQuery(id+"F0.wireOp",EDGE,"E23.47.1"),sQuery(id+"F0.wireOp",EDGE,"E23.47.2"),sQuery(id+"F0.wireOp",EDGE,"E23.47.3"),sQuery(id+"F0.wireOp",EDGE,"E23.47.4"),sQuery(id+"F0.wireOp",EDGE,"E23.47.5"),sQuery(id+"F0.wireOp",EDGE,"E23.47.6"),sQuery(id+"F0.wireOp",EDGE,"E23.47.7"),sQuery(id+"F0.wireOp",EDGE,"E23.47.8"),sQuery(id+"F0.wireOp",EDGE,"E23.47.9"),sQuery(id+"F0.wireOp",EDGE,"E23.47.10"),sQuery(id+"F0.wireOp",EDGE,"E23.47.11"),sQuery(id+"F0.wireOp",EDGE,"E23.48.0"),sQuery(id+"F0.wireOp",EDGE,"E23.48.1"),sQuery(id+"F0.wireOp",EDGE,"E23.48.2"),sQuery(id+"F0.wireOp",EDGE,"E23.48.3"),sQuery(id+"F0.wireOp",EDGE,"E23.48.4"),sQuery(id+"F0.wireOp",EDGE,"E23.48.5"),sQuery(id+"F0.wireOp",EDGE,"E23.48.6"),sQuery(id+"F0.wireOp",EDGE,"E23.48.7"),sQuery(id+"F0.wireOp",EDGE,"E23.48.8"),sQuery(id+"F0.wireOp",EDGE,"E23.48.9"),sQuery(id+"F0.wireOp",EDGE,"E23.48.10"),sQuery(id+"F0.wireOp",EDGE,"E23.48.11"),sQuery(id+"F0.wireOp",EDGE,"E23.49.0"),sQuery(id+"F0.wireOp",EDGE,"E23.49.1"),sQuery(id+"F0.wireOp",EDGE,"E23.49.2"),sQuery(id+"F0.wireOp",EDGE,"E23.49.3"),sQuery(id+"F0.wireOp",EDGE,"E23.49.4"),sQuery(id+"F0.wireOp",EDGE,"E23.49.5"),sQuery(id+"F0.wireOp",EDGE,"E23.49.6"),sQuery(id+"F0.wireOp",EDGE,"E23.49.7"),sQuery(id+"F0.wireOp",EDGE,"E23.49.8"),sQuery(id+"F0.wireOp",EDGE,"E23.49.9"),sQuery(id+"F0.wireOp",EDGE,"E23.49.10"),sQuery(id+"F0.wireOp",EDGE,"E23.49.11"),sQuery(id+"F0.wireOp",EDGE,"E23.50.0"),sQuery(id+"F0.wireOp",EDGE,"E23.50.1"),sQuery(id+"F0.wireOp",EDGE,"E23.50.2"),sQuery(id+"F0.wireOp",EDGE,"E23.50.3"),sQuery(id+"F0.wireOp",EDGE,"E23.50.4"),sQuery(id+"F0.wireOp",EDGE,"E23.50.5"),sQuery(id+"F0.wireOp",EDGE,"E23.50.6"),sQuery(id+"F0.wireOp",EDGE,"E23.50.7"),sQuery(id+"F0.wireOp",EDGE,"E23.50.8"),sQuery(id+"F0.wireOp",EDGE,"E23.50.9"),sQuery(id+"F0.wireOp",EDGE,"E23.50.10"),sQuery(id+"F0.wireOp",EDGE,"E23.50.11"),sQuery(id+"F0.wireOp",EDGE,"E23.51.0"),sQuery(id+"F0.wireOp",EDGE,"E23.51.1"),sQuery(id+"F0.wireOp",EDGE,"E23.51.2"),sQuery(id+"F0.wireOp",EDGE,"E23.51.3"),sQuery(id+"F0.wireOp",EDGE,"E23.51.4"),sQuery(id+"F0.wireOp",EDGE,"E23.51.5"),sQuery(id+"F0.wireOp",EDGE,"E23.51.6"),sQuery(id+"F0.wireOp",EDGE,"E23.51.7"),sQuery(id+"F0.wireOp",EDGE,"E23.51.8"),sQuery(id+"F0.wireOp",EDGE,"E23.51.9"),sQuery(id+"F0.wireOp",EDGE,"E23.51.10"),sQuery(id+"F0.wireOp",EDGE,"E23.51.11"),sQuery(id+"F0.wireOp",EDGE,"E23.52.0"),sQuery(id+"F0.wireOp",EDGE,"E23.52.1"),sQuery(id+"F0.wireOp",EDGE,"E23.52.2"),sQuery(id+"F0.wireOp",EDGE,"E23.52.3"),sQuery(id+"F0.wireOp",EDGE,"E23.52.4"),sQuery(id+"F0.wireOp",EDGE,"E23.52.5"),sQuery(id+"F0.wireOp",EDGE,"E23.52.6"),sQuery(id+"F0.wireOp",EDGE,"E23.52.7"),sQuery(id+"F0.wireOp",EDGE,"E23.52.8"),sQuery(id+"F0.wireOp",EDGE,"E23.52.9"),sQuery(id+"F0.wireOp",EDGE,"E23.52.10"),sQuery(id+"F0.wireOp",EDGE,"E23.52.11"),sQuery(id+"F0.wireOp",EDGE,"E23.53.0"),sQuery(id+"F0.wireOp",EDGE,"E23.53.1"),sQuery(id+"F0.wireOp",EDGE,"E23.53.2"),sQuery(id+"F0.wireOp",EDGE,"E23.53.3"),sQuery(id+"F0.wireOp",EDGE,"E23.53.4"),sQuery(id+"F0.wireOp",EDGE,"E23.53.5"),sQuery(id+"F0.wireOp",EDGE,"E23.53.6"),sQuery(id+"F0.wireOp",EDGE,"E23.53.7"),sQuery(id+"F0.wireOp",EDGE,"E23.53.8"),sQuery(id+"F0.wireOp",EDGE,"E23.53.9"),sQuery(id+"F0.wireOp",EDGE,"E23.53.10"),sQuery(id+"F0.wireOp",EDGE,"E23.53.11"),sQuery(id+"F0.wireOp",EDGE,"E23.54.0"),sQuery(id+"F0.wireOp",EDGE,"E23.54.1"),sQuery(id+"F0.wireOp",EDGE,"E23.54.2"),sQuery(id+"F0.wireOp",EDGE,"E23.54.3"),sQuery(id+"F0.wireOp",EDGE,"E23.54.4"),sQuery(id+"F0.wireOp",EDGE,"E23.54.5"),sQuery(id+"F0.wireOp",EDGE,"E23.54.6"),sQuery(id+"F0.wireOp",EDGE,"E23.54.7"),sQuery(id+"F0.wireOp",EDGE,"E23.54.8"),sQuery(id+"F0.wireOp",EDGE,"E23.54.9"),sQuery(id+"F0.wireOp",EDGE,"E23.54.10"),sQuery(id+"F0.wireOp",EDGE,"E23.54.11"),sQuery(id+"F0.wireOp",EDGE,"E23.55.0"),sQuery(id+"F0.wireOp",EDGE,"E23.55.1"),sQuery(id+"F0.wireOp",EDGE,"E23.55.2"),sQuery(id+"F0.wireOp",EDGE,"E23.55.3"),sQuery(id+"F0.wireOp",EDGE,"E23.55.4"),sQuery(id+"F0.wireOp",EDGE,"E23.55.5"),sQuery(id+"F0.wireOp",EDGE,"E23.55.6"),sQuery(id+"F0.wireOp",EDGE,"E23.55.7"),sQuery(id+"F0.wireOp",EDGE,"E23.55.8"),sQuery(id+"F0.wireOp",EDGE,"E23.55.9"),sQuery(id+"F0.wireOp",EDGE,"E23.55.10"),sQuery(id+"F0.wireOp",EDGE,"E23.55.11"),sQuery(id+"F0.wireOp",EDGE,"E23.56.0"),sQuery(id+"F0.wireOp",EDGE,"E23.56.1"),sQuery(id+"F0.wireOp",EDGE,"E23.56.2"),sQuery(id+"F0.wireOp",EDGE,"E23.56.3"),sQuery(id+"F0.wireOp",EDGE,"E23.56.4"),sQuery(id+"F0.wireOp",EDGE,"E23.56.5"),sQuery(id+"F0.wireOp",EDGE,"E23.56.6"),sQuery(id+"F0.wireOp",EDGE,"E23.56.7"),sQuery(id+"F0.wireOp",EDGE,"E23.56.8"),sQuery(id+"F0.wireOp",EDGE,"E23.56.9"),sQuery(id+"F0.wireOp",EDGE,"E23.56.10"),sQuery(id+"F0.wireOp",EDGE,"E23.56.11"),sQuery(id+"F0.wireOp",EDGE,"E23.57.0"),sQuery(id+"F0.wireOp",EDGE,"E23.57.1"),sQuery(id+"F0.wireOp",EDGE,"E23.57.2"),sQuery(id+"F0.wireOp",EDGE,"E23.57.3"),sQuery(id+"F0.wireOp",EDGE,"E23.57.4"),sQuery(id+"F0.wireOp",EDGE,"E23.57.5"),sQuery(id+"F0.wireOp",EDGE,"E23.57.6"),sQuery(id+"F0.wireOp",EDGE,"E23.57.7"),sQuery(id+"F0.wireOp",EDGE,"E23.57.8"),sQuery(id+"F0.wireOp",EDGE,"E23.57.9"),sQuery(id+"F0.wireOp",EDGE,"E23.57.10"),sQuery(id+"F0.wireOp",EDGE,"E23.57.11"),sQuery(id+"F0.wireOp",EDGE,"E23.58.0"),sQuery(id+"F0.wireOp",EDGE,"E23.58.1"),sQuery(id+"F0.wireOp",EDGE,"E23.58.2"),sQuery(id+"F0.wireOp",EDGE,"E23.58.3"),sQuery(id+"F0.wireOp",EDGE,"E23.58.4"),sQuery(id+"F0.wireOp",EDGE,"E23.58.5"),sQuery(id+"F0.wireOp",EDGE,"E23.58.6"),sQuery(id+"F0.wireOp",EDGE,"E23.58.7"),sQuery(id+"F0.wireOp",EDGE,"E23.58.8"),sQuery(id+"F0.wireOp",EDGE,"E23.58.9"),sQuery(id+"F0.wireOp",EDGE,"E23.58.10"),sQuery(id+"F0.wireOp",EDGE,"E23.58.11"),sQuery(id+"F0.wireOp",EDGE,"E23.59.0"),sQuery(id+"F0.wireOp",EDGE,"E23.59.1"),sQuery(id+"F0.wireOp",EDGE,"E23.59.2"),sQuery(id+"F0.wireOp",EDGE,"E23.59.3"),sQuery(id+"F0.wireOp",EDGE,"E23.59.4"),sQuery(id+"F0.wireOp",EDGE,"E23.59.5"),sQuery(id+"F0.wireOp",EDGE,"E23.59.6"),sQuery(id+"F0.wireOp",EDGE,"E23.59.7"),sQuery(id+"F0.wireOp",EDGE,"E23.59.8"),sQuery(id+"F0.wireOp",EDGE,"E23.59.9"),sQuery(id+"F0.wireOp",EDGE,"E23.59.10"),sQuery(id+"F0.wireOp",EDGE,"E23.59.11"),sQuery(id+"F0.wireOp",EDGE,"E23.60.0"),sQuery(id+"F0.wireOp",EDGE,"E23.60.1"),sQuery(id+"F0.wireOp",EDGE,"E23.60.2"),sQuery(id+"F0.wireOp",EDGE,"E23.60.3"),sQuery(id+"F0.wireOp",EDGE,"E23.60.4"),sQuery(id+"F0.wireOp",EDGE,"E23.60.5"),sQuery(id+"F0.wireOp",EDGE,"E23.60.6"),sQuery(id+"F0.wireOp",EDGE,"E23.60.7"),sQuery(id+"F0.wireOp",EDGE,"E23.60.8"),sQuery(id+"F0.wireOp",EDGE,"E23.60.9"),sQuery(id+"F0.wireOp",EDGE,"E23.60.10"),sQuery(id+"F0.wireOp",EDGE,"E23.60.11"),sQuery(id+"F0.wireOp",EDGE,"E23.61.0"),sQuery(id+"F0.wireOp",EDGE,"E23.61.1"),sQuery(id+"F0.wireOp",EDGE,"E23.61.2"),sQuery(id+"F0.wireOp",EDGE,"E23.61.3"),sQuery(id+"F0.wireOp",EDGE,"E23.61.4"),sQuery(id+"F0.wireOp",EDGE,"E23.61.5"),sQuery(id+"F0.wireOp",EDGE,"E23.61.6"),sQuery(id+"F0.wireOp",EDGE,"E23.61.7"),sQuery(id+"F0.wireOp",EDGE,"E23.61.8"),sQuery(id+"F0.wireOp",EDGE,"E23.61.9"),sQuery(id+"F0.wireOp",EDGE,"E23.61.10"),sQuery(id+"F0.wireOp",EDGE,"E23.61.11"),sQuery(id+"F0.wireOp",EDGE,"E23.62.0"),sQuery(id+"F0.wireOp",EDGE,"E23.62.1"),sQuery(id+"F0.wireOp",EDGE,"E23.62.2"),sQuery(id+"F0.wireOp",EDGE,"E23.62.3"),sQuery(id+"F0.wireOp",EDGE,"E23.62.4"),sQuery(id+"F0.wireOp",EDGE,"E23.62.5"),sQuery(id+"F0.wireOp",EDGE,"E23.62.6"),sQuery(id+"F0.wireOp",EDGE,"E23.62.7"),sQuery(id+"F0.wireOp",EDGE,"E23.62.8"),sQuery(id+"F0.wireOp",EDGE,"E23.62.9"),sQuery(id+"F0.wireOp",EDGE,"E23.62.10"),sQuery(id+"F0.wireOp",EDGE,"E23.62.11"),sQuery(id+"F0.wireOp",EDGE,"E23.63.0"),sQuery(id+"F0.wireOp",EDGE,"E23.63.1"),sQuery(id+"F0.wireOp",EDGE,"E23.63.2"),sQuery(id+"F0.wireOp",EDGE,"E23.63.3"),sQuery(id+"F0.wireOp",EDGE,"E23.63.4"),sQuery(id+"F0.wireOp",EDGE,"E23.63.5"),sQuery(id+"F0.wireOp",EDGE,"E23.63.6"),sQuery(id+"F0.wireOp",EDGE,"E23.63.7"),sQuery(id+"F0.wireOp",EDGE,"E23.63.8"),sQuery(id+"F0.wireOp",EDGE,"E23.63.9"),sQuery(id+"F0.wireOp",EDGE,"E23.63.10"),sQuery(id+"F0.wireOp",EDGE,"E23.63.11"),sQuery(id+"F0.wireOp",EDGE,"E23.64.0"),sQuery(id+"F0.wireOp",EDGE,"E23.64.1"),sQuery(id+"F0.wireOp",EDGE,"E23.64.2"),sQuery(id+"F0.wireOp",EDGE,"E23.64.3"),sQuery(id+"F0.wireOp",EDGE,"E23.64.4"),sQuery(id+"F0.wireOp",EDGE,"E23.64.5"),sQuery(id+"F0.wireOp",EDGE,"E23.64.6"),sQuery(id+"F0.wireOp",EDGE,"E23.64.7"),sQuery(id+"F0.wireOp",EDGE,"E23.64.8"),sQuery(id+"F0.wireOp",EDGE,"E23.64.9"),sQuery(id+"F0.wireOp",EDGE,"E23.64.10"),sQuery(id+"F0.wireOp",EDGE,"E23.64.11"),sQuery(id+"F0.wireOp",EDGE,"E23.65.0"),sQuery(id+"F0.wireOp",EDGE,"E23.65.1"),sQuery(id+"F0.wireOp",EDGE,"E23.65.2"),sQuery(id+"F0.wireOp",EDGE,"E23.65.3"),sQuery(id+"F0.wireOp",EDGE,"E23.65.4"),sQuery(id+"F0.wireOp",EDGE,"E23.65.5"),sQuery(id+"F0.wireOp",EDGE,"E23.65.6"),sQuery(id+"F0.wireOp",EDGE,"E23.65.7"),sQuery(id+"F0.wireOp",EDGE,"E23.65.8"),sQuery(id+"F0.wireOp",EDGE,"E23.65.9"),sQuery(id+"F0.wireOp",EDGE,"E23.65.10"),sQuery(id+"F0.wireOp",EDGE,"E23.65.11"),sQuery(id+"F0.wireOp",EDGE,"E23.66.0"),sQuery(id+"F0.wireOp",EDGE,"E23.66.1"),sQuery(id+"F0.wireOp",EDGE,"E23.66.2"),sQuery(id+"F0.wireOp",EDGE,"E23.66.3"),sQuery(id+"F0.wireOp",EDGE,"E23.66.4"),sQuery(id+"F0.wireOp",EDGE,"E23.66.5"),sQuery(id+"F0.wireOp",EDGE,"E23.66.6"),sQuery(id+"F0.wireOp",EDGE,"E23.66.7"),sQuery(id+"F0.wireOp",EDGE,"E23.66.8"),sQuery(id+"F0.wireOp",EDGE,"E23.66.9"),sQuery(id+"F0.wireOp",EDGE,"E23.66.10"),sQuery(id+"F0.wireOp",EDGE,"E23.66.11"),sQuery(id+"F0.wireOp",EDGE,"E23.67.0"),sQuery(id+"F0.wireOp",EDGE,"E23.67.1"),sQuery(id+"F0.wireOp",EDGE,"E23.67.2"),sQuery(id+"F0.wireOp",EDGE,"E23.67.3"),sQuery(id+"F0.wireOp",EDGE,"E23.67.4"),sQuery(id+"F0.wireOp",EDGE,"E23.67.5"),sQuery(id+"F0.wireOp",EDGE,"E23.67.6"),sQuery(id+"F0.wireOp",EDGE,"E23.67.7"),sQuery(id+"F0.wireOp",EDGE,"E23.67.8"),sQuery(id+"F0.wireOp",EDGE,"E23.67.9"),sQuery(id+"F0.wireOp",EDGE,"E23.67.10"),sQuery(id+"F0.wireOp",EDGE,"E23.67.11"),sQuery(id+"F0.wireOp",EDGE,"E23.68.0"),sQuery(id+"F0.wireOp",EDGE,"E23.68.1"),sQuery(id+"F0.wireOp",EDGE,"E23.68.2"),sQuery(id+"F0.wireOp",EDGE,"E23.68.3"),sQuery(id+"F0.wireOp",EDGE,"E23.68.4"),sQuery(id+"F0.wireOp",EDGE,"E23.68.5"),sQuery(id+"F0.wireOp",EDGE,"E23.68.6"),sQuery(id+"F0.wireOp",EDGE,"E23.68.7"),sQuery(id+"F0.wireOp",EDGE,"E23.68.8"),sQuery(id+"F0.wireOp",EDGE,"E23.68.9"),sQuery(id+"F0.wireOp",EDGE,"E23.68.10"),sQuery(id+"F0.wireOp",EDGE,"E23.68.11"),sQuery(id+"F0.wireOp",EDGE,"E23.69.0"),sQuery(id+"F0.wireOp",EDGE,"E23.69.1"),sQuery(id+"F0.wireOp",EDGE,"E23.69.2"),sQuery(id+"F0.wireOp",EDGE,"E23.69.3"),sQuery(id+"F0.wireOp",EDGE,"E23.69.4"),sQuery(id+"F0.wireOp",EDGE,"E23.69.5"),sQuery(id+"F0.wireOp",EDGE,"E23.69.6"),sQuery(id+"F0.wireOp",EDGE,"E23.69.7"),sQuery(id+"F0.wireOp",EDGE,"E23.69.8"),sQuery(id+"F0.wireOp",EDGE,"E23.69.9"),sQuery(id+"F0.wireOp",EDGE,"E23.69.10"),sQuery(id+"F0.wireOp",EDGE,"E23.69.11"),sQuery(id+"F0.wireOp",EDGE,"E23.70.0"),sQuery(id+"F0.wireOp",EDGE,"E23.70.1"),sQuery(id+"F0.wireOp",EDGE,"E23.70.2"),sQuery(id+"F0.wireOp",EDGE,"E23.70.3"),sQuery(id+"F0.wireOp",EDGE,"E23.70.4"),sQuery(id+"F0.wireOp",EDGE,"E23.70.5"),sQuery(id+"F0.wireOp",EDGE,"E23.70.6"),sQuery(id+"F0.wireOp",EDGE,"E23.70.7"),sQuery(id+"F0.wireOp",EDGE,"E23.70.8"),sQuery(id+"F0.wireOp",EDGE,"E23.70.9"),sQuery(id+"F0.wireOp",EDGE,"E23.70.10"),sQuery(id+"F0.wireOp",EDGE,"E23.70.11"),sQuery(id+"F0.wireOp",EDGE,"E23.71.0"),sQuery(id+"F0.wireOp",EDGE,"E23.71.1"),sQuery(id+"F0.wireOp",EDGE,"E23.71.2"),sQuery(id+"F0.wireOp",EDGE,"E23.71.3"),sQuery(id+"F0.wireOp",EDGE,"E23.71.4"),sQuery(id+"F0.wireOp",EDGE,"E23.71.5"),sQuery(id+"F0.wireOp",EDGE,"E23.71.6"),sQuery(id+"F0.wireOp",EDGE,"E23.71.7"),sQuery(id+"F0.wireOp",EDGE,"E23.71.8"),sQuery(id+"F0.wireOp",EDGE,"E23.71.9"),sQuery(id+"F0.wireOp",EDGE,"E23.71.10"),sQuery(id+"F0.wireOp",EDGE,"E23.71.11"),sQuery(id+"F0.wireOp",EDGE,"E24.trimOffspring"),sQuery(id+"F0.wireOp",EDGE,"E25.trimOffspring"),sQuery(id+"F0.wireOp",EDGE,"E26.trimOffspring"),sQuery(id+"F0.wireOp",EDGE,"E27.trimOffspring"),sQuery(id+"F0.wireOp",EDGE,"E28.trimOffspring"),sQuery(id+"F0.wireOp",EDGE,"E29.trimOffspring"),sQuery(id+"F0.wireOp",EDGE,"E30.trimOffspring"),sQuery(id+"F0.wireOp",EDGE,"E31.trimOffspring"),sQuery(id+"F0.wireOp",EDGE,"E32.trimOffspring"),sQuery(id+"F0.wireOp",EDGE,"E33.trimOffspring"),sQuery(id+"F0.wireOp",EDGE,"E34.trimOffspring"),sQuery(id+"F0.wireOp",EDGE,"E35.trimOffspring"),sQuery(id+"F0.wireOp",EDGE,"E36.trimOffspring"),sQuery(id+"F0.wireOp",EDGE,"E37.trimOffspring"),sQuery(id+"F0.wireOp",EDGE,"E38.trimOffspring"),sQuery(id+"F0.wireOp",EDGE,"E39.trimOffspring"),sQuery(id+"F0.wireOp",EDGE,"E40.trimOffspring"),sQuery(id+"F0.wireOp",EDGE,"E41.trimOffspring"),sQuery(id+"F0.wireOp",EDGE,"E42.trimOffspring"),sQuery(id+"F0.wireOp",EDGE,"E43.trimOffspring"),sQuery(id+"F0.wireOp",EDGE,"E44.trimOffspring"),sQuery(id+"F0.wireOp",EDGE,"E45.trimOffspring"),sQuery(id+"F0.wireOp",EDGE,"E46.trimOffspring"),sQuery(id+"F0.wireOp",EDGE,"E47.trimOffspring"),sQuery(id+"F0.wireOp",EDGE,"E48.trimOffspring"),sQuery(id+"F0.wireOp",EDGE,"E49.trimOffspring"),sQuery(id+"F0.wireOp",EDGE,"E50.trimOffspring"),sQuery(id+"F0.wireOp",EDGE,"E51.trimOffspring"),sQuery(id+"F0.wireOp",EDGE,"E52.trimOffspring"),sQuery(id+"F0.wireOp",EDGE,"E53.trimOffspring"),sQuery(id+"F0.wireOp",EDGE,"E54.trimOffspring"),sQuery(id+"F0.wireOp",EDGE,"E55.trimOffspring"),sQuery(id+"F0.wireOp",EDGE,"E56.trimOffspring"),sQuery(id+"F0.wireOp",EDGE,"E57.trimOffspring"),sQuery(id+"F0.wireOp",EDGE,"E58.trimOffspring"),sQuery(id+"F0.wireOp",EDGE,"E59.trimOffspring"),sQuery(id+"F0.wireOp",EDGE,"E60.trimOffspring"),sQuery(id+"F0.wireOp",EDGE,"E61.trimOffspring"),sQuery(id+"F0.wireOp",EDGE,"E62.trimOffspring"),sQuery(id+"F0.wireOp",EDGE,"E63.trimOffspring"),sQuery(id+"F0.wireOp",EDGE,"E64.trimOffspring"),sQuery(id+"F0.wireOp",EDGE,"E65.trimOffspring"),sQuery(id+"F0.wireOp",EDGE,"E66.trimOffspring"),sQuery(id+"F0.wireOp",EDGE,"E67.trimOffspring"),sQuery(id+"F0.wireOp",EDGE,"E68.trimOffspring"),sQuery(id+"F0.wireOp",EDGE,"E69.trimOffspring"),sQuery(id+"F0.wireOp",EDGE,"E70.trimOffspring"),sQuery(id+"F0.wireOp",EDGE,"E71.trimOffspring"),sQuery(id+"F0.wireOp",EDGE,"E72.trimOffspring"),sQuery(id+"F0.wireOp",EDGE,"E73.trimOffspring"),sQuery(id+"F0.wireOp",EDGE,"E74.trimOffspring"),sQuery(id+"F0.wireOp",EDGE,"E75.trimOffspring"),sQuery(id+"F0.wireOp",EDGE,"E76.trimOffspring"),sQuery(id+"F0.wireOp",EDGE,"E77.trimOffspring"),sQuery(id+"F0.wireOp",EDGE,"E78.trimOffspring"),sQuery(id+"F0.wireOp",EDGE,"E79.trimOffspring"),sQuery(id+"F0.wireOp",EDGE,"E80.trimOffspring"),sQuery(id+"F0.wireOp",EDGE,"E81.trimOffspring"),sQuery(id+"F0.wireOp",EDGE,"E82.trimOffspring"),sQuery(id+"F0.wireOp",EDGE,"E83.trimOffspring"),sQuery(id+"F0.wireOp",EDGE,"E84.trimOffspring"),sQuery(id+"F0.wireOp",EDGE,"E85.trimOffspring"),sQuery(id+"F0.wireOp",EDGE,"E86.trimOffspring"),sQuery(id+"F0.wireOp",EDGE,"E87.trimOffspring"),sQuery(id+"F0.wireOp",EDGE,"E88.trimOffspring"),sQuery(id+"F0.wireOp",EDGE,"E89.trimOffspring"),sQuery(id+"F0.wireOp",EDGE,"E90.trimOffspring"),sQuery(id+"F0.wireOp",EDGE,"E91.trimOffspring"),sQuery(id+"F0.wireOp",EDGE,"E92.trimOffspring"),sQuery(id+"F0.wireOp",EDGE,"E93.trimOffspring"),sQuery(id+"F0.wireOp",EDGE,"E94")])],"isStart":false});
            var sketch = newSketch(context, id + "F15", { "sketchPlane" : qUnion([Q0])});
            skLineSegment(sketch, "E127", {"start": v(0, 0) * mm, "end": v(0, 98.6) * mm, "construction": true});
            skCircle(sketch, "E128", {"center": v(0, 0) * mm, "radius": 83.36 * mm, "construction": true});
            skPoint(sketch, "E129", {"position": v(0, 83.36) * mm});
            skPoint(sketch, "E130.1.0", {"position": v(-83.36, 0) * mm});
            skPoint(sketch, "E130.2.0", {"position": v(0, -83.36) * mm});
            skPoint(sketch, "E130.3.0", {"position": v(83.36, 0) * mm});
            skSolve(sketch);
        }
        {
            var Q0;
            Q0=sQuery(id+"F15.wireOp",VERTEX,"E129");
            var Q1;
            Q1=sQuery(id+"F15.wireOp",VERTEX,"E130.3.0");
            var Q2;
            Q2=sQuery(id+"F15.wireOp",VERTEX,"E130.2.0");
            var Q3;
            Q3=sQuery(id+"F15.wireOp",VERTEX,"E130.1.0");
            var Q4;
            Q4=makeQuery(id+"F1.opExtrude","SWEPT_BODY",BODY,{"disambiguationData":[OSD([sQuery(id+"F0.wireOp",EDGE,"E0"),sQuery(id+"F0.wireOp",EDGE,"E1.MirrorCS"),sQuery(id+"F0.wireOp",EDGE,"E2.MirrorCS"),sQuery(id+"F0.wireOp",EDGE,"E3.MirrorCS"),sQuery(id+"F0.wireOp",EDGE,"E4.MirrorCS"),sQuery(id+"F0.wireOp",EDGE,"E5.MirrorCS"),sQuery(id+"F0.wireOp",EDGE,"E6.MirrorCS"),sQuery(id+"F0.wireOp",EDGE,"E16.filletArc"),sQuery(id+"F0.wireOp",EDGE,"E17.filletArc"),sQuery(id+"F0.wireOp",EDGE,"E18.filletArc"),sQuery(id+"F0.wireOp",EDGE,"E19.filletArc"),sQuery(id+"F0.wireOp",EDGE,"E20.filletArc"),sQuery(id+"F0.wireOp",EDGE,"E21.filletArc"),sQuery(id+"F0.wireOp",EDGE,"E23.1.0"),sQuery(id+"F0.wireOp",EDGE,"E23.1.1"),sQuery(id+"F0.wireOp",EDGE,"E23.1.2"),sQuery(id+"F0.wireOp",EDGE,"E23.1.3"),sQuery(id+"F0.wireOp",EDGE,"E23.1.4"),sQuery(id+"F0.wireOp",EDGE,"E23.1.5"),sQuery(id+"F0.wireOp",EDGE,"E23.1.6"),sQuery(id+"F0.wireOp",EDGE,"E23.1.7"),sQuery(id+"F0.wireOp",EDGE,"E23.1.8"),sQuery(id+"F0.wireOp",EDGE,"E23.1.9"),sQuery(id+"F0.wireOp",EDGE,"E23.1.10"),sQuery(id+"F0.wireOp",EDGE,"E23.1.11"),sQuery(id+"F0.wireOp",EDGE,"E23.2.0"),sQuery(id+"F0.wireOp",EDGE,"E23.2.1"),sQuery(id+"F0.wireOp",EDGE,"E23.2.2"),sQuery(id+"F0.wireOp",EDGE,"E23.2.3"),sQuery(id+"F0.wireOp",EDGE,"E23.2.4"),sQuery(id+"F0.wireOp",EDGE,"E23.2.5"),sQuery(id+"F0.wireOp",EDGE,"E23.2.6"),sQuery(id+"F0.wireOp",EDGE,"E23.2.7"),sQuery(id+"F0.wireOp",EDGE,"E23.2.8"),sQuery(id+"F0.wireOp",EDGE,"E23.2.9"),sQuery(id+"F0.wireOp",EDGE,"E23.2.10"),sQuery(id+"F0.wireOp",EDGE,"E23.2.11"),sQuery(id+"F0.wireOp",EDGE,"E23.3.0"),sQuery(id+"F0.wireOp",EDGE,"E23.3.1"),sQuery(id+"F0.wireOp",EDGE,"E23.3.2"),sQuery(id+"F0.wireOp",EDGE,"E23.3.3"),sQuery(id+"F0.wireOp",EDGE,"E23.3.4"),sQuery(id+"F0.wireOp",EDGE,"E23.3.5"),sQuery(id+"F0.wireOp",EDGE,"E23.3.6"),sQuery(id+"F0.wireOp",EDGE,"E23.3.7"),sQuery(id+"F0.wireOp",EDGE,"E23.3.8"),sQuery(id+"F0.wireOp",EDGE,"E23.3.9"),sQuery(id+"F0.wireOp",EDGE,"E23.3.10"),sQuery(id+"F0.wireOp",EDGE,"E23.3.11"),sQuery(id+"F0.wireOp",EDGE,"E23.4.0"),sQuery(id+"F0.wireOp",EDGE,"E23.4.1"),sQuery(id+"F0.wireOp",EDGE,"E23.4.2"),sQuery(id+"F0.wireOp",EDGE,"E23.4.3"),sQuery(id+"F0.wireOp",EDGE,"E23.4.4"),sQuery(id+"F0.wireOp",EDGE,"E23.4.5"),sQuery(id+"F0.wireOp",EDGE,"E23.4.6"),sQuery(id+"F0.wireOp",EDGE,"E23.4.7"),sQuery(id+"F0.wireOp",EDGE,"E23.4.8"),sQuery(id+"F0.wireOp",EDGE,"E23.4.9"),sQuery(id+"F0.wireOp",EDGE,"E23.4.10"),sQuery(id+"F0.wireOp",EDGE,"E23.4.11"),sQuery(id+"F0.wireOp",EDGE,"E23.5.0"),sQuery(id+"F0.wireOp",EDGE,"E23.5.1"),sQuery(id+"F0.wireOp",EDGE,"E23.5.2"),sQuery(id+"F0.wireOp",EDGE,"E23.5.3"),sQuery(id+"F0.wireOp",EDGE,"E23.5.4"),sQuery(id+"F0.wireOp",EDGE,"E23.5.5"),sQuery(id+"F0.wireOp",EDGE,"E23.5.6"),sQuery(id+"F0.wireOp",EDGE,"E23.5.7"),sQuery(id+"F0.wireOp",EDGE,"E23.5.8"),sQuery(id+"F0.wireOp",EDGE,"E23.5.9"),sQuery(id+"F0.wireOp",EDGE,"E23.5.10"),sQuery(id+"F0.wireOp",EDGE,"E23.5.11"),sQuery(id+"F0.wireOp",EDGE,"E23.6.0"),sQuery(id+"F0.wireOp",EDGE,"E23.6.1"),sQuery(id+"F0.wireOp",EDGE,"E23.6.2"),sQuery(id+"F0.wireOp",EDGE,"E23.6.3"),sQuery(id+"F0.wireOp",EDGE,"E23.6.4"),sQuery(id+"F0.wireOp",EDGE,"E23.6.5"),sQuery(id+"F0.wireOp",EDGE,"E23.6.6"),sQuery(id+"F0.wireOp",EDGE,"E23.6.7"),sQuery(id+"F0.wireOp",EDGE,"E23.6.8"),sQuery(id+"F0.wireOp",EDGE,"E23.6.9"),sQuery(id+"F0.wireOp",EDGE,"E23.6.10"),sQuery(id+"F0.wireOp",EDGE,"E23.6.11"),sQuery(id+"F0.wireOp",EDGE,"E23.7.0"),sQuery(id+"F0.wireOp",EDGE,"E23.7.1"),sQuery(id+"F0.wireOp",EDGE,"E23.7.2"),sQuery(id+"F0.wireOp",EDGE,"E23.7.3"),sQuery(id+"F0.wireOp",EDGE,"E23.7.4"),sQuery(id+"F0.wireOp",EDGE,"E23.7.5"),sQuery(id+"F0.wireOp",EDGE,"E23.7.6"),sQuery(id+"F0.wireOp",EDGE,"E23.7.7"),sQuery(id+"F0.wireOp",EDGE,"E23.7.8"),sQuery(id+"F0.wireOp",EDGE,"E23.7.9"),sQuery(id+"F0.wireOp",EDGE,"E23.7.10"),sQuery(id+"F0.wireOp",EDGE,"E23.7.11"),sQuery(id+"F0.wireOp",EDGE,"E23.8.0"),sQuery(id+"F0.wireOp",EDGE,"E23.8.1"),sQuery(id+"F0.wireOp",EDGE,"E23.8.2"),sQuery(id+"F0.wireOp",EDGE,"E23.8.3"),sQuery(id+"F0.wireOp",EDGE,"E23.8.4"),sQuery(id+"F0.wireOp",EDGE,"E23.8.5"),sQuery(id+"F0.wireOp",EDGE,"E23.8.6"),sQuery(id+"F0.wireOp",EDGE,"E23.8.7"),sQuery(id+"F0.wireOp",EDGE,"E23.8.8"),sQuery(id+"F0.wireOp",EDGE,"E23.8.9"),sQuery(id+"F0.wireOp",EDGE,"E23.8.10"),sQuery(id+"F0.wireOp",EDGE,"E23.8.11"),sQuery(id+"F0.wireOp",EDGE,"E23.9.0"),sQuery(id+"F0.wireOp",EDGE,"E23.9.1"),sQuery(id+"F0.wireOp",EDGE,"E23.9.2"),sQuery(id+"F0.wireOp",EDGE,"E23.9.3"),sQuery(id+"F0.wireOp",EDGE,"E23.9.4"),sQuery(id+"F0.wireOp",EDGE,"E23.9.5"),sQuery(id+"F0.wireOp",EDGE,"E23.9.6"),sQuery(id+"F0.wireOp",EDGE,"E23.9.7"),sQuery(id+"F0.wireOp",EDGE,"E23.9.8"),sQuery(id+"F0.wireOp",EDGE,"E23.9.9"),sQuery(id+"F0.wireOp",EDGE,"E23.9.10"),sQuery(id+"F0.wireOp",EDGE,"E23.9.11"),sQuery(id+"F0.wireOp",EDGE,"E23.10.0"),sQuery(id+"F0.wireOp",EDGE,"E23.10.1"),sQuery(id+"F0.wireOp",EDGE,"E23.10.2"),sQuery(id+"F0.wireOp",EDGE,"E23.10.3"),sQuery(id+"F0.wireOp",EDGE,"E23.10.4"),sQuery(id+"F0.wireOp",EDGE,"E23.10.5"),sQuery(id+"F0.wireOp",EDGE,"E23.10.6"),sQuery(id+"F0.wireOp",EDGE,"E23.10.7"),sQuery(id+"F0.wireOp",EDGE,"E23.10.8"),sQuery(id+"F0.wireOp",EDGE,"E23.10.9"),sQuery(id+"F0.wireOp",EDGE,"E23.10.10"),sQuery(id+"F0.wireOp",EDGE,"E23.10.11"),sQuery(id+"F0.wireOp",EDGE,"E23.11.0"),sQuery(id+"F0.wireOp",EDGE,"E23.11.1"),sQuery(id+"F0.wireOp",EDGE,"E23.11.2"),sQuery(id+"F0.wireOp",EDGE,"E23.11.3"),sQuery(id+"F0.wireOp",EDGE,"E23.11.4"),sQuery(id+"F0.wireOp",EDGE,"E23.11.5"),sQuery(id+"F0.wireOp",EDGE,"E23.11.6"),sQuery(id+"F0.wireOp",EDGE,"E23.11.7"),sQuery(id+"F0.wireOp",EDGE,"E23.11.8"),sQuery(id+"F0.wireOp",EDGE,"E23.11.9"),sQuery(id+"F0.wireOp",EDGE,"E23.11.10"),sQuery(id+"F0.wireOp",EDGE,"E23.11.11"),sQuery(id+"F0.wireOp",EDGE,"E23.12.0"),sQuery(id+"F0.wireOp",EDGE,"E23.12.1"),sQuery(id+"F0.wireOp",EDGE,"E23.12.2"),sQuery(id+"F0.wireOp",EDGE,"E23.12.3"),sQuery(id+"F0.wireOp",EDGE,"E23.12.4"),sQuery(id+"F0.wireOp",EDGE,"E23.12.5"),sQuery(id+"F0.wireOp",EDGE,"E23.12.6"),sQuery(id+"F0.wireOp",EDGE,"E23.12.7"),sQuery(id+"F0.wireOp",EDGE,"E23.12.8"),sQuery(id+"F0.wireOp",EDGE,"E23.12.9"),sQuery(id+"F0.wireOp",EDGE,"E23.12.10"),sQuery(id+"F0.wireOp",EDGE,"E23.12.11"),sQuery(id+"F0.wireOp",EDGE,"E23.13.0"),sQuery(id+"F0.wireOp",EDGE,"E23.13.1"),sQuery(id+"F0.wireOp",EDGE,"E23.13.2"),sQuery(id+"F0.wireOp",EDGE,"E23.13.3"),sQuery(id+"F0.wireOp",EDGE,"E23.13.4"),sQuery(id+"F0.wireOp",EDGE,"E23.13.5"),sQuery(id+"F0.wireOp",EDGE,"E23.13.6"),sQuery(id+"F0.wireOp",EDGE,"E23.13.7"),sQuery(id+"F0.wireOp",EDGE,"E23.13.8"),sQuery(id+"F0.wireOp",EDGE,"E23.13.9"),sQuery(id+"F0.wireOp",EDGE,"E23.13.10"),sQuery(id+"F0.wireOp",EDGE,"E23.13.11"),sQuery(id+"F0.wireOp",EDGE,"E23.14.0"),sQuery(id+"F0.wireOp",EDGE,"E23.14.1"),sQuery(id+"F0.wireOp",EDGE,"E23.14.2"),sQuery(id+"F0.wireOp",EDGE,"E23.14.3"),sQuery(id+"F0.wireOp",EDGE,"E23.14.4"),sQuery(id+"F0.wireOp",EDGE,"E23.14.5"),sQuery(id+"F0.wireOp",EDGE,"E23.14.6"),sQuery(id+"F0.wireOp",EDGE,"E23.14.7"),sQuery(id+"F0.wireOp",EDGE,"E23.14.8"),sQuery(id+"F0.wireOp",EDGE,"E23.14.9"),sQuery(id+"F0.wireOp",EDGE,"E23.14.10"),sQuery(id+"F0.wireOp",EDGE,"E23.14.11"),sQuery(id+"F0.wireOp",EDGE,"E23.15.0"),sQuery(id+"F0.wireOp",EDGE,"E23.15.1"),sQuery(id+"F0.wireOp",EDGE,"E23.15.2"),sQuery(id+"F0.wireOp",EDGE,"E23.15.3"),sQuery(id+"F0.wireOp",EDGE,"E23.15.4"),sQuery(id+"F0.wireOp",EDGE,"E23.15.5"),sQuery(id+"F0.wireOp",EDGE,"E23.15.6"),sQuery(id+"F0.wireOp",EDGE,"E23.15.7"),sQuery(id+"F0.wireOp",EDGE,"E23.15.8"),sQuery(id+"F0.wireOp",EDGE,"E23.15.9"),sQuery(id+"F0.wireOp",EDGE,"E23.15.10"),sQuery(id+"F0.wireOp",EDGE,"E23.15.11"),sQuery(id+"F0.wireOp",EDGE,"E23.16.0"),sQuery(id+"F0.wireOp",EDGE,"E23.16.1"),sQuery(id+"F0.wireOp",EDGE,"E23.16.2"),sQuery(id+"F0.wireOp",EDGE,"E23.16.3"),sQuery(id+"F0.wireOp",EDGE,"E23.16.4"),sQuery(id+"F0.wireOp",EDGE,"E23.16.5"),sQuery(id+"F0.wireOp",EDGE,"E23.16.6"),sQuery(id+"F0.wireOp",EDGE,"E23.16.7"),sQuery(id+"F0.wireOp",EDGE,"E23.16.8"),sQuery(id+"F0.wireOp",EDGE,"E23.16.9"),sQuery(id+"F0.wireOp",EDGE,"E23.16.10"),sQuery(id+"F0.wireOp",EDGE,"E23.16.11"),sQuery(id+"F0.wireOp",EDGE,"E23.17.0"),sQuery(id+"F0.wireOp",EDGE,"E23.17.1"),sQuery(id+"F0.wireOp",EDGE,"E23.17.2"),sQuery(id+"F0.wireOp",EDGE,"E23.17.3"),sQuery(id+"F0.wireOp",EDGE,"E23.17.4"),sQuery(id+"F0.wireOp",EDGE,"E23.17.5"),sQuery(id+"F0.wireOp",EDGE,"E23.17.6"),sQuery(id+"F0.wireOp",EDGE,"E23.17.7"),sQuery(id+"F0.wireOp",EDGE,"E23.17.8"),sQuery(id+"F0.wireOp",EDGE,"E23.17.9"),sQuery(id+"F0.wireOp",EDGE,"E23.17.10"),sQuery(id+"F0.wireOp",EDGE,"E23.17.11"),sQuery(id+"F0.wireOp",EDGE,"E23.18.0"),sQuery(id+"F0.wireOp",EDGE,"E23.18.1"),sQuery(id+"F0.wireOp",EDGE,"E23.18.2"),sQuery(id+"F0.wireOp",EDGE,"E23.18.3"),sQuery(id+"F0.wireOp",EDGE,"E23.18.4"),sQuery(id+"F0.wireOp",EDGE,"E23.18.5"),sQuery(id+"F0.wireOp",EDGE,"E23.18.6"),sQuery(id+"F0.wireOp",EDGE,"E23.18.7"),sQuery(id+"F0.wireOp",EDGE,"E23.18.8"),sQuery(id+"F0.wireOp",EDGE,"E23.18.9"),sQuery(id+"F0.wireOp",EDGE,"E23.18.10"),sQuery(id+"F0.wireOp",EDGE,"E23.18.11"),sQuery(id+"F0.wireOp",EDGE,"E23.19.0"),sQuery(id+"F0.wireOp",EDGE,"E23.19.1"),sQuery(id+"F0.wireOp",EDGE,"E23.19.2"),sQuery(id+"F0.wireOp",EDGE,"E23.19.3"),sQuery(id+"F0.wireOp",EDGE,"E23.19.4"),sQuery(id+"F0.wireOp",EDGE,"E23.19.5"),sQuery(id+"F0.wireOp",EDGE,"E23.19.6"),sQuery(id+"F0.wireOp",EDGE,"E23.19.7"),sQuery(id+"F0.wireOp",EDGE,"E23.19.8"),sQuery(id+"F0.wireOp",EDGE,"E23.19.9"),sQuery(id+"F0.wireOp",EDGE,"E23.19.10"),sQuery(id+"F0.wireOp",EDGE,"E23.19.11"),sQuery(id+"F0.wireOp",EDGE,"E23.20.0"),sQuery(id+"F0.wireOp",EDGE,"E23.20.1"),sQuery(id+"F0.wireOp",EDGE,"E23.20.2"),sQuery(id+"F0.wireOp",EDGE,"E23.20.3"),sQuery(id+"F0.wireOp",EDGE,"E23.20.4"),sQuery(id+"F0.wireOp",EDGE,"E23.20.5"),sQuery(id+"F0.wireOp",EDGE,"E23.20.6"),sQuery(id+"F0.wireOp",EDGE,"E23.20.7"),sQuery(id+"F0.wireOp",EDGE,"E23.20.8"),sQuery(id+"F0.wireOp",EDGE,"E23.20.9"),sQuery(id+"F0.wireOp",EDGE,"E23.20.10"),sQuery(id+"F0.wireOp",EDGE,"E23.20.11"),sQuery(id+"F0.wireOp",EDGE,"E23.21.0"),sQuery(id+"F0.wireOp",EDGE,"E23.21.1"),sQuery(id+"F0.wireOp",EDGE,"E23.21.2"),sQuery(id+"F0.wireOp",EDGE,"E23.21.3"),sQuery(id+"F0.wireOp",EDGE,"E23.21.4"),sQuery(id+"F0.wireOp",EDGE,"E23.21.5"),sQuery(id+"F0.wireOp",EDGE,"E23.21.6"),sQuery(id+"F0.wireOp",EDGE,"E23.21.7"),sQuery(id+"F0.wireOp",EDGE,"E23.21.8"),sQuery(id+"F0.wireOp",EDGE,"E23.21.9"),sQuery(id+"F0.wireOp",EDGE,"E23.21.10"),sQuery(id+"F0.wireOp",EDGE,"E23.21.11"),sQuery(id+"F0.wireOp",EDGE,"E23.22.0"),sQuery(id+"F0.wireOp",EDGE,"E23.22.1"),sQuery(id+"F0.wireOp",EDGE,"E23.22.2"),sQuery(id+"F0.wireOp",EDGE,"E23.22.3"),sQuery(id+"F0.wireOp",EDGE,"E23.22.4"),sQuery(id+"F0.wireOp",EDGE,"E23.22.5"),sQuery(id+"F0.wireOp",EDGE,"E23.22.6"),sQuery(id+"F0.wireOp",EDGE,"E23.22.7"),sQuery(id+"F0.wireOp",EDGE,"E23.22.8"),sQuery(id+"F0.wireOp",EDGE,"E23.22.9"),sQuery(id+"F0.wireOp",EDGE,"E23.22.10"),sQuery(id+"F0.wireOp",EDGE,"E23.22.11"),sQuery(id+"F0.wireOp",EDGE,"E23.23.0"),sQuery(id+"F0.wireOp",EDGE,"E23.23.1"),sQuery(id+"F0.wireOp",EDGE,"E23.23.2"),sQuery(id+"F0.wireOp",EDGE,"E23.23.3"),sQuery(id+"F0.wireOp",EDGE,"E23.23.4"),sQuery(id+"F0.wireOp",EDGE,"E23.23.5"),sQuery(id+"F0.wireOp",EDGE,"E23.23.6"),sQuery(id+"F0.wireOp",EDGE,"E23.23.7"),sQuery(id+"F0.wireOp",EDGE,"E23.23.8"),sQuery(id+"F0.wireOp",EDGE,"E23.23.9"),sQuery(id+"F0.wireOp",EDGE,"E23.23.10"),sQuery(id+"F0.wireOp",EDGE,"E23.23.11"),sQuery(id+"F0.wireOp",EDGE,"E23.24.0"),sQuery(id+"F0.wireOp",EDGE,"E23.24.1"),sQuery(id+"F0.wireOp",EDGE,"E23.24.2"),sQuery(id+"F0.wireOp",EDGE,"E23.24.3"),sQuery(id+"F0.wireOp",EDGE,"E23.24.4"),sQuery(id+"F0.wireOp",EDGE,"E23.24.5"),sQuery(id+"F0.wireOp",EDGE,"E23.24.6"),sQuery(id+"F0.wireOp",EDGE,"E23.24.7"),sQuery(id+"F0.wireOp",EDGE,"E23.24.8"),sQuery(id+"F0.wireOp",EDGE,"E23.24.9"),sQuery(id+"F0.wireOp",EDGE,"E23.24.10"),sQuery(id+"F0.wireOp",EDGE,"E23.24.11"),sQuery(id+"F0.wireOp",EDGE,"E23.25.0"),sQuery(id+"F0.wireOp",EDGE,"E23.25.1"),sQuery(id+"F0.wireOp",EDGE,"E23.25.2"),sQuery(id+"F0.wireOp",EDGE,"E23.25.3"),sQuery(id+"F0.wireOp",EDGE,"E23.25.4"),sQuery(id+"F0.wireOp",EDGE,"E23.25.5"),sQuery(id+"F0.wireOp",EDGE,"E23.25.6"),sQuery(id+"F0.wireOp",EDGE,"E23.25.7"),sQuery(id+"F0.wireOp",EDGE,"E23.25.8"),sQuery(id+"F0.wireOp",EDGE,"E23.25.9"),sQuery(id+"F0.wireOp",EDGE,"E23.25.10"),sQuery(id+"F0.wireOp",EDGE,"E23.25.11"),sQuery(id+"F0.wireOp",EDGE,"E23.26.0"),sQuery(id+"F0.wireOp",EDGE,"E23.26.1"),sQuery(id+"F0.wireOp",EDGE,"E23.26.2"),sQuery(id+"F0.wireOp",EDGE,"E23.26.3"),sQuery(id+"F0.wireOp",EDGE,"E23.26.4"),sQuery(id+"F0.wireOp",EDGE,"E23.26.5"),sQuery(id+"F0.wireOp",EDGE,"E23.26.6"),sQuery(id+"F0.wireOp",EDGE,"E23.26.7"),sQuery(id+"F0.wireOp",EDGE,"E23.26.8"),sQuery(id+"F0.wireOp",EDGE,"E23.26.9"),sQuery(id+"F0.wireOp",EDGE,"E23.26.10"),sQuery(id+"F0.wireOp",EDGE,"E23.26.11"),sQuery(id+"F0.wireOp",EDGE,"E23.27.0"),sQuery(id+"F0.wireOp",EDGE,"E23.27.1"),sQuery(id+"F0.wireOp",EDGE,"E23.27.2"),sQuery(id+"F0.wireOp",EDGE,"E23.27.3"),sQuery(id+"F0.wireOp",EDGE,"E23.27.4"),sQuery(id+"F0.wireOp",EDGE,"E23.27.5"),sQuery(id+"F0.wireOp",EDGE,"E23.27.6"),sQuery(id+"F0.wireOp",EDGE,"E23.27.7"),sQuery(id+"F0.wireOp",EDGE,"E23.27.8"),sQuery(id+"F0.wireOp",EDGE,"E23.27.9"),sQuery(id+"F0.wireOp",EDGE,"E23.27.10"),sQuery(id+"F0.wireOp",EDGE,"E23.27.11"),sQuery(id+"F0.wireOp",EDGE,"E23.28.0"),sQuery(id+"F0.wireOp",EDGE,"E23.28.1"),sQuery(id+"F0.wireOp",EDGE,"E23.28.2"),sQuery(id+"F0.wireOp",EDGE,"E23.28.3"),sQuery(id+"F0.wireOp",EDGE,"E23.28.4"),sQuery(id+"F0.wireOp",EDGE,"E23.28.5"),sQuery(id+"F0.wireOp",EDGE,"E23.28.6"),sQuery(id+"F0.wireOp",EDGE,"E23.28.7"),sQuery(id+"F0.wireOp",EDGE,"E23.28.8"),sQuery(id+"F0.wireOp",EDGE,"E23.28.9"),sQuery(id+"F0.wireOp",EDGE,"E23.28.10"),sQuery(id+"F0.wireOp",EDGE,"E23.28.11"),sQuery(id+"F0.wireOp",EDGE,"E23.29.0"),sQuery(id+"F0.wireOp",EDGE,"E23.29.1"),sQuery(id+"F0.wireOp",EDGE,"E23.29.2"),sQuery(id+"F0.wireOp",EDGE,"E23.29.3"),sQuery(id+"F0.wireOp",EDGE,"E23.29.4"),sQuery(id+"F0.wireOp",EDGE,"E23.29.5"),sQuery(id+"F0.wireOp",EDGE,"E23.29.6"),sQuery(id+"F0.wireOp",EDGE,"E23.29.7"),sQuery(id+"F0.wireOp",EDGE,"E23.29.8"),sQuery(id+"F0.wireOp",EDGE,"E23.29.9"),sQuery(id+"F0.wireOp",EDGE,"E23.29.10"),sQuery(id+"F0.wireOp",EDGE,"E23.29.11"),sQuery(id+"F0.wireOp",EDGE,"E23.30.0"),sQuery(id+"F0.wireOp",EDGE,"E23.30.1"),sQuery(id+"F0.wireOp",EDGE,"E23.30.2"),sQuery(id+"F0.wireOp",EDGE,"E23.30.3"),sQuery(id+"F0.wireOp",EDGE,"E23.30.4"),sQuery(id+"F0.wireOp",EDGE,"E23.30.5"),sQuery(id+"F0.wireOp",EDGE,"E23.30.6"),sQuery(id+"F0.wireOp",EDGE,"E23.30.7"),sQuery(id+"F0.wireOp",EDGE,"E23.30.8"),sQuery(id+"F0.wireOp",EDGE,"E23.30.9"),sQuery(id+"F0.wireOp",EDGE,"E23.30.10"),sQuery(id+"F0.wireOp",EDGE,"E23.30.11"),sQuery(id+"F0.wireOp",EDGE,"E23.31.0"),sQuery(id+"F0.wireOp",EDGE,"E23.31.1"),sQuery(id+"F0.wireOp",EDGE,"E23.31.2"),sQuery(id+"F0.wireOp",EDGE,"E23.31.3"),sQuery(id+"F0.wireOp",EDGE,"E23.31.4"),sQuery(id+"F0.wireOp",EDGE,"E23.31.5"),sQuery(id+"F0.wireOp",EDGE,"E23.31.6"),sQuery(id+"F0.wireOp",EDGE,"E23.31.7"),sQuery(id+"F0.wireOp",EDGE,"E23.31.8"),sQuery(id+"F0.wireOp",EDGE,"E23.31.9"),sQuery(id+"F0.wireOp",EDGE,"E23.31.10"),sQuery(id+"F0.wireOp",EDGE,"E23.31.11"),sQuery(id+"F0.wireOp",EDGE,"E23.32.0"),sQuery(id+"F0.wireOp",EDGE,"E23.32.1"),sQuery(id+"F0.wireOp",EDGE,"E23.32.2"),sQuery(id+"F0.wireOp",EDGE,"E23.32.3"),sQuery(id+"F0.wireOp",EDGE,"E23.32.4"),sQuery(id+"F0.wireOp",EDGE,"E23.32.5"),sQuery(id+"F0.wireOp",EDGE,"E23.32.6"),sQuery(id+"F0.wireOp",EDGE,"E23.32.7"),sQuery(id+"F0.wireOp",EDGE,"E23.32.8"),sQuery(id+"F0.wireOp",EDGE,"E23.32.9"),sQuery(id+"F0.wireOp",EDGE,"E23.32.10"),sQuery(id+"F0.wireOp",EDGE,"E23.32.11"),sQuery(id+"F0.wireOp",EDGE,"E23.33.0"),sQuery(id+"F0.wireOp",EDGE,"E23.33.1"),sQuery(id+"F0.wireOp",EDGE,"E23.33.2"),sQuery(id+"F0.wireOp",EDGE,"E23.33.3"),sQuery(id+"F0.wireOp",EDGE,"E23.33.4"),sQuery(id+"F0.wireOp",EDGE,"E23.33.5"),sQuery(id+"F0.wireOp",EDGE,"E23.33.6"),sQuery(id+"F0.wireOp",EDGE,"E23.33.7"),sQuery(id+"F0.wireOp",EDGE,"E23.33.8"),sQuery(id+"F0.wireOp",EDGE,"E23.33.9"),sQuery(id+"F0.wireOp",EDGE,"E23.33.10"),sQuery(id+"F0.wireOp",EDGE,"E23.33.11"),sQuery(id+"F0.wireOp",EDGE,"E23.34.0"),sQuery(id+"F0.wireOp",EDGE,"E23.34.1"),sQuery(id+"F0.wireOp",EDGE,"E23.34.2"),sQuery(id+"F0.wireOp",EDGE,"E23.34.3"),sQuery(id+"F0.wireOp",EDGE,"E23.34.4"),sQuery(id+"F0.wireOp",EDGE,"E23.34.5"),sQuery(id+"F0.wireOp",EDGE,"E23.34.6"),sQuery(id+"F0.wireOp",EDGE,"E23.34.7"),sQuery(id+"F0.wireOp",EDGE,"E23.34.8"),sQuery(id+"F0.wireOp",EDGE,"E23.34.9"),sQuery(id+"F0.wireOp",EDGE,"E23.34.10"),sQuery(id+"F0.wireOp",EDGE,"E23.34.11"),sQuery(id+"F0.wireOp",EDGE,"E23.35.0"),sQuery(id+"F0.wireOp",EDGE,"E23.35.1"),sQuery(id+"F0.wireOp",EDGE,"E23.35.2"),sQuery(id+"F0.wireOp",EDGE,"E23.35.3"),sQuery(id+"F0.wireOp",EDGE,"E23.35.4"),sQuery(id+"F0.wireOp",EDGE,"E23.35.5"),sQuery(id+"F0.wireOp",EDGE,"E23.35.6"),sQuery(id+"F0.wireOp",EDGE,"E23.35.7"),sQuery(id+"F0.wireOp",EDGE,"E23.35.8"),sQuery(id+"F0.wireOp",EDGE,"E23.35.9"),sQuery(id+"F0.wireOp",EDGE,"E23.35.10"),sQuery(id+"F0.wireOp",EDGE,"E23.35.11"),sQuery(id+"F0.wireOp",EDGE,"E23.36.0"),sQuery(id+"F0.wireOp",EDGE,"E23.36.1"),sQuery(id+"F0.wireOp",EDGE,"E23.36.2"),sQuery(id+"F0.wireOp",EDGE,"E23.36.3"),sQuery(id+"F0.wireOp",EDGE,"E23.36.4"),sQuery(id+"F0.wireOp",EDGE,"E23.36.5"),sQuery(id+"F0.wireOp",EDGE,"E23.36.6"),sQuery(id+"F0.wireOp",EDGE,"E23.36.7"),sQuery(id+"F0.wireOp",EDGE,"E23.36.8"),sQuery(id+"F0.wireOp",EDGE,"E23.36.9"),sQuery(id+"F0.wireOp",EDGE,"E23.36.10"),sQuery(id+"F0.wireOp",EDGE,"E23.36.11"),sQuery(id+"F0.wireOp",EDGE,"E23.37.0"),sQuery(id+"F0.wireOp",EDGE,"E23.37.1"),sQuery(id+"F0.wireOp",EDGE,"E23.37.2"),sQuery(id+"F0.wireOp",EDGE,"E23.37.3"),sQuery(id+"F0.wireOp",EDGE,"E23.37.4"),sQuery(id+"F0.wireOp",EDGE,"E23.37.5"),sQuery(id+"F0.wireOp",EDGE,"E23.37.6"),sQuery(id+"F0.wireOp",EDGE,"E23.37.7"),sQuery(id+"F0.wireOp",EDGE,"E23.37.8"),sQuery(id+"F0.wireOp",EDGE,"E23.37.9"),sQuery(id+"F0.wireOp",EDGE,"E23.37.10"),sQuery(id+"F0.wireOp",EDGE,"E23.37.11"),sQuery(id+"F0.wireOp",EDGE,"E23.38.0"),sQuery(id+"F0.wireOp",EDGE,"E23.38.1"),sQuery(id+"F0.wireOp",EDGE,"E23.38.2"),sQuery(id+"F0.wireOp",EDGE,"E23.38.3"),sQuery(id+"F0.wireOp",EDGE,"E23.38.4"),sQuery(id+"F0.wireOp",EDGE,"E23.38.5"),sQuery(id+"F0.wireOp",EDGE,"E23.38.6"),sQuery(id+"F0.wireOp",EDGE,"E23.38.7"),sQuery(id+"F0.wireOp",EDGE,"E23.38.8"),sQuery(id+"F0.wireOp",EDGE,"E23.38.9"),sQuery(id+"F0.wireOp",EDGE,"E23.38.10"),sQuery(id+"F0.wireOp",EDGE,"E23.38.11"),sQuery(id+"F0.wireOp",EDGE,"E23.39.0"),sQuery(id+"F0.wireOp",EDGE,"E23.39.1"),sQuery(id+"F0.wireOp",EDGE,"E23.39.2"),sQuery(id+"F0.wireOp",EDGE,"E23.39.3"),sQuery(id+"F0.wireOp",EDGE,"E23.39.4"),sQuery(id+"F0.wireOp",EDGE,"E23.39.5"),sQuery(id+"F0.wireOp",EDGE,"E23.39.6"),sQuery(id+"F0.wireOp",EDGE,"E23.39.7"),sQuery(id+"F0.wireOp",EDGE,"E23.39.8"),sQuery(id+"F0.wireOp",EDGE,"E23.39.9"),sQuery(id+"F0.wireOp",EDGE,"E23.39.10"),sQuery(id+"F0.wireOp",EDGE,"E23.39.11"),sQuery(id+"F0.wireOp",EDGE,"E23.40.0"),sQuery(id+"F0.wireOp",EDGE,"E23.40.1"),sQuery(id+"F0.wireOp",EDGE,"E23.40.2"),sQuery(id+"F0.wireOp",EDGE,"E23.40.3"),sQuery(id+"F0.wireOp",EDGE,"E23.40.4"),sQuery(id+"F0.wireOp",EDGE,"E23.40.5"),sQuery(id+"F0.wireOp",EDGE,"E23.40.6"),sQuery(id+"F0.wireOp",EDGE,"E23.40.7"),sQuery(id+"F0.wireOp",EDGE,"E23.40.8"),sQuery(id+"F0.wireOp",EDGE,"E23.40.9"),sQuery(id+"F0.wireOp",EDGE,"E23.40.10"),sQuery(id+"F0.wireOp",EDGE,"E23.40.11"),sQuery(id+"F0.wireOp",EDGE,"E23.41.0"),sQuery(id+"F0.wireOp",EDGE,"E23.41.1"),sQuery(id+"F0.wireOp",EDGE,"E23.41.2"),sQuery(id+"F0.wireOp",EDGE,"E23.41.3"),sQuery(id+"F0.wireOp",EDGE,"E23.41.4"),sQuery(id+"F0.wireOp",EDGE,"E23.41.5"),sQuery(id+"F0.wireOp",EDGE,"E23.41.6"),sQuery(id+"F0.wireOp",EDGE,"E23.41.7"),sQuery(id+"F0.wireOp",EDGE,"E23.41.8"),sQuery(id+"F0.wireOp",EDGE,"E23.41.9"),sQuery(id+"F0.wireOp",EDGE,"E23.41.10"),sQuery(id+"F0.wireOp",EDGE,"E23.41.11"),sQuery(id+"F0.wireOp",EDGE,"E23.42.0"),sQuery(id+"F0.wireOp",EDGE,"E23.42.1"),sQuery(id+"F0.wireOp",EDGE,"E23.42.2"),sQuery(id+"F0.wireOp",EDGE,"E23.42.3"),sQuery(id+"F0.wireOp",EDGE,"E23.42.4"),sQuery(id+"F0.wireOp",EDGE,"E23.42.5"),sQuery(id+"F0.wireOp",EDGE,"E23.42.6"),sQuery(id+"F0.wireOp",EDGE,"E23.42.7"),sQuery(id+"F0.wireOp",EDGE,"E23.42.8"),sQuery(id+"F0.wireOp",EDGE,"E23.42.9"),sQuery(id+"F0.wireOp",EDGE,"E23.42.10"),sQuery(id+"F0.wireOp",EDGE,"E23.42.11"),sQuery(id+"F0.wireOp",EDGE,"E23.43.0"),sQuery(id+"F0.wireOp",EDGE,"E23.43.1"),sQuery(id+"F0.wireOp",EDGE,"E23.43.2"),sQuery(id+"F0.wireOp",EDGE,"E23.43.3"),sQuery(id+"F0.wireOp",EDGE,"E23.43.4"),sQuery(id+"F0.wireOp",EDGE,"E23.43.5"),sQuery(id+"F0.wireOp",EDGE,"E23.43.6"),sQuery(id+"F0.wireOp",EDGE,"E23.43.7"),sQuery(id+"F0.wireOp",EDGE,"E23.43.8"),sQuery(id+"F0.wireOp",EDGE,"E23.43.9"),sQuery(id+"F0.wireOp",EDGE,"E23.43.10"),sQuery(id+"F0.wireOp",EDGE,"E23.43.11"),sQuery(id+"F0.wireOp",EDGE,"E23.44.0"),sQuery(id+"F0.wireOp",EDGE,"E23.44.1"),sQuery(id+"F0.wireOp",EDGE,"E23.44.2"),sQuery(id+"F0.wireOp",EDGE,"E23.44.3"),sQuery(id+"F0.wireOp",EDGE,"E23.44.4"),sQuery(id+"F0.wireOp",EDGE,"E23.44.5"),sQuery(id+"F0.wireOp",EDGE,"E23.44.6"),sQuery(id+"F0.wireOp",EDGE,"E23.44.7"),sQuery(id+"F0.wireOp",EDGE,"E23.44.8"),sQuery(id+"F0.wireOp",EDGE,"E23.44.9"),sQuery(id+"F0.wireOp",EDGE,"E23.44.10"),sQuery(id+"F0.wireOp",EDGE,"E23.44.11"),sQuery(id+"F0.wireOp",EDGE,"E23.45.0"),sQuery(id+"F0.wireOp",EDGE,"E23.45.1"),sQuery(id+"F0.wireOp",EDGE,"E23.45.2"),sQuery(id+"F0.wireOp",EDGE,"E23.45.3"),sQuery(id+"F0.wireOp",EDGE,"E23.45.4"),sQuery(id+"F0.wireOp",EDGE,"E23.45.5"),sQuery(id+"F0.wireOp",EDGE,"E23.45.6"),sQuery(id+"F0.wireOp",EDGE,"E23.45.7"),sQuery(id+"F0.wireOp",EDGE,"E23.45.8"),sQuery(id+"F0.wireOp",EDGE,"E23.45.9"),sQuery(id+"F0.wireOp",EDGE,"E23.45.10"),sQuery(id+"F0.wireOp",EDGE,"E23.45.11"),sQuery(id+"F0.wireOp",EDGE,"E23.46.0"),sQuery(id+"F0.wireOp",EDGE,"E23.46.1"),sQuery(id+"F0.wireOp",EDGE,"E23.46.2"),sQuery(id+"F0.wireOp",EDGE,"E23.46.3"),sQuery(id+"F0.wireOp",EDGE,"E23.46.4"),sQuery(id+"F0.wireOp",EDGE,"E23.46.5"),sQuery(id+"F0.wireOp",EDGE,"E23.46.6"),sQuery(id+"F0.wireOp",EDGE,"E23.46.7"),sQuery(id+"F0.wireOp",EDGE,"E23.46.8"),sQuery(id+"F0.wireOp",EDGE,"E23.46.9"),sQuery(id+"F0.wireOp",EDGE,"E23.46.10"),sQuery(id+"F0.wireOp",EDGE,"E23.46.11"),sQuery(id+"F0.wireOp",EDGE,"E23.47.0"),sQuery(id+"F0.wireOp",EDGE,"E23.47.1"),sQuery(id+"F0.wireOp",EDGE,"E23.47.2"),sQuery(id+"F0.wireOp",EDGE,"E23.47.3"),sQuery(id+"F0.wireOp",EDGE,"E23.47.4"),sQuery(id+"F0.wireOp",EDGE,"E23.47.5"),sQuery(id+"F0.wireOp",EDGE,"E23.47.6"),sQuery(id+"F0.wireOp",EDGE,"E23.47.7"),sQuery(id+"F0.wireOp",EDGE,"E23.47.8"),sQuery(id+"F0.wireOp",EDGE,"E23.47.9"),sQuery(id+"F0.wireOp",EDGE,"E23.47.10"),sQuery(id+"F0.wireOp",EDGE,"E23.47.11"),sQuery(id+"F0.wireOp",EDGE,"E23.48.0"),sQuery(id+"F0.wireOp",EDGE,"E23.48.1"),sQuery(id+"F0.wireOp",EDGE,"E23.48.2"),sQuery(id+"F0.wireOp",EDGE,"E23.48.3"),sQuery(id+"F0.wireOp",EDGE,"E23.48.4"),sQuery(id+"F0.wireOp",EDGE,"E23.48.5"),sQuery(id+"F0.wireOp",EDGE,"E23.48.6"),sQuery(id+"F0.wireOp",EDGE,"E23.48.7"),sQuery(id+"F0.wireOp",EDGE,"E23.48.8"),sQuery(id+"F0.wireOp",EDGE,"E23.48.9"),sQuery(id+"F0.wireOp",EDGE,"E23.48.10"),sQuery(id+"F0.wireOp",EDGE,"E23.48.11"),sQuery(id+"F0.wireOp",EDGE,"E23.49.0"),sQuery(id+"F0.wireOp",EDGE,"E23.49.1"),sQuery(id+"F0.wireOp",EDGE,"E23.49.2"),sQuery(id+"F0.wireOp",EDGE,"E23.49.3"),sQuery(id+"F0.wireOp",EDGE,"E23.49.4"),sQuery(id+"F0.wireOp",EDGE,"E23.49.5"),sQuery(id+"F0.wireOp",EDGE,"E23.49.6"),sQuery(id+"F0.wireOp",EDGE,"E23.49.7"),sQuery(id+"F0.wireOp",EDGE,"E23.49.8"),sQuery(id+"F0.wireOp",EDGE,"E23.49.9"),sQuery(id+"F0.wireOp",EDGE,"E23.49.10"),sQuery(id+"F0.wireOp",EDGE,"E23.49.11"),sQuery(id+"F0.wireOp",EDGE,"E23.50.0"),sQuery(id+"F0.wireOp",EDGE,"E23.50.1"),sQuery(id+"F0.wireOp",EDGE,"E23.50.2"),sQuery(id+"F0.wireOp",EDGE,"E23.50.3"),sQuery(id+"F0.wireOp",EDGE,"E23.50.4"),sQuery(id+"F0.wireOp",EDGE,"E23.50.5"),sQuery(id+"F0.wireOp",EDGE,"E23.50.6"),sQuery(id+"F0.wireOp",EDGE,"E23.50.7"),sQuery(id+"F0.wireOp",EDGE,"E23.50.8"),sQuery(id+"F0.wireOp",EDGE,"E23.50.9"),sQuery(id+"F0.wireOp",EDGE,"E23.50.10"),sQuery(id+"F0.wireOp",EDGE,"E23.50.11"),sQuery(id+"F0.wireOp",EDGE,"E23.51.0"),sQuery(id+"F0.wireOp",EDGE,"E23.51.1"),sQuery(id+"F0.wireOp",EDGE,"E23.51.2"),sQuery(id+"F0.wireOp",EDGE,"E23.51.3"),sQuery(id+"F0.wireOp",EDGE,"E23.51.4"),sQuery(id+"F0.wireOp",EDGE,"E23.51.5"),sQuery(id+"F0.wireOp",EDGE,"E23.51.6"),sQuery(id+"F0.wireOp",EDGE,"E23.51.7"),sQuery(id+"F0.wireOp",EDGE,"E23.51.8"),sQuery(id+"F0.wireOp",EDGE,"E23.51.9"),sQuery(id+"F0.wireOp",EDGE,"E23.51.10"),sQuery(id+"F0.wireOp",EDGE,"E23.51.11"),sQuery(id+"F0.wireOp",EDGE,"E23.52.0"),sQuery(id+"F0.wireOp",EDGE,"E23.52.1"),sQuery(id+"F0.wireOp",EDGE,"E23.52.2"),sQuery(id+"F0.wireOp",EDGE,"E23.52.3"),sQuery(id+"F0.wireOp",EDGE,"E23.52.4"),sQuery(id+"F0.wireOp",EDGE,"E23.52.5"),sQuery(id+"F0.wireOp",EDGE,"E23.52.6"),sQuery(id+"F0.wireOp",EDGE,"E23.52.7"),sQuery(id+"F0.wireOp",EDGE,"E23.52.8"),sQuery(id+"F0.wireOp",EDGE,"E23.52.9"),sQuery(id+"F0.wireOp",EDGE,"E23.52.10"),sQuery(id+"F0.wireOp",EDGE,"E23.52.11"),sQuery(id+"F0.wireOp",EDGE,"E23.53.0"),sQuery(id+"F0.wireOp",EDGE,"E23.53.1"),sQuery(id+"F0.wireOp",EDGE,"E23.53.2"),sQuery(id+"F0.wireOp",EDGE,"E23.53.3"),sQuery(id+"F0.wireOp",EDGE,"E23.53.4"),sQuery(id+"F0.wireOp",EDGE,"E23.53.5"),sQuery(id+"F0.wireOp",EDGE,"E23.53.6"),sQuery(id+"F0.wireOp",EDGE,"E23.53.7"),sQuery(id+"F0.wireOp",EDGE,"E23.53.8"),sQuery(id+"F0.wireOp",EDGE,"E23.53.9"),sQuery(id+"F0.wireOp",EDGE,"E23.53.10"),sQuery(id+"F0.wireOp",EDGE,"E23.53.11"),sQuery(id+"F0.wireOp",EDGE,"E23.54.0"),sQuery(id+"F0.wireOp",EDGE,"E23.54.1"),sQuery(id+"F0.wireOp",EDGE,"E23.54.2"),sQuery(id+"F0.wireOp",EDGE,"E23.54.3"),sQuery(id+"F0.wireOp",EDGE,"E23.54.4"),sQuery(id+"F0.wireOp",EDGE,"E23.54.5"),sQuery(id+"F0.wireOp",EDGE,"E23.54.6"),sQuery(id+"F0.wireOp",EDGE,"E23.54.7"),sQuery(id+"F0.wireOp",EDGE,"E23.54.8"),sQuery(id+"F0.wireOp",EDGE,"E23.54.9"),sQuery(id+"F0.wireOp",EDGE,"E23.54.10"),sQuery(id+"F0.wireOp",EDGE,"E23.54.11"),sQuery(id+"F0.wireOp",EDGE,"E23.55.0"),sQuery(id+"F0.wireOp",EDGE,"E23.55.1"),sQuery(id+"F0.wireOp",EDGE,"E23.55.2"),sQuery(id+"F0.wireOp",EDGE,"E23.55.3"),sQuery(id+"F0.wireOp",EDGE,"E23.55.4"),sQuery(id+"F0.wireOp",EDGE,"E23.55.5"),sQuery(id+"F0.wireOp",EDGE,"E23.55.6"),sQuery(id+"F0.wireOp",EDGE,"E23.55.7"),sQuery(id+"F0.wireOp",EDGE,"E23.55.8"),sQuery(id+"F0.wireOp",EDGE,"E23.55.9"),sQuery(id+"F0.wireOp",EDGE,"E23.55.10"),sQuery(id+"F0.wireOp",EDGE,"E23.55.11"),sQuery(id+"F0.wireOp",EDGE,"E23.56.0"),sQuery(id+"F0.wireOp",EDGE,"E23.56.1"),sQuery(id+"F0.wireOp",EDGE,"E23.56.2"),sQuery(id+"F0.wireOp",EDGE,"E23.56.3"),sQuery(id+"F0.wireOp",EDGE,"E23.56.4"),sQuery(id+"F0.wireOp",EDGE,"E23.56.5"),sQuery(id+"F0.wireOp",EDGE,"E23.56.6"),sQuery(id+"F0.wireOp",EDGE,"E23.56.7"),sQuery(id+"F0.wireOp",EDGE,"E23.56.8"),sQuery(id+"F0.wireOp",EDGE,"E23.56.9"),sQuery(id+"F0.wireOp",EDGE,"E23.56.10"),sQuery(id+"F0.wireOp",EDGE,"E23.56.11"),sQuery(id+"F0.wireOp",EDGE,"E23.57.0"),sQuery(id+"F0.wireOp",EDGE,"E23.57.1"),sQuery(id+"F0.wireOp",EDGE,"E23.57.2"),sQuery(id+"F0.wireOp",EDGE,"E23.57.3"),sQuery(id+"F0.wireOp",EDGE,"E23.57.4"),sQuery(id+"F0.wireOp",EDGE,"E23.57.5"),sQuery(id+"F0.wireOp",EDGE,"E23.57.6"),sQuery(id+"F0.wireOp",EDGE,"E23.57.7"),sQuery(id+"F0.wireOp",EDGE,"E23.57.8"),sQuery(id+"F0.wireOp",EDGE,"E23.57.9"),sQuery(id+"F0.wireOp",EDGE,"E23.57.10"),sQuery(id+"F0.wireOp",EDGE,"E23.57.11"),sQuery(id+"F0.wireOp",EDGE,"E23.58.0"),sQuery(id+"F0.wireOp",EDGE,"E23.58.1"),sQuery(id+"F0.wireOp",EDGE,"E23.58.2"),sQuery(id+"F0.wireOp",EDGE,"E23.58.3"),sQuery(id+"F0.wireOp",EDGE,"E23.58.4"),sQuery(id+"F0.wireOp",EDGE,"E23.58.5"),sQuery(id+"F0.wireOp",EDGE,"E23.58.6"),sQuery(id+"F0.wireOp",EDGE,"E23.58.7"),sQuery(id+"F0.wireOp",EDGE,"E23.58.8"),sQuery(id+"F0.wireOp",EDGE,"E23.58.9"),sQuery(id+"F0.wireOp",EDGE,"E23.58.10"),sQuery(id+"F0.wireOp",EDGE,"E23.58.11"),sQuery(id+"F0.wireOp",EDGE,"E23.59.0"),sQuery(id+"F0.wireOp",EDGE,"E23.59.1"),sQuery(id+"F0.wireOp",EDGE,"E23.59.2"),sQuery(id+"F0.wireOp",EDGE,"E23.59.3"),sQuery(id+"F0.wireOp",EDGE,"E23.59.4"),sQuery(id+"F0.wireOp",EDGE,"E23.59.5"),sQuery(id+"F0.wireOp",EDGE,"E23.59.6"),sQuery(id+"F0.wireOp",EDGE,"E23.59.7"),sQuery(id+"F0.wireOp",EDGE,"E23.59.8"),sQuery(id+"F0.wireOp",EDGE,"E23.59.9"),sQuery(id+"F0.wireOp",EDGE,"E23.59.10"),sQuery(id+"F0.wireOp",EDGE,"E23.59.11"),sQuery(id+"F0.wireOp",EDGE,"E23.60.0"),sQuery(id+"F0.wireOp",EDGE,"E23.60.1"),sQuery(id+"F0.wireOp",EDGE,"E23.60.2"),sQuery(id+"F0.wireOp",EDGE,"E23.60.3"),sQuery(id+"F0.wireOp",EDGE,"E23.60.4"),sQuery(id+"F0.wireOp",EDGE,"E23.60.5"),sQuery(id+"F0.wireOp",EDGE,"E23.60.6"),sQuery(id+"F0.wireOp",EDGE,"E23.60.7"),sQuery(id+"F0.wireOp",EDGE,"E23.60.8"),sQuery(id+"F0.wireOp",EDGE,"E23.60.9"),sQuery(id+"F0.wireOp",EDGE,"E23.60.10"),sQuery(id+"F0.wireOp",EDGE,"E23.60.11"),sQuery(id+"F0.wireOp",EDGE,"E23.61.0"),sQuery(id+"F0.wireOp",EDGE,"E23.61.1"),sQuery(id+"F0.wireOp",EDGE,"E23.61.2"),sQuery(id+"F0.wireOp",EDGE,"E23.61.3"),sQuery(id+"F0.wireOp",EDGE,"E23.61.4"),sQuery(id+"F0.wireOp",EDGE,"E23.61.5"),sQuery(id+"F0.wireOp",EDGE,"E23.61.6"),sQuery(id+"F0.wireOp",EDGE,"E23.61.7"),sQuery(id+"F0.wireOp",EDGE,"E23.61.8"),sQuery(id+"F0.wireOp",EDGE,"E23.61.9"),sQuery(id+"F0.wireOp",EDGE,"E23.61.10"),sQuery(id+"F0.wireOp",EDGE,"E23.61.11"),sQuery(id+"F0.wireOp",EDGE,"E23.62.0"),sQuery(id+"F0.wireOp",EDGE,"E23.62.1"),sQuery(id+"F0.wireOp",EDGE,"E23.62.2"),sQuery(id+"F0.wireOp",EDGE,"E23.62.3"),sQuery(id+"F0.wireOp",EDGE,"E23.62.4"),sQuery(id+"F0.wireOp",EDGE,"E23.62.5"),sQuery(id+"F0.wireOp",EDGE,"E23.62.6"),sQuery(id+"F0.wireOp",EDGE,"E23.62.7"),sQuery(id+"F0.wireOp",EDGE,"E23.62.8"),sQuery(id+"F0.wireOp",EDGE,"E23.62.9"),sQuery(id+"F0.wireOp",EDGE,"E23.62.10"),sQuery(id+"F0.wireOp",EDGE,"E23.62.11"),sQuery(id+"F0.wireOp",EDGE,"E23.63.0"),sQuery(id+"F0.wireOp",EDGE,"E23.63.1"),sQuery(id+"F0.wireOp",EDGE,"E23.63.2"),sQuery(id+"F0.wireOp",EDGE,"E23.63.3"),sQuery(id+"F0.wireOp",EDGE,"E23.63.4"),sQuery(id+"F0.wireOp",EDGE,"E23.63.5"),sQuery(id+"F0.wireOp",EDGE,"E23.63.6"),sQuery(id+"F0.wireOp",EDGE,"E23.63.7"),sQuery(id+"F0.wireOp",EDGE,"E23.63.8"),sQuery(id+"F0.wireOp",EDGE,"E23.63.9"),sQuery(id+"F0.wireOp",EDGE,"E23.63.10"),sQuery(id+"F0.wireOp",EDGE,"E23.63.11"),sQuery(id+"F0.wireOp",EDGE,"E23.64.0"),sQuery(id+"F0.wireOp",EDGE,"E23.64.1"),sQuery(id+"F0.wireOp",EDGE,"E23.64.2"),sQuery(id+"F0.wireOp",EDGE,"E23.64.3"),sQuery(id+"F0.wireOp",EDGE,"E23.64.4"),sQuery(id+"F0.wireOp",EDGE,"E23.64.5"),sQuery(id+"F0.wireOp",EDGE,"E23.64.6"),sQuery(id+"F0.wireOp",EDGE,"E23.64.7"),sQuery(id+"F0.wireOp",EDGE,"E23.64.8"),sQuery(id+"F0.wireOp",EDGE,"E23.64.9"),sQuery(id+"F0.wireOp",EDGE,"E23.64.10"),sQuery(id+"F0.wireOp",EDGE,"E23.64.11"),sQuery(id+"F0.wireOp",EDGE,"E23.65.0"),sQuery(id+"F0.wireOp",EDGE,"E23.65.1"),sQuery(id+"F0.wireOp",EDGE,"E23.65.2"),sQuery(id+"F0.wireOp",EDGE,"E23.65.3"),sQuery(id+"F0.wireOp",EDGE,"E23.65.4"),sQuery(id+"F0.wireOp",EDGE,"E23.65.5"),sQuery(id+"F0.wireOp",EDGE,"E23.65.6"),sQuery(id+"F0.wireOp",EDGE,"E23.65.7"),sQuery(id+"F0.wireOp",EDGE,"E23.65.8"),sQuery(id+"F0.wireOp",EDGE,"E23.65.9"),sQuery(id+"F0.wireOp",EDGE,"E23.65.10"),sQuery(id+"F0.wireOp",EDGE,"E23.65.11"),sQuery(id+"F0.wireOp",EDGE,"E23.66.0"),sQuery(id+"F0.wireOp",EDGE,"E23.66.1"),sQuery(id+"F0.wireOp",EDGE,"E23.66.2"),sQuery(id+"F0.wireOp",EDGE,"E23.66.3"),sQuery(id+"F0.wireOp",EDGE,"E23.66.4"),sQuery(id+"F0.wireOp",EDGE,"E23.66.5"),sQuery(id+"F0.wireOp",EDGE,"E23.66.6"),sQuery(id+"F0.wireOp",EDGE,"E23.66.7"),sQuery(id+"F0.wireOp",EDGE,"E23.66.8"),sQuery(id+"F0.wireOp",EDGE,"E23.66.9"),sQuery(id+"F0.wireOp",EDGE,"E23.66.10"),sQuery(id+"F0.wireOp",EDGE,"E23.66.11"),sQuery(id+"F0.wireOp",EDGE,"E23.67.0"),sQuery(id+"F0.wireOp",EDGE,"E23.67.1"),sQuery(id+"F0.wireOp",EDGE,"E23.67.2"),sQuery(id+"F0.wireOp",EDGE,"E23.67.3"),sQuery(id+"F0.wireOp",EDGE,"E23.67.4"),sQuery(id+"F0.wireOp",EDGE,"E23.67.5"),sQuery(id+"F0.wireOp",EDGE,"E23.67.6"),sQuery(id+"F0.wireOp",EDGE,"E23.67.7"),sQuery(id+"F0.wireOp",EDGE,"E23.67.8"),sQuery(id+"F0.wireOp",EDGE,"E23.67.9"),sQuery(id+"F0.wireOp",EDGE,"E23.67.10"),sQuery(id+"F0.wireOp",EDGE,"E23.67.11"),sQuery(id+"F0.wireOp",EDGE,"E23.68.0"),sQuery(id+"F0.wireOp",EDGE,"E23.68.1"),sQuery(id+"F0.wireOp",EDGE,"E23.68.2"),sQuery(id+"F0.wireOp",EDGE,"E23.68.3"),sQuery(id+"F0.wireOp",EDGE,"E23.68.4"),sQuery(id+"F0.wireOp",EDGE,"E23.68.5"),sQuery(id+"F0.wireOp",EDGE,"E23.68.6"),sQuery(id+"F0.wireOp",EDGE,"E23.68.7"),sQuery(id+"F0.wireOp",EDGE,"E23.68.8"),sQuery(id+"F0.wireOp",EDGE,"E23.68.9"),sQuery(id+"F0.wireOp",EDGE,"E23.68.10"),sQuery(id+"F0.wireOp",EDGE,"E23.68.11"),sQuery(id+"F0.wireOp",EDGE,"E23.69.0"),sQuery(id+"F0.wireOp",EDGE,"E23.69.1"),sQuery(id+"F0.wireOp",EDGE,"E23.69.2"),sQuery(id+"F0.wireOp",EDGE,"E23.69.3"),sQuery(id+"F0.wireOp",EDGE,"E23.69.4"),sQuery(id+"F0.wireOp",EDGE,"E23.69.5"),sQuery(id+"F0.wireOp",EDGE,"E23.69.6"),sQuery(id+"F0.wireOp",EDGE,"E23.69.7"),sQuery(id+"F0.wireOp",EDGE,"E23.69.8"),sQuery(id+"F0.wireOp",EDGE,"E23.69.9"),sQuery(id+"F0.wireOp",EDGE,"E23.69.10"),sQuery(id+"F0.wireOp",EDGE,"E23.69.11"),sQuery(id+"F0.wireOp",EDGE,"E23.70.0"),sQuery(id+"F0.wireOp",EDGE,"E23.70.1"),sQuery(id+"F0.wireOp",EDGE,"E23.70.2"),sQuery(id+"F0.wireOp",EDGE,"E23.70.3"),sQuery(id+"F0.wireOp",EDGE,"E23.70.4"),sQuery(id+"F0.wireOp",EDGE,"E23.70.5"),sQuery(id+"F0.wireOp",EDGE,"E23.70.6"),sQuery(id+"F0.wireOp",EDGE,"E23.70.7"),sQuery(id+"F0.wireOp",EDGE,"E23.70.8"),sQuery(id+"F0.wireOp",EDGE,"E23.70.9"),sQuery(id+"F0.wireOp",EDGE,"E23.70.10"),sQuery(id+"F0.wireOp",EDGE,"E23.70.11"),sQuery(id+"F0.wireOp",EDGE,"E23.71.0"),sQuery(id+"F0.wireOp",EDGE,"E23.71.1"),sQuery(id+"F0.wireOp",EDGE,"E23.71.2"),sQuery(id+"F0.wireOp",EDGE,"E23.71.3"),sQuery(id+"F0.wireOp",EDGE,"E23.71.4"),sQuery(id+"F0.wireOp",EDGE,"E23.71.5"),sQuery(id+"F0.wireOp",EDGE,"E23.71.6"),sQuery(id+"F0.wireOp",EDGE,"E23.71.7"),sQuery(id+"F0.wireOp",EDGE,"E23.71.8"),sQuery(id+"F0.wireOp",EDGE,"E23.71.9"),sQuery(id+"F0.wireOp",EDGE,"E23.71.10"),sQuery(id+"F0.wireOp",EDGE,"E23.71.11"),sQuery(id+"F0.wireOp",EDGE,"E24.trimOffspring"),sQuery(id+"F0.wireOp",EDGE,"E25.trimOffspring"),sQuery(id+"F0.wireOp",EDGE,"E26.trimOffspring"),sQuery(id+"F0.wireOp",EDGE,"E27.trimOffspring"),sQuery(id+"F0.wireOp",EDGE,"E28.trimOffspring"),sQuery(id+"F0.wireOp",EDGE,"E29.trimOffspring"),sQuery(id+"F0.wireOp",EDGE,"E30.trimOffspring"),sQuery(id+"F0.wireOp",EDGE,"E31.trimOffspring"),sQuery(id+"F0.wireOp",EDGE,"E32.trimOffspring"),sQuery(id+"F0.wireOp",EDGE,"E33.trimOffspring"),sQuery(id+"F0.wireOp",EDGE,"E34.trimOffspring"),sQuery(id+"F0.wireOp",EDGE,"E35.trimOffspring"),sQuery(id+"F0.wireOp",EDGE,"E36.trimOffspring"),sQuery(id+"F0.wireOp",EDGE,"E37.trimOffspring"),sQuery(id+"F0.wireOp",EDGE,"E38.trimOffspring"),sQuery(id+"F0.wireOp",EDGE,"E39.trimOffspring"),sQuery(id+"F0.wireOp",EDGE,"E40.trimOffspring"),sQuery(id+"F0.wireOp",EDGE,"E41.trimOffspring"),sQuery(id+"F0.wireOp",EDGE,"E42.trimOffspring"),sQuery(id+"F0.wireOp",EDGE,"E43.trimOffspring"),sQuery(id+"F0.wireOp",EDGE,"E44.trimOffspring"),sQuery(id+"F0.wireOp",EDGE,"E45.trimOffspring"),sQuery(id+"F0.wireOp",EDGE,"E46.trimOffspring"),sQuery(id+"F0.wireOp",EDGE,"E47.trimOffspring"),sQuery(id+"F0.wireOp",EDGE,"E48.trimOffspring"),sQuery(id+"F0.wireOp",EDGE,"E49.trimOffspring"),sQuery(id+"F0.wireOp",EDGE,"E50.trimOffspring"),sQuery(id+"F0.wireOp",EDGE,"E51.trimOffspring"),sQuery(id+"F0.wireOp",EDGE,"E52.trimOffspring"),sQuery(id+"F0.wireOp",EDGE,"E53.trimOffspring"),sQuery(id+"F0.wireOp",EDGE,"E54.trimOffspring"),sQuery(id+"F0.wireOp",EDGE,"E55.trimOffspring"),sQuery(id+"F0.wireOp",EDGE,"E56.trimOffspring"),sQuery(id+"F0.wireOp",EDGE,"E57.trimOffspring"),sQuery(id+"F0.wireOp",EDGE,"E58.trimOffspring"),sQuery(id+"F0.wireOp",EDGE,"E59.trimOffspring"),sQuery(id+"F0.wireOp",EDGE,"E60.trimOffspring"),sQuery(id+"F0.wireOp",EDGE,"E61.trimOffspring"),sQuery(id+"F0.wireOp",EDGE,"E62.trimOffspring"),sQuery(id+"F0.wireOp",EDGE,"E63.trimOffspring"),sQuery(id+"F0.wireOp",EDGE,"E64.trimOffspring"),sQuery(id+"F0.wireOp",EDGE,"E65.trimOffspring"),sQuery(id+"F0.wireOp",EDGE,"E66.trimOffspring"),sQuery(id+"F0.wireOp",EDGE,"E67.trimOffspring"),sQuery(id+"F0.wireOp",EDGE,"E68.trimOffspring"),sQuery(id+"F0.wireOp",EDGE,"E69.trimOffspring"),sQuery(id+"F0.wireOp",EDGE,"E70.trimOffspring"),sQuery(id+"F0.wireOp",EDGE,"E71.trimOffspring"),sQuery(id+"F0.wireOp",EDGE,"E72.trimOffspring"),sQuery(id+"F0.wireOp",EDGE,"E73.trimOffspring"),sQuery(id+"F0.wireOp",EDGE,"E74.trimOffspring"),sQuery(id+"F0.wireOp",EDGE,"E75.trimOffspring"),sQuery(id+"F0.wireOp",EDGE,"E76.trimOffspring"),sQuery(id+"F0.wireOp",EDGE,"E77.trimOffspring"),sQuery(id+"F0.wireOp",EDGE,"E78.trimOffspring"),sQuery(id+"F0.wireOp",EDGE,"E79.trimOffspring"),sQuery(id+"F0.wireOp",EDGE,"E80.trimOffspring"),sQuery(id+"F0.wireOp",EDGE,"E81.trimOffspring"),sQuery(id+"F0.wireOp",EDGE,"E82.trimOffspring"),sQuery(id+"F0.wireOp",EDGE,"E83.trimOffspring"),sQuery(id+"F0.wireOp",EDGE,"E84.trimOffspring"),sQuery(id+"F0.wireOp",EDGE,"E85.trimOffspring"),sQuery(id+"F0.wireOp",EDGE,"E86.trimOffspring"),sQuery(id+"F0.wireOp",EDGE,"E87.trimOffspring"),sQuery(id+"F0.wireOp",EDGE,"E88.trimOffspring"),sQuery(id+"F0.wireOp",EDGE,"E89.trimOffspring"),sQuery(id+"F0.wireOp",EDGE,"E90.trimOffspring"),sQuery(id+"F0.wireOp",EDGE,"E91.trimOffspring"),sQuery(id+"F0.wireOp",EDGE,"E92.trimOffspring"),sQuery(id+"F0.wireOp",EDGE,"E93.trimOffspring"),sQuery(id+"F0.wireOp",EDGE,"E94")])]});
            hole(context, id + "F16", {"style" : HoleStyle.SIMPLE, "endStyle" : HoleEndStyle.BLIND, "holeDiameter" : 8 * mm, "holeDepth" : 10 * mm, "isTappedThrough" : true, "tappedDepth" : 12.3 * mm, "tapClearance" : 6, "locations" : qUnion([Q0, Q1, Q2, Q3]), "scope" : qUnion([Q4])});
        }
        {
            var Q0;
            Q0=makeQuery(id+"F2.opExtrude","CAP_FACE",FACE,{"disambiguationData":[OSD([sQuery(id+"F0.wireOp",EDGE,"E0"),sQuery(id+"F0.wireOp",EDGE,"E1.MirrorCS"),sQuery(id+"F0.wireOp",EDGE,"E2.MirrorCS"),sQuery(id+"F0.wireOp",EDGE,"E3.MirrorCS"),sQuery(id+"F0.wireOp",EDGE,"E4.MirrorCS"),sQuery(id+"F0.wireOp",EDGE,"E5.MirrorCS"),sQuery(id+"F0.wireOp",EDGE,"E6.MirrorCS"),sQuery(id+"F0.wireOp",EDGE,"E16.filletArc"),sQuery(id+"F0.wireOp",EDGE,"E17.filletArc"),sQuery(id+"F0.wireOp",EDGE,"E18.filletArc"),sQuery(id+"F0.wireOp",EDGE,"E19.filletArc"),sQuery(id+"F0.wireOp",EDGE,"E20.filletArc"),sQuery(id+"F0.wireOp",EDGE,"E21.filletArc"),sQuery(id+"F0.wireOp",EDGE,"E22"),sQuery(id+"F0.wireOp",EDGE,"E23.1.0"),sQuery(id+"F0.wireOp",EDGE,"E23.1.1"),sQuery(id+"F0.wireOp",EDGE,"E23.1.2"),sQuery(id+"F0.wireOp",EDGE,"E23.1.3"),sQuery(id+"F0.wireOp",EDGE,"E23.1.4"),sQuery(id+"F0.wireOp",EDGE,"E23.1.5"),sQuery(id+"F0.wireOp",EDGE,"E23.1.6"),sQuery(id+"F0.wireOp",EDGE,"E23.1.7"),sQuery(id+"F0.wireOp",EDGE,"E23.1.8"),sQuery(id+"F0.wireOp",EDGE,"E23.1.9"),sQuery(id+"F0.wireOp",EDGE,"E23.1.10"),sQuery(id+"F0.wireOp",EDGE,"E23.1.11"),sQuery(id+"F0.wireOp",EDGE,"E23.2.0"),sQuery(id+"F0.wireOp",EDGE,"E23.2.1"),sQuery(id+"F0.wireOp",EDGE,"E23.2.2"),sQuery(id+"F0.wireOp",EDGE,"E23.2.3"),sQuery(id+"F0.wireOp",EDGE,"E23.2.4"),sQuery(id+"F0.wireOp",EDGE,"E23.2.5"),sQuery(id+"F0.wireOp",EDGE,"E23.2.6"),sQuery(id+"F0.wireOp",EDGE,"E23.2.7"),sQuery(id+"F0.wireOp",EDGE,"E23.2.8"),sQuery(id+"F0.wireOp",EDGE,"E23.2.9"),sQuery(id+"F0.wireOp",EDGE,"E23.2.10"),sQuery(id+"F0.wireOp",EDGE,"E23.2.11"),sQuery(id+"F0.wireOp",EDGE,"E23.3.0"),sQuery(id+"F0.wireOp",EDGE,"E23.3.1"),sQuery(id+"F0.wireOp",EDGE,"E23.3.2"),sQuery(id+"F0.wireOp",EDGE,"E23.3.3"),sQuery(id+"F0.wireOp",EDGE,"E23.3.4"),sQuery(id+"F0.wireOp",EDGE,"E23.3.5"),sQuery(id+"F0.wireOp",EDGE,"E23.3.6"),sQuery(id+"F0.wireOp",EDGE,"E23.3.7"),sQuery(id+"F0.wireOp",EDGE,"E23.3.8"),sQuery(id+"F0.wireOp",EDGE,"E23.3.9"),sQuery(id+"F0.wireOp",EDGE,"E23.3.10"),sQuery(id+"F0.wireOp",EDGE,"E23.3.11"),sQuery(id+"F0.wireOp",EDGE,"E23.4.0"),sQuery(id+"F0.wireOp",EDGE,"E23.4.1"),sQuery(id+"F0.wireOp",EDGE,"E23.4.2"),sQuery(id+"F0.wireOp",EDGE,"E23.4.3"),sQuery(id+"F0.wireOp",EDGE,"E23.4.4"),sQuery(id+"F0.wireOp",EDGE,"E23.4.5"),sQuery(id+"F0.wireOp",EDGE,"E23.4.6"),sQuery(id+"F0.wireOp",EDGE,"E23.4.7"),sQuery(id+"F0.wireOp",EDGE,"E23.4.8"),sQuery(id+"F0.wireOp",EDGE,"E23.4.9"),sQuery(id+"F0.wireOp",EDGE,"E23.4.10"),sQuery(id+"F0.wireOp",EDGE,"E23.4.11"),sQuery(id+"F0.wireOp",EDGE,"E23.5.0"),sQuery(id+"F0.wireOp",EDGE,"E23.5.1"),sQuery(id+"F0.wireOp",EDGE,"E23.5.2"),sQuery(id+"F0.wireOp",EDGE,"E23.5.3"),sQuery(id+"F0.wireOp",EDGE,"E23.5.4"),sQuery(id+"F0.wireOp",EDGE,"E23.5.5"),sQuery(id+"F0.wireOp",EDGE,"E23.5.6"),sQuery(id+"F0.wireOp",EDGE,"E23.5.7"),sQuery(id+"F0.wireOp",EDGE,"E23.5.8"),sQuery(id+"F0.wireOp",EDGE,"E23.5.9"),sQuery(id+"F0.wireOp",EDGE,"E23.5.10"),sQuery(id+"F0.wireOp",EDGE,"E23.5.11"),sQuery(id+"F0.wireOp",EDGE,"E23.6.0"),sQuery(id+"F0.wireOp",EDGE,"E23.6.1"),sQuery(id+"F0.wireOp",EDGE,"E23.6.2"),sQuery(id+"F0.wireOp",EDGE,"E23.6.3"),sQuery(id+"F0.wireOp",EDGE,"E23.6.4"),sQuery(id+"F0.wireOp",EDGE,"E23.6.5"),sQuery(id+"F0.wireOp",EDGE,"E23.6.6"),sQuery(id+"F0.wireOp",EDGE,"E23.6.7"),sQuery(id+"F0.wireOp",EDGE,"E23.6.8"),sQuery(id+"F0.wireOp",EDGE,"E23.6.9"),sQuery(id+"F0.wireOp",EDGE,"E23.6.10"),sQuery(id+"F0.wireOp",EDGE,"E23.6.11"),sQuery(id+"F0.wireOp",EDGE,"E23.7.0"),sQuery(id+"F0.wireOp",EDGE,"E23.7.1"),sQuery(id+"F0.wireOp",EDGE,"E23.7.2"),sQuery(id+"F0.wireOp",EDGE,"E23.7.3"),sQuery(id+"F0.wireOp",EDGE,"E23.7.4"),sQuery(id+"F0.wireOp",EDGE,"E23.7.5"),sQuery(id+"F0.wireOp",EDGE,"E23.7.6"),sQuery(id+"F0.wireOp",EDGE,"E23.7.7"),sQuery(id+"F0.wireOp",EDGE,"E23.7.8"),sQuery(id+"F0.wireOp",EDGE,"E23.7.9"),sQuery(id+"F0.wireOp",EDGE,"E23.7.10"),sQuery(id+"F0.wireOp",EDGE,"E23.7.11"),sQuery(id+"F0.wireOp",EDGE,"E23.8.0"),sQuery(id+"F0.wireOp",EDGE,"E23.8.1"),sQuery(id+"F0.wireOp",EDGE,"E23.8.2"),sQuery(id+"F0.wireOp",EDGE,"E23.8.3"),sQuery(id+"F0.wireOp",EDGE,"E23.8.4"),sQuery(id+"F0.wireOp",EDGE,"E23.8.5"),sQuery(id+"F0.wireOp",EDGE,"E23.8.6"),sQuery(id+"F0.wireOp",EDGE,"E23.8.7"),sQuery(id+"F0.wireOp",EDGE,"E23.8.8"),sQuery(id+"F0.wireOp",EDGE,"E23.8.9"),sQuery(id+"F0.wireOp",EDGE,"E23.8.10"),sQuery(id+"F0.wireOp",EDGE,"E23.8.11"),sQuery(id+"F0.wireOp",EDGE,"E23.9.0"),sQuery(id+"F0.wireOp",EDGE,"E23.9.1"),sQuery(id+"F0.wireOp",EDGE,"E23.9.2"),sQuery(id+"F0.wireOp",EDGE,"E23.9.3"),sQuery(id+"F0.wireOp",EDGE,"E23.9.4"),sQuery(id+"F0.wireOp",EDGE,"E23.9.5"),sQuery(id+"F0.wireOp",EDGE,"E23.9.6"),sQuery(id+"F0.wireOp",EDGE,"E23.9.7"),sQuery(id+"F0.wireOp",EDGE,"E23.9.8"),sQuery(id+"F0.wireOp",EDGE,"E23.9.9"),sQuery(id+"F0.wireOp",EDGE,"E23.9.10"),sQuery(id+"F0.wireOp",EDGE,"E23.9.11"),sQuery(id+"F0.wireOp",EDGE,"E23.10.0"),sQuery(id+"F0.wireOp",EDGE,"E23.10.1"),sQuery(id+"F0.wireOp",EDGE,"E23.10.2"),sQuery(id+"F0.wireOp",EDGE,"E23.10.3"),sQuery(id+"F0.wireOp",EDGE,"E23.10.4"),sQuery(id+"F0.wireOp",EDGE,"E23.10.5"),sQuery(id+"F0.wireOp",EDGE,"E23.10.6"),sQuery(id+"F0.wireOp",EDGE,"E23.10.7"),sQuery(id+"F0.wireOp",EDGE,"E23.10.8"),sQuery(id+"F0.wireOp",EDGE,"E23.10.9"),sQuery(id+"F0.wireOp",EDGE,"E23.10.10"),sQuery(id+"F0.wireOp",EDGE,"E23.10.11"),sQuery(id+"F0.wireOp",EDGE,"E23.11.0"),sQuery(id+"F0.wireOp",EDGE,"E23.11.1"),sQuery(id+"F0.wireOp",EDGE,"E23.11.2"),sQuery(id+"F0.wireOp",EDGE,"E23.11.3"),sQuery(id+"F0.wireOp",EDGE,"E23.11.4"),sQuery(id+"F0.wireOp",EDGE,"E23.11.5"),sQuery(id+"F0.wireOp",EDGE,"E23.11.6"),sQuery(id+"F0.wireOp",EDGE,"E23.11.7"),sQuery(id+"F0.wireOp",EDGE,"E23.11.8"),sQuery(id+"F0.wireOp",EDGE,"E23.11.9"),sQuery(id+"F0.wireOp",EDGE,"E23.11.10"),sQuery(id+"F0.wireOp",EDGE,"E23.11.11"),sQuery(id+"F0.wireOp",EDGE,"E23.12.0"),sQuery(id+"F0.wireOp",EDGE,"E23.12.1"),sQuery(id+"F0.wireOp",EDGE,"E23.12.2"),sQuery(id+"F0.wireOp",EDGE,"E23.12.3"),sQuery(id+"F0.wireOp",EDGE,"E23.12.4"),sQuery(id+"F0.wireOp",EDGE,"E23.12.5"),sQuery(id+"F0.wireOp",EDGE,"E23.12.6"),sQuery(id+"F0.wireOp",EDGE,"E23.12.7"),sQuery(id+"F0.wireOp",EDGE,"E23.12.8"),sQuery(id+"F0.wireOp",EDGE,"E23.12.9"),sQuery(id+"F0.wireOp",EDGE,"E23.12.10"),sQuery(id+"F0.wireOp",EDGE,"E23.12.11"),sQuery(id+"F0.wireOp",EDGE,"E23.13.0"),sQuery(id+"F0.wireOp",EDGE,"E23.13.1"),sQuery(id+"F0.wireOp",EDGE,"E23.13.2"),sQuery(id+"F0.wireOp",EDGE,"E23.13.3"),sQuery(id+"F0.wireOp",EDGE,"E23.13.4"),sQuery(id+"F0.wireOp",EDGE,"E23.13.5"),sQuery(id+"F0.wireOp",EDGE,"E23.13.6"),sQuery(id+"F0.wireOp",EDGE,"E23.13.7"),sQuery(id+"F0.wireOp",EDGE,"E23.13.8"),sQuery(id+"F0.wireOp",EDGE,"E23.13.9"),sQuery(id+"F0.wireOp",EDGE,"E23.13.10"),sQuery(id+"F0.wireOp",EDGE,"E23.13.11"),sQuery(id+"F0.wireOp",EDGE,"E23.14.0"),sQuery(id+"F0.wireOp",EDGE,"E23.14.1"),sQuery(id+"F0.wireOp",EDGE,"E23.14.2"),sQuery(id+"F0.wireOp",EDGE,"E23.14.3"),sQuery(id+"F0.wireOp",EDGE,"E23.14.4"),sQuery(id+"F0.wireOp",EDGE,"E23.14.5"),sQuery(id+"F0.wireOp",EDGE,"E23.14.6"),sQuery(id+"F0.wireOp",EDGE,"E23.14.7"),sQuery(id+"F0.wireOp",EDGE,"E23.14.8"),sQuery(id+"F0.wireOp",EDGE,"E23.14.9"),sQuery(id+"F0.wireOp",EDGE,"E23.14.10"),sQuery(id+"F0.wireOp",EDGE,"E23.14.11"),sQuery(id+"F0.wireOp",EDGE,"E23.15.0"),sQuery(id+"F0.wireOp",EDGE,"E23.15.1"),sQuery(id+"F0.wireOp",EDGE,"E23.15.2"),sQuery(id+"F0.wireOp",EDGE,"E23.15.3"),sQuery(id+"F0.wireOp",EDGE,"E23.15.4"),sQuery(id+"F0.wireOp",EDGE,"E23.15.5"),sQuery(id+"F0.wireOp",EDGE,"E23.15.6"),sQuery(id+"F0.wireOp",EDGE,"E23.15.7"),sQuery(id+"F0.wireOp",EDGE,"E23.15.8"),sQuery(id+"F0.wireOp",EDGE,"E23.15.9"),sQuery(id+"F0.wireOp",EDGE,"E23.15.10"),sQuery(id+"F0.wireOp",EDGE,"E23.15.11"),sQuery(id+"F0.wireOp",EDGE,"E23.16.0"),sQuery(id+"F0.wireOp",EDGE,"E23.16.1"),sQuery(id+"F0.wireOp",EDGE,"E23.16.2"),sQuery(id+"F0.wireOp",EDGE,"E23.16.3"),sQuery(id+"F0.wireOp",EDGE,"E23.16.4"),sQuery(id+"F0.wireOp",EDGE,"E23.16.5"),sQuery(id+"F0.wireOp",EDGE,"E23.16.6"),sQuery(id+"F0.wireOp",EDGE,"E23.16.7"),sQuery(id+"F0.wireOp",EDGE,"E23.16.8"),sQuery(id+"F0.wireOp",EDGE,"E23.16.9"),sQuery(id+"F0.wireOp",EDGE,"E23.16.10"),sQuery(id+"F0.wireOp",EDGE,"E23.16.11"),sQuery(id+"F0.wireOp",EDGE,"E23.17.0"),sQuery(id+"F0.wireOp",EDGE,"E23.17.1"),sQuery(id+"F0.wireOp",EDGE,"E23.17.2"),sQuery(id+"F0.wireOp",EDGE,"E23.17.3"),sQuery(id+"F0.wireOp",EDGE,"E23.17.4"),sQuery(id+"F0.wireOp",EDGE,"E23.17.5"),sQuery(id+"F0.wireOp",EDGE,"E23.17.6"),sQuery(id+"F0.wireOp",EDGE,"E23.17.7"),sQuery(id+"F0.wireOp",EDGE,"E23.17.8"),sQuery(id+"F0.wireOp",EDGE,"E23.17.9"),sQuery(id+"F0.wireOp",EDGE,"E23.17.10"),sQuery(id+"F0.wireOp",EDGE,"E23.17.11"),sQuery(id+"F0.wireOp",EDGE,"E23.18.0"),sQuery(id+"F0.wireOp",EDGE,"E23.18.1"),sQuery(id+"F0.wireOp",EDGE,"E23.18.2"),sQuery(id+"F0.wireOp",EDGE,"E23.18.3"),sQuery(id+"F0.wireOp",EDGE,"E23.18.4"),sQuery(id+"F0.wireOp",EDGE,"E23.18.5"),sQuery(id+"F0.wireOp",EDGE,"E23.18.6"),sQuery(id+"F0.wireOp",EDGE,"E23.18.7"),sQuery(id+"F0.wireOp",EDGE,"E23.18.8"),sQuery(id+"F0.wireOp",EDGE,"E23.18.9"),sQuery(id+"F0.wireOp",EDGE,"E23.18.10"),sQuery(id+"F0.wireOp",EDGE,"E23.18.11"),sQuery(id+"F0.wireOp",EDGE,"E23.19.0"),sQuery(id+"F0.wireOp",EDGE,"E23.19.1"),sQuery(id+"F0.wireOp",EDGE,"E23.19.2"),sQuery(id+"F0.wireOp",EDGE,"E23.19.3"),sQuery(id+"F0.wireOp",EDGE,"E23.19.4"),sQuery(id+"F0.wireOp",EDGE,"E23.19.5"),sQuery(id+"F0.wireOp",EDGE,"E23.19.6"),sQuery(id+"F0.wireOp",EDGE,"E23.19.7"),sQuery(id+"F0.wireOp",EDGE,"E23.19.8"),sQuery(id+"F0.wireOp",EDGE,"E23.19.9"),sQuery(id+"F0.wireOp",EDGE,"E23.19.10"),sQuery(id+"F0.wireOp",EDGE,"E23.19.11"),sQuery(id+"F0.wireOp",EDGE,"E23.20.0"),sQuery(id+"F0.wireOp",EDGE,"E23.20.1"),sQuery(id+"F0.wireOp",EDGE,"E23.20.2"),sQuery(id+"F0.wireOp",EDGE,"E23.20.3"),sQuery(id+"F0.wireOp",EDGE,"E23.20.4"),sQuery(id+"F0.wireOp",EDGE,"E23.20.5"),sQuery(id+"F0.wireOp",EDGE,"E23.20.6"),sQuery(id+"F0.wireOp",EDGE,"E23.20.7"),sQuery(id+"F0.wireOp",EDGE,"E23.20.8"),sQuery(id+"F0.wireOp",EDGE,"E23.20.9"),sQuery(id+"F0.wireOp",EDGE,"E23.20.10"),sQuery(id+"F0.wireOp",EDGE,"E23.20.11"),sQuery(id+"F0.wireOp",EDGE,"E23.21.0"),sQuery(id+"F0.wireOp",EDGE,"E23.21.1"),sQuery(id+"F0.wireOp",EDGE,"E23.21.2"),sQuery(id+"F0.wireOp",EDGE,"E23.21.3"),sQuery(id+"F0.wireOp",EDGE,"E23.21.4"),sQuery(id+"F0.wireOp",EDGE,"E23.21.5"),sQuery(id+"F0.wireOp",EDGE,"E23.21.6"),sQuery(id+"F0.wireOp",EDGE,"E23.21.7"),sQuery(id+"F0.wireOp",EDGE,"E23.21.8"),sQuery(id+"F0.wireOp",EDGE,"E23.21.9"),sQuery(id+"F0.wireOp",EDGE,"E23.21.10"),sQuery(id+"F0.wireOp",EDGE,"E23.21.11"),sQuery(id+"F0.wireOp",EDGE,"E23.22.0"),sQuery(id+"F0.wireOp",EDGE,"E23.22.1"),sQuery(id+"F0.wireOp",EDGE,"E23.22.2"),sQuery(id+"F0.wireOp",EDGE,"E23.22.3"),sQuery(id+"F0.wireOp",EDGE,"E23.22.4"),sQuery(id+"F0.wireOp",EDGE,"E23.22.5"),sQuery(id+"F0.wireOp",EDGE,"E23.22.6"),sQuery(id+"F0.wireOp",EDGE,"E23.22.7"),sQuery(id+"F0.wireOp",EDGE,"E23.22.8"),sQuery(id+"F0.wireOp",EDGE,"E23.22.9"),sQuery(id+"F0.wireOp",EDGE,"E23.22.10"),sQuery(id+"F0.wireOp",EDGE,"E23.22.11"),sQuery(id+"F0.wireOp",EDGE,"E23.23.0"),sQuery(id+"F0.wireOp",EDGE,"E23.23.1"),sQuery(id+"F0.wireOp",EDGE,"E23.23.2"),sQuery(id+"F0.wireOp",EDGE,"E23.23.3"),sQuery(id+"F0.wireOp",EDGE,"E23.23.4"),sQuery(id+"F0.wireOp",EDGE,"E23.23.5"),sQuery(id+"F0.wireOp",EDGE,"E23.23.6"),sQuery(id+"F0.wireOp",EDGE,"E23.23.7"),sQuery(id+"F0.wireOp",EDGE,"E23.23.8"),sQuery(id+"F0.wireOp",EDGE,"E23.23.9"),sQuery(id+"F0.wireOp",EDGE,"E23.23.10"),sQuery(id+"F0.wireOp",EDGE,"E23.23.11"),sQuery(id+"F0.wireOp",EDGE,"E23.24.0"),sQuery(id+"F0.wireOp",EDGE,"E23.24.1"),sQuery(id+"F0.wireOp",EDGE,"E23.24.2"),sQuery(id+"F0.wireOp",EDGE,"E23.24.3"),sQuery(id+"F0.wireOp",EDGE,"E23.24.4"),sQuery(id+"F0.wireOp",EDGE,"E23.24.5"),sQuery(id+"F0.wireOp",EDGE,"E23.24.6"),sQuery(id+"F0.wireOp",EDGE,"E23.24.7"),sQuery(id+"F0.wireOp",EDGE,"E23.24.8"),sQuery(id+"F0.wireOp",EDGE,"E23.24.9"),sQuery(id+"F0.wireOp",EDGE,"E23.24.10"),sQuery(id+"F0.wireOp",EDGE,"E23.24.11"),sQuery(id+"F0.wireOp",EDGE,"E23.25.0"),sQuery(id+"F0.wireOp",EDGE,"E23.25.1"),sQuery(id+"F0.wireOp",EDGE,"E23.25.2"),sQuery(id+"F0.wireOp",EDGE,"E23.25.3"),sQuery(id+"F0.wireOp",EDGE,"E23.25.4"),sQuery(id+"F0.wireOp",EDGE,"E23.25.5"),sQuery(id+"F0.wireOp",EDGE,"E23.25.6"),sQuery(id+"F0.wireOp",EDGE,"E23.25.7"),sQuery(id+"F0.wireOp",EDGE,"E23.25.8"),sQuery(id+"F0.wireOp",EDGE,"E23.25.9"),sQuery(id+"F0.wireOp",EDGE,"E23.25.10"),sQuery(id+"F0.wireOp",EDGE,"E23.25.11"),sQuery(id+"F0.wireOp",EDGE,"E23.26.0"),sQuery(id+"F0.wireOp",EDGE,"E23.26.1"),sQuery(id+"F0.wireOp",EDGE,"E23.26.2"),sQuery(id+"F0.wireOp",EDGE,"E23.26.3"),sQuery(id+"F0.wireOp",EDGE,"E23.26.4"),sQuery(id+"F0.wireOp",EDGE,"E23.26.5"),sQuery(id+"F0.wireOp",EDGE,"E23.26.6"),sQuery(id+"F0.wireOp",EDGE,"E23.26.7"),sQuery(id+"F0.wireOp",EDGE,"E23.26.8"),sQuery(id+"F0.wireOp",EDGE,"E23.26.9"),sQuery(id+"F0.wireOp",EDGE,"E23.26.10"),sQuery(id+"F0.wireOp",EDGE,"E23.26.11"),sQuery(id+"F0.wireOp",EDGE,"E23.27.0"),sQuery(id+"F0.wireOp",EDGE,"E23.27.1"),sQuery(id+"F0.wireOp",EDGE,"E23.27.2"),sQuery(id+"F0.wireOp",EDGE,"E23.27.3"),sQuery(id+"F0.wireOp",EDGE,"E23.27.4"),sQuery(id+"F0.wireOp",EDGE,"E23.27.5"),sQuery(id+"F0.wireOp",EDGE,"E23.27.6"),sQuery(id+"F0.wireOp",EDGE,"E23.27.7"),sQuery(id+"F0.wireOp",EDGE,"E23.27.8"),sQuery(id+"F0.wireOp",EDGE,"E23.27.9"),sQuery(id+"F0.wireOp",EDGE,"E23.27.10"),sQuery(id+"F0.wireOp",EDGE,"E23.27.11"),sQuery(id+"F0.wireOp",EDGE,"E23.28.0"),sQuery(id+"F0.wireOp",EDGE,"E23.28.1"),sQuery(id+"F0.wireOp",EDGE,"E23.28.2"),sQuery(id+"F0.wireOp",EDGE,"E23.28.3"),sQuery(id+"F0.wireOp",EDGE,"E23.28.4"),sQuery(id+"F0.wireOp",EDGE,"E23.28.5"),sQuery(id+"F0.wireOp",EDGE,"E23.28.6"),sQuery(id+"F0.wireOp",EDGE,"E23.28.7"),sQuery(id+"F0.wireOp",EDGE,"E23.28.8"),sQuery(id+"F0.wireOp",EDGE,"E23.28.9"),sQuery(id+"F0.wireOp",EDGE,"E23.28.10"),sQuery(id+"F0.wireOp",EDGE,"E23.28.11"),sQuery(id+"F0.wireOp",EDGE,"E23.29.0"),sQuery(id+"F0.wireOp",EDGE,"E23.29.1"),sQuery(id+"F0.wireOp",EDGE,"E23.29.2"),sQuery(id+"F0.wireOp",EDGE,"E23.29.3"),sQuery(id+"F0.wireOp",EDGE,"E23.29.4"),sQuery(id+"F0.wireOp",EDGE,"E23.29.5"),sQuery(id+"F0.wireOp",EDGE,"E23.29.6"),sQuery(id+"F0.wireOp",EDGE,"E23.29.7"),sQuery(id+"F0.wireOp",EDGE,"E23.29.8"),sQuery(id+"F0.wireOp",EDGE,"E23.29.9"),sQuery(id+"F0.wireOp",EDGE,"E23.29.10"),sQuery(id+"F0.wireOp",EDGE,"E23.29.11"),sQuery(id+"F0.wireOp",EDGE,"E23.30.0"),sQuery(id+"F0.wireOp",EDGE,"E23.30.1"),sQuery(id+"F0.wireOp",EDGE,"E23.30.2"),sQuery(id+"F0.wireOp",EDGE,"E23.30.3"),sQuery(id+"F0.wireOp",EDGE,"E23.30.4"),sQuery(id+"F0.wireOp",EDGE,"E23.30.5"),sQuery(id+"F0.wireOp",EDGE,"E23.30.6"),sQuery(id+"F0.wireOp",EDGE,"E23.30.7"),sQuery(id+"F0.wireOp",EDGE,"E23.30.8"),sQuery(id+"F0.wireOp",EDGE,"E23.30.9"),sQuery(id+"F0.wireOp",EDGE,"E23.30.10"),sQuery(id+"F0.wireOp",EDGE,"E23.30.11"),sQuery(id+"F0.wireOp",EDGE,"E23.31.0"),sQuery(id+"F0.wireOp",EDGE,"E23.31.1"),sQuery(id+"F0.wireOp",EDGE,"E23.31.2"),sQuery(id+"F0.wireOp",EDGE,"E23.31.3"),sQuery(id+"F0.wireOp",EDGE,"E23.31.4"),sQuery(id+"F0.wireOp",EDGE,"E23.31.5"),sQuery(id+"F0.wireOp",EDGE,"E23.31.6"),sQuery(id+"F0.wireOp",EDGE,"E23.31.7"),sQuery(id+"F0.wireOp",EDGE,"E23.31.8"),sQuery(id+"F0.wireOp",EDGE,"E23.31.9"),sQuery(id+"F0.wireOp",EDGE,"E23.31.10"),sQuery(id+"F0.wireOp",EDGE,"E23.31.11"),sQuery(id+"F0.wireOp",EDGE,"E23.32.0"),sQuery(id+"F0.wireOp",EDGE,"E23.32.1"),sQuery(id+"F0.wireOp",EDGE,"E23.32.2"),sQuery(id+"F0.wireOp",EDGE,"E23.32.3"),sQuery(id+"F0.wireOp",EDGE,"E23.32.4"),sQuery(id+"F0.wireOp",EDGE,"E23.32.5"),sQuery(id+"F0.wireOp",EDGE,"E23.32.6"),sQuery(id+"F0.wireOp",EDGE,"E23.32.7"),sQuery(id+"F0.wireOp",EDGE,"E23.32.8"),sQuery(id+"F0.wireOp",EDGE,"E23.32.9"),sQuery(id+"F0.wireOp",EDGE,"E23.32.10"),sQuery(id+"F0.wireOp",EDGE,"E23.32.11"),sQuery(id+"F0.wireOp",EDGE,"E23.33.0"),sQuery(id+"F0.wireOp",EDGE,"E23.33.1"),sQuery(id+"F0.wireOp",EDGE,"E23.33.2"),sQuery(id+"F0.wireOp",EDGE,"E23.33.3"),sQuery(id+"F0.wireOp",EDGE,"E23.33.4"),sQuery(id+"F0.wireOp",EDGE,"E23.33.5"),sQuery(id+"F0.wireOp",EDGE,"E23.33.6"),sQuery(id+"F0.wireOp",EDGE,"E23.33.7"),sQuery(id+"F0.wireOp",EDGE,"E23.33.8"),sQuery(id+"F0.wireOp",EDGE,"E23.33.9"),sQuery(id+"F0.wireOp",EDGE,"E23.33.10"),sQuery(id+"F0.wireOp",EDGE,"E23.33.11"),sQuery(id+"F0.wireOp",EDGE,"E23.34.0"),sQuery(id+"F0.wireOp",EDGE,"E23.34.1"),sQuery(id+"F0.wireOp",EDGE,"E23.34.2"),sQuery(id+"F0.wireOp",EDGE,"E23.34.3"),sQuery(id+"F0.wireOp",EDGE,"E23.34.4"),sQuery(id+"F0.wireOp",EDGE,"E23.34.5"),sQuery(id+"F0.wireOp",EDGE,"E23.34.6"),sQuery(id+"F0.wireOp",EDGE,"E23.34.7"),sQuery(id+"F0.wireOp",EDGE,"E23.34.8"),sQuery(id+"F0.wireOp",EDGE,"E23.34.9"),sQuery(id+"F0.wireOp",EDGE,"E23.34.10"),sQuery(id+"F0.wireOp",EDGE,"E23.34.11"),sQuery(id+"F0.wireOp",EDGE,"E23.35.0"),sQuery(id+"F0.wireOp",EDGE,"E23.35.1"),sQuery(id+"F0.wireOp",EDGE,"E23.35.2"),sQuery(id+"F0.wireOp",EDGE,"E23.35.3"),sQuery(id+"F0.wireOp",EDGE,"E23.35.4"),sQuery(id+"F0.wireOp",EDGE,"E23.35.5"),sQuery(id+"F0.wireOp",EDGE,"E23.35.6"),sQuery(id+"F0.wireOp",EDGE,"E23.35.7"),sQuery(id+"F0.wireOp",EDGE,"E23.35.8"),sQuery(id+"F0.wireOp",EDGE,"E23.35.9"),sQuery(id+"F0.wireOp",EDGE,"E23.35.10"),sQuery(id+"F0.wireOp",EDGE,"E23.35.11"),sQuery(id+"F0.wireOp",EDGE,"E23.36.0"),sQuery(id+"F0.wireOp",EDGE,"E23.36.1"),sQuery(id+"F0.wireOp",EDGE,"E23.36.2"),sQuery(id+"F0.wireOp",EDGE,"E23.36.3"),sQuery(id+"F0.wireOp",EDGE,"E23.36.4"),sQuery(id+"F0.wireOp",EDGE,"E23.36.5"),sQuery(id+"F0.wireOp",EDGE,"E23.36.6"),sQuery(id+"F0.wireOp",EDGE,"E23.36.7"),sQuery(id+"F0.wireOp",EDGE,"E23.36.8"),sQuery(id+"F0.wireOp",EDGE,"E23.36.9"),sQuery(id+"F0.wireOp",EDGE,"E23.36.10"),sQuery(id+"F0.wireOp",EDGE,"E23.36.11"),sQuery(id+"F0.wireOp",EDGE,"E23.37.0"),sQuery(id+"F0.wireOp",EDGE,"E23.37.1"),sQuery(id+"F0.wireOp",EDGE,"E23.37.2"),sQuery(id+"F0.wireOp",EDGE,"E23.37.3"),sQuery(id+"F0.wireOp",EDGE,"E23.37.4"),sQuery(id+"F0.wireOp",EDGE,"E23.37.5"),sQuery(id+"F0.wireOp",EDGE,"E23.37.6"),sQuery(id+"F0.wireOp",EDGE,"E23.37.7"),sQuery(id+"F0.wireOp",EDGE,"E23.37.8"),sQuery(id+"F0.wireOp",EDGE,"E23.37.9"),sQuery(id+"F0.wireOp",EDGE,"E23.37.10"),sQuery(id+"F0.wireOp",EDGE,"E23.37.11"),sQuery(id+"F0.wireOp",EDGE,"E23.38.0"),sQuery(id+"F0.wireOp",EDGE,"E23.38.1"),sQuery(id+"F0.wireOp",EDGE,"E23.38.2"),sQuery(id+"F0.wireOp",EDGE,"E23.38.3"),sQuery(id+"F0.wireOp",EDGE,"E23.38.4"),sQuery(id+"F0.wireOp",EDGE,"E23.38.5"),sQuery(id+"F0.wireOp",EDGE,"E23.38.6"),sQuery(id+"F0.wireOp",EDGE,"E23.38.7"),sQuery(id+"F0.wireOp",EDGE,"E23.38.8"),sQuery(id+"F0.wireOp",EDGE,"E23.38.9"),sQuery(id+"F0.wireOp",EDGE,"E23.38.10"),sQuery(id+"F0.wireOp",EDGE,"E23.38.11"),sQuery(id+"F0.wireOp",EDGE,"E23.39.0"),sQuery(id+"F0.wireOp",EDGE,"E23.39.1"),sQuery(id+"F0.wireOp",EDGE,"E23.39.2"),sQuery(id+"F0.wireOp",EDGE,"E23.39.3"),sQuery(id+"F0.wireOp",EDGE,"E23.39.4"),sQuery(id+"F0.wireOp",EDGE,"E23.39.5"),sQuery(id+"F0.wireOp",EDGE,"E23.39.6"),sQuery(id+"F0.wireOp",EDGE,"E23.39.7"),sQuery(id+"F0.wireOp",EDGE,"E23.39.8"),sQuery(id+"F0.wireOp",EDGE,"E23.39.9"),sQuery(id+"F0.wireOp",EDGE,"E23.39.10"),sQuery(id+"F0.wireOp",EDGE,"E23.39.11"),sQuery(id+"F0.wireOp",EDGE,"E23.40.0"),sQuery(id+"F0.wireOp",EDGE,"E23.40.1"),sQuery(id+"F0.wireOp",EDGE,"E23.40.2"),sQuery(id+"F0.wireOp",EDGE,"E23.40.3"),sQuery(id+"F0.wireOp",EDGE,"E23.40.4"),sQuery(id+"F0.wireOp",EDGE,"E23.40.5"),sQuery(id+"F0.wireOp",EDGE,"E23.40.6"),sQuery(id+"F0.wireOp",EDGE,"E23.40.7"),sQuery(id+"F0.wireOp",EDGE,"E23.40.8"),sQuery(id+"F0.wireOp",EDGE,"E23.40.9"),sQuery(id+"F0.wireOp",EDGE,"E23.40.10"),sQuery(id+"F0.wireOp",EDGE,"E23.40.11"),sQuery(id+"F0.wireOp",EDGE,"E23.41.0"),sQuery(id+"F0.wireOp",EDGE,"E23.41.1"),sQuery(id+"F0.wireOp",EDGE,"E23.41.2"),sQuery(id+"F0.wireOp",EDGE,"E23.41.3"),sQuery(id+"F0.wireOp",EDGE,"E23.41.4"),sQuery(id+"F0.wireOp",EDGE,"E23.41.5"),sQuery(id+"F0.wireOp",EDGE,"E23.41.6"),sQuery(id+"F0.wireOp",EDGE,"E23.41.7"),sQuery(id+"F0.wireOp",EDGE,"E23.41.8"),sQuery(id+"F0.wireOp",EDGE,"E23.41.9"),sQuery(id+"F0.wireOp",EDGE,"E23.41.10"),sQuery(id+"F0.wireOp",EDGE,"E23.41.11"),sQuery(id+"F0.wireOp",EDGE,"E23.42.0"),sQuery(id+"F0.wireOp",EDGE,"E23.42.1"),sQuery(id+"F0.wireOp",EDGE,"E23.42.2"),sQuery(id+"F0.wireOp",EDGE,"E23.42.3"),sQuery(id+"F0.wireOp",EDGE,"E23.42.4"),sQuery(id+"F0.wireOp",EDGE,"E23.42.5"),sQuery(id+"F0.wireOp",EDGE,"E23.42.6"),sQuery(id+"F0.wireOp",EDGE,"E23.42.7"),sQuery(id+"F0.wireOp",EDGE,"E23.42.8"),sQuery(id+"F0.wireOp",EDGE,"E23.42.9"),sQuery(id+"F0.wireOp",EDGE,"E23.42.10"),sQuery(id+"F0.wireOp",EDGE,"E23.42.11"),sQuery(id+"F0.wireOp",EDGE,"E23.43.0"),sQuery(id+"F0.wireOp",EDGE,"E23.43.1"),sQuery(id+"F0.wireOp",EDGE,"E23.43.2"),sQuery(id+"F0.wireOp",EDGE,"E23.43.3"),sQuery(id+"F0.wireOp",EDGE,"E23.43.4"),sQuery(id+"F0.wireOp",EDGE,"E23.43.5"),sQuery(id+"F0.wireOp",EDGE,"E23.43.6"),sQuery(id+"F0.wireOp",EDGE,"E23.43.7"),sQuery(id+"F0.wireOp",EDGE,"E23.43.8"),sQuery(id+"F0.wireOp",EDGE,"E23.43.9"),sQuery(id+"F0.wireOp",EDGE,"E23.43.10"),sQuery(id+"F0.wireOp",EDGE,"E23.43.11"),sQuery(id+"F0.wireOp",EDGE,"E23.44.0"),sQuery(id+"F0.wireOp",EDGE,"E23.44.1"),sQuery(id+"F0.wireOp",EDGE,"E23.44.2"),sQuery(id+"F0.wireOp",EDGE,"E23.44.3"),sQuery(id+"F0.wireOp",EDGE,"E23.44.4"),sQuery(id+"F0.wireOp",EDGE,"E23.44.5"),sQuery(id+"F0.wireOp",EDGE,"E23.44.6"),sQuery(id+"F0.wireOp",EDGE,"E23.44.7"),sQuery(id+"F0.wireOp",EDGE,"E23.44.8"),sQuery(id+"F0.wireOp",EDGE,"E23.44.9"),sQuery(id+"F0.wireOp",EDGE,"E23.44.10"),sQuery(id+"F0.wireOp",EDGE,"E23.44.11"),sQuery(id+"F0.wireOp",EDGE,"E23.45.0"),sQuery(id+"F0.wireOp",EDGE,"E23.45.1"),sQuery(id+"F0.wireOp",EDGE,"E23.45.2"),sQuery(id+"F0.wireOp",EDGE,"E23.45.3"),sQuery(id+"F0.wireOp",EDGE,"E23.45.4"),sQuery(id+"F0.wireOp",EDGE,"E23.45.5"),sQuery(id+"F0.wireOp",EDGE,"E23.45.6"),sQuery(id+"F0.wireOp",EDGE,"E23.45.7"),sQuery(id+"F0.wireOp",EDGE,"E23.45.8"),sQuery(id+"F0.wireOp",EDGE,"E23.45.9"),sQuery(id+"F0.wireOp",EDGE,"E23.45.10"),sQuery(id+"F0.wireOp",EDGE,"E23.45.11"),sQuery(id+"F0.wireOp",EDGE,"E23.46.0"),sQuery(id+"F0.wireOp",EDGE,"E23.46.1"),sQuery(id+"F0.wireOp",EDGE,"E23.46.2"),sQuery(id+"F0.wireOp",EDGE,"E23.46.3"),sQuery(id+"F0.wireOp",EDGE,"E23.46.4"),sQuery(id+"F0.wireOp",EDGE,"E23.46.5"),sQuery(id+"F0.wireOp",EDGE,"E23.46.6"),sQuery(id+"F0.wireOp",EDGE,"E23.46.7"),sQuery(id+"F0.wireOp",EDGE,"E23.46.8"),sQuery(id+"F0.wireOp",EDGE,"E23.46.9"),sQuery(id+"F0.wireOp",EDGE,"E23.46.10"),sQuery(id+"F0.wireOp",EDGE,"E23.46.11"),sQuery(id+"F0.wireOp",EDGE,"E23.47.0"),sQuery(id+"F0.wireOp",EDGE,"E23.47.1"),sQuery(id+"F0.wireOp",EDGE,"E23.47.2"),sQuery(id+"F0.wireOp",EDGE,"E23.47.3"),sQuery(id+"F0.wireOp",EDGE,"E23.47.4"),sQuery(id+"F0.wireOp",EDGE,"E23.47.5"),sQuery(id+"F0.wireOp",EDGE,"E23.47.6"),sQuery(id+"F0.wireOp",EDGE,"E23.47.7"),sQuery(id+"F0.wireOp",EDGE,"E23.47.8"),sQuery(id+"F0.wireOp",EDGE,"E23.47.9"),sQuery(id+"F0.wireOp",EDGE,"E23.47.10"),sQuery(id+"F0.wireOp",EDGE,"E23.47.11"),sQuery(id+"F0.wireOp",EDGE,"E23.48.0"),sQuery(id+"F0.wireOp",EDGE,"E23.48.1"),sQuery(id+"F0.wireOp",EDGE,"E23.48.2"),sQuery(id+"F0.wireOp",EDGE,"E23.48.3"),sQuery(id+"F0.wireOp",EDGE,"E23.48.4"),sQuery(id+"F0.wireOp",EDGE,"E23.48.5"),sQuery(id+"F0.wireOp",EDGE,"E23.48.6"),sQuery(id+"F0.wireOp",EDGE,"E23.48.7"),sQuery(id+"F0.wireOp",EDGE,"E23.48.8"),sQuery(id+"F0.wireOp",EDGE,"E23.48.9"),sQuery(id+"F0.wireOp",EDGE,"E23.48.10"),sQuery(id+"F0.wireOp",EDGE,"E23.48.11"),sQuery(id+"F0.wireOp",EDGE,"E23.49.0"),sQuery(id+"F0.wireOp",EDGE,"E23.49.1"),sQuery(id+"F0.wireOp",EDGE,"E23.49.2"),sQuery(id+"F0.wireOp",EDGE,"E23.49.3"),sQuery(id+"F0.wireOp",EDGE,"E23.49.4"),sQuery(id+"F0.wireOp",EDGE,"E23.49.5"),sQuery(id+"F0.wireOp",EDGE,"E23.49.6"),sQuery(id+"F0.wireOp",EDGE,"E23.49.7"),sQuery(id+"F0.wireOp",EDGE,"E23.49.8"),sQuery(id+"F0.wireOp",EDGE,"E23.49.9"),sQuery(id+"F0.wireOp",EDGE,"E23.49.10"),sQuery(id+"F0.wireOp",EDGE,"E23.49.11"),sQuery(id+"F0.wireOp",EDGE,"E23.50.0"),sQuery(id+"F0.wireOp",EDGE,"E23.50.1"),sQuery(id+"F0.wireOp",EDGE,"E23.50.2"),sQuery(id+"F0.wireOp",EDGE,"E23.50.3"),sQuery(id+"F0.wireOp",EDGE,"E23.50.4"),sQuery(id+"F0.wireOp",EDGE,"E23.50.5"),sQuery(id+"F0.wireOp",EDGE,"E23.50.6"),sQuery(id+"F0.wireOp",EDGE,"E23.50.7"),sQuery(id+"F0.wireOp",EDGE,"E23.50.8"),sQuery(id+"F0.wireOp",EDGE,"E23.50.9"),sQuery(id+"F0.wireOp",EDGE,"E23.50.10"),sQuery(id+"F0.wireOp",EDGE,"E23.50.11"),sQuery(id+"F0.wireOp",EDGE,"E23.51.0"),sQuery(id+"F0.wireOp",EDGE,"E23.51.1"),sQuery(id+"F0.wireOp",EDGE,"E23.51.2"),sQuery(id+"F0.wireOp",EDGE,"E23.51.3"),sQuery(id+"F0.wireOp",EDGE,"E23.51.4"),sQuery(id+"F0.wireOp",EDGE,"E23.51.5"),sQuery(id+"F0.wireOp",EDGE,"E23.51.6"),sQuery(id+"F0.wireOp",EDGE,"E23.51.7"),sQuery(id+"F0.wireOp",EDGE,"E23.51.8"),sQuery(id+"F0.wireOp",EDGE,"E23.51.9"),sQuery(id+"F0.wireOp",EDGE,"E23.51.10"),sQuery(id+"F0.wireOp",EDGE,"E23.51.11"),sQuery(id+"F0.wireOp",EDGE,"E23.52.0"),sQuery(id+"F0.wireOp",EDGE,"E23.52.1"),sQuery(id+"F0.wireOp",EDGE,"E23.52.2"),sQuery(id+"F0.wireOp",EDGE,"E23.52.3"),sQuery(id+"F0.wireOp",EDGE,"E23.52.4"),sQuery(id+"F0.wireOp",EDGE,"E23.52.5"),sQuery(id+"F0.wireOp",EDGE,"E23.52.6"),sQuery(id+"F0.wireOp",EDGE,"E23.52.7"),sQuery(id+"F0.wireOp",EDGE,"E23.52.8"),sQuery(id+"F0.wireOp",EDGE,"E23.52.9"),sQuery(id+"F0.wireOp",EDGE,"E23.52.10"),sQuery(id+"F0.wireOp",EDGE,"E23.52.11"),sQuery(id+"F0.wireOp",EDGE,"E23.53.0"),sQuery(id+"F0.wireOp",EDGE,"E23.53.1"),sQuery(id+"F0.wireOp",EDGE,"E23.53.2"),sQuery(id+"F0.wireOp",EDGE,"E23.53.3"),sQuery(id+"F0.wireOp",EDGE,"E23.53.4"),sQuery(id+"F0.wireOp",EDGE,"E23.53.5"),sQuery(id+"F0.wireOp",EDGE,"E23.53.6"),sQuery(id+"F0.wireOp",EDGE,"E23.53.7"),sQuery(id+"F0.wireOp",EDGE,"E23.53.8"),sQuery(id+"F0.wireOp",EDGE,"E23.53.9"),sQuery(id+"F0.wireOp",EDGE,"E23.53.10"),sQuery(id+"F0.wireOp",EDGE,"E23.53.11"),sQuery(id+"F0.wireOp",EDGE,"E23.54.0"),sQuery(id+"F0.wireOp",EDGE,"E23.54.1"),sQuery(id+"F0.wireOp",EDGE,"E23.54.2"),sQuery(id+"F0.wireOp",EDGE,"E23.54.3"),sQuery(id+"F0.wireOp",EDGE,"E23.54.4"),sQuery(id+"F0.wireOp",EDGE,"E23.54.5"),sQuery(id+"F0.wireOp",EDGE,"E23.54.6"),sQuery(id+"F0.wireOp",EDGE,"E23.54.7"),sQuery(id+"F0.wireOp",EDGE,"E23.54.8"),sQuery(id+"F0.wireOp",EDGE,"E23.54.9"),sQuery(id+"F0.wireOp",EDGE,"E23.54.10"),sQuery(id+"F0.wireOp",EDGE,"E23.54.11"),sQuery(id+"F0.wireOp",EDGE,"E23.55.0"),sQuery(id+"F0.wireOp",EDGE,"E23.55.1"),sQuery(id+"F0.wireOp",EDGE,"E23.55.2"),sQuery(id+"F0.wireOp",EDGE,"E23.55.3"),sQuery(id+"F0.wireOp",EDGE,"E23.55.4"),sQuery(id+"F0.wireOp",EDGE,"E23.55.5"),sQuery(id+"F0.wireOp",EDGE,"E23.55.6"),sQuery(id+"F0.wireOp",EDGE,"E23.55.7"),sQuery(id+"F0.wireOp",EDGE,"E23.55.8"),sQuery(id+"F0.wireOp",EDGE,"E23.55.9"),sQuery(id+"F0.wireOp",EDGE,"E23.55.10"),sQuery(id+"F0.wireOp",EDGE,"E23.55.11"),sQuery(id+"F0.wireOp",EDGE,"E23.56.0"),sQuery(id+"F0.wireOp",EDGE,"E23.56.1"),sQuery(id+"F0.wireOp",EDGE,"E23.56.2"),sQuery(id+"F0.wireOp",EDGE,"E23.56.3"),sQuery(id+"F0.wireOp",EDGE,"E23.56.4"),sQuery(id+"F0.wireOp",EDGE,"E23.56.5"),sQuery(id+"F0.wireOp",EDGE,"E23.56.6"),sQuery(id+"F0.wireOp",EDGE,"E23.56.7"),sQuery(id+"F0.wireOp",EDGE,"E23.56.8"),sQuery(id+"F0.wireOp",EDGE,"E23.56.9"),sQuery(id+"F0.wireOp",EDGE,"E23.56.10"),sQuery(id+"F0.wireOp",EDGE,"E23.56.11"),sQuery(id+"F0.wireOp",EDGE,"E23.57.0"),sQuery(id+"F0.wireOp",EDGE,"E23.57.1"),sQuery(id+"F0.wireOp",EDGE,"E23.57.2"),sQuery(id+"F0.wireOp",EDGE,"E23.57.3"),sQuery(id+"F0.wireOp",EDGE,"E23.57.4"),sQuery(id+"F0.wireOp",EDGE,"E23.57.5"),sQuery(id+"F0.wireOp",EDGE,"E23.57.6"),sQuery(id+"F0.wireOp",EDGE,"E23.57.7"),sQuery(id+"F0.wireOp",EDGE,"E23.57.8"),sQuery(id+"F0.wireOp",EDGE,"E23.57.9"),sQuery(id+"F0.wireOp",EDGE,"E23.57.10"),sQuery(id+"F0.wireOp",EDGE,"E23.57.11"),sQuery(id+"F0.wireOp",EDGE,"E23.58.0"),sQuery(id+"F0.wireOp",EDGE,"E23.58.1"),sQuery(id+"F0.wireOp",EDGE,"E23.58.2"),sQuery(id+"F0.wireOp",EDGE,"E23.58.3"),sQuery(id+"F0.wireOp",EDGE,"E23.58.4"),sQuery(id+"F0.wireOp",EDGE,"E23.58.5"),sQuery(id+"F0.wireOp",EDGE,"E23.58.6"),sQuery(id+"F0.wireOp",EDGE,"E23.58.7"),sQuery(id+"F0.wireOp",EDGE,"E23.58.8"),sQuery(id+"F0.wireOp",EDGE,"E23.58.9"),sQuery(id+"F0.wireOp",EDGE,"E23.58.10"),sQuery(id+"F0.wireOp",EDGE,"E23.58.11"),sQuery(id+"F0.wireOp",EDGE,"E23.59.0"),sQuery(id+"F0.wireOp",EDGE,"E23.59.1"),sQuery(id+"F0.wireOp",EDGE,"E23.59.2"),sQuery(id+"F0.wireOp",EDGE,"E23.59.3"),sQuery(id+"F0.wireOp",EDGE,"E23.59.4"),sQuery(id+"F0.wireOp",EDGE,"E23.59.5"),sQuery(id+"F0.wireOp",EDGE,"E23.59.6"),sQuery(id+"F0.wireOp",EDGE,"E23.59.7"),sQuery(id+"F0.wireOp",EDGE,"E23.59.8"),sQuery(id+"F0.wireOp",EDGE,"E23.59.9"),sQuery(id+"F0.wireOp",EDGE,"E23.59.10"),sQuery(id+"F0.wireOp",EDGE,"E23.59.11"),sQuery(id+"F0.wireOp",EDGE,"E23.60.0"),sQuery(id+"F0.wireOp",EDGE,"E23.60.1"),sQuery(id+"F0.wireOp",EDGE,"E23.60.2"),sQuery(id+"F0.wireOp",EDGE,"E23.60.3"),sQuery(id+"F0.wireOp",EDGE,"E23.60.4"),sQuery(id+"F0.wireOp",EDGE,"E23.60.5"),sQuery(id+"F0.wireOp",EDGE,"E23.60.6"),sQuery(id+"F0.wireOp",EDGE,"E23.60.7"),sQuery(id+"F0.wireOp",EDGE,"E23.60.8"),sQuery(id+"F0.wireOp",EDGE,"E23.60.9"),sQuery(id+"F0.wireOp",EDGE,"E23.60.10"),sQuery(id+"F0.wireOp",EDGE,"E23.60.11"),sQuery(id+"F0.wireOp",EDGE,"E23.61.0"),sQuery(id+"F0.wireOp",EDGE,"E23.61.1"),sQuery(id+"F0.wireOp",EDGE,"E23.61.2"),sQuery(id+"F0.wireOp",EDGE,"E23.61.3"),sQuery(id+"F0.wireOp",EDGE,"E23.61.4"),sQuery(id+"F0.wireOp",EDGE,"E23.61.5"),sQuery(id+"F0.wireOp",EDGE,"E23.61.6"),sQuery(id+"F0.wireOp",EDGE,"E23.61.7"),sQuery(id+"F0.wireOp",EDGE,"E23.61.8"),sQuery(id+"F0.wireOp",EDGE,"E23.61.9"),sQuery(id+"F0.wireOp",EDGE,"E23.61.10"),sQuery(id+"F0.wireOp",EDGE,"E23.61.11"),sQuery(id+"F0.wireOp",EDGE,"E23.62.0"),sQuery(id+"F0.wireOp",EDGE,"E23.62.1"),sQuery(id+"F0.wireOp",EDGE,"E23.62.2"),sQuery(id+"F0.wireOp",EDGE,"E23.62.3"),sQuery(id+"F0.wireOp",EDGE,"E23.62.4"),sQuery(id+"F0.wireOp",EDGE,"E23.62.5"),sQuery(id+"F0.wireOp",EDGE,"E23.62.6"),sQuery(id+"F0.wireOp",EDGE,"E23.62.7"),sQuery(id+"F0.wireOp",EDGE,"E23.62.8"),sQuery(id+"F0.wireOp",EDGE,"E23.62.9"),sQuery(id+"F0.wireOp",EDGE,"E23.62.10"),sQuery(id+"F0.wireOp",EDGE,"E23.62.11"),sQuery(id+"F0.wireOp",EDGE,"E23.63.0"),sQuery(id+"F0.wireOp",EDGE,"E23.63.1"),sQuery(id+"F0.wireOp",EDGE,"E23.63.2"),sQuery(id+"F0.wireOp",EDGE,"E23.63.3"),sQuery(id+"F0.wireOp",EDGE,"E23.63.4"),sQuery(id+"F0.wireOp",EDGE,"E23.63.5"),sQuery(id+"F0.wireOp",EDGE,"E23.63.6"),sQuery(id+"F0.wireOp",EDGE,"E23.63.7"),sQuery(id+"F0.wireOp",EDGE,"E23.63.8"),sQuery(id+"F0.wireOp",EDGE,"E23.63.9"),sQuery(id+"F0.wireOp",EDGE,"E23.63.10"),sQuery(id+"F0.wireOp",EDGE,"E23.63.11"),sQuery(id+"F0.wireOp",EDGE,"E23.64.0"),sQuery(id+"F0.wireOp",EDGE,"E23.64.1"),sQuery(id+"F0.wireOp",EDGE,"E23.64.2"),sQuery(id+"F0.wireOp",EDGE,"E23.64.3"),sQuery(id+"F0.wireOp",EDGE,"E23.64.4"),sQuery(id+"F0.wireOp",EDGE,"E23.64.5"),sQuery(id+"F0.wireOp",EDGE,"E23.64.6"),sQuery(id+"F0.wireOp",EDGE,"E23.64.7"),sQuery(id+"F0.wireOp",EDGE,"E23.64.8"),sQuery(id+"F0.wireOp",EDGE,"E23.64.9"),sQuery(id+"F0.wireOp",EDGE,"E23.64.10"),sQuery(id+"F0.wireOp",EDGE,"E23.64.11"),sQuery(id+"F0.wireOp",EDGE,"E23.65.0"),sQuery(id+"F0.wireOp",EDGE,"E23.65.1"),sQuery(id+"F0.wireOp",EDGE,"E23.65.2"),sQuery(id+"F0.wireOp",EDGE,"E23.65.3"),sQuery(id+"F0.wireOp",EDGE,"E23.65.4"),sQuery(id+"F0.wireOp",EDGE,"E23.65.5"),sQuery(id+"F0.wireOp",EDGE,"E23.65.6"),sQuery(id+"F0.wireOp",EDGE,"E23.65.7"),sQuery(id+"F0.wireOp",EDGE,"E23.65.8"),sQuery(id+"F0.wireOp",EDGE,"E23.65.9"),sQuery(id+"F0.wireOp",EDGE,"E23.65.10"),sQuery(id+"F0.wireOp",EDGE,"E23.65.11"),sQuery(id+"F0.wireOp",EDGE,"E23.66.0"),sQuery(id+"F0.wireOp",EDGE,"E23.66.1"),sQuery(id+"F0.wireOp",EDGE,"E23.66.2"),sQuery(id+"F0.wireOp",EDGE,"E23.66.3"),sQuery(id+"F0.wireOp",EDGE,"E23.66.4"),sQuery(id+"F0.wireOp",EDGE,"E23.66.5"),sQuery(id+"F0.wireOp",EDGE,"E23.66.6"),sQuery(id+"F0.wireOp",EDGE,"E23.66.7"),sQuery(id+"F0.wireOp",EDGE,"E23.66.8"),sQuery(id+"F0.wireOp",EDGE,"E23.66.9"),sQuery(id+"F0.wireOp",EDGE,"E23.66.10"),sQuery(id+"F0.wireOp",EDGE,"E23.66.11"),sQuery(id+"F0.wireOp",EDGE,"E23.67.0"),sQuery(id+"F0.wireOp",EDGE,"E23.67.1"),sQuery(id+"F0.wireOp",EDGE,"E23.67.2"),sQuery(id+"F0.wireOp",EDGE,"E23.67.3"),sQuery(id+"F0.wireOp",EDGE,"E23.67.4"),sQuery(id+"F0.wireOp",EDGE,"E23.67.5"),sQuery(id+"F0.wireOp",EDGE,"E23.67.6"),sQuery(id+"F0.wireOp",EDGE,"E23.67.7"),sQuery(id+"F0.wireOp",EDGE,"E23.67.8"),sQuery(id+"F0.wireOp",EDGE,"E23.67.9"),sQuery(id+"F0.wireOp",EDGE,"E23.67.10"),sQuery(id+"F0.wireOp",EDGE,"E23.67.11"),sQuery(id+"F0.wireOp",EDGE,"E23.68.0"),sQuery(id+"F0.wireOp",EDGE,"E23.68.1"),sQuery(id+"F0.wireOp",EDGE,"E23.68.2"),sQuery(id+"F0.wireOp",EDGE,"E23.68.3"),sQuery(id+"F0.wireOp",EDGE,"E23.68.4"),sQuery(id+"F0.wireOp",EDGE,"E23.68.5"),sQuery(id+"F0.wireOp",EDGE,"E23.68.6"),sQuery(id+"F0.wireOp",EDGE,"E23.68.7"),sQuery(id+"F0.wireOp",EDGE,"E23.68.8"),sQuery(id+"F0.wireOp",EDGE,"E23.68.9"),sQuery(id+"F0.wireOp",EDGE,"E23.68.10"),sQuery(id+"F0.wireOp",EDGE,"E23.68.11"),sQuery(id+"F0.wireOp",EDGE,"E23.69.0"),sQuery(id+"F0.wireOp",EDGE,"E23.69.1"),sQuery(id+"F0.wireOp",EDGE,"E23.69.2"),sQuery(id+"F0.wireOp",EDGE,"E23.69.3"),sQuery(id+"F0.wireOp",EDGE,"E23.69.4"),sQuery(id+"F0.wireOp",EDGE,"E23.69.5"),sQuery(id+"F0.wireOp",EDGE,"E23.69.6"),sQuery(id+"F0.wireOp",EDGE,"E23.69.7"),sQuery(id+"F0.wireOp",EDGE,"E23.69.8"),sQuery(id+"F0.wireOp",EDGE,"E23.69.9"),sQuery(id+"F0.wireOp",EDGE,"E23.69.10"),sQuery(id+"F0.wireOp",EDGE,"E23.69.11"),sQuery(id+"F0.wireOp",EDGE,"E23.70.0"),sQuery(id+"F0.wireOp",EDGE,"E23.70.1"),sQuery(id+"F0.wireOp",EDGE,"E23.70.2"),sQuery(id+"F0.wireOp",EDGE,"E23.70.3"),sQuery(id+"F0.wireOp",EDGE,"E23.70.4"),sQuery(id+"F0.wireOp",EDGE,"E23.70.5"),sQuery(id+"F0.wireOp",EDGE,"E23.70.6"),sQuery(id+"F0.wireOp",EDGE,"E23.70.7"),sQuery(id+"F0.wireOp",EDGE,"E23.70.8"),sQuery(id+"F0.wireOp",EDGE,"E23.70.9"),sQuery(id+"F0.wireOp",EDGE,"E23.70.10"),sQuery(id+"F0.wireOp",EDGE,"E23.70.11"),sQuery(id+"F0.wireOp",EDGE,"E23.71.0"),sQuery(id+"F0.wireOp",EDGE,"E23.71.1"),sQuery(id+"F0.wireOp",EDGE,"E23.71.2"),sQuery(id+"F0.wireOp",EDGE,"E23.71.3"),sQuery(id+"F0.wireOp",EDGE,"E23.71.4"),sQuery(id+"F0.wireOp",EDGE,"E23.71.5"),sQuery(id+"F0.wireOp",EDGE,"E23.71.6"),sQuery(id+"F0.wireOp",EDGE,"E23.71.7"),sQuery(id+"F0.wireOp",EDGE,"E23.71.8"),sQuery(id+"F0.wireOp",EDGE,"E23.71.9"),sQuery(id+"F0.wireOp",EDGE,"E23.71.10"),sQuery(id+"F0.wireOp",EDGE,"E23.71.11"),sQuery(id+"F0.wireOp",EDGE,"E24.trimOffspring"),sQuery(id+"F0.wireOp",EDGE,"E25.trimOffspring"),sQuery(id+"F0.wireOp",EDGE,"E26.trimOffspring"),sQuery(id+"F0.wireOp",EDGE,"E27.trimOffspring"),sQuery(id+"F0.wireOp",EDGE,"E28.trimOffspring"),sQuery(id+"F0.wireOp",EDGE,"E29.trimOffspring"),sQuery(id+"F0.wireOp",EDGE,"E30.trimOffspring"),sQuery(id+"F0.wireOp",EDGE,"E31.trimOffspring"),sQuery(id+"F0.wireOp",EDGE,"E32.trimOffspring"),sQuery(id+"F0.wireOp",EDGE,"E33.trimOffspring"),sQuery(id+"F0.wireOp",EDGE,"E34.trimOffspring"),sQuery(id+"F0.wireOp",EDGE,"E35.trimOffspring"),sQuery(id+"F0.wireOp",EDGE,"E36.trimOffspring"),sQuery(id+"F0.wireOp",EDGE,"E37.trimOffspring"),sQuery(id+"F0.wireOp",EDGE,"E38.trimOffspring"),sQuery(id+"F0.wireOp",EDGE,"E39.trimOffspring"),sQuery(id+"F0.wireOp",EDGE,"E40.trimOffspring"),sQuery(id+"F0.wireOp",EDGE,"E41.trimOffspring"),sQuery(id+"F0.wireOp",EDGE,"E42.trimOffspring"),sQuery(id+"F0.wireOp",EDGE,"E43.trimOffspring"),sQuery(id+"F0.wireOp",EDGE,"E44.trimOffspring"),sQuery(id+"F0.wireOp",EDGE,"E45.trimOffspring"),sQuery(id+"F0.wireOp",EDGE,"E46.trimOffspring"),sQuery(id+"F0.wireOp",EDGE,"E47.trimOffspring"),sQuery(id+"F0.wireOp",EDGE,"E48.trimOffspring"),sQuery(id+"F0.wireOp",EDGE,"E49.trimOffspring"),sQuery(id+"F0.wireOp",EDGE,"E50.trimOffspring"),sQuery(id+"F0.wireOp",EDGE,"E51.trimOffspring"),sQuery(id+"F0.wireOp",EDGE,"E52.trimOffspring"),sQuery(id+"F0.wireOp",EDGE,"E53.trimOffspring"),sQuery(id+"F0.wireOp",EDGE,"E54.trimOffspring"),sQuery(id+"F0.wireOp",EDGE,"E55.trimOffspring"),sQuery(id+"F0.wireOp",EDGE,"E56.trimOffspring"),sQuery(id+"F0.wireOp",EDGE,"E57.trimOffspring"),sQuery(id+"F0.wireOp",EDGE,"E58.trimOffspring"),sQuery(id+"F0.wireOp",EDGE,"E59.trimOffspring"),sQuery(id+"F0.wireOp",EDGE,"E60.trimOffspring"),sQuery(id+"F0.wireOp",EDGE,"E61.trimOffspring"),sQuery(id+"F0.wireOp",EDGE,"E62.trimOffspring"),sQuery(id+"F0.wireOp",EDGE,"E63.trimOffspring"),sQuery(id+"F0.wireOp",EDGE,"E64.trimOffspring"),sQuery(id+"F0.wireOp",EDGE,"E65.trimOffspring"),sQuery(id+"F0.wireOp",EDGE,"E66.trimOffspring"),sQuery(id+"F0.wireOp",EDGE,"E67.trimOffspring"),sQuery(id+"F0.wireOp",EDGE,"E68.trimOffspring"),sQuery(id+"F0.wireOp",EDGE,"E69.trimOffspring"),sQuery(id+"F0.wireOp",EDGE,"E70.trimOffspring"),sQuery(id+"F0.wireOp",EDGE,"E71.trimOffspring"),sQuery(id+"F0.wireOp",EDGE,"E72.trimOffspring"),sQuery(id+"F0.wireOp",EDGE,"E73.trimOffspring"),sQuery(id+"F0.wireOp",EDGE,"E74.trimOffspring"),sQuery(id+"F0.wireOp",EDGE,"E75.trimOffspring"),sQuery(id+"F0.wireOp",EDGE,"E76.trimOffspring"),sQuery(id+"F0.wireOp",EDGE,"E77.trimOffspring"),sQuery(id+"F0.wireOp",EDGE,"E78.trimOffspring"),sQuery(id+"F0.wireOp",EDGE,"E79.trimOffspring"),sQuery(id+"F0.wireOp",EDGE,"E80.trimOffspring"),sQuery(id+"F0.wireOp",EDGE,"E81.trimOffspring"),sQuery(id+"F0.wireOp",EDGE,"E82.trimOffspring"),sQuery(id+"F0.wireOp",EDGE,"E83.trimOffspring"),sQuery(id+"F0.wireOp",EDGE,"E84.trimOffspring"),sQuery(id+"F0.wireOp",EDGE,"E85.trimOffspring"),sQuery(id+"F0.wireOp",EDGE,"E86.trimOffspring"),sQuery(id+"F0.wireOp",EDGE,"E87.trimOffspring"),sQuery(id+"F0.wireOp",EDGE,"E88.trimOffspring"),sQuery(id+"F0.wireOp",EDGE,"E89.trimOffspring"),sQuery(id+"F0.wireOp",EDGE,"E90.trimOffspring"),sQuery(id+"F0.wireOp",EDGE,"E91.trimOffspring"),sQuery(id+"F0.wireOp",EDGE,"E92.trimOffspring"),sQuery(id+"F0.wireOp",EDGE,"E93.trimOffspring"),sQuery(id+"F0.wireOp",EDGE,"E94")])],"isStart":false});
            var sketch = newSketch(context, id + "F17", { "sketchPlane" : qUnion([Q0])});
            skCircle(sketch, "E131", {"center": v(0, 0) * mm, "radius": 78.32 * mm});
            skCircle(sketch, "E132", {"center": v(0, 0) * mm, "radius": 60 * mm});
            skSolve(sketch);
        }
        {
            var Q0;
            Q0=qSketchRegion(id+"F17",true);
            extrude(context, id + "F18", {"entities" : qUnion([Q0]), "depth" : 2 * mm});
        }
        {
            var Q0;
            Q0=qCreatedBy(makeId("Top.planeOp"),FACE);
            var sketch = newSketch(context, id + "F19", { "sketchPlane" : qUnion([Q0])});
            skLineSegment(sketch, "E133", {"start": v(-94.1, -24.5) * mm, "end": v(-94.1, 5) * mm});
            skLineSegment(sketch, "E134.0", {"start": v(0, 5) * mm, "end": v(-94.1, 5) * mm});
            skLineSegment(sketch, "E135", {"start": v(0, 0) * mm, "end": v(0, -36.97) * mm, "construction": true});
            skLineSegment(sketch, "E136", {"start": v(0, -36.97) * mm, "end": v(0, 38.4) * mm, "construction": true});
            skPoint(sketch, "E137.orphan", {"position": v(94.1, 5) * mm});
            skLineSegment(sketch, "E138", {"start": v(-94.1, -24.5) * mm, "end": v(-119.1, -24.5) * mm, "construction": true});
            skLineSegment(sketch, "E139", {"start": v(-119.1, -13.62) * mm, "end": v(-119.1, -13.62) * mm});
            skLineSegment(sketch, "E140", {"start": v(-119.1, 13.78) * mm, "end": v(0, 13.78) * mm});
            skLineSegment(sketch, "E141", {"start": v(0, 13.78) * mm, "end": v(0, 5) * mm});
            skLineSegment(sketch, "E142", {"start": v(0, 70.76) * mm, "end": v(-156.4, 69.09) * mm});
            skLineSegment(sketch, "E143", {"start": v(-184.8, 68.79) * mm, "end": v(-185.03, 89.7) * mm});
            skLineSegment(sketch, "E144", {"start": v(-185.03, 89.7) * mm, "end": v(0, 91.67) * mm});
            skLineSegment(sketch, "E145", {"start": v(0, 91.67) * mm, "end": v(0, 70.76) * mm});
            skLineSegment(sketch, "E146.trimOffspring", {"start": v(-119.1, -5) * mm, "end": v(-119.1, -5) * mm});
            skLineSegment(sketch, "E147.trimOffspring", {"start": v(-119.1, 10.78) * mm, "end": v(-119.1, 13.78) * mm});
            skLineSegment(sketch, "E148", {"start": v(-119.1, 13.78) * mm, "end": v(-119.1, -24.5) * mm, "construction": true});
            skFitSpline(sketch, "E149", {"points": [v(-119.1, -24.5) * mm, v(-123.4, -18.21) * mm, v(-124.37, -13.3) * mm, v(-119.1, -9.17) * mm], "startDerivative": vector(0, 40.05) * mm, "endDerivative": vector(19.92, 9.69) * mm});
            skFitSpline(sketch, "E150", {"points": [v(-119.1, -9.17) * mm, v(-124.37, -3.83) * mm, v(-119.1, 0.42) * mm], "startDerivative": vector(-26.91, -1.33) * mm, "endDerivative": vector(21.81, 2.56) * mm});
            skFitSpline(sketch, "E151", {"points": [v(-119.1, 0.42) * mm, v(-123.7, 6.81) * mm, v(-119.1, 13.78) * mm], "startDerivative": vector(-21.56, -2.53) * mm, "endDerivative": vector(0, 17.75) * mm});
            skFitSpline(sketch, "E152", {"points": [v(-119.1, -24.5) * mm, v(-112.18, -30.44) * mm, v(-104.72, -30.86) * mm, v(-98.59, -28.95) * mm, v(-94.1, -24.5) * mm], "startDerivative": vector(0, -37.62) * mm, "endDerivative": vector(3.35, 30.01) * mm});
            skLineSegment(sketch, "E153", {"start": v(-119.1, 13.78) * mm, "end": v(-115, 8.25) * mm});
            skLineSegment(sketch, "E154", {"start": v(-115, 8.25) * mm, "end": v(-112.63, 10) * mm});
            skLineSegment(sketch, "E155", {"start": v(-112.63, 10) * mm, "end": v(-161.1, 75.42) * mm});
            skPoint(sketch, "E155.endSnap0", {"position": v(-161.1, 69.4) * mm});
            skFitSpline(sketch, "E156", {"points": [v(-119.1, 13.78) * mm, v(-126.5, 15.52) * mm, v(-126.2, 24.14) * mm], "startDerivative": vector(-18.73, 0.6) * mm, "endDerivative": vector(5.36, 17.58) * mm});
            skFitSpline(sketch, "E157", {"points": [v(-126.2, 24.14) * mm, v(-133.24, 24.14) * mm, v(-132.55, 31.93) * mm], "startDerivative": vector(-18.11, -3.9) * mm, "endDerivative": vector(4.44, 21.12) * mm});
            skFitSpline(sketch, "E158", {"points": [v(-132.55, 31.93) * mm, v(-139.25, 31.93) * mm, v(-138.96, 40.59) * mm], "startDerivative": vector(-20.16, -4.1) * mm, "endDerivative": vector(6.7, 21.45) * mm});
            skFitSpline(sketch, "E159", {"points": [v(-138.96, 40.59) * mm, v(-145.78, 40.4) * mm, v(-144.9, 48.6) * mm], "startDerivative": vector(-23.93, -7.42) * mm, "endDerivative": vector(11.81, 23.27) * mm});
            skFitSpline(sketch, "E160", {"points": [v(-144.9, 48.6) * mm, v(-152.71, 49.59) * mm, v(-151.46, 57.46) * mm], "startDerivative": vector(-20.2, -1.51) * mm, "endDerivative": vector(6.66, 19.6) * mm});
            skFitSpline(sketch, "E161", {"points": [v(-151.46, 57.46) * mm, v(-158.95, 57.46) * mm, v(-157.1, 65.07) * mm], "startDerivative": vector(-20.57, -3.7) * mm, "endDerivative": vector(9.66, 18.45) * mm});
            skFitSpline(sketch, "E162", {"points": [v(-157.1, 65.07) * mm, v(-164.82, 65.07) * mm, v(-163.6, 73.84) * mm], "startDerivative": vector(-21.96, -4.23) * mm, "endDerivative": vector(8.74, 21.63) * mm});
            skLineSegment(sketch, "E163", {"start": v(-170.47, 72.4) * mm, "end": v(-122.82, 10.63) * mm, "construction": true});
            skLineSegment(sketch, "E164", {"start": v(-161.1, 75.42) * mm, "end": v(-163.6, 73.84) * mm});
            skLineSegment(sketch, "E165", {"start": v(-156.4, 69.09) * mm, "end": v(-184.8, 68.79) * mm});
            skSolve(sketch);
        }
        {
            var Q0;
            Q0=makeQuery(id+"F19.imprint","IMPRINT",FACE,{"disambiguationData":[TD([[makeQuery(id+"F19.imprint","IMPRINT",EDGE,{"derivedFrom":sQuery(id+"F19.wireOp",EDGE,"E133")}),1.0]])]});
            var Q1;
            Q1=sQuery(id+"F19.wireOp",EDGE,"E136");
            revolve(context, id + "F20", {"entities" : qUnion([Q0]), "axis" : qUnion([Q1]), "revolveType" : RevolveType.FULL});
        }
        {
            var Q0;
            {var subQ0=sQuery(id+"F19.wireOp",EDGE,"E156");Q0=makeQuery(id+"F19.imprint","IMPRINT",FACE,{"disambiguationData":[TD([[makeQuery(id+"F19.imprint","IMPRINT",EDGE,{"derivedFrom":subQ0}),-1.0]])]});}
            var Q1;
            {var subQ0=sQuery(id+"F19.wireOp",EDGE,"E153");Q1=makeQuery(id+"F19.imprint","IMPRINT",FACE,{"disambiguationData":[TD([[makeQuery(id+"F19.imprint","IMPRINT",EDGE,{"derivedFrom":subQ0}),1.0]])]});}
            var Q2;
            {var subQ5=sQuery(id+"F19.wireOp",EDGE,"E164");Q2=makeQuery(id+"F19.imprint","IMPRINT",FACE,{"disambiguationData":[TD([[makeQuery(id+"F19.imprint","IMPRINT",EDGE,{"derivedFrom":subQ5}),1.0]])]});}
            var Q3;
            Q3=sQuery(id+"F19.wireOp",EDGE,"E155");
            revolve(context, id + "F21", {"entities" : qUnion([Q0, Q1, Q2]), "axis" : qUnion([Q3]), "revolveType" : RevolveType.FULL});
        }
        {
            var Q0;
            Q0=makeQuery(id+"F21.opRevolve","SWEPT_BODY",BODY,{"disambiguationData":[OSD([sQuery(id+"F19.wireOp",EDGE,"E153"),sQuery(id+"F19.wireOp",EDGE,"E154"),sQuery(id+"F19.wireOp",EDGE,"E155"),sQuery(id+"F19.wireOp",EDGE,"E156"),sQuery(id+"F19.wireOp",EDGE,"E157"),sQuery(id+"F19.wireOp",EDGE,"E158"),sQuery(id+"F19.wireOp",EDGE,"E159"),sQuery(id+"F19.wireOp",EDGE,"E160"),sQuery(id+"F19.wireOp",EDGE,"E161"),sQuery(id+"F19.wireOp",EDGE,"E162"),sQuery(id+"F19.wireOp",EDGE,"E164")])]});
            var Q1;
            Q1=sQuery(id+"F19.wireOp",EDGE,"E136");
            var Q2;
            Q2=makeQuery(id+"F20.opRevolve","SWEPT_BODY",BODY,{"disambiguationData":[OSD([sQuery(id+"F19.wireOp",EDGE,"E133"),sQuery(id+"F19.wireOp",EDGE,"E134.0"),sQuery(id+"F19.wireOp",EDGE,"E138"),sQuery(id+"F19.wireOp",EDGE,"E139"),sQuery(id+"F19.wireOp",EDGE,"E140"),sQuery(id+"F19.wireOp",EDGE,"E141")])]});
            circularPattern(context, id + "F22", {"entities" : qUnion([Q0]), "axis" : qUnion([Q1]), "angle" : 360 * degree, "instanceCount" : 4, "equalSpace" : true});
        }
        {
            var Q0;
            {var subQ3=sQuery(id+"F19.wireOp",EDGE,"E142");Q0=makeQuery(id+"F19.imprint","IMPRINT",FACE,{"disambiguationData":[TD([[makeQuery(id+"F19.imprint","IMPRINT",EDGE,{"derivedFrom":subQ3}),-1.0]])]});}
            var Q1;
            {var subQ3=sQuery(id+"F19.wireOp",EDGE,"E164");Q1=makeQuery(id+"F19.imprint","IMPRINT",FACE,{"disambiguationData":[TD([[makeQuery(id+"F19.imprint","IMPRINT",EDGE,{"derivedFrom":subQ3}),1.0]])]});}
            var Q2;
            Q2=sQuery(id+"F19.wireOp",EDGE,"E145");
            revolve(context, id + "F23", {"operationType" : NewBodyOperationType.REMOVE, "entities" : qUnion([Q0, Q1]), "axis" : qUnion([Q2]), "revolveType" : RevolveType.FULL, "oppositeDirection" : true});
        }
        {
            var Q0;
            {var subQ0=sQuery(id+"F19.wireOp",EDGE,"E139");var subQ1=makeQuery(id+"F21.opRevolve","SWEPT_FACE",FACE,{"disambiguationData":[OSD([sQuery(id+"F19.wireOp",EDGE,"98eac7df-80cc-4f42-b12e-d95ddb8a739b")])]});var subQ2=sQuery(id+"F19.wireOp",EDGE,"E140");Q0=makeQuery(id+"F22.boolean.opBoolean","SPLIT",EDGE,{"disambiguationData":[TD([makeQuery(id+"F20.opRevolve","SWEPT_FACE",FACE,{"disambiguationData":[OSD([subQ0])]}),makeQuery(id+"F20.opRevolve","SWEPT_FACE",FACE,{"disambiguationData":[OSD([subQ2])]}),makeQuery(id+"F22.opPattern","COPY",FACE,{"derivedFrom":subQ1,"instanceName":"2"}),makeQuery(id+"F22.opPattern","COPY",FACE,{"derivedFrom":subQ1,"instanceName":"3"})])],"derivedFrom":makeQuery(id+"F20.opRevolve","SWEPT_EDGE",EDGE,{"disambiguationData":[OSD([subQ0,subQ2])]})});}
            var Q1;
            {var subQ0=sQuery(id+"F19.wireOp",EDGE,"E139");var subQ1=makeQuery(id+"F21.opRevolve","SWEPT_FACE",FACE,{"disambiguationData":[OSD([sQuery(id+"F19.wireOp",EDGE,"98eac7df-80cc-4f42-b12e-d95ddb8a739b")])]});var subQ2=sQuery(id+"F19.wireOp",EDGE,"E140");Q1=makeQuery(id+"F22.boolean.opBoolean","SPLIT",EDGE,{"disambiguationData":[TD([makeQuery(id+"F20.opRevolve","SWEPT_FACE",FACE,{"disambiguationData":[OSD([subQ0])]}),makeQuery(id+"F20.opRevolve","SWEPT_FACE",FACE,{"disambiguationData":[OSD([subQ2])]}),subQ1,makeQuery(id+"F22.opPattern","COPY",FACE,{"derivedFrom":subQ1,"instanceName":"3"})])],"derivedFrom":makeQuery(id+"F20.opRevolve","SWEPT_EDGE",EDGE,{"disambiguationData":[OSD([subQ0,subQ2])]})});}
            var Q2;
            {var subQ0=sQuery(id+"F19.wireOp",EDGE,"E139");var subQ1=sQuery(id+"F19.wireOp",EDGE,"E140");var subQ2=makeQuery(id+"F21.opRevolve","SWEPT_FACE",FACE,{"disambiguationData":[OSD([sQuery(id+"F19.wireOp",EDGE,"98eac7df-80cc-4f42-b12e-d95ddb8a739b")])]});Q2=makeQuery(id+"F22.boolean.opBoolean","SPLIT",EDGE,{"disambiguationData":[TD([makeQuery(id+"F20.opRevolve","SWEPT_FACE",FACE,{"disambiguationData":[OSD([subQ0])]}),makeQuery(id+"F20.opRevolve","SWEPT_FACE",FACE,{"disambiguationData":[OSD([subQ1])]}),subQ2,makeQuery(id+"F22.opPattern","COPY",FACE,{"derivedFrom":subQ2,"instanceName":"1"})])],"derivedFrom":makeQuery(id+"F20.opRevolve","SWEPT_EDGE",EDGE,{"disambiguationData":[OSD([subQ0,subQ1])]})});}
            var Q3;
            {var subQ0=sQuery(id+"F19.wireOp",EDGE,"E139");var subQ1=sQuery(id+"F19.wireOp",EDGE,"E140");var subQ2=makeQuery(id+"F21.opRevolve","SWEPT_FACE",FACE,{"disambiguationData":[OSD([sQuery(id+"F19.wireOp",EDGE,"98eac7df-80cc-4f42-b12e-d95ddb8a739b")])]});Q3=makeQuery(id+"F22.boolean.opBoolean","SPLIT",EDGE,{"disambiguationData":[TD([makeQuery(id+"F20.opRevolve","SWEPT_FACE",FACE,{"disambiguationData":[OSD([subQ0])]}),makeQuery(id+"F20.opRevolve","SWEPT_FACE",FACE,{"disambiguationData":[OSD([subQ1])]}),makeQuery(id+"F22.opPattern","COPY",FACE,{"derivedFrom":subQ2,"instanceName":"1"}),makeQuery(id+"F22.opPattern","COPY",FACE,{"derivedFrom":subQ2,"instanceName":"2"})])],"derivedFrom":makeQuery(id+"F20.opRevolve","SWEPT_EDGE",EDGE,{"disambiguationData":[OSD([subQ0,subQ1])]})});}
            var Q4;
            Q4=makeQuery(id+"F20.opRevolve","SWEPT_EDGE",EDGE,{"disambiguationData":[OSD([sQuery(id+"F19.wireOp",EDGE,"E138"),sQuery(id+"F19.wireOp",EDGE,"E139")])]});
            fillet(context, id + "F24", {"entities" : qUnion([Q0, Q1, Q2, Q3, Q4]), "radius" : 5 * mm, "tangentPropagation" : true, "allowEdgeOverflow" : false});
        }
        {
            var Q0;
            Q0=makeQuery(id+"F19.imprint","IMPRINT",FACE,{"disambiguationData":[TD([[makeQuery(id+"F19.imprint","IMPRINT",EDGE,{"derivedFrom":sQuery(id+"F19.wireOp",EDGE,"E133")}),1.0]])]});
            var Q1;
            Q1=sQuery(id+"F19.wireOp",EDGE,"E136");
            revolve(context, id + "F25", {"entities" : qUnion([Q0]), "axis" : qUnion([Q1]), "revolveType" : RevolveType.FULL});
        }
        {
            var Q0;
            Q0=qCreatedBy(makeId("Top.planeOp"),FACE);
            var sketch = newSketch(context, id + "F26", { "sketchPlane" : qUnion([Q0])});
            skLineSegment(sketch, "E166.0", {"start": v(116.38, -24.5) * mm, "end": v(101.38, -24.5) * mm});
            skLineSegment(sketch, "E167.0", {"start": v(119.1, -24.5) * mm, "end": v(0, -24.5) * mm});
            skLineSegment(sketch, "E168", {"start": v(119.1, -24.5) * mm, "end": v(119.1, -124.5) * mm, "construction": true});
            skLineSegment(sketch, "E169", {"start": v(0, 0) * mm, "end": v(0, -77.2) * mm, "construction": true});
            skLineSegment(sketch, "E170", {"start": v(101.38, -24.5) * mm, "end": v(116.38, -24.5) * mm});
            skLineSegment(sketch, "E171.trimOffspring", {"start": v(0, -24.5) * mm, "end": v(-119.1, -24.5) * mm});
            skFitSpline(sketch, "E172", {"points": [v(101.38, -24.5) * mm, v(113.27, -72.28) * mm, v(115.69, -113.87) * mm, v(101.38, -150.6) * mm, v(75.96, -174.46) * mm, v(42.05, -195.8) * mm, v(25.73, -203.02) * mm, v(0, -208.98) * mm], "startDerivative": vector(0, -296.49) * mm, "endDerivative": vector(-223.24, -42.07) * mm});
            skFitSpline(sketch, "E173.0", {"points": [v(116.38, -24.5) * mm, v(116.38, -26.73) * mm, v(116.76, -31.33) * mm, v(118.34, -38.77) * mm, v(120.74, -46.73) * mm, v(123.15, -53.78) * mm, v(124.89, -58.94) * mm, v(125.86, -61.96) * mm, v(126.58, -64.27) * mm, v(127.15, -66.22) * mm, v(127.6, -67.8) * mm, v(128.03, -69.4) * mm, v(128.54, -71.4) * mm, v(129.3, -74.6) * mm, v(130.1, -78.6) * mm, v(130.88, -83.42) * mm, v(131.45, -88.23) * mm, v(131.92, -94.64) * mm, v(131.99, -102.66) * mm, v(131.22, -112.24) * mm, v(129.6, -121.76) * mm, v(127.16, -131.11) * mm, v(123.96, -140.18) * mm, v(120.67, -147.4) * mm, v(117.67, -152.94) * mm, v(115.23, -156.94) * mm, v(112.59, -160.8) * mm, v(109.8, -164.41) * mm, v(106.86, -167.83) * mm, v(103.8, -171.04) * mm, v(100.65, -174.07) * mm, v(97.4, -176.95) * mm, v(94.06, -179.7) * mm, v(90.64, -182.34) * mm, v(87.15, -184.92) * mm, v(83.58, -187.45) * mm, v(79.9, -189.99) * mm, v(74.89, -193.35) * mm, v(68.52, -197.48) * mm, v(62.28, -201.35) * mm, v(57.51, -204.22) * mm, v(54.08, -206.23) * mm, v(51.38, -207.78) * mm, v(49.32, -208.92) * mm, v(47.32, -210.02) * mm, v(44.91, -211.3) * mm, v(42.08, -212.7) * mm, v(39.24, -214) * mm, v(36.36, -215.2) * mm, v(33.41, -216.3) * mm, v(29.36, -217.64) * mm, v(23.98, -219.16) * mm, v(17.11, -220.81) * mm, v(9.98, -222.34) * mm, v(5.16, -223.27) * mm, v(2.78, -223.72) * mm]});
            skLineSegment(sketch, "E174", {"start": v(0, -193.04) * mm, "end": v(0, -259.57) * mm, "construction": true});
            skLineSegment(sketch, "E175.left", {"start": v(6.35, -193.22) * mm, "end": v(6.35, -233.98) * mm});
            skLineSegment(sketch, "E176.bottom", {"start": v(12.5, -233.98) * mm, "end": v(6.35, -233.98) * mm});
            skLineSegment(sketch, "E176.top", {"start": v(12.5, -193.22) * mm, "end": v(6.35, -193.22) * mm});
            skLineSegment(sketch, "E176.left", {"start": v(12.5, -233.98) * mm, "end": v(12.5, -193.22) * mm});
            skLineSegment(sketch, "E177", {"start": v(6.35, -233.98) * mm, "end": v(0, -233.98) * mm, "construction": true});
            skLineSegment(sketch, "E178", {"start": v(6.35, -193.22) * mm, "end": v(0, -193.04) * mm, "construction": true});
            skFitSpline(sketch, "E179.MirrorCS", {"points": [v(-101.38, -24.5) * mm, v(-113.27, -72.28) * mm, v(-115.69, -113.87) * mm, v(-101.38, -150.6) * mm, v(-75.96, -174.46) * mm, v(-42.05, -195.8) * mm, v(-25.73, -203.02) * mm, v(0, -208.98) * mm], "startDerivative": vector(0, -296.49) * mm, "endDerivative": vector(223.24, -42.07) * mm});
            skLineSegment(sketch, "E180.MirrorCS", {"start": v(-116.38, -24.5) * mm, "end": v(-101.38, -24.5) * mm});
            skFitSpline(sketch, "E181.0", {"points": [v(-116.38, -24.5) * mm, v(-116.38, -26.73) * mm, v(-116.76, -31.33) * mm, v(-118.34, -38.77) * mm, v(-120.74, -46.73) * mm, v(-123.15, -53.78) * mm, v(-124.89, -58.94) * mm, v(-125.86, -61.96) * mm, v(-126.58, -64.27) * mm, v(-127.15, -66.22) * mm, v(-127.6, -67.8) * mm, v(-128.03, -69.4) * mm, v(-128.54, -71.4) * mm, v(-129.3, -74.6) * mm, v(-130.1, -78.6) * mm, v(-130.88, -83.42) * mm, v(-131.45, -88.23) * mm, v(-131.92, -94.64) * mm, v(-131.99, -102.66) * mm, v(-131.22, -112.24) * mm, v(-129.6, -121.76) * mm, v(-127.16, -131.11) * mm, v(-123.96, -140.18) * mm, v(-120.67, -147.4) * mm, v(-117.67, -152.94) * mm, v(-115.23, -156.94) * mm, v(-112.59, -160.8) * mm, v(-109.8, -164.41) * mm, v(-106.86, -167.83) * mm, v(-103.8, -171.04) * mm, v(-100.65, -174.07) * mm, v(-97.4, -176.95) * mm, v(-94.06, -179.7) * mm, v(-90.64, -182.34) * mm, v(-87.15, -184.92) * mm, v(-83.58, -187.45) * mm, v(-79.9, -189.99) * mm, v(-74.89, -193.35) * mm, v(-68.52, -197.48) * mm, v(-62.28, -201.35) * mm, v(-57.51, -204.22) * mm, v(-54.08, -206.23) * mm, v(-51.38, -207.78) * mm, v(-49.32, -208.92) * mm, v(-47.32, -210.02) * mm, v(-44.91, -211.3) * mm, v(-42.08, -212.7) * mm, v(-39.24, -214) * mm, v(-36.36, -215.2) * mm, v(-33.41, -216.3) * mm, v(-29.36, -217.64) * mm, v(-23.98, -219.16) * mm, v(-17.11, -220.81) * mm, v(-9.98, -222.34) * mm, v(-5.16, -223.27) * mm, v(-2.78, -223.72) * mm]});
            skPoint(sketch, "E182.orphan", {"position": v(-119.1, -24.5) * mm});
            skLineSegment(sketch, "E183.trimOffspring", {"start": v(-101.38, -24.5) * mm, "end": v(-116.38, -24.5) * mm});
            skLineSegment(sketch, "E184.MirrorCS", {"start": v(-6.35, -193.22) * mm, "end": v(-6.35, -233.98) * mm});
            skLineSegment(sketch, "E185", {"start": v(-8.1, -222.7) * mm, "end": v(-6.35, -223.14) * mm});
            skSolve(sketch);
        }
        {
            var Q0;
            {var subQ5=sQuery(id+"F26.wireOp",EDGE,"E176.top");Q0=makeQuery(id+"F26.imprint","IMPRINT",FACE,{"disambiguationData":[TD([[makeQuery(id+"F26.imprint","IMPRINT",EDGE,{"derivedFrom":subQ5}),1.0]])]});}
            var Q1;
            {var subQ5=sQuery(id+"F26.wireOp",EDGE,"E176.bottom");Q1=makeQuery(id+"F26.imprint","IMPRINT",FACE,{"disambiguationData":[TD([[makeQuery(id+"F26.imprint","IMPRINT",EDGE,{"derivedFrom":subQ5}),-1.0]])]});}
            var Q2;
            {var subQ0=sQuery(id+"F26.wireOp",EDGE,"E175.left");var subQ1=sQuery(id+"F26.wireOp",EDGE,"E172");var subQ2=makeQuery(id+"F26.imprint","INTERSECT",VERTEX,{"derivedFrom":[subQ1,subQ0]});Q2=makeQuery(id+"F26.imprint","IMPRINT",FACE,{"disambiguationData":[TD([[makeQuery(id+"F26.imprint","IMPRINT",EDGE,{"disambiguationData":[TD([[subQ2,1.0]])],"derivedFrom":subQ1}),1.0]])]});}
            var Q3;
            Q3=sQuery(id+"F26.wireOp",EDGE,"E174");
            revolve(context, id + "F27", {"entities" : qUnion([Q0, Q1, Q2]), "axis" : qUnion([Q3]), "revolveType" : RevolveType.FULL});
        }
        {
            var Q0;
            {var subQ1=sQuery(id+"F26.wireOp",EDGE,"E179.MirrorCS");Q0=makeQuery(id+"F26.imprint","IMPRINT",FACE,{"disambiguationData":[TD([[makeQuery(id+"F26.imprint","IMPRINT",EDGE,{"derivedFrom":subQ1}),-1.0]])]});}
            var Q1;
            {var subQ0=sQuery(id+"F26.wireOp",EDGE,"E170");Q1=makeQuery(id+"F26.imprint","IMPRINT",FACE,{"disambiguationData":[TD([[makeQuery(id+"F26.imprint","IMPRINT",EDGE,{"derivedFrom":subQ0}),-1.0]])]});}
            var Q2;
            {var subQ0=sQuery(id+"F26.wireOp",EDGE,"E175.left");var subQ1=sQuery(id+"F26.wireOp",EDGE,"E172");var subQ2=makeQuery(id+"F26.imprint","INTERSECT",VERTEX,{"derivedFrom":[subQ1,subQ0]});Q2=makeQuery(id+"F26.imprint","IMPRINT",FACE,{"disambiguationData":[TD([[makeQuery(id+"F26.imprint","IMPRINT",EDGE,{"disambiguationData":[TD([[subQ2,1.0]])],"derivedFrom":subQ1}),1.0]])]});}
            extrude(context, id + "F28", {"entities" : qUnion([Q0, Q1, Q2]), "operationType" : NewBodyOperationType.ADD, "depth" : 15 * mm, "symmetric" : true});
        }
        {
            var Q0;
            Q0=makeQuery(id+"F27.opRevolve","SWEPT_EDGE",EDGE,{"disambiguationData":[OSD([sQuery(id+"F26.wireOp",EDGE,"E176.bottom"),sQuery(id+"F26.wireOp",EDGE,"E176.left")])]});
            var Q1;
            Q1=makeQuery(id+"F27.opRevolve","SWEPT_EDGE",EDGE,{"disambiguationData":[OSD([sQuery(id+"F26.wireOp",EDGE,"E176.top"),sQuery(id+"F26.wireOp",EDGE,"E176.left")])]});
            fillet(context, id + "F29", {"entities" : qUnion([Q0, Q1]), "radius" : 5 * mm, "tangentPropagation" : true, "allowEdgeOverflow" : false});
        }
    });
